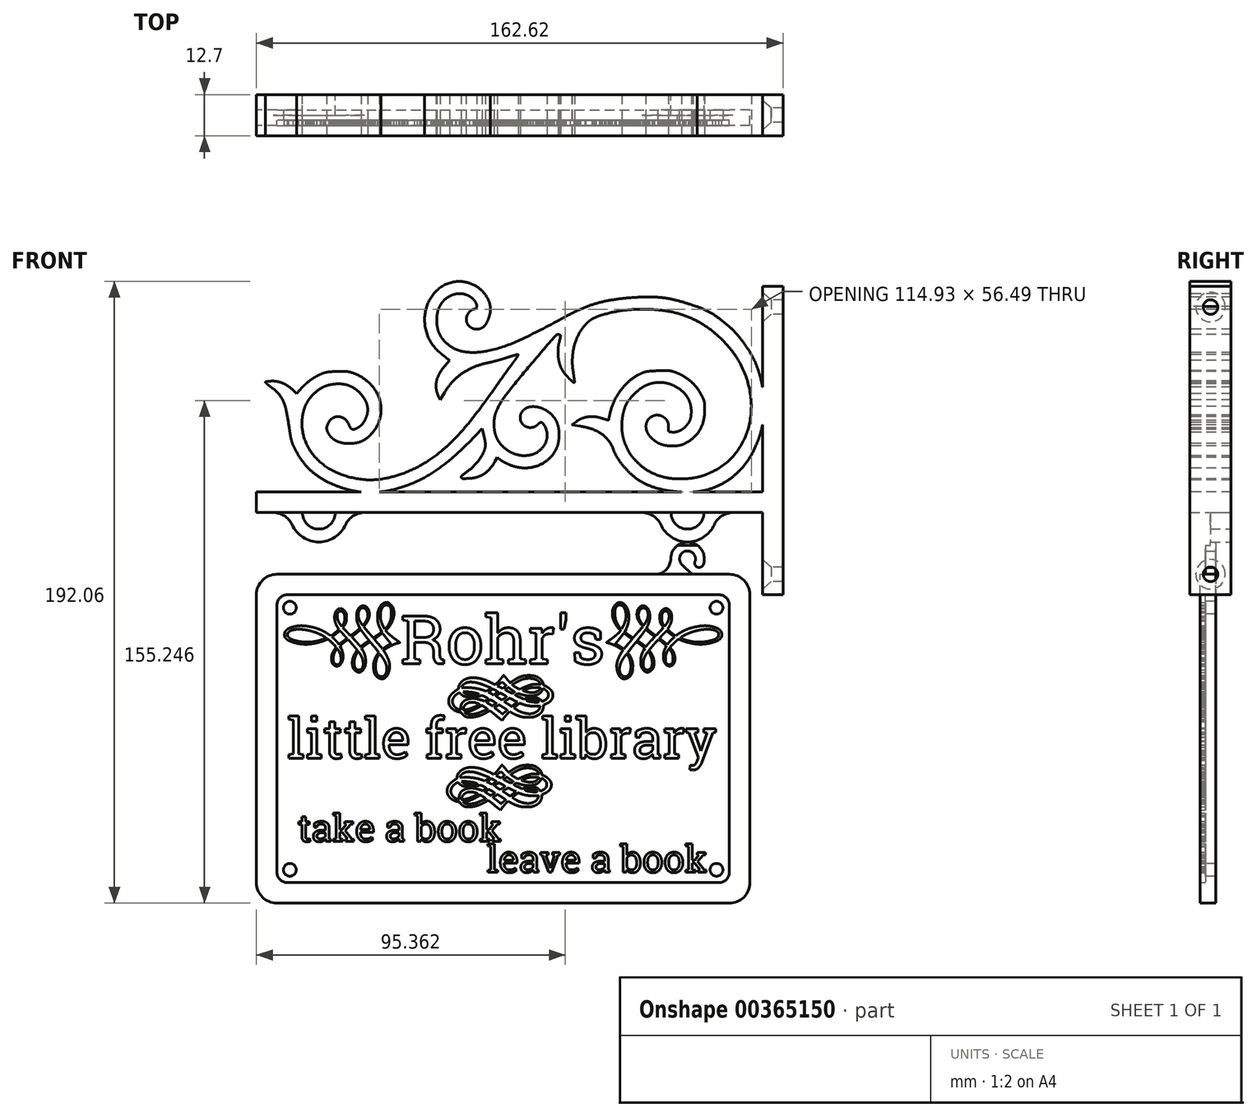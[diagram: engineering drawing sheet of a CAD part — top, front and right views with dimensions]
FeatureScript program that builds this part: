
annotation { "Feature Type Name" : "Feature", "Feature Type Description" : "" }
export const myFeature = defineFeature(function(context is Context, id is Id, definition is map)
    precondition{}
    {
        {
            var Q0;
            Q0=qCreatedBy(makeId("Front.planeOp"),FACE);
            var sketch = newSketch(context, id + "F0", { "sketchPlane" : qUnion([Q0])});
            skLineSegment(sketch, "E0.bottom", {"start": v(-69.85, 50.8) * mm, "end": v(69.85, 50.8) * mm});
            skLineSegment(sketch, "E0.top", {"start": v(-69.85, -50.8) * mm, "end": v(69.85, -50.8) * mm});
            skLineSegment(sketch, "E0.left", {"start": v(-76.2, 44.45) * mm, "end": v(-76.2, -44.45) * mm});
            skLineSegment(sketch, "E0.right", {"start": v(76.2, 44.45) * mm, "end": v(76.2, -44.45) * mm});
            skPoint(sketch, "E0.middle", {"position": v(0, 0) * mm});
            skPoint(sketch, "E1.visualSharp", {"position": v(-76.2, 50.8) * mm});
            skArc(sketch, "E1.filletArc", {"start": v(-69.85, 50.8) * mm, "mid": v(-74.34, 48.94) * mm, "end": v(-76.2, 44.45) * mm});
            skPoint(sketch, "E2.visualSharp", {"position": v(76.2, 50.8) * mm});
            skArc(sketch, "E2.filletArc", {"start": v(76.2, 44.45) * mm, "mid": v(74.34, 48.94) * mm, "end": v(69.85, 50.8) * mm});
            skPoint(sketch, "E3.visualSharp", {"position": v(76.2, -50.8) * mm});
            skArc(sketch, "E3.filletArc", {"start": v(69.85, -50.8) * mm, "mid": v(74.34, -48.94) * mm, "end": v(76.2, -44.45) * mm});
            skPoint(sketch, "E4.visualSharp", {"position": v(-76.2, -50.8) * mm});
            skArc(sketch, "E4.filletArc", {"start": v(-76.2, -44.45) * mm, "mid": v(-74.34, -48.94) * mm, "end": v(-69.85, -50.8) * mm});
            skSolve(sketch);
        }
        {
            var Q0;
            Q0=makeQuery(id+"F0.imprint","IMPRINT",FACE,{"disambiguationData":[TD([[makeQuery(id+"F0.imprint","IMPRINT",EDGE,{"derivedFrom":sQuery(id+"F0.wireOp",EDGE,"E0.bottom")}),-1.0]])]});
            extrude(context, id + "F1", {"entities" : qUnion([Q0]), "endBound" : BoundingType.SYMMETRIC, "depth" : 3.17 * mm, "offsetDistance" : 25.4 * mm});
        }
        {
            var Q0;
            Q0=makeQuery(id+"F1.opExtrude","CAP_FACE",FACE,{"disambiguationData":[OSD([sQuery(id+"F0.wireOp",EDGE,"E0.bottom"),sQuery(id+"F0.wireOp",EDGE,"E0.top"),sQuery(id+"F0.wireOp",EDGE,"E0.left"),sQuery(id+"F0.wireOp",EDGE,"E0.right"),sQuery(id+"F0.wireOp",EDGE,"E1.filletArc"),sQuery(id+"F0.wireOp",EDGE,"E2.filletArc"),sQuery(id+"F0.wireOp",EDGE,"E3.filletArc"),sQuery(id+"F0.wireOp",EDGE,"E4.filletArc")])],"isStart":false});
            var sketch = newSketch(context, id + "F2", { "sketchPlane" : qUnion([Q0])});
            skLineSegment(sketch, "E5.bottom", {"start": v(-66.67, 44.45) * mm, "end": v(66.67, 44.45) * mm});
            skLineSegment(sketch, "E5.top", {"start": v(-66.67, -44.45) * mm, "end": v(66.67, -44.45) * mm});
            skLineSegment(sketch, "E5.left", {"start": v(-69.85, 41.28) * mm, "end": v(-69.85, -41.27) * mm});
            skLineSegment(sketch, "E5.right", {"start": v(69.85, 41.28) * mm, "end": v(69.85, -41.27) * mm});
            skPoint(sketch, "E5.middle", {"position": v(0, 0) * mm});
            skPoint(sketch, "E6.visualSharp", {"position": v(-69.85, 44.45) * mm});
            skArc(sketch, "E6.filletArc", {"start": v(-66.67, 44.45) * mm, "mid": v(-68.92, 43.52) * mm, "end": v(-69.85, 41.28) * mm});
            skPoint(sketch, "E7.visualSharp", {"position": v(69.85, 44.45) * mm});
            skArc(sketch, "E7.filletArc", {"start": v(69.85, 41.28) * mm, "mid": v(68.92, 43.52) * mm, "end": v(66.67, 44.45) * mm});
            skPoint(sketch, "E8.visualSharp", {"position": v(69.85, -44.45) * mm});
            skArc(sketch, "E8.filletArc", {"start": v(66.67, -44.45) * mm, "mid": v(68.92, -43.52) * mm, "end": v(69.85, -41.27) * mm});
            skPoint(sketch, "E9.visualSharp", {"position": v(-69.85, -44.45) * mm});
            skArc(sketch, "E9.filletArc", {"start": v(-69.85, -41.27) * mm, "mid": v(-68.92, -43.52) * mm, "end": v(-66.67, -44.45) * mm});
            skSolve(sketch);
        }
        {
            var Q0;
            Q0=makeQuery(id+"F2.imprint","IMPRINT",FACE,{"disambiguationData":[TD([[makeQuery(id+"F2.imprint","IMPRINT",EDGE,{"derivedFrom":sQuery(id+"F2.wireOp",EDGE,"E5.bottom")}),1.0]])]});
            extrude(context, id + "F3", {"entities" : qUnion([Q0]), "operationType" : NewBodyOperationType.ADD, "depth" : 1.59 * mm, "offsetDistance" : 25.4 * mm});
        }
        {
            var Q0;
            Q0=makeQuery(id+"F1.opExtrude","CAP_FACE",FACE,{"disambiguationData":[OSD([sQuery(id+"F0.wireOp",EDGE,"E0.bottom"),sQuery(id+"F0.wireOp",EDGE,"E0.top"),sQuery(id+"F0.wireOp",EDGE,"E0.left"),sQuery(id+"F0.wireOp",EDGE,"E0.right"),sQuery(id+"F0.wireOp",EDGE,"E1.filletArc"),sQuery(id+"F0.wireOp",EDGE,"E2.filletArc"),sQuery(id+"F0.wireOp",EDGE,"E3.filletArc"),sQuery(id+"F0.wireOp",EDGE,"E4.filletArc")])],"isStart":false});
            var sketch = newSketch(context, id + "F4", { "sketchPlane" : qUnion([Q0])});
            skLineSegment(sketch, "E10", {"start": v(0, 0) * mm, "end": v(0, 25.75) * mm, "construction": true});
            skArc(sketch, "E11", {"start": v(-36.9, 41.88) * mm, "mid": v(-37.36, 41.59) * mm, "end": v(-37.75, 41.2) * mm});
            skArc(sketch, "E12", {"start": v(-37.75, 41.2) * mm, "mid": v(-38.1, 40.67) * mm, "end": v(-38.38, 40.1) * mm});
            skArc(sketch, "E13", {"start": v(-38.38, 40.1) * mm, "mid": v(-38.6, 39.42) * mm, "end": v(-38.75, 38.7) * mm});
            skArc(sketch, "E14", {"start": v(-38.75, 38.7) * mm, "mid": v(-38.82, 37.9) * mm, "end": v(-38.8, 37.1) * mm});
            skArc(sketch, "E15", {"start": v(-38.8, 37.1) * mm, "mid": v(-38.78, 36.68) * mm, "end": v(-38.72, 36.26) * mm});
            skArc(sketch, "E16", {"start": v(-38.72, 36.26) * mm, "mid": v(-38.65, 35.87) * mm, "end": v(-38.56, 35.49) * mm});
            skArc(sketch, "E17", {"start": v(-38.56, 35.49) * mm, "mid": v(-38.44, 35.1) * mm, "end": v(-38.3, 34.7) * mm});
            skArc(sketch, "E18", {"start": v(-38.3, 34.7) * mm, "mid": v(-38.1, 34.27) * mm, "end": v(-37.9, 33.83) * mm});
            skLineSegment(sketch, "E19", {"start": v(-37.9, 33.83) * mm, "end": v(-37.5, 32.99) * mm});
            skLineSegment(sketch, "E20", {"start": v(-37.5, 32.99) * mm, "end": v(-37.74, 32.8) * mm});
            skArc(sketch, "E21", {"start": v(-37.74, 32.8) * mm, "mid": v(-38, 32.6) * mm, "end": v(-38.27, 32.4) * mm});
            skArc(sketch, "E22", {"start": v(-38.27, 32.4) * mm, "mid": v(-38.7, 32.12) * mm, "end": v(-39.12, 31.84) * mm});
            skArc(sketch, "E23", {"start": v(-39.12, 31.84) * mm, "mid": v(-39.59, 31.53) * mm, "end": v(-40.05, 31.23) * mm});
            skArc(sketch, "E24", {"start": v(-40.05, 31.23) * mm, "mid": v(-40.1, 31.21) * mm, "end": v(-40.15, 31.22) * mm});
            skArc(sketch, "E25", {"start": v(-40.15, 31.22) * mm, "mid": v(-40.18, 31.23) * mm, "end": v(-40.2, 31.25) * mm});
            skArc(sketch, "E26", {"start": v(-40.2, 31.25) * mm, "mid": v(-40.41, 31.5) * mm, "end": v(-40.62, 31.74) * mm});
            skArc(sketch, "E27", {"start": v(-40.62, 31.74) * mm, "mid": v(-40.86, 32.01) * mm, "end": v(-41.1, 32.29) * mm});
            skArc(sketch, "E28", {"start": v(-41.1, 32.29) * mm, "mid": v(-41.38, 32.61) * mm, "end": v(-41.66, 32.94) * mm});
            skLineSegment(sketch, "E29", {"start": v(-41.66, 32.94) * mm, "end": v(-43.09, 34.63) * mm});
            skLineSegment(sketch, "E30", {"start": v(-43.09, 34.63) * mm, "end": v(-42.74, 35.06) * mm});
            skArc(sketch, "E31", {"start": v(-42.74, 35.06) * mm, "mid": v(-42.33, 35.6) * mm, "end": v(-41.96, 36.17) * mm});
            skArc(sketch, "E32", {"start": v(-41.96, 36.17) * mm, "mid": v(-41.7, 36.7) * mm, "end": v(-41.49, 37.24) * mm});
            skArc(sketch, "E33", {"start": v(-41.49, 37.24) * mm, "mid": v(-41.36, 37.75) * mm, "end": v(-41.3, 38.28) * mm});
            skArc(sketch, "E34", {"start": v(-41.3, 38.28) * mm, "mid": v(-41.32, 38.78) * mm, "end": v(-41.4, 39.28) * mm});
            skArc(sketch, "E35", {"start": v(-41.4, 39.28) * mm, "mid": v(-41.49, 39.56) * mm, "end": v(-41.6, 39.84) * mm});
            skArc(sketch, "E36", {"start": v(-41.6, 39.84) * mm, "mid": v(-41.7, 40.07) * mm, "end": v(-41.84, 40.29) * mm});
            skArc(sketch, "E37", {"start": v(-41.84, 40.29) * mm, "mid": v(-41.98, 40.47) * mm, "end": v(-42.14, 40.63) * mm});
            skArc(sketch, "E38", {"start": v(-42.14, 40.63) * mm, "mid": v(-42.32, 40.77) * mm, "end": v(-42.51, 40.88) * mm});
            skArc(sketch, "E39", {"start": v(-42.51, 40.88) * mm, "mid": v(-42.7, 40.96) * mm, "end": v(-42.9, 41.03) * mm});
            skArc(sketch, "E40", {"start": v(-42.9, 41.03) * mm, "mid": v(-43.07, 41.06) * mm, "end": v(-43.25, 41.07) * mm});
            skArc(sketch, "E41", {"start": v(-43.25, 41.07) * mm, "mid": v(-43.42, 41.06) * mm, "end": v(-43.6, 41.02) * mm});
            skArc(sketch, "E42", {"start": v(-43.6, 41.02) * mm, "mid": v(-43.8, 40.95) * mm, "end": v(-43.99, 40.86) * mm});
            skArc(sketch, "E43", {"start": v(-43.99, 40.86) * mm, "mid": v(-44.28, 40.67) * mm, "end": v(-44.53, 40.41) * mm});
            skArc(sketch, "E44", {"start": v(-44.53, 40.41) * mm, "mid": v(-44.76, 40.08) * mm, "end": v(-44.95, 39.7) * mm});
            skArc(sketch, "E45", {"start": v(-44.95, 39.7) * mm, "mid": v(-45.1, 39.26) * mm, "end": v(-45.2, 38.79) * mm});
            skArc(sketch, "E46", {"start": v(-45.2, 38.79) * mm, "mid": v(-45.27, 38.25) * mm, "end": v(-45.3, 37.7) * mm});
            skArc(sketch, "E47", {"start": v(-45.3, 37.7) * mm, "mid": v(-45.29, 37.34) * mm, "end": v(-45.26, 36.98) * mm});
            skArc(sketch, "E48", {"start": v(-45.26, 36.98) * mm, "mid": v(-45.2, 36.64) * mm, "end": v(-45.14, 36.3) * mm});
            skArc(sketch, "E49", {"start": v(-45.14, 36.3) * mm, "mid": v(-45.04, 35.97) * mm, "end": v(-44.93, 35.63) * mm});
            skArc(sketch, "E50", {"start": v(-44.93, 35.63) * mm, "mid": v(-44.78, 35.27) * mm, "end": v(-44.6, 34.9) * mm});
            skLineSegment(sketch, "E51", {"start": v(-44.6, 34.9) * mm, "end": v(-44.22, 34.12) * mm});
            skLineSegment(sketch, "E52", {"start": v(-44.22, 34.12) * mm, "end": v(-44.73, 33.68) * mm});
            skArc(sketch, "E53", {"start": v(-44.73, 33.68) * mm, "mid": v(-44.86, 33.57) * mm, "end": v(-45, 33.47) * mm});
            skArc(sketch, "E54", {"start": v(-45, 33.47) * mm, "mid": v(-45.19, 33.32) * mm, "end": v(-45.38, 33.16) * mm});
            skArc(sketch, "E55", {"start": v(-45.38, 33.16) * mm, "mid": v(-45.59, 33) * mm, "end": v(-45.8, 32.83) * mm});
            skArc(sketch, "E56", {"start": v(-45.8, 32.83) * mm, "mid": v(-46, 32.68) * mm, "end": v(-46.2, 32.53) * mm});
            skArc(sketch, "E57", {"start": v(-46.2, 32.53) * mm, "mid": v(-46.45, 32.34) * mm, "end": v(-46.7, 32.16) * mm});
            skArc(sketch, "E58", {"start": v(-46.7, 32.16) * mm, "mid": v(-46.84, 32.07) * mm, "end": v(-46.98, 31.98) * mm});
            skArc(sketch, "E59", {"start": v(-46.98, 31.98) * mm, "mid": v(-47.07, 31.93) * mm, "end": v(-47.17, 31.9) * mm});
            skArc(sketch, "E60", {"start": v(-47.17, 31.9) * mm, "mid": v(-47.22, 31.9) * mm, "end": v(-47.27, 31.93) * mm});
            skArc(sketch, "E61", {"start": v(-47.27, 31.93) * mm, "mid": v(-47.31, 31.97) * mm, "end": v(-47.36, 32.02) * mm});
            skArc(sketch, "E62", {"start": v(-47.36, 32.02) * mm, "mid": v(-47.51, 32.19) * mm, "end": v(-47.67, 32.35) * mm});
            skArc(sketch, "E63", {"start": v(-47.67, 32.35) * mm, "mid": v(-47.85, 32.55) * mm, "end": v(-48.04, 32.75) * mm});
            skArc(sketch, "E64", {"start": v(-48.04, 32.75) * mm, "mid": v(-48.25, 32.97) * mm, "end": v(-48.46, 33.2) * mm});
            skLineSegment(sketch, "E65", {"start": v(-48.46, 33.2) * mm, "end": v(-49.53, 34.33) * mm});
            skLineSegment(sketch, "E66", {"start": v(-49.53, 34.33) * mm, "end": v(-49.19, 34.78) * mm});
            skArc(sketch, "E67", {"start": v(-49.19, 34.78) * mm, "mid": v(-48.98, 35.07) * mm, "end": v(-48.8, 35.37) * mm});
            skArc(sketch, "E68", {"start": v(-48.8, 35.37) * mm, "mid": v(-48.67, 35.66) * mm, "end": v(-48.56, 35.96) * mm});
            skArc(sketch, "E69", {"start": v(-48.56, 35.96) * mm, "mid": v(-48.48, 36.29) * mm, "end": v(-48.42, 36.62) * mm});
            skArc(sketch, "E70", {"start": v(-48.42, 36.62) * mm, "mid": v(-48.39, 37.04) * mm, "end": v(-48.38, 37.45) * mm});
            skArc(sketch, "E71", {"start": v(-48.38, 37.45) * mm, "mid": v(-48.38, 37.75) * mm, "end": v(-48.38, 38.05) * mm});
            skArc(sketch, "E72", {"start": v(-48.38, 38.05) * mm, "mid": v(-48.4, 38.23) * mm, "end": v(-48.42, 38.4) * mm});
            skArc(sketch, "E73", {"start": v(-48.42, 38.4) * mm, "mid": v(-48.44, 38.54) * mm, "end": v(-48.48, 38.68) * mm});
            skArc(sketch, "E74", {"start": v(-48.48, 38.68) * mm, "mid": v(-48.54, 38.82) * mm, "end": v(-48.6, 38.97) * mm});
            skArc(sketch, "E75", {"start": v(-48.6, 38.97) * mm, "mid": v(-48.73, 39.18) * mm, "end": v(-48.85, 39.38) * mm});
            skArc(sketch, "E76", {"start": v(-48.85, 39.38) * mm, "mid": v(-48.97, 39.54) * mm, "end": v(-49.1, 39.68) * mm});
            skArc(sketch, "E77", {"start": v(-49.1, 39.68) * mm, "mid": v(-49.23, 39.8) * mm, "end": v(-49.37, 39.9) * mm});
            skArc(sketch, "E78", {"start": v(-49.37, 39.9) * mm, "mid": v(-49.54, 40.01) * mm, "end": v(-49.72, 40.1) * mm});
            skArc(sketch, "E79", {"start": v(-49.72, 40.1) * mm, "mid": v(-49.92, 40.18) * mm, "end": v(-50.13, 40.23) * mm});
            skArc(sketch, "E80", {"start": v(-50.13, 40.23) * mm, "mid": v(-50.32, 40.24) * mm, "end": v(-50.5, 40.23) * mm});
            skArc(sketch, "E81", {"start": v(-50.5, 40.23) * mm, "mid": v(-50.7, 40.17) * mm, "end": v(-50.87, 40.09) * mm});
            skArc(sketch, "E82", {"start": v(-50.87, 40.09) * mm, "mid": v(-51.07, 39.96) * mm, "end": v(-51.25, 39.81) * mm});
            skArc(sketch, "E83", {"start": v(-51.25, 39.81) * mm, "mid": v(-51.64, 39.34) * mm, "end": v(-51.89, 38.79) * mm});
            skArc(sketch, "E84", {"start": v(-51.89, 38.79) * mm, "mid": v(-52.04, 38.07) * mm, "end": v(-52.07, 37.34) * mm});
            skArc(sketch, "E85", {"start": v(-52.07, 37.34) * mm, "mid": v(-51.98, 36.52) * mm, "end": v(-51.77, 35.73) * mm});
            skArc(sketch, "E86", {"start": v(-51.77, 35.73) * mm, "mid": v(-51.46, 34.97) * mm, "end": v(-51.04, 34.26) * mm});
            skLineSegment(sketch, "E87", {"start": v(-51.04, 34.26) * mm, "end": v(-50.7, 33.78) * mm});
            skLineSegment(sketch, "E88", {"start": v(-50.7, 33.78) * mm, "end": v(-51.26, 33.3) * mm});
            skArc(sketch, "E89", {"start": v(-51.26, 33.3) * mm, "mid": v(-51.39, 33.18) * mm, "end": v(-51.52, 33.07) * mm});
            skArc(sketch, "E90", {"start": v(-51.52, 33.07) * mm, "mid": v(-51.69, 32.94) * mm, "end": v(-51.85, 32.8) * mm});
            skArc(sketch, "E91", {"start": v(-51.85, 32.8) * mm, "mid": v(-52.03, 32.67) * mm, "end": v(-52.2, 32.54) * mm});
            skArc(sketch, "E92", {"start": v(-52.2, 32.54) * mm, "mid": v(-52.37, 32.42) * mm, "end": v(-52.52, 32.3) * mm});
            skLineSegment(sketch, "E93", {"start": v(-52.52, 32.3) * mm, "end": v(-53.25, 31.8) * mm});
            skLineSegment(sketch, "E94", {"start": v(-53.25, 31.8) * mm, "end": v(-54.37, 32.55) * mm});
            skArc(sketch, "E95", {"start": v(-54.37, 32.55) * mm, "mid": v(-55.03, 32.97) * mm, "end": v(-55.72, 33.33) * mm});
            skArc(sketch, "E96", {"start": v(-55.72, 33.33) * mm, "mid": v(-56.45, 33.67) * mm, "end": v(-57.2, 33.95) * mm});
            skArc(sketch, "E97", {"start": v(-57.2, 33.95) * mm, "mid": v(-58.01, 34.22) * mm, "end": v(-58.85, 34.43) * mm});
            skArc(sketch, "E98", {"start": v(-58.85, 34.43) * mm, "mid": v(-59.79, 34.63) * mm, "end": v(-60.73, 34.79) * mm});
            skArc(sketch, "E99", {"start": v(-60.73, 34.79) * mm, "mid": v(-61.26, 34.85) * mm, "end": v(-61.78, 34.9) * mm});
            skArc(sketch, "E100", {"start": v(-61.78, 34.9) * mm, "mid": v(-62.29, 34.9) * mm, "end": v(-62.79, 34.9) * mm});
            skArc(sketch, "E101", {"start": v(-62.79, 34.9) * mm, "mid": v(-63.28, 34.86) * mm, "end": v(-63.77, 34.8) * mm});
            skArc(sketch, "E102", {"start": v(-63.77, 34.8) * mm, "mid": v(-64.28, 34.7) * mm, "end": v(-64.78, 34.6) * mm});
            skArc(sketch, "E103", {"start": v(-64.78, 34.6) * mm, "mid": v(-65.27, 34.45) * mm, "end": v(-65.75, 34.3) * mm});
            skArc(sketch, "E104", {"start": v(-65.75, 34.3) * mm, "mid": v(-66.11, 34.14) * mm, "end": v(-66.46, 33.95) * mm});
            skArc(sketch, "E105", {"start": v(-66.46, 33.95) * mm, "mid": v(-66.73, 33.75) * mm, "end": v(-66.98, 33.52) * mm});
            skArc(sketch, "E106", {"start": v(-66.98, 33.52) * mm, "mid": v(-67.19, 33.26) * mm, "end": v(-67.36, 32.98) * mm});
            skArc(sketch, "E107", {"start": v(-67.36, 32.98) * mm, "mid": v(-67.45, 32.78) * mm, "end": v(-67.5, 32.57) * mm});
            skArc(sketch, "E108", {"start": v(-67.5, 32.57) * mm, "mid": v(-67.53, 32.32) * mm, "end": v(-67.54, 32.06) * mm});
            skArc(sketch, "E109", {"start": v(-67.54, 32.06) * mm, "mid": v(-67.52, 31.82) * mm, "end": v(-67.48, 31.57) * mm});
            skArc(sketch, "E110", {"start": v(-67.48, 31.57) * mm, "mid": v(-67.43, 31.4) * mm, "end": v(-67.33, 31.23) * mm});
            skArc(sketch, "E111", {"start": v(-67.33, 31.23) * mm, "mid": v(-66.8, 30.66) * mm, "end": v(-66.12, 30.26) * mm});
            skArc(sketch, "E112", {"start": v(-66.12, 30.26) * mm, "mid": v(-65.05, 29.85) * mm, "end": v(-63.95, 29.55) * mm});
            skArc(sketch, "E113", {"start": v(-63.95, 29.55) * mm, "mid": v(-62.7, 29.31) * mm, "end": v(-61.44, 29.2) * mm});
            skArc(sketch, "E114", {"start": v(-61.44, 29.2) * mm, "mid": v(-60.25, 29.2) * mm, "end": v(-59.07, 29.33) * mm});
            skArc(sketch, "E115", {"start": v(-59.07, 29.33) * mm, "mid": v(-58.52, 29.42) * mm, "end": v(-57.97, 29.53) * mm});
            skArc(sketch, "E116", {"start": v(-57.97, 29.53) * mm, "mid": v(-57.44, 29.65) * mm, "end": v(-56.92, 29.78) * mm});
            skArc(sketch, "E117", {"start": v(-56.92, 29.78) * mm, "mid": v(-56.44, 29.92) * mm, "end": v(-55.96, 30.07) * mm});
            skArc(sketch, "E118", {"start": v(-55.96, 30.07) * mm, "mid": v(-55.53, 30.23) * mm, "end": v(-55.1, 30.4) * mm});
            skArc(sketch, "E119", {"start": v(-55.1, 30.4) * mm, "mid": v(-54.8, 30.52) * mm, "end": v(-54.5, 30.64) * mm});
            skArc(sketch, "E120", {"start": v(-54.5, 30.64) * mm, "mid": v(-54.37, 30.69) * mm, "end": v(-54.24, 30.72) * mm});
            skArc(sketch, "E121", {"start": v(-54.24, 30.72) * mm, "mid": v(-54.16, 30.72) * mm, "end": v(-54.09, 30.7) * mm});
            skArc(sketch, "E122", {"start": v(-54.09, 30.7) * mm, "mid": v(-54, 30.67) * mm, "end": v(-53.93, 30.62) * mm});
            skArc(sketch, "E123", {"start": v(-53.93, 30.62) * mm, "mid": v(-53.71, 30.43) * mm, "end": v(-53.5, 30.24) * mm});
            skArc(sketch, "E124", {"start": v(-53.5, 30.24) * mm, "mid": v(-53.25, 30) * mm, "end": v(-53, 29.77) * mm});
            skArc(sketch, "E125", {"start": v(-53, 29.77) * mm, "mid": v(-52.74, 29.53) * mm, "end": v(-52.5, 29.28) * mm});
            skArc(sketch, "E126", {"start": v(-52.5, 29.28) * mm, "mid": v(-52.29, 29.07) * mm, "end": v(-52.09, 28.85) * mm});
            skLineSegment(sketch, "E127", {"start": v(-52.09, 28.85) * mm, "end": v(-51.55, 28.28) * mm});
            skLineSegment(sketch, "E128", {"start": v(-51.55, 28.28) * mm, "end": v(-51.96, 27.74) * mm});
            skArc(sketch, "E129", {"start": v(-51.96, 27.74) * mm, "mid": v(-52.24, 27.34) * mm, "end": v(-52.49, 26.92) * mm});
            skArc(sketch, "E130", {"start": v(-52.49, 26.92) * mm, "mid": v(-52.69, 26.5) * mm, "end": v(-52.84, 26.06) * mm});
            skArc(sketch, "E131", {"start": v(-52.84, 26.06) * mm, "mid": v(-52.96, 25.63) * mm, "end": v(-53.02, 25.2) * mm});
            skArc(sketch, "E132", {"start": v(-53.02, 25.2) * mm, "mid": v(-53.04, 24.75) * mm, "end": v(-53.02, 24.31) * mm});
            skArc(sketch, "E133", {"start": v(-53.02, 24.31) * mm, "mid": v(-52.93, 23.82) * mm, "end": v(-52.75, 23.34) * mm});
            skArc(sketch, "E134", {"start": v(-52.75, 23.34) * mm, "mid": v(-52.52, 22.97) * mm, "end": v(-52.2, 22.68) * mm});
            skArc(sketch, "E135", {"start": v(-52.2, 22.68) * mm, "mid": v(-51.85, 22.5) * mm, "end": v(-51.46, 22.43) * mm});
            skArc(sketch, "E136", {"start": v(-51.46, 22.43) * mm, "mid": v(-51.04, 22.48) * mm, "end": v(-50.64, 22.62) * mm});
            skArc(sketch, "E137", {"start": v(-50.64, 22.62) * mm, "mid": v(-50.38, 22.8) * mm, "end": v(-50.17, 23.03) * mm});
            skArc(sketch, "E138", {"start": v(-50.17, 23.03) * mm, "mid": v(-49.95, 23.36) * mm, "end": v(-49.78, 23.7) * mm});
            skArc(sketch, "E139", {"start": v(-49.78, 23.7) * mm, "mid": v(-49.63, 24.13) * mm, "end": v(-49.52, 24.57) * mm});
            skArc(sketch, "E140", {"start": v(-49.52, 24.57) * mm, "mid": v(-49.45, 25.03) * mm, "end": v(-49.43, 25.5) * mm});
            skArc(sketch, "E141", {"start": v(-49.43, 25.5) * mm, "mid": v(-49.45, 25.8) * mm, "end": v(-49.48, 26.1) * mm});
            skArc(sketch, "E142", {"start": v(-49.48, 26.1) * mm, "mid": v(-49.55, 26.46) * mm, "end": v(-49.64, 26.82) * mm});
            skArc(sketch, "E143", {"start": v(-49.64, 26.82) * mm, "mid": v(-49.74, 27.19) * mm, "end": v(-49.86, 27.55) * mm});
            skArc(sketch, "E144", {"start": v(-49.86, 27.55) * mm, "mid": v(-49.99, 27.87) * mm, "end": v(-50.13, 28.18) * mm});
            skLineSegment(sketch, "E145", {"start": v(-50.13, 28.18) * mm, "end": v(-50.42, 28.74) * mm});
            skLineSegment(sketch, "E146", {"start": v(-50.42, 28.74) * mm, "end": v(-50.05, 29.04) * mm});
            skArc(sketch, "E147", {"start": v(-50.05, 29.04) * mm, "mid": v(-49.95, 29.12) * mm, "end": v(-49.85, 29.2) * mm});
            skArc(sketch, "E148", {"start": v(-49.85, 29.2) * mm, "mid": v(-49.7, 29.33) * mm, "end": v(-49.54, 29.46) * mm});
            skArc(sketch, "E149", {"start": v(-49.54, 29.46) * mm, "mid": v(-49.36, 29.6) * mm, "end": v(-49.17, 29.74) * mm});
            skArc(sketch, "E150", {"start": v(-49.17, 29.74) * mm, "mid": v(-49, 29.88) * mm, "end": v(-48.81, 30.02) * mm});
            skLineSegment(sketch, "E151", {"start": v(-48.81, 30.02) * mm, "end": v(-47.94, 30.7) * mm});
            skLineSegment(sketch, "E152", {"start": v(-47.94, 30.7) * mm, "end": v(-47.2, 29.86) * mm});
            skArc(sketch, "E153", {"start": v(-47.2, 29.86) * mm, "mid": v(-46.91, 29.54) * mm, "end": v(-46.63, 29.22) * mm});
            skArc(sketch, "E154", {"start": v(-46.63, 29.22) * mm, "mid": v(-46.32, 28.87) * mm, "end": v(-46.02, 28.52) * mm});
            skArc(sketch, "E155", {"start": v(-46.02, 28.52) * mm, "mid": v(-45.75, 28.2) * mm, "end": v(-45.48, 27.89) * mm});
            skArc(sketch, "E156", {"start": v(-45.48, 27.89) * mm, "mid": v(-45.34, 27.72) * mm, "end": v(-45.2, 27.55) * mm});
            skArc(sketch, "E157", {"start": v(-45.2, 27.55) * mm, "mid": v(-45.18, 27.5) * mm, "end": v(-45.16, 27.43) * mm});
            skArc(sketch, "E158", {"start": v(-45.16, 27.43) * mm, "mid": v(-45.16, 27.36) * mm, "end": v(-45.18, 27.3) * mm});
            skArc(sketch, "E159", {"start": v(-45.18, 27.3) * mm, "mid": v(-45.22, 27.2) * mm, "end": v(-45.27, 27.1) * mm});
            skArc(sketch, "E160", {"start": v(-45.27, 27.1) * mm, "mid": v(-45.38, 26.93) * mm, "end": v(-45.5, 26.76) * mm});
            skArc(sketch, "E161", {"start": v(-45.5, 26.76) * mm, "mid": v(-45.78, 26.3) * mm, "end": v(-46.03, 25.84) * mm});
            skArc(sketch, "E162", {"start": v(-46.03, 25.84) * mm, "mid": v(-46.23, 25.39) * mm, "end": v(-46.39, 24.92) * mm});
            skArc(sketch, "E163", {"start": v(-46.39, 24.92) * mm, "mid": v(-46.5, 24.46) * mm, "end": v(-46.57, 23.99) * mm});
            skArc(sketch, "E164", {"start": v(-46.57, 23.99) * mm, "mid": v(-46.6, 23.5) * mm, "end": v(-46.58, 23.02) * mm});
            skArc(sketch, "E165", {"start": v(-46.58, 23.02) * mm, "mid": v(-46.53, 22.6) * mm, "end": v(-46.43, 22.17) * mm});
            skArc(sketch, "E166", {"start": v(-46.43, 22.17) * mm, "mid": v(-46.28, 21.81) * mm, "end": v(-46.09, 21.48) * mm});
            skArc(sketch, "E167", {"start": v(-46.09, 21.48) * mm, "mid": v(-45.86, 21.2) * mm, "end": v(-45.58, 20.95) * mm});
            skArc(sketch, "E168", {"start": v(-45.58, 20.95) * mm, "mid": v(-45.26, 20.75) * mm, "end": v(-44.91, 20.6) * mm});
            skArc(sketch, "E169", {"start": v(-44.91, 20.6) * mm, "mid": v(-44.64, 20.54) * mm, "end": v(-44.35, 20.54) * mm});
            skArc(sketch, "E170", {"start": v(-44.35, 20.54) * mm, "mid": v(-44.06, 20.61) * mm, "end": v(-43.8, 20.74) * mm});
            skArc(sketch, "E171", {"start": v(-43.8, 20.74) * mm, "mid": v(-43.52, 20.95) * mm, "end": v(-43.29, 21.2) * mm});
            skArc(sketch, "E172", {"start": v(-43.29, 21.2) * mm, "mid": v(-43.05, 21.53) * mm, "end": v(-42.86, 21.9) * mm});
            skArc(sketch, "E173", {"start": v(-42.86, 21.9) * mm, "mid": v(-42.76, 22.1) * mm, "end": v(-42.67, 22.3) * mm});
            skArc(sketch, "E174", {"start": v(-42.67, 22.3) * mm, "mid": v(-42.61, 22.47) * mm, "end": v(-42.57, 22.63) * mm});
            skArc(sketch, "E175", {"start": v(-42.57, 22.63) * mm, "mid": v(-42.54, 22.82) * mm, "end": v(-42.52, 23) * mm});
            skArc(sketch, "E176", {"start": v(-42.52, 23) * mm, "mid": v(-42.5, 23.32) * mm, "end": v(-42.49, 23.64) * mm});
            skArc(sketch, "E177", {"start": v(-42.49, 23.64) * mm, "mid": v(-42.48, 24.17) * mm, "end": v(-42.51, 24.7) * mm});
            skArc(sketch, "E178", {"start": v(-42.51, 24.7) * mm, "mid": v(-42.57, 25.17) * mm, "end": v(-42.66, 25.63) * mm});
            skArc(sketch, "E179", {"start": v(-42.66, 25.63) * mm, "mid": v(-42.8, 26.07) * mm, "end": v(-42.96, 26.5) * mm});
            skArc(sketch, "E180", {"start": v(-42.96, 26.5) * mm, "mid": v(-43.18, 26.96) * mm, "end": v(-43.42, 27.4) * mm});
            skLineSegment(sketch, "E181", {"start": v(-43.42, 27.4) * mm, "end": v(-43.77, 27.97) * mm});
            skLineSegment(sketch, "E182", {"start": v(-43.77, 27.97) * mm, "end": v(-43.33, 28.34) * mm});
            skArc(sketch, "E183", {"start": v(-43.33, 28.34) * mm, "mid": v(-43.22, 28.43) * mm, "end": v(-43.1, 28.52) * mm});
            skArc(sketch, "E184", {"start": v(-43.1, 28.52) * mm, "mid": v(-42.93, 28.65) * mm, "end": v(-42.76, 28.78) * mm});
            skArc(sketch, "E185", {"start": v(-42.76, 28.78) * mm, "mid": v(-42.57, 28.93) * mm, "end": v(-42.37, 29.07) * mm});
            skArc(sketch, "E186", {"start": v(-42.37, 29.07) * mm, "mid": v(-42.19, 29.2) * mm, "end": v(-42, 29.34) * mm});
            skArc(sketch, "E187", {"start": v(-42, 29.34) * mm, "mid": v(-41.78, 29.5) * mm, "end": v(-41.55, 29.66) * mm});
            skArc(sketch, "E188", {"start": v(-41.55, 29.66) * mm, "mid": v(-41.42, 29.74) * mm, "end": v(-41.28, 29.82) * mm});
            skArc(sketch, "E189", {"start": v(-41.28, 29.82) * mm, "mid": v(-41.2, 29.86) * mm, "end": v(-41.1, 29.89) * mm});
            skArc(sketch, "E190", {"start": v(-41.1, 29.89) * mm, "mid": v(-41.05, 29.88) * mm, "end": v(-41, 29.86) * mm});
            skArc(sketch, "E191", {"start": v(-41, 29.86) * mm, "mid": v(-40.97, 29.8) * mm, "end": v(-40.93, 29.76) * mm});
            skArc(sketch, "E192", {"start": v(-40.93, 29.76) * mm, "mid": v(-40.75, 29.54) * mm, "end": v(-40.57, 29.31) * mm});
            skArc(sketch, "E193", {"start": v(-40.57, 29.31) * mm, "mid": v(-40.36, 29.05) * mm, "end": v(-40.15, 28.79) * mm});
            skArc(sketch, "E194", {"start": v(-40.15, 28.79) * mm, "mid": v(-39.9, 28.49) * mm, "end": v(-39.67, 28.2) * mm});
            skLineSegment(sketch, "E195", {"start": v(-39.67, 28.2) * mm, "end": v(-38.42, 26.65) * mm});
            skLineSegment(sketch, "E196", {"start": v(-38.42, 26.65) * mm, "end": v(-38.72, 26.28) * mm});
            skArc(sketch, "E197", {"start": v(-38.72, 26.28) * mm, "mid": v(-38.9, 26.04) * mm, "end": v(-39.05, 25.8) * mm});
            skArc(sketch, "E198", {"start": v(-39.05, 25.8) * mm, "mid": v(-39.21, 25.5) * mm, "end": v(-39.36, 25.2) * mm});
            skArc(sketch, "E199", {"start": v(-39.36, 25.2) * mm, "mid": v(-39.51, 24.87) * mm, "end": v(-39.64, 24.53) * mm});
            skArc(sketch, "E200", {"start": v(-39.64, 24.53) * mm, "mid": v(-39.76, 24.2) * mm, "end": v(-39.86, 23.87) * mm});
            skArc(sketch, "E201", {"start": v(-39.86, 23.87) * mm, "mid": v(-39.92, 23.64) * mm, "end": v(-39.97, 23.41) * mm});
            skArc(sketch, "E202", {"start": v(-39.97, 23.41) * mm, "mid": v(-40, 23.22) * mm, "end": v(-40.02, 23.02) * mm});
            skArc(sketch, "E203", {"start": v(-40.02, 23.02) * mm, "mid": v(-40.04, 22.8) * mm, "end": v(-40.04, 22.59) * mm});
            skArc(sketch, "E204", {"start": v(-40.04, 22.59) * mm, "mid": v(-40.04, 22.28) * mm, "end": v(-40.03, 21.97) * mm});
            skArc(sketch, "E205", {"start": v(-40.03, 21.97) * mm, "mid": v(-39.98, 21.37) * mm, "end": v(-39.9, 20.78) * mm});
            skArc(sketch, "E206", {"start": v(-39.9, 20.78) * mm, "mid": v(-39.78, 20.33) * mm, "end": v(-39.6, 19.9) * mm});
            skArc(sketch, "E207", {"start": v(-39.6, 19.9) * mm, "mid": v(-39.38, 19.54) * mm, "end": v(-39.11, 19.24) * mm});
            skArc(sketch, "E208", {"start": v(-39.11, 19.24) * mm, "mid": v(-38.78, 18.97) * mm, "end": v(-38.41, 18.75) * mm});
            skArc(sketch, "E209", {"start": v(-38.41, 18.75) * mm, "mid": v(-37.94, 18.57) * mm, "end": v(-37.45, 18.49) * mm});
            skArc(sketch, "E210", {"start": v(-37.45, 18.49) * mm, "mid": v(-37.01, 18.53) * mm, "end": v(-36.6, 18.7) * mm});
            skArc(sketch, "E211", {"start": v(-36.6, 18.7) * mm, "mid": v(-36.2, 19) * mm, "end": v(-35.9, 19.39) * mm});
            skArc(sketch, "E212", {"start": v(-35.9, 19.39) * mm, "mid": v(-35.6, 19.96) * mm, "end": v(-35.35, 20.55) * mm});
            skArc(sketch, "E213", {"start": v(-35.35, 20.55) * mm, "mid": v(-35.23, 20.97) * mm, "end": v(-35.15, 21.4) * mm});
            skArc(sketch, "E214", {"start": v(-35.15, 21.4) * mm, "mid": v(-35.1, 21.86) * mm, "end": v(-35.07, 22.33) * mm});
            skArc(sketch, "E215", {"start": v(-35.07, 22.33) * mm, "mid": v(-35.08, 22.79) * mm, "end": v(-35.12, 23.25) * mm});
            skArc(sketch, "E216", {"start": v(-35.12, 23.25) * mm, "mid": v(-35.2, 23.67) * mm, "end": v(-35.3, 24.09) * mm});
            skArc(sketch, "E217", {"start": v(-35.3, 24.09) * mm, "mid": v(-35.42, 24.4) * mm, "end": v(-35.54, 24.72) * mm});
            skArc(sketch, "E218", {"start": v(-35.54, 24.72) * mm, "mid": v(-35.7, 25.09) * mm, "end": v(-35.88, 25.45) * mm});
            skArc(sketch, "E219", {"start": v(-35.88, 25.45) * mm, "mid": v(-36.06, 25.82) * mm, "end": v(-36.25, 26.17) * mm});
            skArc(sketch, "E220", {"start": v(-36.25, 26.17) * mm, "mid": v(-36.43, 26.47) * mm, "end": v(-36.61, 26.76) * mm});
            skArc(sketch, "E221", {"start": v(-36.61, 26.76) * mm, "mid": v(-36.67, 26.85) * mm, "end": v(-36.73, 26.94) * mm});
            skArc(sketch, "E222", {"start": v(-36.73, 26.94) * mm, "mid": v(-36.78, 27.02) * mm, "end": v(-36.83, 27.1) * mm});
            skArc(sketch, "E223", {"start": v(-36.83, 27.1) * mm, "mid": v(-36.87, 27.17) * mm, "end": v(-36.91, 27.24) * mm});
            skArc(sketch, "E224", {"start": v(-36.91, 27.24) * mm, "mid": v(-36.92, 27.26) * mm, "end": v(-36.92, 27.28) * mm});
            skArc(sketch, "E225", {"start": v(-36.92, 27.28) * mm, "mid": v(-36.9, 27.36) * mm, "end": v(-36.85, 27.42) * mm});
            skArc(sketch, "E226", {"start": v(-36.85, 27.42) * mm, "mid": v(-36.44, 27.68) * mm, "end": v(-36.03, 27.94) * mm});
            skArc(sketch, "E227", {"start": v(-36.03, 27.94) * mm, "mid": v(-35.61, 28.2) * mm, "end": v(-35.2, 28.44) * mm});
            skArc(sketch, "E228", {"start": v(-35.2, 28.44) * mm, "mid": v(-34.83, 28.64) * mm, "end": v(-34.46, 28.83) * mm});
            skArc(sketch, "E229", {"start": v(-34.46, 28.83) * mm, "mid": v(-34.25, 28.92) * mm, "end": v(-34.05, 29.02) * mm});
            skArc(sketch, "E230", {"start": v(-34.05, 29.02) * mm, "mid": v(-33.81, 29.11) * mm, "end": v(-33.57, 29.2) * mm});
            skArc(sketch, "E231", {"start": v(-33.57, 29.2) * mm, "mid": v(-33.34, 29.3) * mm, "end": v(-33.11, 29.38) * mm});
            skArc(sketch, "E232", {"start": v(-33.11, 29.38) * mm, "mid": v(-32.92, 29.44) * mm, "end": v(-32.74, 29.5) * mm});
            skArc(sketch, "E233", {"start": v(-32.74, 29.5) * mm, "mid": v(-32.58, 29.53) * mm, "end": v(-32.42, 29.58) * mm});
            skArc(sketch, "E234", {"start": v(-32.42, 29.58) * mm, "mid": v(-32.3, 29.61) * mm, "end": v(-32.16, 29.65) * mm});
            skArc(sketch, "E235", {"start": v(-32.16, 29.65) * mm, "mid": v(-32.04, 29.69) * mm, "end": v(-31.93, 29.72) * mm});
            skArc(sketch, "E236", {"start": v(-31.93, 29.72) * mm, "mid": v(-31.91, 29.73) * mm, "end": v(-31.9, 29.73) * mm});
            skArc(sketch, "E237", {"start": v(-31.9, 29.73) * mm, "mid": v(-31.9, 29.74) * mm, "end": v(-31.9, 29.75) * mm});
            skArc(sketch, "E238", {"start": v(-31.9, 29.75) * mm, "mid": v(-32.08, 29.89) * mm, "end": v(-32.26, 30.02) * mm});
            skArc(sketch, "E239", {"start": v(-32.26, 30.02) * mm, "mid": v(-32.46, 30.16) * mm, "end": v(-32.67, 30.31) * mm});
            skArc(sketch, "E240", {"start": v(-32.67, 30.31) * mm, "mid": v(-32.91, 30.48) * mm, "end": v(-33.16, 30.66) * mm});
            skArc(sketch, "E241", {"start": v(-33.16, 30.66) * mm, "mid": v(-33.63, 31) * mm, "end": v(-34.09, 31.34) * mm});
            skArc(sketch, "E242", {"start": v(-34.09, 31.34) * mm, "mid": v(-34.56, 31.72) * mm, "end": v(-35.03, 32.12) * mm});
            skArc(sketch, "E243", {"start": v(-35.03, 32.12) * mm, "mid": v(-35.43, 32.48) * mm, "end": v(-35.83, 32.85) * mm});
            skArc(sketch, "E244", {"start": v(-35.83, 32.85) * mm, "mid": v(-36, 33.03) * mm, "end": v(-36.13, 33.25) * mm});
            skArc(sketch, "E245", {"start": v(-36.13, 33.25) * mm, "mid": v(-36.16, 33.3) * mm, "end": v(-36.17, 33.36) * mm});
            skArc(sketch, "E246", {"start": v(-36.17, 33.36) * mm, "mid": v(-36.16, 33.42) * mm, "end": v(-36.15, 33.47) * mm});
            skArc(sketch, "E247", {"start": v(-36.15, 33.47) * mm, "mid": v(-36.11, 33.54) * mm, "end": v(-36.07, 33.6) * mm});
            skArc(sketch, "E248", {"start": v(-36.07, 33.6) * mm, "mid": v(-35.98, 33.7) * mm, "end": v(-35.89, 33.8) * mm});
            skArc(sketch, "E249", {"start": v(-35.89, 33.8) * mm, "mid": v(-35.13, 34.7) * mm, "end": v(-34.5, 35.7) * mm});
            skArc(sketch, "E250", {"start": v(-34.5, 35.7) * mm, "mid": v(-34.06, 36.72) * mm, "end": v(-33.78, 37.8) * mm});
            skArc(sketch, "E251", {"start": v(-33.78, 37.8) * mm, "mid": v(-33.7, 38.77) * mm, "end": v(-33.8, 39.75) * mm});
            skArc(sketch, "E252", {"start": v(-33.8, 39.75) * mm, "mid": v(-34.08, 40.57) * mm, "end": v(-34.57, 41.28) * mm});
            skArc(sketch, "E253", {"start": v(-34.57, 41.28) * mm, "mid": v(-34.66, 41.39) * mm, "end": v(-34.77, 41.5) * mm});
            skArc(sketch, "E254", {"start": v(-34.77, 41.5) * mm, "mid": v(-34.87, 41.6) * mm, "end": v(-34.98, 41.7) * mm});
            skArc(sketch, "E255", {"start": v(-34.98, 41.7) * mm, "mid": v(-35.08, 41.77) * mm, "end": v(-35.18, 41.86) * mm});
            skArc(sketch, "E256", {"start": v(-35.18, 41.86) * mm, "mid": v(-35.24, 41.9) * mm, "end": v(-35.32, 41.95) * mm});
            skArc(sketch, "E257", {"start": v(-35.32, 41.95) * mm, "mid": v(-35.48, 42.02) * mm, "end": v(-35.66, 42.06) * mm});
            skArc(sketch, "E258", {"start": v(-35.66, 42.06) * mm, "mid": v(-35.86, 42.08) * mm, "end": v(-36.07, 42.09) * mm});
            skArc(sketch, "E259", {"start": v(-36.07, 42.09) * mm, "mid": v(-36.29, 42.07) * mm, "end": v(-36.5, 42.03) * mm});
            skArc(sketch, "E260", {"start": v(-36.5, 42.03) * mm, "mid": v(-36.7, 41.97) * mm, "end": v(-36.9, 41.88) * mm});
            skArc(sketch, "E261", {"start": v(-35.33, 41.15) * mm, "mid": v(-35.26, 41.1) * mm, "end": v(-35.2, 41.06) * mm});
            skArc(sketch, "E262", {"start": v(-35.2, 41.06) * mm, "mid": v(-35.13, 41) * mm, "end": v(-35.06, 40.92) * mm});
            skArc(sketch, "E263", {"start": v(-35.06, 40.92) * mm, "mid": v(-34.99, 40.83) * mm, "end": v(-34.92, 40.74) * mm});
            skArc(sketch, "E264", {"start": v(-34.92, 40.74) * mm, "mid": v(-34.86, 40.66) * mm, "end": v(-34.8, 40.57) * mm});
            skArc(sketch, "E265", {"start": v(-34.8, 40.57) * mm, "mid": v(-34.73, 40.43) * mm, "end": v(-34.67, 40.29) * mm});
            skArc(sketch, "E266", {"start": v(-34.67, 40.29) * mm, "mid": v(-34.63, 40.15) * mm, "end": v(-34.6, 40.01) * mm});
            skArc(sketch, "E267", {"start": v(-34.6, 40.01) * mm, "mid": v(-34.57, 39.83) * mm, "end": v(-34.55, 39.65) * mm});
            skArc(sketch, "E268", {"start": v(-34.55, 39.65) * mm, "mid": v(-34.53, 39.35) * mm, "end": v(-34.52, 39.05) * mm});
            skArc(sketch, "E269", {"start": v(-34.52, 39.05) * mm, "mid": v(-34.52, 38.37) * mm, "end": v(-34.58, 37.69) * mm});
            skArc(sketch, "E270", {"start": v(-34.58, 37.69) * mm, "mid": v(-34.68, 37.07) * mm, "end": v(-34.85, 36.46) * mm});
            skArc(sketch, "E271", {"start": v(-34.85, 36.46) * mm, "mid": v(-35.07, 35.9) * mm, "end": v(-35.34, 35.35) * mm});
            skArc(sketch, "E272", {"start": v(-35.34, 35.35) * mm, "mid": v(-35.67, 34.85) * mm, "end": v(-36.05, 34.38) * mm});
            skLineSegment(sketch, "E273", {"start": v(-36.05, 34.38) * mm, "end": v(-36.6, 33.77) * mm});
            skLineSegment(sketch, "E274", {"start": v(-36.6, 33.77) * mm, "end": v(-37.1, 34.83) * mm});
            skArc(sketch, "E275", {"start": v(-37.1, 34.83) * mm, "mid": v(-37.3, 35.28) * mm, "end": v(-37.5, 35.73) * mm});
            skArc(sketch, "E276", {"start": v(-37.5, 35.73) * mm, "mid": v(-37.64, 36.12) * mm, "end": v(-37.75, 36.51) * mm});
            skArc(sketch, "E277", {"start": v(-37.75, 36.51) * mm, "mid": v(-37.83, 36.88) * mm, "end": v(-37.89, 37.26) * mm});
            skArc(sketch, "E278", {"start": v(-37.89, 37.26) * mm, "mid": v(-37.92, 37.67) * mm, "end": v(-37.93, 38.08) * mm});
            skArc(sketch, "E279", {"start": v(-37.93, 38.08) * mm, "mid": v(-37.91, 38.57) * mm, "end": v(-37.85, 39.06) * mm});
            skArc(sketch, "E280", {"start": v(-37.85, 39.06) * mm, "mid": v(-37.76, 39.5) * mm, "end": v(-37.62, 39.93) * mm});
            skArc(sketch, "E281", {"start": v(-37.62, 39.93) * mm, "mid": v(-37.45, 40.29) * mm, "end": v(-37.24, 40.63) * mm});
            skArc(sketch, "E282", {"start": v(-37.24, 40.63) * mm, "mid": v(-37.02, 40.89) * mm, "end": v(-36.75, 41.1) * mm});
            skArc(sketch, "E283", {"start": v(-36.75, 41.1) * mm, "mid": v(-36.6, 41.18) * mm, "end": v(-36.45, 41.23) * mm});
            skArc(sketch, "E284", {"start": v(-36.45, 41.23) * mm, "mid": v(-36.25, 41.26) * mm, "end": v(-36.06, 41.28) * mm});
            skArc(sketch, "E285", {"start": v(-36.06, 41.28) * mm, "mid": v(-35.85, 41.28) * mm, "end": v(-35.65, 41.25) * mm});
            skArc(sketch, "E286", {"start": v(-35.65, 41.25) * mm, "mid": v(-35.49, 41.21) * mm, "end": v(-35.33, 41.15) * mm});
            skArc(sketch, "E287", {"start": v(-42.47, 40) * mm, "mid": v(-42.22, 39.7) * mm, "end": v(-42.03, 39.35) * mm});
            skArc(sketch, "E288", {"start": v(-42.03, 39.35) * mm, "mid": v(-41.89, 38.96) * mm, "end": v(-41.81, 38.55) * mm});
            skArc(sketch, "E289", {"start": v(-41.81, 38.55) * mm, "mid": v(-41.8, 38.1) * mm, "end": v(-41.84, 37.67) * mm});
            skArc(sketch, "E290", {"start": v(-41.84, 37.67) * mm, "mid": v(-41.94, 37.22) * mm, "end": v(-42.1, 36.8) * mm});
            skArc(sketch, "E291", {"start": v(-42.1, 36.8) * mm, "mid": v(-42.23, 36.56) * mm, "end": v(-42.36, 36.32) * mm});
            skArc(sketch, "E292", {"start": v(-42.36, 36.32) * mm, "mid": v(-42.56, 36.01) * mm, "end": v(-42.78, 35.7) * mm});
            skArc(sketch, "E293", {"start": v(-42.78, 35.7) * mm, "mid": v(-43, 35.4) * mm, "end": v(-43.22, 35.1) * mm});
            skArc(sketch, "E294", {"start": v(-43.22, 35.1) * mm, "mid": v(-43.28, 35.05) * mm, "end": v(-43.36, 35.03) * mm});
            skArc(sketch, "E295", {"start": v(-43.36, 35.03) * mm, "mid": v(-43.41, 35.05) * mm, "end": v(-43.45, 35.08) * mm});
            skArc(sketch, "E296", {"start": v(-43.45, 35.08) * mm, "mid": v(-43.62, 35.34) * mm, "end": v(-43.79, 35.6) * mm});
            skArc(sketch, "E297", {"start": v(-43.79, 35.6) * mm, "mid": v(-43.96, 35.87) * mm, "end": v(-44.12, 36.14) * mm});
            skArc(sketch, "E298", {"start": v(-44.12, 36.14) * mm, "mid": v(-44.25, 36.36) * mm, "end": v(-44.37, 36.6) * mm});
            skArc(sketch, "E299", {"start": v(-44.37, 36.6) * mm, "mid": v(-44.56, 37.06) * mm, "end": v(-44.69, 37.56) * mm});
            skArc(sketch, "E300", {"start": v(-44.69, 37.56) * mm, "mid": v(-44.75, 38.07) * mm, "end": v(-44.74, 38.58) * mm});
            skArc(sketch, "E301", {"start": v(-44.74, 38.58) * mm, "mid": v(-44.66, 39.05) * mm, "end": v(-44.52, 39.5) * mm});
            skArc(sketch, "E302", {"start": v(-44.52, 39.5) * mm, "mid": v(-44.33, 39.84) * mm, "end": v(-44.07, 40.13) * mm});
            skArc(sketch, "E303", {"start": v(-44.07, 40.13) * mm, "mid": v(-43.99, 40.2) * mm, "end": v(-43.9, 40.25) * mm});
            skArc(sketch, "E304", {"start": v(-43.9, 40.25) * mm, "mid": v(-43.82, 40.29) * mm, "end": v(-43.73, 40.32) * mm});
            skArc(sketch, "E305", {"start": v(-43.73, 40.32) * mm, "mid": v(-43.64, 40.35) * mm, "end": v(-43.54, 40.37) * mm});
            skArc(sketch, "E306", {"start": v(-43.54, 40.37) * mm, "mid": v(-43.43, 40.38) * mm, "end": v(-43.3, 40.38) * mm});
            skArc(sketch, "E307", {"start": v(-43.3, 40.38) * mm, "mid": v(-43.18, 40.37) * mm, "end": v(-43.05, 40.36) * mm});
            skArc(sketch, "E308", {"start": v(-43.05, 40.36) * mm, "mid": v(-42.95, 40.34) * mm, "end": v(-42.86, 40.31) * mm});
            skArc(sketch, "E309", {"start": v(-42.86, 40.31) * mm, "mid": v(-42.78, 40.26) * mm, "end": v(-42.7, 40.2) * mm});
            skArc(sketch, "E310", {"start": v(-42.7, 40.2) * mm, "mid": v(-42.58, 40.1) * mm, "end": v(-42.47, 40) * mm});
            skArc(sketch, "E311", {"start": v(-49.48, 39.14) * mm, "mid": v(-49.34, 38.98) * mm, "end": v(-49.22, 38.8) * mm});
            skArc(sketch, "E312", {"start": v(-49.22, 38.8) * mm, "mid": v(-49.12, 38.6) * mm, "end": v(-49.05, 38.4) * mm});
            skArc(sketch, "E313", {"start": v(-49.05, 38.4) * mm, "mid": v(-49, 38.15) * mm, "end": v(-48.96, 37.9) * mm});
            skArc(sketch, "E314", {"start": v(-48.96, 37.9) * mm, "mid": v(-48.94, 37.55) * mm, "end": v(-48.93, 37.2) * mm});
            skArc(sketch, "E315", {"start": v(-48.93, 37.2) * mm, "mid": v(-48.94, 36.9) * mm, "end": v(-48.96, 36.6) * mm});
            skArc(sketch, "E316", {"start": v(-48.96, 36.6) * mm, "mid": v(-49, 36.37) * mm, "end": v(-49.05, 36.14) * mm});
            skArc(sketch, "E317", {"start": v(-49.05, 36.14) * mm, "mid": v(-49.12, 35.91) * mm, "end": v(-49.2, 35.7) * mm});
            skArc(sketch, "E318", {"start": v(-49.2, 35.7) * mm, "mid": v(-49.34, 35.43) * mm, "end": v(-49.48, 35.17) * mm});
            skLineSegment(sketch, "E319", {"start": v(-49.48, 35.17) * mm, "end": v(-49.77, 34.69) * mm});
            skLineSegment(sketch, "E320", {"start": v(-49.77, 34.69) * mm, "end": v(-50.16, 35.14) * mm});
            skArc(sketch, "E321", {"start": v(-50.16, 35.14) * mm, "mid": v(-50.54, 35.65) * mm, "end": v(-50.86, 36.2) * mm});
            skArc(sketch, "E322", {"start": v(-50.86, 36.2) * mm, "mid": v(-51.08, 36.8) * mm, "end": v(-51.21, 37.4) * mm});
            skArc(sketch, "E323", {"start": v(-51.21, 37.4) * mm, "mid": v(-51.24, 37.94) * mm, "end": v(-51.17, 38.48) * mm});
            skArc(sketch, "E324", {"start": v(-51.17, 38.48) * mm, "mid": v(-51.02, 38.88) * mm, "end": v(-50.73, 39.21) * mm});
            skArc(sketch, "E325", {"start": v(-50.73, 39.21) * mm, "mid": v(-50.58, 39.32) * mm, "end": v(-50.41, 39.41) * mm});
            skArc(sketch, "E326", {"start": v(-50.41, 39.41) * mm, "mid": v(-50.26, 39.46) * mm, "end": v(-50.1, 39.47) * mm});
            skArc(sketch, "E327", {"start": v(-50.1, 39.47) * mm, "mid": v(-49.94, 39.44) * mm, "end": v(-49.8, 39.38) * mm});
            skArc(sketch, "E328", {"start": v(-49.8, 39.38) * mm, "mid": v(-49.63, 39.27) * mm, "end": v(-49.48, 39.14) * mm});
            skArc(sketch, "E329", {"start": v(-61.16, 33.66) * mm, "mid": v(-60.4, 33.53) * mm, "end": v(-59.65, 33.35) * mm});
            skArc(sketch, "E330", {"start": v(-59.65, 33.35) * mm, "mid": v(-58.83, 33.12) * mm, "end": v(-58.03, 32.86) * mm});
            skArc(sketch, "E331", {"start": v(-58.03, 32.86) * mm, "mid": v(-57.26, 32.57) * mm, "end": v(-56.5, 32.24) * mm});
            skArc(sketch, "E332", {"start": v(-56.5, 32.24) * mm, "mid": v(-55.88, 31.94) * mm, "end": v(-55.29, 31.59) * mm});
            skArc(sketch, "E333", {"start": v(-55.29, 31.59) * mm, "mid": v(-55.1, 31.46) * mm, "end": v(-54.9, 31.34) * mm});
            skArc(sketch, "E334", {"start": v(-54.9, 31.34) * mm, "mid": v(-54.83, 31.28) * mm, "end": v(-54.77, 31.22) * mm});
            skArc(sketch, "E335", {"start": v(-54.77, 31.22) * mm, "mid": v(-54.75, 31.18) * mm, "end": v(-54.75, 31.13) * mm});
            skArc(sketch, "E336", {"start": v(-54.75, 31.13) * mm, "mid": v(-54.78, 31.08) * mm, "end": v(-54.82, 31.04) * mm});
            skArc(sketch, "E337", {"start": v(-54.82, 31.04) * mm, "mid": v(-55, 30.93) * mm, "end": v(-55.2, 30.85) * mm});
            skArc(sketch, "E338", {"start": v(-55.2, 30.85) * mm, "mid": v(-55.72, 30.68) * mm, "end": v(-56.24, 30.52) * mm});
            skArc(sketch, "E339", {"start": v(-56.24, 30.52) * mm, "mid": v(-56.79, 30.36) * mm, "end": v(-57.34, 30.21) * mm});
            skArc(sketch, "E340", {"start": v(-57.34, 30.21) * mm, "mid": v(-57.77, 30.1) * mm, "end": v(-58.2, 30.02) * mm});
            skArc(sketch, "E341", {"start": v(-58.2, 30.02) * mm, "mid": v(-59.34, 29.88) * mm, "end": v(-60.47, 29.84) * mm});
            skArc(sketch, "E342", {"start": v(-60.47, 29.84) * mm, "mid": v(-61.66, 29.89) * mm, "end": v(-62.84, 30.03) * mm});
            skArc(sketch, "E343", {"start": v(-62.84, 30.03) * mm, "mid": v(-63.89, 30.24) * mm, "end": v(-64.91, 30.53) * mm});
            skArc(sketch, "E344", {"start": v(-64.91, 30.53) * mm, "mid": v(-65.6, 30.84) * mm, "end": v(-66.19, 31.3) * mm});
            skArc(sketch, "E345", {"start": v(-66.19, 31.3) * mm, "mid": v(-66.3, 31.4) * mm, "end": v(-66.4, 31.52) * mm});
            skArc(sketch, "E346", {"start": v(-66.4, 31.52) * mm, "mid": v(-66.47, 31.6) * mm, "end": v(-66.52, 31.69) * mm});
            skArc(sketch, "E347", {"start": v(-66.52, 31.69) * mm, "mid": v(-66.55, 31.77) * mm, "end": v(-66.57, 31.87) * mm});
            skArc(sketch, "E348", {"start": v(-66.57, 31.87) * mm, "mid": v(-66.58, 32) * mm, "end": v(-66.58, 32.13) * mm});
            skArc(sketch, "E349", {"start": v(-66.58, 32.13) * mm, "mid": v(-66.57, 32.34) * mm, "end": v(-66.52, 32.54) * mm});
            skArc(sketch, "E350", {"start": v(-66.52, 32.54) * mm, "mid": v(-66.44, 32.72) * mm, "end": v(-66.33, 32.89) * mm});
            skArc(sketch, "E351", {"start": v(-66.33, 32.89) * mm, "mid": v(-66.19, 33.04) * mm, "end": v(-66.01, 33.17) * mm});
            skArc(sketch, "E352", {"start": v(-66.01, 33.17) * mm, "mid": v(-65.78, 33.3) * mm, "end": v(-65.54, 33.41) * mm});
            skArc(sketch, "E353", {"start": v(-65.54, 33.41) * mm, "mid": v(-65.1, 33.56) * mm, "end": v(-64.66, 33.67) * mm});
            skArc(sketch, "E354", {"start": v(-64.66, 33.67) * mm, "mid": v(-64.15, 33.75) * mm, "end": v(-63.62, 33.8) * mm});
            skArc(sketch, "E355", {"start": v(-63.62, 33.8) * mm, "mid": v(-63.03, 33.81) * mm, "end": v(-62.44, 33.8) * mm});
            skArc(sketch, "E356", {"start": v(-62.44, 33.8) * mm, "mid": v(-61.8, 33.74) * mm, "end": v(-61.16, 33.66) * mm});
            skArc(sketch, "E357", {"start": v(-43.88, 33.64) * mm, "mid": v(-43.87, 33.58) * mm, "end": v(-43.84, 33.52) * mm});
            skArc(sketch, "E358", {"start": v(-43.84, 33.52) * mm, "mid": v(-43.55, 33.12) * mm, "end": v(-43.26, 32.71) * mm});
            skArc(sketch, "E359", {"start": v(-43.26, 32.71) * mm, "mid": v(-42.95, 32.3) * mm, "end": v(-42.64, 31.88) * mm});
            skArc(sketch, "E360", {"start": v(-42.64, 31.88) * mm, "mid": v(-42.34, 31.5) * mm, "end": v(-42.04, 31.12) * mm});
            skArc(sketch, "E361", {"start": v(-42.04, 31.12) * mm, "mid": v(-41.93, 30.98) * mm, "end": v(-41.82, 30.84) * mm});
            skArc(sketch, "E362", {"start": v(-41.82, 30.84) * mm, "mid": v(-41.73, 30.72) * mm, "end": v(-41.63, 30.6) * mm});
            skArc(sketch, "E363", {"start": v(-41.63, 30.6) * mm, "mid": v(-41.55, 30.5) * mm, "end": v(-41.47, 30.39) * mm});
            skArc(sketch, "E364", {"start": v(-41.47, 30.39) * mm, "mid": v(-41.47, 30.38) * mm, "end": v(-41.46, 30.36) * mm});
            skArc(sketch, "E365", {"start": v(-41.46, 30.36) * mm, "mid": v(-41.47, 30.35) * mm, "end": v(-41.48, 30.34) * mm});
            skArc(sketch, "E366", {"start": v(-41.48, 30.34) * mm, "mid": v(-41.57, 30.27) * mm, "end": v(-41.67, 30.2) * mm});
            skArc(sketch, "E367", {"start": v(-41.67, 30.2) * mm, "mid": v(-41.78, 30.12) * mm, "end": v(-41.89, 30.04) * mm});
            skArc(sketch, "E368", {"start": v(-41.89, 30.04) * mm, "mid": v(-42.02, 29.95) * mm, "end": v(-42.15, 29.86) * mm});
            skArc(sketch, "E369", {"start": v(-42.15, 29.86) * mm, "mid": v(-42.3, 29.76) * mm, "end": v(-42.46, 29.65) * mm});
            skArc(sketch, "E370", {"start": v(-42.46, 29.65) * mm, "mid": v(-42.63, 29.53) * mm, "end": v(-42.8, 29.4) * mm});
            skArc(sketch, "E371", {"start": v(-42.8, 29.4) * mm, "mid": v(-42.98, 29.28) * mm, "end": v(-43.14, 29.15) * mm});
            skArc(sketch, "E372", {"start": v(-43.14, 29.15) * mm, "mid": v(-43.28, 29.04) * mm, "end": v(-43.41, 28.94) * mm});
            skArc(sketch, "E373", {"start": v(-43.41, 28.94) * mm, "mid": v(-43.52, 28.85) * mm, "end": v(-43.64, 28.76) * mm});
            skArc(sketch, "E374", {"start": v(-43.64, 28.76) * mm, "mid": v(-43.74, 28.69) * mm, "end": v(-43.84, 28.61) * mm});
            skArc(sketch, "E375", {"start": v(-43.84, 28.61) * mm, "mid": v(-43.92, 28.55) * mm, "end": v(-44, 28.5) * mm});
            skArc(sketch, "E376", {"start": v(-44, 28.5) * mm, "mid": v(-44.03, 28.48) * mm, "end": v(-44.06, 28.48) * mm});
            skArc(sketch, "E377", {"start": v(-44.06, 28.48) * mm, "mid": v(-44.08, 28.48) * mm, "end": v(-44.1, 28.5) * mm});
            skArc(sketch, "E378", {"start": v(-44.1, 28.5) * mm, "mid": v(-44.16, 28.55) * mm, "end": v(-44.21, 28.6) * mm});
            skArc(sketch, "E379", {"start": v(-44.21, 28.6) * mm, "mid": v(-44.27, 28.68) * mm, "end": v(-44.33, 28.75) * mm});
            skArc(sketch, "E380", {"start": v(-44.33, 28.75) * mm, "mid": v(-44.4, 28.83) * mm, "end": v(-44.47, 28.92) * mm});
            skArc(sketch, "E381", {"start": v(-44.47, 28.92) * mm, "mid": v(-44.56, 29.04) * mm, "end": v(-44.66, 29.15) * mm});
            skArc(sketch, "E382", {"start": v(-44.66, 29.15) * mm, "mid": v(-44.82, 29.35) * mm, "end": v(-45, 29.54) * mm});
            skArc(sketch, "E383", {"start": v(-45, 29.54) * mm, "mid": v(-45.2, 29.76) * mm, "end": v(-45.4, 29.98) * mm});
            skArc(sketch, "E384", {"start": v(-45.4, 29.98) * mm, "mid": v(-45.6, 30.2) * mm, "end": v(-45.8, 30.42) * mm});
            skLineSegment(sketch, "E385", {"start": v(-45.8, 30.42) * mm, "end": v(-46.81, 31.48) * mm});
            skLineSegment(sketch, "E386", {"start": v(-46.81, 31.48) * mm, "end": v(-45.56, 32.45) * mm});
            skArc(sketch, "E387", {"start": v(-45.56, 32.45) * mm, "mid": v(-45.31, 32.64) * mm, "end": v(-45.07, 32.84) * mm});
            skArc(sketch, "E388", {"start": v(-45.07, 32.84) * mm, "mid": v(-44.85, 33) * mm, "end": v(-44.64, 33.18) * mm});
            skArc(sketch, "E389", {"start": v(-44.64, 33.18) * mm, "mid": v(-44.46, 33.33) * mm, "end": v(-44.28, 33.48) * mm});
            skArc(sketch, "E390", {"start": v(-44.28, 33.48) * mm, "mid": v(-44.23, 33.52) * mm, "end": v(-44.18, 33.57) * mm});
            skArc(sketch, "E391", {"start": v(-44.18, 33.57) * mm, "mid": v(-44.14, 33.62) * mm, "end": v(-44.08, 33.67) * mm});
            skArc(sketch, "E392", {"start": v(-44.08, 33.67) * mm, "mid": v(-44.04, 33.7) * mm, "end": v(-43.98, 33.71) * mm});
            skArc(sketch, "E393", {"start": v(-43.98, 33.71) * mm, "mid": v(-43.95, 33.72) * mm, "end": v(-43.91, 33.7) * mm});
            skArc(sketch, "E394", {"start": v(-43.91, 33.7) * mm, "mid": v(-43.9, 33.68) * mm, "end": v(-43.88, 33.64) * mm});
            skArc(sketch, "E395", {"start": v(-49.35, 32.22) * mm, "mid": v(-49.15, 32) * mm, "end": v(-48.95, 31.79) * mm});
            skArc(sketch, "E396", {"start": v(-48.95, 31.79) * mm, "mid": v(-48.79, 31.6) * mm, "end": v(-48.62, 31.41) * mm});
            skArc(sketch, "E397", {"start": v(-48.62, 31.41) * mm, "mid": v(-48.48, 31.25) * mm, "end": v(-48.35, 31.08) * mm});
            skArc(sketch, "E398", {"start": v(-48.35, 31.08) * mm, "mid": v(-48.33, 31.05) * mm, "end": v(-48.32, 31.02) * mm});
            skArc(sketch, "E399", {"start": v(-48.32, 31.02) * mm, "mid": v(-48.33, 31) * mm, "end": v(-48.34, 30.97) * mm});
            skArc(sketch, "E400", {"start": v(-48.34, 30.97) * mm, "mid": v(-48.37, 30.93) * mm, "end": v(-48.4, 30.9) * mm});
            skArc(sketch, "E401", {"start": v(-48.4, 30.9) * mm, "mid": v(-48.45, 30.85) * mm, "end": v(-48.5, 30.81) * mm});
            skArc(sketch, "E402", {"start": v(-48.5, 30.81) * mm, "mid": v(-48.55, 30.77) * mm, "end": v(-48.6, 30.74) * mm});
            skArc(sketch, "E403", {"start": v(-48.6, 30.74) * mm, "mid": v(-48.68, 30.68) * mm, "end": v(-48.76, 30.63) * mm});
            skArc(sketch, "E404", {"start": v(-48.76, 30.63) * mm, "mid": v(-48.9, 30.52) * mm, "end": v(-49.06, 30.4) * mm});
            skArc(sketch, "E405", {"start": v(-49.06, 30.4) * mm, "mid": v(-49.23, 30.27) * mm, "end": v(-49.4, 30.14) * mm});
            skArc(sketch, "E406", {"start": v(-49.4, 30.14) * mm, "mid": v(-49.59, 30) * mm, "end": v(-49.77, 29.85) * mm});
            skLineSegment(sketch, "E407", {"start": v(-49.77, 29.85) * mm, "end": v(-50.66, 29.15) * mm});
            skLineSegment(sketch, "E408", {"start": v(-50.66, 29.15) * mm, "end": v(-51.13, 29.7) * mm});
            skArc(sketch, "E409", {"start": v(-51.13, 29.7) * mm, "mid": v(-51.24, 29.82) * mm, "end": v(-51.35, 29.95) * mm});
            skArc(sketch, "E410", {"start": v(-51.35, 29.95) * mm, "mid": v(-51.5, 30.1) * mm, "end": v(-51.65, 30.26) * mm});
            skArc(sketch, "E411", {"start": v(-51.65, 30.26) * mm, "mid": v(-51.8, 30.42) * mm, "end": v(-51.96, 30.58) * mm});
            skArc(sketch, "E412", {"start": v(-51.96, 30.58) * mm, "mid": v(-52.1, 30.72) * mm, "end": v(-52.25, 30.86) * mm});
            skLineSegment(sketch, "E413", {"start": v(-52.25, 30.86) * mm, "end": v(-52.9, 31.47) * mm});
            skLineSegment(sketch, "E414", {"start": v(-52.9, 31.47) * mm, "end": v(-52.3, 31.88) * mm});
            skArc(sketch, "E415", {"start": v(-52.3, 31.88) * mm, "mid": v(-52.16, 31.98) * mm, "end": v(-52.03, 32.08) * mm});
            skArc(sketch, "E416", {"start": v(-52.03, 32.08) * mm, "mid": v(-51.86, 32.2) * mm, "end": v(-51.7, 32.32) * mm});
            skArc(sketch, "E417", {"start": v(-51.7, 32.32) * mm, "mid": v(-51.54, 32.45) * mm, "end": v(-51.37, 32.58) * mm});
            skArc(sketch, "E418", {"start": v(-51.37, 32.58) * mm, "mid": v(-51.23, 32.69) * mm, "end": v(-51.1, 32.8) * mm});
            skArc(sketch, "E419", {"start": v(-51.1, 32.8) * mm, "mid": v(-50.98, 32.9) * mm, "end": v(-50.86, 33) * mm});
            skArc(sketch, "E420", {"start": v(-50.86, 33) * mm, "mid": v(-50.76, 33.08) * mm, "end": v(-50.65, 33.16) * mm});
            skArc(sketch, "E421", {"start": v(-50.65, 33.16) * mm, "mid": v(-50.56, 33.23) * mm, "end": v(-50.47, 33.3) * mm});
            skArc(sketch, "E422", {"start": v(-50.47, 33.3) * mm, "mid": v(-50.45, 33.3) * mm, "end": v(-50.43, 33.31) * mm});
            skArc(sketch, "E423", {"start": v(-50.43, 33.31) * mm, "mid": v(-50.4, 33.3) * mm, "end": v(-50.39, 33.3) * mm});
            skArc(sketch, "E424", {"start": v(-50.39, 33.3) * mm, "mid": v(-50.24, 33.14) * mm, "end": v(-50.09, 33) * mm});
            skArc(sketch, "E425", {"start": v(-50.09, 33) * mm, "mid": v(-49.91, 32.82) * mm, "end": v(-49.74, 32.64) * mm});
            skArc(sketch, "E426", {"start": v(-49.74, 32.64) * mm, "mid": v(-49.54, 32.43) * mm, "end": v(-49.35, 32.22) * mm});
            skArc(sketch, "E427", {"start": v(-36.54, 31.68) * mm, "mid": v(-36.38, 31.47) * mm, "end": v(-36.23, 31.27) * mm});
            skArc(sketch, "E428", {"start": v(-36.23, 31.27) * mm, "mid": v(-36.05, 31.05) * mm, "end": v(-35.87, 30.83) * mm});
            skArc(sketch, "E429", {"start": v(-35.87, 30.83) * mm, "mid": v(-35.7, 30.62) * mm, "end": v(-35.54, 30.4) * mm});
            skArc(sketch, "E430", {"start": v(-35.54, 30.4) * mm, "mid": v(-35.4, 30.25) * mm, "end": v(-35.27, 30.1) * mm});
            skArc(sketch, "E431", {"start": v(-35.27, 30.1) * mm, "mid": v(-35.17, 29.97) * mm, "end": v(-35.06, 29.84) * mm});
            skArc(sketch, "E432", {"start": v(-35.06, 29.84) * mm, "mid": v(-34.98, 29.73) * mm, "end": v(-34.9, 29.61) * mm});
            skArc(sketch, "E433", {"start": v(-34.9, 29.61) * mm, "mid": v(-34.83, 29.52) * mm, "end": v(-34.76, 29.42) * mm});
            skArc(sketch, "E434", {"start": v(-34.76, 29.42) * mm, "mid": v(-34.75, 29.4) * mm, "end": v(-34.76, 29.37) * mm});
            skArc(sketch, "E435", {"start": v(-34.76, 29.37) * mm, "mid": v(-34.78, 29.35) * mm, "end": v(-34.8, 29.33) * mm});
            skArc(sketch, "E436", {"start": v(-34.8, 29.33) * mm, "mid": v(-34.9, 29.27) * mm, "end": v(-35, 29.2) * mm});
            skArc(sketch, "E437", {"start": v(-35, 29.2) * mm, "mid": v(-35.13, 29.12) * mm, "end": v(-35.25, 29.05) * mm});
            skArc(sketch, "E438", {"start": v(-35.25, 29.05) * mm, "mid": v(-35.4, 28.96) * mm, "end": v(-35.53, 28.88) * mm});
            skArc(sketch, "E439", {"start": v(-35.53, 28.88) * mm, "mid": v(-35.7, 28.78) * mm, "end": v(-35.85, 28.68) * mm});
            skArc(sketch, "E440", {"start": v(-35.85, 28.68) * mm, "mid": v(-36.03, 28.57) * mm, "end": v(-36.2, 28.46) * mm});
            skArc(sketch, "E441", {"start": v(-36.2, 28.46) * mm, "mid": v(-36.37, 28.35) * mm, "end": v(-36.53, 28.25) * mm});
            skArc(sketch, "E442", {"start": v(-36.53, 28.25) * mm, "mid": v(-36.65, 28.16) * mm, "end": v(-36.77, 28.07) * mm});
            skLineSegment(sketch, "E443", {"start": v(-36.77, 28.07) * mm, "end": v(-37.28, 27.7) * mm});
            skLineSegment(sketch, "E444", {"start": v(-37.28, 27.7) * mm, "end": v(-38.54, 29.21) * mm});
            skArc(sketch, "E445", {"start": v(-38.54, 29.21) * mm, "mid": v(-38.78, 29.5) * mm, "end": v(-39.02, 29.8) * mm});
            skArc(sketch, "E446", {"start": v(-39.02, 29.8) * mm, "mid": v(-39.23, 30.05) * mm, "end": v(-39.43, 30.3) * mm});
            skArc(sketch, "E447", {"start": v(-39.43, 30.3) * mm, "mid": v(-39.6, 30.52) * mm, "end": v(-39.79, 30.74) * mm});
            skArc(sketch, "E448", {"start": v(-39.79, 30.74) * mm, "mid": v(-39.8, 30.75) * mm, "end": v(-39.8, 30.77) * mm});
            skArc(sketch, "E449", {"start": v(-39.8, 30.77) * mm, "mid": v(-39.8, 30.78) * mm, "end": v(-39.78, 30.8) * mm});
            skArc(sketch, "E450", {"start": v(-39.78, 30.8) * mm, "mid": v(-39.17, 31.25) * mm, "end": v(-38.55, 31.7) * mm});
            skArc(sketch, "E451", {"start": v(-38.55, 31.7) * mm, "mid": v(-37.94, 32.14) * mm, "end": v(-37.33, 32.58) * mm});
            skArc(sketch, "E452", {"start": v(-37.33, 32.58) * mm, "mid": v(-37.3, 32.6) * mm, "end": v(-37.27, 32.6) * mm});
            skArc(sketch, "E453", {"start": v(-37.27, 32.6) * mm, "mid": v(-37.26, 32.6) * mm, "end": v(-37.26, 32.6) * mm});
            skArc(sketch, "E454", {"start": v(-37.26, 32.6) * mm, "mid": v(-37.15, 32.47) * mm, "end": v(-37.05, 32.34) * mm});
            skArc(sketch, "E455", {"start": v(-37.05, 32.34) * mm, "mid": v(-36.93, 32.19) * mm, "end": v(-36.82, 32.04) * mm});
            skArc(sketch, "E456", {"start": v(-36.82, 32.04) * mm, "mid": v(-36.68, 31.86) * mm, "end": v(-36.54, 31.68) * mm});
            skArc(sketch, "E457", {"start": v(-50.81, 27.22) * mm, "mid": v(-50.64, 26.9) * mm, "end": v(-50.48, 26.59) * mm});
            skArc(sketch, "E458", {"start": v(-50.48, 26.59) * mm, "mid": v(-50.36, 26.3) * mm, "end": v(-50.27, 26.03) * mm});
            skArc(sketch, "E459", {"start": v(-50.27, 26.03) * mm, "mid": v(-50.2, 25.74) * mm, "end": v(-50.15, 25.44) * mm});
            skArc(sketch, "E460", {"start": v(-50.15, 25.44) * mm, "mid": v(-50.12, 25.1) * mm, "end": v(-50.1, 24.74) * mm});
            skArc(sketch, "E461", {"start": v(-50.1, 24.74) * mm, "mid": v(-50.1, 24.52) * mm, "end": v(-50.1, 24.3) * mm});
            skArc(sketch, "E462", {"start": v(-50.1, 24.3) * mm, "mid": v(-50.11, 24.15) * mm, "end": v(-50.13, 24) * mm});
            skArc(sketch, "E463", {"start": v(-50.13, 24) * mm, "mid": v(-50.15, 23.88) * mm, "end": v(-50.18, 23.76) * mm});
            skArc(sketch, "E464", {"start": v(-50.18, 23.76) * mm, "mid": v(-50.22, 23.66) * mm, "end": v(-50.27, 23.56) * mm});
            skArc(sketch, "E465", {"start": v(-50.27, 23.56) * mm, "mid": v(-50.48, 23.27) * mm, "end": v(-50.75, 23.04) * mm});
            skArc(sketch, "E466", {"start": v(-50.75, 23.04) * mm, "mid": v(-51.06, 22.9) * mm, "end": v(-51.39, 22.88) * mm});
            skArc(sketch, "E467", {"start": v(-51.39, 22.88) * mm, "mid": v(-51.7, 22.95) * mm, "end": v(-51.98, 23.13) * mm});
            skArc(sketch, "E468", {"start": v(-51.98, 23.13) * mm, "mid": v(-52.22, 23.4) * mm, "end": v(-52.37, 23.72) * mm});
            skArc(sketch, "E469", {"start": v(-52.37, 23.72) * mm, "mid": v(-52.43, 23.94) * mm, "end": v(-52.46, 24.17) * mm});
            skArc(sketch, "E470", {"start": v(-52.46, 24.17) * mm, "mid": v(-52.48, 24.48) * mm, "end": v(-52.48, 24.8) * mm});
            skArc(sketch, "E471", {"start": v(-52.48, 24.8) * mm, "mid": v(-52.46, 25.13) * mm, "end": v(-52.43, 25.45) * mm});
            skArc(sketch, "E472", {"start": v(-52.43, 25.45) * mm, "mid": v(-52.38, 25.74) * mm, "end": v(-52.31, 26.02) * mm});
            skArc(sketch, "E473", {"start": v(-52.31, 26.02) * mm, "mid": v(-52.23, 26.25) * mm, "end": v(-52.13, 26.48) * mm});
            skArc(sketch, "E474", {"start": v(-52.13, 26.48) * mm, "mid": v(-51.96, 26.81) * mm, "end": v(-51.78, 27.14) * mm});
            skArc(sketch, "E475", {"start": v(-51.78, 27.14) * mm, "mid": v(-51.59, 27.46) * mm, "end": v(-51.4, 27.8) * mm});
            skArc(sketch, "E476", {"start": v(-51.4, 27.8) * mm, "mid": v(-51.33, 27.85) * mm, "end": v(-51.25, 27.87) * mm});
            skArc(sketch, "E477", {"start": v(-51.25, 27.87) * mm, "mid": v(-51.23, 27.86) * mm, "end": v(-51.22, 27.85) * mm});
            skArc(sketch, "E478", {"start": v(-51.22, 27.85) * mm, "mid": v(-51.16, 27.76) * mm, "end": v(-51.1, 27.68) * mm});
            skArc(sketch, "E479", {"start": v(-51.1, 27.68) * mm, "mid": v(-51.03, 27.57) * mm, "end": v(-50.96, 27.46) * mm});
            skArc(sketch, "E480", {"start": v(-50.96, 27.46) * mm, "mid": v(-50.89, 27.34) * mm, "end": v(-50.81, 27.22) * mm});
            skArc(sketch, "E481", {"start": v(-44.19, 26.18) * mm, "mid": v(-43.97, 25.82) * mm, "end": v(-43.77, 25.45) * mm});
            skArc(sketch, "E482", {"start": v(-43.77, 25.45) * mm, "mid": v(-43.6, 25.1) * mm, "end": v(-43.48, 24.72) * mm});
            skArc(sketch, "E483", {"start": v(-43.48, 24.72) * mm, "mid": v(-43.38, 24.36) * mm, "end": v(-43.3, 23.98) * mm});
            skArc(sketch, "E484", {"start": v(-43.3, 23.98) * mm, "mid": v(-43.26, 23.59) * mm, "end": v(-43.24, 23.19) * mm});
            skArc(sketch, "E485", {"start": v(-43.24, 23.19) * mm, "mid": v(-43.24, 22.97) * mm, "end": v(-43.25, 22.76) * mm});
            skArc(sketch, "E486", {"start": v(-43.25, 22.76) * mm, "mid": v(-43.26, 22.6) * mm, "end": v(-43.28, 22.45) * mm});
            skArc(sketch, "E487", {"start": v(-43.28, 22.45) * mm, "mid": v(-43.3, 22.33) * mm, "end": v(-43.35, 22.2) * mm});
            skArc(sketch, "E488", {"start": v(-43.35, 22.2) * mm, "mid": v(-43.4, 22.08) * mm, "end": v(-43.45, 21.96) * mm});
            skArc(sketch, "E489", {"start": v(-43.45, 21.96) * mm, "mid": v(-43.68, 21.64) * mm, "end": v(-43.98, 21.4) * mm});
            skArc(sketch, "E490", {"start": v(-43.98, 21.4) * mm, "mid": v(-44.32, 21.28) * mm, "end": v(-44.68, 21.26) * mm});
            skArc(sketch, "E491", {"start": v(-44.68, 21.26) * mm, "mid": v(-45.05, 21.36) * mm, "end": v(-45.37, 21.57) * mm});
            skArc(sketch, "E492", {"start": v(-45.37, 21.57) * mm, "mid": v(-45.65, 21.88) * mm, "end": v(-45.86, 22.24) * mm});
            skArc(sketch, "E493", {"start": v(-45.86, 22.24) * mm, "mid": v(-45.95, 22.52) * mm, "end": v(-46, 22.8) * mm});
            skArc(sketch, "E494", {"start": v(-46, 22.8) * mm, "mid": v(-46.03, 23.17) * mm, "end": v(-46.03, 23.53) * mm});
            skArc(sketch, "E495", {"start": v(-46.03, 23.53) * mm, "mid": v(-46, 23.93) * mm, "end": v(-45.95, 24.32) * mm});
            skArc(sketch, "E496", {"start": v(-45.95, 24.32) * mm, "mid": v(-45.88, 24.7) * mm, "end": v(-45.77, 25.08) * mm});
            skArc(sketch, "E497", {"start": v(-45.77, 25.08) * mm, "mid": v(-45.67, 25.37) * mm, "end": v(-45.55, 25.66) * mm});
            skArc(sketch, "E498", {"start": v(-45.55, 25.66) * mm, "mid": v(-45.4, 25.99) * mm, "end": v(-45.24, 26.3) * mm});
            skArc(sketch, "E499", {"start": v(-45.24, 26.3) * mm, "mid": v(-45.08, 26.6) * mm, "end": v(-44.92, 26.88) * mm});
            skArc(sketch, "E500", {"start": v(-44.92, 26.88) * mm, "mid": v(-44.86, 26.94) * mm, "end": v(-44.78, 26.96) * mm});
            skArc(sketch, "E501", {"start": v(-44.78, 26.96) * mm, "mid": v(-44.75, 26.96) * mm, "end": v(-44.73, 26.94) * mm});
            skArc(sketch, "E502", {"start": v(-44.73, 26.94) * mm, "mid": v(-44.65, 26.84) * mm, "end": v(-44.57, 26.73) * mm});
            skArc(sketch, "E503", {"start": v(-44.57, 26.73) * mm, "mid": v(-44.48, 26.6) * mm, "end": v(-44.4, 26.48) * mm});
            skArc(sketch, "E504", {"start": v(-44.4, 26.48) * mm, "mid": v(-44.29, 26.33) * mm, "end": v(-44.19, 26.18) * mm});
            skArc(sketch, "E505", {"start": v(-37.66, 25.62) * mm, "mid": v(-37.29, 25.1) * mm, "end": v(-36.94, 24.58) * mm});
            skArc(sketch, "E506", {"start": v(-36.94, 24.58) * mm, "mid": v(-36.66, 24.1) * mm, "end": v(-36.42, 23.6) * mm});
            skArc(sketch, "E507", {"start": v(-36.42, 23.6) * mm, "mid": v(-36.24, 23.16) * mm, "end": v(-36.09, 22.7) * mm});
            skArc(sketch, "E508", {"start": v(-36.09, 22.7) * mm, "mid": v(-36, 22.28) * mm, "end": v(-35.94, 21.84) * mm});
            skArc(sketch, "E509", {"start": v(-35.94, 21.84) * mm, "mid": v(-35.93, 21.5) * mm, "end": v(-35.93, 21.15) * mm});
            skArc(sketch, "E510", {"start": v(-35.93, 21.15) * mm, "mid": v(-35.97, 20.87) * mm, "end": v(-36.03, 20.6) * mm});
            skArc(sketch, "E511", {"start": v(-36.03, 20.6) * mm, "mid": v(-36.13, 20.36) * mm, "end": v(-36.26, 20.14) * mm});
            skArc(sketch, "E512", {"start": v(-36.26, 20.14) * mm, "mid": v(-36.43, 19.9) * mm, "end": v(-36.62, 19.68) * mm});
            skArc(sketch, "E513", {"start": v(-36.62, 19.68) * mm, "mid": v(-36.76, 19.53) * mm, "end": v(-36.91, 19.39) * mm});
            skArc(sketch, "E514", {"start": v(-36.91, 19.39) * mm, "mid": v(-37, 19.32) * mm, "end": v(-37.1, 19.26) * mm});
            skArc(sketch, "E515", {"start": v(-37.1, 19.26) * mm, "mid": v(-37.2, 19.23) * mm, "end": v(-37.3, 19.2) * mm});
            skArc(sketch, "E516", {"start": v(-37.3, 19.2) * mm, "mid": v(-37.45, 19.2) * mm, "end": v(-37.61, 19.2) * mm});
            skArc(sketch, "E517", {"start": v(-37.61, 19.2) * mm, "mid": v(-37.76, 19.2) * mm, "end": v(-37.91, 19.2) * mm});
            skArc(sketch, "E518", {"start": v(-37.91, 19.2) * mm, "mid": v(-38.01, 19.22) * mm, "end": v(-38.11, 19.25) * mm});
            skArc(sketch, "E519", {"start": v(-38.11, 19.25) * mm, "mid": v(-38.2, 19.3) * mm, "end": v(-38.3, 19.35) * mm});
            skArc(sketch, "E520", {"start": v(-38.3, 19.35) * mm, "mid": v(-38.4, 19.45) * mm, "end": v(-38.52, 19.55) * mm});
            skArc(sketch, "E521", {"start": v(-38.52, 19.55) * mm, "mid": v(-38.72, 19.75) * mm, "end": v(-38.9, 19.97) * mm});
            skArc(sketch, "E522", {"start": v(-38.9, 19.97) * mm, "mid": v(-39.04, 20.22) * mm, "end": v(-39.16, 20.49) * mm});
            skArc(sketch, "E523", {"start": v(-39.16, 20.49) * mm, "mid": v(-39.27, 20.8) * mm, "end": v(-39.34, 21.11) * mm});
            skArc(sketch, "E524", {"start": v(-39.34, 21.11) * mm, "mid": v(-39.4, 21.5) * mm, "end": v(-39.42, 21.88) * mm});
            skArc(sketch, "E525", {"start": v(-39.42, 21.88) * mm, "mid": v(-39.43, 22.24) * mm, "end": v(-39.43, 22.61) * mm});
            skArc(sketch, "E526", {"start": v(-39.43, 22.61) * mm, "mid": v(-39.4, 22.98) * mm, "end": v(-39.36, 23.34) * mm});
            skArc(sketch, "E527", {"start": v(-39.36, 23.34) * mm, "mid": v(-39.3, 23.7) * mm, "end": v(-39.24, 24.05) * mm});
            skArc(sketch, "E528", {"start": v(-39.24, 24.05) * mm, "mid": v(-39.15, 24.38) * mm, "end": v(-39.05, 24.7) * mm});
            skArc(sketch, "E529", {"start": v(-39.05, 24.7) * mm, "mid": v(-38.96, 24.93) * mm, "end": v(-38.86, 25.14) * mm});
            skArc(sketch, "E530", {"start": v(-38.86, 25.14) * mm, "mid": v(-38.72, 25.39) * mm, "end": v(-38.58, 25.63) * mm});
            skArc(sketch, "E531", {"start": v(-38.58, 25.63) * mm, "mid": v(-38.43, 25.86) * mm, "end": v(-38.28, 26.08) * mm});
            skArc(sketch, "E532", {"start": v(-38.28, 26.08) * mm, "mid": v(-38.22, 26.13) * mm, "end": v(-38.14, 26.15) * mm});
            skArc(sketch, "E533", {"start": v(-38.14, 26.15) * mm, "mid": v(-38.11, 26.15) * mm, "end": v(-38.1, 26.13) * mm});
            skArc(sketch, "E534", {"start": v(-38.1, 26.13) * mm, "mid": v(-38.03, 26.07) * mm, "end": v(-37.96, 26) * mm});
            skArc(sketch, "E535", {"start": v(-37.96, 26) * mm, "mid": v(-37.89, 25.91) * mm, "end": v(-37.82, 25.83) * mm});
            skArc(sketch, "E536", {"start": v(-37.82, 25.83) * mm, "mid": v(-37.74, 25.73) * mm, "end": v(-37.66, 25.62) * mm});
            skArc(sketch, "E537.MirrorCS", {"start": v(42.04, 31.12) * mm, "mid": v(41.93, 30.98) * mm, "end": v(41.82, 30.84) * mm});
            skArc(sketch, "E538.MirrorCS", {"start": v(44.06, 28.48) * mm, "mid": v(44.08, 28.48) * mm, "end": v(44.1, 28.5) * mm});
            skArc(sketch, "E539.MirrorCS", {"start": v(44.1, 28.5) * mm, "mid": v(44.16, 28.55) * mm, "end": v(44.21, 28.6) * mm});
            skArc(sketch, "E540.MirrorCS", {"start": v(41.82, 30.84) * mm, "mid": v(41.73, 30.72) * mm, "end": v(41.63, 30.6) * mm});
            skArc(sketch, "E541.MirrorCS", {"start": v(44.21, 28.6) * mm, "mid": v(44.27, 28.68) * mm, "end": v(44.33, 28.75) * mm});
            skArc(sketch, "E542.MirrorCS", {"start": v(41.63, 30.6) * mm, "mid": v(41.55, 30.5) * mm, "end": v(41.47, 30.39) * mm});
            skArc(sketch, "E543.MirrorCS", {"start": v(44.33, 28.75) * mm, "mid": v(44.4, 28.83) * mm, "end": v(44.47, 28.92) * mm});
            skArc(sketch, "E544.MirrorCS", {"start": v(41.47, 30.39) * mm, "mid": v(41.47, 30.38) * mm, "end": v(41.46, 30.36) * mm});
            skArc(sketch, "E545.MirrorCS", {"start": v(42, 29.34) * mm, "mid": v(41.78, 29.5) * mm, "end": v(41.55, 29.66) * mm});
            skArc(sketch, "E546.MirrorCS", {"start": v(43.41, 28.94) * mm, "mid": v(43.52, 28.85) * mm, "end": v(43.64, 28.76) * mm});
            skArc(sketch, "E547.MirrorCS", {"start": v(39.43, 30.3) * mm, "mid": v(39.6, 30.52) * mm, "end": v(39.79, 30.74) * mm});
            skArc(sketch, "E548.MirrorCS", {"start": v(41.1, 29.89) * mm, "mid": v(41.05, 29.88) * mm, "end": v(41, 29.86) * mm});
            skArc(sketch, "E549.MirrorCS", {"start": v(41.46, 30.36) * mm, "mid": v(41.47, 30.35) * mm, "end": v(41.48, 30.34) * mm});
            skArc(sketch, "E550.MirrorCS", {"start": v(41.55, 29.66) * mm, "mid": v(41.42, 29.74) * mm, "end": v(41.28, 29.82) * mm});
            skArc(sketch, "E551.MirrorCS", {"start": v(43.64, 28.76) * mm, "mid": v(43.74, 28.69) * mm, "end": v(43.84, 28.61) * mm});
            skArc(sketch, "E552.MirrorCS", {"start": v(42.46, 29.65) * mm, "mid": v(42.63, 29.53) * mm, "end": v(42.8, 29.4) * mm});
            skArc(sketch, "E553.MirrorCS", {"start": v(39.79, 30.74) * mm, "mid": v(39.8, 30.75) * mm, "end": v(39.8, 30.77) * mm});
            skArc(sketch, "E554.MirrorCS", {"start": v(41, 29.86) * mm, "mid": v(40.97, 29.8) * mm, "end": v(40.93, 29.76) * mm});
            skArc(sketch, "E555.MirrorCS", {"start": v(41.48, 30.34) * mm, "mid": v(41.57, 30.27) * mm, "end": v(41.67, 30.2) * mm});
            skArc(sketch, "E556.MirrorCS", {"start": v(41.28, 29.82) * mm, "mid": v(41.2, 29.86) * mm, "end": v(41.1, 29.89) * mm});
            skArc(sketch, "E557.MirrorCS", {"start": v(40.2, 31.25) * mm, "mid": v(40.41, 31.5) * mm, "end": v(40.62, 31.74) * mm});
            skArc(sketch, "E558.MirrorCS", {"start": v(42.76, 28.78) * mm, "mid": v(42.57, 28.93) * mm, "end": v(42.37, 29.07) * mm});
            skArc(sketch, "E559.MirrorCS", {"start": v(40.05, 31.23) * mm, "mid": v(40.1, 31.21) * mm, "end": v(40.15, 31.22) * mm});
            skArc(sketch, "E560.MirrorCS", {"start": v(39.12, 31.84) * mm, "mid": v(39.59, 31.53) * mm, "end": v(40.05, 31.23) * mm});
            skArc(sketch, "E561.MirrorCS", {"start": v(43.33, 28.34) * mm, "mid": v(43.22, 28.43) * mm, "end": v(43.1, 28.52) * mm});
            skArc(sketch, "E562.MirrorCS", {"start": v(43.84, 28.61) * mm, "mid": v(43.92, 28.55) * mm, "end": v(44, 28.5) * mm});
            skArc(sketch, "E563.MirrorCS", {"start": v(42.8, 29.4) * mm, "mid": v(42.98, 29.28) * mm, "end": v(43.14, 29.15) * mm});
            skArc(sketch, "E564.MirrorCS", {"start": v(39.8, 30.77) * mm, "mid": v(39.8, 30.78) * mm, "end": v(39.78, 30.8) * mm});
            skArc(sketch, "E565.MirrorCS", {"start": v(41.89, 30.04) * mm, "mid": v(42.02, 29.95) * mm, "end": v(42.15, 29.86) * mm});
            skArc(sketch, "E566.MirrorCS", {"start": v(40.93, 29.76) * mm, "mid": v(40.75, 29.54) * mm, "end": v(40.57, 29.31) * mm});
            skArc(sketch, "E567.MirrorCS", {"start": v(41.67, 30.2) * mm, "mid": v(41.78, 30.12) * mm, "end": v(41.89, 30.04) * mm});
            skArc(sketch, "E568.MirrorCS", {"start": v(40.62, 31.74) * mm, "mid": v(40.86, 32.01) * mm, "end": v(41.1, 32.29) * mm});
            skArc(sketch, "E569.MirrorCS", {"start": v(43.1, 28.52) * mm, "mid": v(42.93, 28.65) * mm, "end": v(42.76, 28.78) * mm});
            skArc(sketch, "E570.MirrorCS", {"start": v(38.27, 32.4) * mm, "mid": v(38.7, 32.12) * mm, "end": v(39.12, 31.84) * mm});
            skArc(sketch, "E571.MirrorCS", {"start": v(44, 28.5) * mm, "mid": v(44.03, 28.48) * mm, "end": v(44.06, 28.48) * mm});
            skArc(sketch, "E572.MirrorCS", {"start": v(42.64, 31.88) * mm, "mid": v(42.34, 31.5) * mm, "end": v(42.04, 31.12) * mm});
            skArc(sketch, "E573.MirrorCS", {"start": v(40.15, 31.22) * mm, "mid": v(40.18, 31.23) * mm, "end": v(40.2, 31.25) * mm});
            skArc(sketch, "E574.MirrorCS", {"start": v(43.26, 32.71) * mm, "mid": v(42.95, 32.3) * mm, "end": v(42.64, 31.88) * mm});
            skArc(sketch, "E575.MirrorCS", {"start": v(43.84, 33.52) * mm, "mid": v(43.55, 33.12) * mm, "end": v(43.26, 32.71) * mm});
            skLineSegment(sketch, "E576.MirrorCS", {"start": v(43.77, 27.97) * mm, "end": v(43.33, 28.34) * mm});
            skLineSegment(sketch, "E577.MirrorCS", {"start": v(43.42, 27.4) * mm, "end": v(43.77, 27.97) * mm});
            skArc(sketch, "E578.MirrorCS", {"start": v(43.14, 29.15) * mm, "mid": v(43.28, 29.04) * mm, "end": v(43.41, 28.94) * mm});
            skArc(sketch, "E579.MirrorCS", {"start": v(39.78, 30.8) * mm, "mid": v(39.17, 31.25) * mm, "end": v(38.55, 31.7) * mm});
            skArc(sketch, "E580.MirrorCS", {"start": v(40.15, 28.79) * mm, "mid": v(39.9, 28.49) * mm, "end": v(39.67, 28.2) * mm});
            skArc(sketch, "E581.MirrorCS", {"start": v(42.15, 29.86) * mm, "mid": v(42.3, 29.76) * mm, "end": v(42.46, 29.65) * mm});
            skArc(sketch, "E582.MirrorCS", {"start": v(40.57, 29.31) * mm, "mid": v(40.36, 29.05) * mm, "end": v(40.15, 28.79) * mm});
            skArc(sketch, "E583.MirrorCS", {"start": v(39.02, 29.8) * mm, "mid": v(39.23, 30.05) * mm, "end": v(39.43, 30.3) * mm});
            skArc(sketch, "E584.MirrorCS", {"start": v(48.35, 31.08) * mm, "mid": v(48.33, 31.05) * mm, "end": v(48.32, 31.02) * mm});
            skArc(sketch, "E585.MirrorCS", {"start": v(38.54, 29.21) * mm, "mid": v(38.78, 29.5) * mm, "end": v(39.02, 29.8) * mm});
            skArc(sketch, "E586.MirrorCS", {"start": v(41.1, 32.29) * mm, "mid": v(41.38, 32.61) * mm, "end": v(41.66, 32.94) * mm});
            skArc(sketch, "E587.MirrorCS", {"start": v(42.37, 29.07) * mm, "mid": v(42.19, 29.2) * mm, "end": v(42, 29.34) * mm});
            skArc(sketch, "E588.MirrorCS", {"start": v(48.32, 31.02) * mm, "mid": v(48.33, 31) * mm, "end": v(48.34, 30.97) * mm});
            skArc(sketch, "E589.MirrorCS", {"start": v(51.1, 32.8) * mm, "mid": v(50.98, 32.9) * mm, "end": v(50.86, 33) * mm});
            skArc(sketch, "E590.MirrorCS", {"start": v(48.34, 30.97) * mm, "mid": v(48.37, 30.93) * mm, "end": v(48.4, 30.9) * mm});
            skArc(sketch, "E591.MirrorCS", {"start": v(45.48, 27.89) * mm, "mid": v(45.34, 27.72) * mm, "end": v(45.2, 27.55) * mm});
            skArc(sketch, "E592.MirrorCS", {"start": v(43.98, 33.71) * mm, "mid": v(43.95, 33.72) * mm, "end": v(43.91, 33.7) * mm});
            skArc(sketch, "E593.MirrorCS", {"start": v(50.86, 33) * mm, "mid": v(50.76, 33.08) * mm, "end": v(50.65, 33.16) * mm});
            skArc(sketch, "E594.MirrorCS", {"start": v(48.4, 30.9) * mm, "mid": v(48.45, 30.85) * mm, "end": v(48.5, 30.81) * mm});
            skArc(sketch, "E595.MirrorCS", {"start": v(45.2, 27.55) * mm, "mid": v(45.18, 27.5) * mm, "end": v(45.16, 27.43) * mm});
            skArc(sketch, "E596.MirrorCS", {"start": v(46.98, 31.98) * mm, "mid": v(47.07, 31.93) * mm, "end": v(47.17, 31.9) * mm});
            skArc(sketch, "E597.MirrorCS", {"start": v(43.91, 33.7) * mm, "mid": v(43.9, 33.68) * mm, "end": v(43.88, 33.64) * mm});
            skArc(sketch, "E598.MirrorCS", {"start": v(50.65, 33.16) * mm, "mid": v(50.56, 33.23) * mm, "end": v(50.47, 33.3) * mm});
            skArc(sketch, "E599.MirrorCS", {"start": v(43.88, 33.64) * mm, "mid": v(43.87, 33.58) * mm, "end": v(43.84, 33.52) * mm});
            skArc(sketch, "E600.MirrorCS", {"start": v(45.07, 32.84) * mm, "mid": v(44.85, 33) * mm, "end": v(44.64, 33.18) * mm});
            skArc(sketch, "E601.MirrorCS", {"start": v(49.85, 29.2) * mm, "mid": v(49.7, 29.33) * mm, "end": v(49.54, 29.46) * mm});
            skArc(sketch, "E602.MirrorCS", {"start": v(48.5, 30.81) * mm, "mid": v(48.55, 30.77) * mm, "end": v(48.6, 30.74) * mm});
            skArc(sketch, "E603.MirrorCS", {"start": v(45.18, 27.3) * mm, "mid": v(45.22, 27.2) * mm, "end": v(45.27, 27.1) * mm});
            skArc(sketch, "E604.MirrorCS", {"start": v(47.17, 31.9) * mm, "mid": v(47.22, 31.9) * mm, "end": v(47.27, 31.93) * mm});
            skArc(sketch, "E605.MirrorCS", {"start": v(51.26, 33.3) * mm, "mid": v(51.39, 33.18) * mm, "end": v(51.52, 33.07) * mm});
            skArc(sketch, "E606.MirrorCS", {"start": v(50.47, 33.3) * mm, "mid": v(50.45, 33.3) * mm, "end": v(50.43, 33.31) * mm});
            skArc(sketch, "E607.MirrorCS", {"start": v(44.28, 33.48) * mm, "mid": v(44.23, 33.52) * mm, "end": v(44.18, 33.57) * mm});
            skArc(sketch, "E608.MirrorCS", {"start": v(44.64, 33.18) * mm, "mid": v(44.46, 33.33) * mm, "end": v(44.28, 33.48) * mm});
            skArc(sketch, "E609.MirrorCS", {"start": v(49.54, 29.46) * mm, "mid": v(49.36, 29.6) * mm, "end": v(49.17, 29.74) * mm});
            skArc(sketch, "E610.MirrorCS", {"start": v(44.92, 26.88) * mm, "mid": v(44.86, 26.94) * mm, "end": v(44.78, 26.96) * mm});
            skLineSegment(sketch, "E611.MirrorCS", {"start": v(38.42, 26.65) * mm, "end": v(38.72, 26.28) * mm});
            skArc(sketch, "E612.MirrorCS", {"start": v(48.6, 30.74) * mm, "mid": v(48.68, 30.68) * mm, "end": v(48.76, 30.63) * mm});
            skArc(sketch, "E613.MirrorCS", {"start": v(44.66, 29.15) * mm, "mid": v(44.82, 29.35) * mm, "end": v(45, 29.54) * mm});
            skArc(sketch, "E614.MirrorCS", {"start": v(47.27, 31.93) * mm, "mid": v(47.31, 31.97) * mm, "end": v(47.36, 32.02) * mm});
            skArc(sketch, "E615.MirrorCS", {"start": v(51.52, 33.07) * mm, "mid": v(51.69, 32.94) * mm, "end": v(51.85, 32.8) * mm});
            skLineSegment(sketch, "E616.MirrorCS", {"start": v(51.04, 34.26) * mm, "end": v(50.7, 33.78) * mm});
            skArc(sketch, "E617.MirrorCS", {"start": v(44.18, 33.57) * mm, "mid": v(44.14, 33.62) * mm, "end": v(44.08, 33.67) * mm});
            skArc(sketch, "E618.MirrorCS", {"start": v(50.43, 33.31) * mm, "mid": v(50.4, 33.3) * mm, "end": v(50.39, 33.3) * mm});
            skArc(sketch, "E619.MirrorCS", {"start": v(49.4, 30.14) * mm, "mid": v(49.59, 30) * mm, "end": v(49.77, 29.85) * mm});
            skArc(sketch, "E620.MirrorCS", {"start": v(49.17, 29.74) * mm, "mid": v(49, 29.88) * mm, "end": v(48.81, 30.02) * mm});
            skArc(sketch, "E621.MirrorCS", {"start": v(45, 33.47) * mm, "mid": v(45.19, 33.32) * mm, "end": v(45.38, 33.16) * mm});
            skArc(sketch, "E622.MirrorCS", {"start": v(44.78, 26.96) * mm, "mid": v(44.75, 26.96) * mm, "end": v(44.73, 26.94) * mm});
            skArc(sketch, "E623.MirrorCS", {"start": v(38.28, 26.08) * mm, "mid": v(38.22, 26.13) * mm, "end": v(38.14, 26.15) * mm});
            skArc(sketch, "E624.MirrorCS", {"start": v(37.33, 32.58) * mm, "mid": v(37.3, 32.6) * mm, "end": v(37.27, 32.6) * mm});
            skArc(sketch, "E625.MirrorCS", {"start": v(48.76, 30.63) * mm, "mid": v(48.9, 30.52) * mm, "end": v(49.06, 30.4) * mm});
            skLineSegment(sketch, "E626.MirrorCS", {"start": v(44.22, 34.12) * mm, "end": v(44.73, 33.68) * mm});
            skArc(sketch, "E627.MirrorCS", {"start": v(45.24, 26.3) * mm, "mid": v(45.08, 26.6) * mm, "end": v(44.92, 26.88) * mm});
            skLineSegment(sketch, "E628.MirrorCS", {"start": v(39.67, 28.2) * mm, "end": v(38.42, 26.65) * mm});
            skLineSegment(sketch, "E629.MirrorCS", {"start": v(50.13, 28.18) * mm, "end": v(50.42, 28.74) * mm});
            skArc(sketch, "E630.MirrorCS", {"start": v(48.04, 32.75) * mm, "mid": v(48.25, 32.97) * mm, "end": v(48.46, 33.2) * mm});
            skArc(sketch, "E631.MirrorCS", {"start": v(52.03, 32.08) * mm, "mid": v(51.86, 32.2) * mm, "end": v(51.7, 32.32) * mm});
            skArc(sketch, "E632.MirrorCS", {"start": v(45, 29.54) * mm, "mid": v(45.2, 29.76) * mm, "end": v(45.4, 29.98) * mm});
            skArc(sketch, "E633.MirrorCS", {"start": v(47.36, 32.02) * mm, "mid": v(47.51, 32.19) * mm, "end": v(47.67, 32.35) * mm});
            skArc(sketch, "E634.MirrorCS", {"start": v(51.78, 27.14) * mm, "mid": v(51.59, 27.46) * mm, "end": v(51.4, 27.8) * mm});
            skArc(sketch, "E635.MirrorCS", {"start": v(49.35, 32.22) * mm, "mid": v(49.15, 32) * mm, "end": v(48.95, 31.79) * mm});
            skArc(sketch, "E636.MirrorCS", {"start": v(51.65, 30.26) * mm, "mid": v(51.8, 30.42) * mm, "end": v(51.96, 30.58) * mm});
            skArc(sketch, "E637.MirrorCS", {"start": v(51.85, 32.8) * mm, "mid": v(52.03, 32.67) * mm, "end": v(52.2, 32.54) * mm});
            skArc(sketch, "E638.MirrorCS", {"start": v(47.2, 29.86) * mm, "mid": v(46.91, 29.54) * mm, "end": v(46.63, 29.22) * mm});
            skArc(sketch, "E639.MirrorCS", {"start": v(46.2, 32.53) * mm, "mid": v(46.45, 32.34) * mm, "end": v(46.7, 32.16) * mm});
            skArc(sketch, "E640.MirrorCS", {"start": v(51.13, 29.7) * mm, "mid": v(51.24, 29.82) * mm, "end": v(51.35, 29.95) * mm});
            skArc(sketch, "E641.MirrorCS", {"start": v(50.09, 33) * mm, "mid": v(49.91, 32.82) * mm, "end": v(49.74, 32.64) * mm});
            skLineSegment(sketch, "E642.MirrorCS", {"start": v(47.94, 30.7) * mm, "end": v(47.2, 29.86) * mm});
            skArc(sketch, "E643.MirrorCS", {"start": v(45.8, 32.83) * mm, "mid": v(46, 32.68) * mm, "end": v(46.2, 32.53) * mm});
            skLineSegment(sketch, "E644.MirrorCS", {"start": v(50.7, 33.78) * mm, "end": v(51.26, 33.3) * mm});
            skArc(sketch, "E645.MirrorCS", {"start": v(44.4, 26.48) * mm, "mid": v(44.29, 26.33) * mm, "end": v(44.19, 26.18) * mm});
            skArc(sketch, "E646.MirrorCS", {"start": v(44.08, 33.67) * mm, "mid": v(44.04, 33.7) * mm, "end": v(43.98, 33.71) * mm});
            skLineSegment(sketch, "E647.MirrorCS", {"start": v(50.66, 29.15) * mm, "end": v(51.13, 29.7) * mm});
            skArc(sketch, "E648.MirrorCS", {"start": v(50.39, 33.3) * mm, "mid": v(50.24, 33.14) * mm, "end": v(50.09, 33) * mm});
            skLineSegment(sketch, "E649.MirrorCS", {"start": v(48.81, 30.02) * mm, "end": v(47.94, 30.7) * mm});
            skArc(sketch, "E650.MirrorCS", {"start": v(45.38, 33.16) * mm, "mid": v(45.59, 33) * mm, "end": v(45.8, 32.83) * mm});
            skArc(sketch, "E651.MirrorCS", {"start": v(44.57, 26.73) * mm, "mid": v(44.48, 26.6) * mm, "end": v(44.4, 26.48) * mm});
            skLineSegment(sketch, "E652.MirrorCS", {"start": v(49.77, 29.85) * mm, "end": v(50.66, 29.15) * mm});
            skArc(sketch, "E653.MirrorCS", {"start": v(44.73, 26.94) * mm, "mid": v(44.65, 26.84) * mm, "end": v(44.57, 26.73) * mm});
            skArc(sketch, "E654.MirrorCS", {"start": v(38.14, 26.15) * mm, "mid": v(38.11, 26.15) * mm, "end": v(38.1, 26.13) * mm});
            skArc(sketch, "E655.MirrorCS", {"start": v(37.27, 32.6) * mm, "mid": v(37.26, 32.6) * mm, "end": v(37.26, 32.6) * mm});
            skArc(sketch, "E656.MirrorCS", {"start": v(49.06, 30.4) * mm, "mid": v(49.23, 30.27) * mm, "end": v(49.4, 30.14) * mm});
            skArc(sketch, "E657.MirrorCS", {"start": v(42.78, 35.7) * mm, "mid": v(43, 35.4) * mm, "end": v(43.22, 35.1) * mm});
            skArc(sketch, "E658.MirrorCS", {"start": v(38.72, 26.28) * mm, "mid": v(38.9, 26.04) * mm, "end": v(39.05, 25.8) * mm});
            skArc(sketch, "E659.MirrorCS", {"start": v(44.73, 33.68) * mm, "mid": v(44.86, 33.57) * mm, "end": v(45, 33.47) * mm});
            skArc(sketch, "E660.MirrorCS", {"start": v(42.96, 26.5) * mm, "mid": v(43.18, 26.96) * mm, "end": v(43.42, 27.4) * mm});
            skArc(sketch, "E661.MirrorCS", {"start": v(38.55, 31.7) * mm, "mid": v(37.94, 32.14) * mm, "end": v(37.33, 32.58) * mm});
            skArc(sketch, "E662.MirrorCS", {"start": v(45.56, 32.45) * mm, "mid": v(45.31, 32.64) * mm, "end": v(45.07, 32.84) * mm});
            skArc(sketch, "E663.MirrorCS", {"start": v(50.05, 29.04) * mm, "mid": v(49.95, 29.12) * mm, "end": v(49.85, 29.2) * mm});
            skArc(sketch, "E664.MirrorCS", {"start": v(51.37, 32.58) * mm, "mid": v(51.23, 32.69) * mm, "end": v(51.1, 32.8) * mm});
            skLineSegment(sketch, "E665.MirrorCS", {"start": v(46.81, 31.48) * mm, "end": v(45.56, 32.45) * mm});
            skLineSegment(sketch, "E666.MirrorCS", {"start": v(50.42, 28.74) * mm, "end": v(50.05, 29.04) * mm});
            skArc(sketch, "E667.MirrorCS", {"start": v(51.7, 32.32) * mm, "mid": v(51.54, 32.45) * mm, "end": v(51.37, 32.58) * mm});
            skLineSegment(sketch, "E668.MirrorCS", {"start": v(45.8, 30.42) * mm, "end": v(46.81, 31.48) * mm});
            skLineSegment(sketch, "E669.MirrorCS", {"start": v(48.46, 33.2) * mm, "end": v(49.53, 34.33) * mm});
            skArc(sketch, "E670.MirrorCS", {"start": v(45.4, 29.98) * mm, "mid": v(45.6, 30.2) * mm, "end": v(45.8, 30.42) * mm});
            skArc(sketch, "E671.MirrorCS", {"start": v(36.83, 27.1) * mm, "mid": v(36.87, 27.17) * mm, "end": v(36.91, 27.24) * mm});
            skLineSegment(sketch, "E672.MirrorCS", {"start": v(52.09, 28.85) * mm, "end": v(51.55, 28.28) * mm});
            skArc(sketch, "E673.MirrorCS", {"start": v(47.67, 32.35) * mm, "mid": v(47.85, 32.55) * mm, "end": v(48.04, 32.75) * mm});
            skArc(sketch, "E674.MirrorCS", {"start": v(35.27, 30.1) * mm, "mid": v(35.17, 29.97) * mm, "end": v(35.06, 29.84) * mm});
            skArc(sketch, "E675.MirrorCS", {"start": v(44.47, 28.92) * mm, "mid": v(44.56, 29.04) * mm, "end": v(44.66, 29.15) * mm});
            skArc(sketch, "E676.MirrorCS", {"start": v(48.62, 31.41) * mm, "mid": v(48.48, 31.25) * mm, "end": v(48.35, 31.08) * mm});
            skArc(sketch, "E677.MirrorCS", {"start": v(51.4, 27.8) * mm, "mid": v(51.33, 27.85) * mm, "end": v(51.25, 27.87) * mm});
            skArc(sketch, "E678.MirrorCS", {"start": v(48.95, 31.79) * mm, "mid": v(48.79, 31.6) * mm, "end": v(48.62, 31.41) * mm});
            skArc(sketch, "E679.MirrorCS", {"start": v(51.96, 30.58) * mm, "mid": v(52.1, 30.72) * mm, "end": v(52.25, 30.86) * mm});
            skArc(sketch, "E680.MirrorCS", {"start": v(46.02, 28.52) * mm, "mid": v(45.75, 28.2) * mm, "end": v(45.48, 27.89) * mm});
            skArc(sketch, "E681.MirrorCS", {"start": v(49.74, 32.64) * mm, "mid": v(49.54, 32.43) * mm, "end": v(49.35, 32.22) * mm});
            skArc(sketch, "E682.MirrorCS", {"start": v(51.35, 29.95) * mm, "mid": v(51.5, 30.1) * mm, "end": v(51.65, 30.26) * mm});
            skArc(sketch, "E683.MirrorCS", {"start": v(46.63, 29.22) * mm, "mid": v(46.32, 28.87) * mm, "end": v(46.02, 28.52) * mm});
            skArc(sketch, "E684.MirrorCS", {"start": v(46.7, 32.16) * mm, "mid": v(46.84, 32.07) * mm, "end": v(46.98, 31.98) * mm});
            skLineSegment(sketch, "E685.MirrorCS", {"start": v(37.5, 32.99) * mm, "end": v(37.74, 32.8) * mm});
            skArc(sketch, "E686.MirrorCS", {"start": v(38.1, 26.13) * mm, "mid": v(38.03, 26.07) * mm, "end": v(37.96, 26) * mm});
            skArc(sketch, "E687.MirrorCS", {"start": v(37.26, 32.6) * mm, "mid": v(37.15, 32.47) * mm, "end": v(37.05, 32.34) * mm});
            skArc(sketch, "E688.MirrorCS", {"start": v(43.22, 35.1) * mm, "mid": v(43.28, 35.05) * mm, "end": v(43.36, 35.03) * mm});
            skArc(sketch, "E689.MirrorCS", {"start": v(35.83, 32.85) * mm, "mid": v(36, 33.03) * mm, "end": v(36.13, 33.25) * mm});
            skArc(sketch, "E690.MirrorCS", {"start": v(44.93, 35.63) * mm, "mid": v(44.78, 35.27) * mm, "end": v(44.6, 34.9) * mm});
            skLineSegment(sketch, "E691.MirrorCS", {"start": v(49.53, 34.33) * mm, "end": v(49.19, 34.78) * mm});
            skArc(sketch, "E692.MirrorCS", {"start": v(45.5, 26.76) * mm, "mid": v(45.78, 26.3) * mm, "end": v(46.03, 25.84) * mm});
            skArc(sketch, "E693.MirrorCS", {"start": v(44.19, 26.18) * mm, "mid": v(43.97, 25.82) * mm, "end": v(43.77, 25.45) * mm});
            skArc(sketch, "E694.MirrorCS", {"start": v(45.77, 25.08) * mm, "mid": v(45.67, 25.37) * mm, "end": v(45.55, 25.66) * mm});
            skArc(sketch, "E695.MirrorCS", {"start": v(36.91, 27.24) * mm, "mid": v(36.92, 27.26) * mm, "end": v(36.92, 27.28) * mm});
            skArc(sketch, "E696.MirrorCS", {"start": v(35.06, 29.84) * mm, "mid": v(34.98, 29.73) * mm, "end": v(34.9, 29.61) * mm});
            skArc(sketch, "E697.MirrorCS", {"start": v(42.57, 22.63) * mm, "mid": v(42.54, 22.82) * mm, "end": v(42.52, 23) * mm});
            skLineSegment(sketch, "E698.MirrorCS", {"start": v(49.48, 35.17) * mm, "end": v(49.77, 34.69) * mm});
            skArc(sketch, "E699.MirrorCS", {"start": v(45.16, 27.43) * mm, "mid": v(45.16, 27.36) * mm, "end": v(45.18, 27.3) * mm});
            skLineSegment(sketch, "E700.MirrorCS", {"start": v(43.09, 34.63) * mm, "end": v(42.74, 35.06) * mm});
            skArc(sketch, "E701.MirrorCS", {"start": v(49.2, 35.7) * mm, "mid": v(49.34, 35.43) * mm, "end": v(49.48, 35.17) * mm});
            skLineSegment(sketch, "E702.MirrorCS", {"start": v(41.66, 32.94) * mm, "end": v(43.09, 34.63) * mm});
            skArc(sketch, "E703.MirrorCS", {"start": v(51.25, 27.87) * mm, "mid": v(51.23, 27.86) * mm, "end": v(51.22, 27.85) * mm});
            skLineSegment(sketch, "E704.MirrorCS", {"start": v(37.28, 27.7) * mm, "end": v(38.54, 29.21) * mm});
            skArc(sketch, "E705.MirrorCS", {"start": v(43.79, 35.6) * mm, "mid": v(43.96, 35.87) * mm, "end": v(44.12, 36.14) * mm});
            skArc(sketch, "E706.MirrorCS", {"start": v(43.45, 35.08) * mm, "mid": v(43.62, 35.34) * mm, "end": v(43.79, 35.6) * mm});
            skArc(sketch, "E707.MirrorCS", {"start": v(37.74, 32.8) * mm, "mid": v(38, 32.6) * mm, "end": v(38.27, 32.4) * mm});
            skLineSegment(sketch, "E708.MirrorCS", {"start": v(37.9, 33.83) * mm, "end": v(37.5, 32.99) * mm});
            skArc(sketch, "E709.MirrorCS", {"start": v(37.96, 26) * mm, "mid": v(37.89, 25.91) * mm, "end": v(37.82, 25.83) * mm});
            skArc(sketch, "E710.MirrorCS", {"start": v(37.05, 32.34) * mm, "mid": v(36.93, 32.19) * mm, "end": v(36.82, 32.04) * mm});
            skArc(sketch, "E711.MirrorCS", {"start": v(43.36, 35.03) * mm, "mid": v(43.41, 35.05) * mm, "end": v(43.45, 35.08) * mm});
            skArc(sketch, "E712.MirrorCS", {"start": v(43.25, 22.76) * mm, "mid": v(43.26, 22.6) * mm, "end": v(43.28, 22.45) * mm});
            skArc(sketch, "E713.MirrorCS", {"start": v(36.13, 33.25) * mm, "mid": v(36.16, 33.3) * mm, "end": v(36.17, 33.36) * mm});
            skArc(sketch, "E714.MirrorCS", {"start": v(48.8, 35.37) * mm, "mid": v(48.67, 35.66) * mm, "end": v(48.56, 35.96) * mm});
            skArc(sketch, "E715.MirrorCS", {"start": v(42.66, 25.63) * mm, "mid": v(42.8, 26.07) * mm, "end": v(42.96, 26.5) * mm});
            skLineSegment(sketch, "E716.MirrorCS", {"start": v(44.6, 34.9) * mm, "end": v(44.22, 34.12) * mm});
            skArc(sketch, "E717.MirrorCS", {"start": v(49.19, 34.78) * mm, "mid": v(48.98, 35.07) * mm, "end": v(48.8, 35.37) * mm});
            skArc(sketch, "E718.MirrorCS", {"start": v(43.77, 25.45) * mm, "mid": v(43.6, 25.1) * mm, "end": v(43.48, 24.72) * mm});
            skArc(sketch, "E719.MirrorCS", {"start": v(45.55, 25.66) * mm, "mid": v(45.4, 25.99) * mm, "end": v(45.24, 26.3) * mm});
            skArc(sketch, "E720.MirrorCS", {"start": v(46.03, 25.84) * mm, "mid": v(46.23, 25.39) * mm, "end": v(46.39, 24.92) * mm});
            skArc(sketch, "E721.MirrorCS", {"start": v(42.51, 24.7) * mm, "mid": v(42.57, 25.17) * mm, "end": v(42.66, 25.63) * mm});
            skArc(sketch, "E722.MirrorCS", {"start": v(34.9, 29.61) * mm, "mid": v(34.83, 29.52) * mm, "end": v(34.76, 29.42) * mm});
            skArc(sketch, "E723.MirrorCS", {"start": v(36.92, 27.28) * mm, "mid": v(36.9, 27.36) * mm, "end": v(36.85, 27.42) * mm});
            skArc(sketch, "E724.MirrorCS", {"start": v(41.49, 37.24) * mm, "mid": v(41.36, 37.75) * mm, "end": v(41.3, 38.28) * mm});
            skArc(sketch, "E725.MirrorCS", {"start": v(39.05, 24.7) * mm, "mid": v(38.96, 24.93) * mm, "end": v(38.86, 25.14) * mm});
            skLineSegment(sketch, "E726.MirrorCS", {"start": v(49.77, 34.69) * mm, "end": v(50.16, 35.14) * mm});
            skArc(sketch, "E727.MirrorCS", {"start": v(45.27, 27.1) * mm, "mid": v(45.38, 26.93) * mm, "end": v(45.5, 26.76) * mm});
            skArc(sketch, "E728.MirrorCS", {"start": v(42.52, 23) * mm, "mid": v(42.5, 23.32) * mm, "end": v(42.49, 23.64) * mm});
            skArc(sketch, "E729.MirrorCS", {"start": v(41.96, 36.17) * mm, "mid": v(41.7, 36.7) * mm, "end": v(41.49, 37.24) * mm});
            skArc(sketch, "E730.MirrorCS", {"start": v(45.95, 24.32) * mm, "mid": v(45.88, 24.7) * mm, "end": v(45.77, 25.08) * mm});
            skArc(sketch, "E731.MirrorCS", {"start": v(51.1, 27.68) * mm, "mid": v(51.03, 27.57) * mm, "end": v(50.96, 27.46) * mm});
            skArc(sketch, "E732.MirrorCS", {"start": v(42.67, 22.3) * mm, "mid": v(42.61, 22.47) * mm, "end": v(42.57, 22.63) * mm});
            skArc(sketch, "E733.MirrorCS", {"start": v(51.22, 27.85) * mm, "mid": v(51.16, 27.76) * mm, "end": v(51.1, 27.68) * mm});
            skArc(sketch, "E734.MirrorCS", {"start": v(44.69, 37.56) * mm, "mid": v(44.75, 38.07) * mm, "end": v(44.74, 38.58) * mm});
            skLineSegment(sketch, "E735.MirrorCS", {"start": v(36.77, 28.07) * mm, "end": v(37.28, 27.7) * mm});
            skArc(sketch, "E736.MirrorCS", {"start": v(44.12, 36.14) * mm, "mid": v(44.25, 36.36) * mm, "end": v(44.37, 36.6) * mm});
            skArc(sketch, "E737.MirrorCS", {"start": v(39.97, 23.41) * mm, "mid": v(40, 23.22) * mm, "end": v(40.02, 23.02) * mm});
            skArc(sketch, "E738.MirrorCS", {"start": v(43.28, 22.45) * mm, "mid": v(43.3, 22.33) * mm, "end": v(43.35, 22.2) * mm});
            skArc(sketch, "E739.MirrorCS", {"start": v(36.17, 33.36) * mm, "mid": v(36.16, 33.42) * mm, "end": v(36.15, 33.47) * mm});
            skArc(sketch, "E740.MirrorCS", {"start": v(39.05, 25.8) * mm, "mid": v(39.21, 25.5) * mm, "end": v(39.36, 25.2) * mm});
            skArc(sketch, "E741.MirrorCS", {"start": v(51.77, 35.73) * mm, "mid": v(51.46, 34.97) * mm, "end": v(51.04, 34.26) * mm});
            skArc(sketch, "E742.MirrorCS", {"start": v(43.24, 23.19) * mm, "mid": v(43.24, 22.97) * mm, "end": v(43.25, 22.76) * mm});
            skArc(sketch, "E743.MirrorCS", {"start": v(48.56, 35.96) * mm, "mid": v(48.48, 36.29) * mm, "end": v(48.42, 36.62) * mm});
            skArc(sketch, "E744.MirrorCS", {"start": v(43.3, 23.98) * mm, "mid": v(43.26, 23.59) * mm, "end": v(43.24, 23.19) * mm});
            skArc(sketch, "E745.MirrorCS", {"start": v(42.36, 36.32) * mm, "mid": v(42.56, 36.01) * mm, "end": v(42.78, 35.7) * mm});
            skArc(sketch, "E746.MirrorCS", {"start": v(46.57, 23.99) * mm, "mid": v(46.6, 23.5) * mm, "end": v(46.58, 23.02) * mm});
            skArc(sketch, "E747.MirrorCS", {"start": v(43.48, 24.72) * mm, "mid": v(43.38, 24.36) * mm, "end": v(43.3, 23.98) * mm});
            skArc(sketch, "E748.MirrorCS", {"start": v(43.3, 40.38) * mm, "mid": v(43.18, 40.37) * mm, "end": v(43.05, 40.36) * mm});
            skArc(sketch, "E749.MirrorCS", {"start": v(42.1, 36.8) * mm, "mid": v(42.23, 36.56) * mm, "end": v(42.36, 36.32) * mm});
            skArc(sketch, "E750.MirrorCS", {"start": v(46.39, 24.92) * mm, "mid": v(46.5, 24.46) * mm, "end": v(46.57, 23.99) * mm});
            skArc(sketch, "E751.MirrorCS", {"start": v(34.76, 29.42) * mm, "mid": v(34.75, 29.4) * mm, "end": v(34.76, 29.37) * mm});
            skArc(sketch, "E752.MirrorCS", {"start": v(41.84, 37.67) * mm, "mid": v(41.94, 37.22) * mm, "end": v(42.1, 36.8) * mm});
            skArc(sketch, "E753.MirrorCS", {"start": v(38.86, 25.14) * mm, "mid": v(38.72, 25.39) * mm, "end": v(38.58, 25.63) * mm});
            skArc(sketch, "E754.MirrorCS", {"start": v(41.81, 38.55) * mm, "mid": v(41.8, 38.1) * mm, "end": v(41.84, 37.67) * mm});
            skArc(sketch, "E755.MirrorCS", {"start": v(50.16, 35.14) * mm, "mid": v(50.54, 35.65) * mm, "end": v(50.86, 36.2) * mm});
            skLineSegment(sketch, "E756.MirrorCS", {"start": v(36.05, 34.38) * mm, "end": v(36.6, 33.77) * mm});
            skArc(sketch, "E757.MirrorCS", {"start": v(42.49, 23.64) * mm, "mid": v(42.48, 24.17) * mm, "end": v(42.51, 24.7) * mm});
            skArc(sketch, "E758.MirrorCS", {"start": v(45.14, 36.3) * mm, "mid": v(45.04, 35.97) * mm, "end": v(44.93, 35.63) * mm});
            skLineSegment(sketch, "E759.MirrorCS", {"start": v(51.55, 28.28) * mm, "end": v(51.96, 27.74) * mm});
            skArc(sketch, "E760.MirrorCS", {"start": v(49.86, 27.55) * mm, "mid": v(49.99, 27.87) * mm, "end": v(50.13, 28.18) * mm});
            skArc(sketch, "E761.MirrorCS", {"start": v(45.26, 36.98) * mm, "mid": v(45.2, 36.64) * mm, "end": v(45.14, 36.3) * mm});
            skArc(sketch, "E762.MirrorCS", {"start": v(50.96, 27.46) * mm, "mid": v(50.89, 27.34) * mm, "end": v(50.81, 27.22) * mm});
            skArc(sketch, "E763.MirrorCS", {"start": v(42.74, 35.06) * mm, "mid": v(42.33, 35.6) * mm, "end": v(41.96, 36.17) * mm});
            skArc(sketch, "E764.MirrorCS", {"start": v(45.3, 37.7) * mm, "mid": v(45.29, 37.34) * mm, "end": v(45.26, 36.98) * mm});
            skArc(sketch, "E765.MirrorCS", {"start": v(46.03, 23.53) * mm, "mid": v(46, 23.93) * mm, "end": v(45.95, 24.32) * mm});
            skArc(sketch, "E766.MirrorCS", {"start": v(50.13, 24) * mm, "mid": v(50.15, 23.88) * mm, "end": v(50.18, 23.76) * mm});
            skArc(sketch, "E767.MirrorCS", {"start": v(45.2, 38.79) * mm, "mid": v(45.27, 38.25) * mm, "end": v(45.3, 37.7) * mm});
            skArc(sketch, "E768.MirrorCS", {"start": v(46, 22.8) * mm, "mid": v(46.03, 23.17) * mm, "end": v(46.03, 23.53) * mm});
            skArc(sketch, "E769.MirrorCS", {"start": v(50.1, 24.3) * mm, "mid": v(50.11, 24.15) * mm, "end": v(50.13, 24) * mm});
            skArc(sketch, "E770.MirrorCS", {"start": v(45.86, 22.24) * mm, "mid": v(45.95, 22.52) * mm, "end": v(46, 22.8) * mm});
            skArc(sketch, "E771.MirrorCS", {"start": v(48.96, 36.6) * mm, "mid": v(49, 36.37) * mm, "end": v(49.05, 36.14) * mm});
            skArc(sketch, "E772.MirrorCS", {"start": v(36.54, 31.68) * mm, "mid": v(36.38, 31.47) * mm, "end": v(36.23, 31.27) * mm});
            skArc(sketch, "E773.MirrorCS", {"start": v(48.93, 37.2) * mm, "mid": v(48.94, 36.9) * mm, "end": v(48.96, 36.6) * mm});
            skArc(sketch, "E774.MirrorCS", {"start": v(44.37, 36.6) * mm, "mid": v(44.56, 37.06) * mm, "end": v(44.69, 37.56) * mm});
            skArc(sketch, "E775.MirrorCS", {"start": v(40.02, 23.02) * mm, "mid": v(40.04, 22.8) * mm, "end": v(40.04, 22.59) * mm});
            skArc(sketch, "E776.MirrorCS", {"start": v(34.8, 40.57) * mm, "mid": v(34.73, 40.43) * mm, "end": v(34.67, 40.29) * mm});
            skArc(sketch, "E777.MirrorCS", {"start": v(39.86, 23.87) * mm, "mid": v(39.92, 23.64) * mm, "end": v(39.97, 23.41) * mm});
            skArc(sketch, "E778.MirrorCS", {"start": v(48.42, 38.4) * mm, "mid": v(48.44, 38.54) * mm, "end": v(48.48, 38.68) * mm});
            skArc(sketch, "E779.MirrorCS", {"start": v(43.25, 41.07) * mm, "mid": v(43.42, 41.06) * mm, "end": v(43.6, 41.02) * mm});
            skArc(sketch, "E780.MirrorCS", {"start": v(43.45, 21.96) * mm, "mid": v(43.68, 21.64) * mm, "end": v(43.98, 21.4) * mm});
            skArc(sketch, "E781.MirrorCS", {"start": v(36.2, 28.46) * mm, "mid": v(36.37, 28.35) * mm, "end": v(36.53, 28.25) * mm});
            skArc(sketch, "E782.MirrorCS", {"start": v(50.81, 27.22) * mm, "mid": v(50.64, 26.9) * mm, "end": v(50.48, 26.59) * mm});
            skArc(sketch, "E783.MirrorCS", {"start": v(36.07, 33.6) * mm, "mid": v(35.98, 33.7) * mm, "end": v(35.89, 33.8) * mm});
            skArc(sketch, "E784.MirrorCS", {"start": v(39.64, 24.53) * mm, "mid": v(39.76, 24.2) * mm, "end": v(39.86, 23.87) * mm});
            skArc(sketch, "E785.MirrorCS", {"start": v(37.82, 25.83) * mm, "mid": v(37.74, 25.73) * mm, "end": v(37.66, 25.62) * mm});
            skArc(sketch, "E786.MirrorCS", {"start": v(43.35, 22.2) * mm, "mid": v(43.4, 22.08) * mm, "end": v(43.45, 21.96) * mm});
            skArc(sketch, "E787.MirrorCS", {"start": v(35.85, 28.68) * mm, "mid": v(36.03, 28.57) * mm, "end": v(36.2, 28.46) * mm});
            skArc(sketch, "E788.MirrorCS", {"start": v(36.82, 32.04) * mm, "mid": v(36.68, 31.86) * mm, "end": v(36.54, 31.68) * mm});
            skArc(sketch, "E789.MirrorCS", {"start": v(38.56, 35.49) * mm, "mid": v(38.44, 35.1) * mm, "end": v(38.3, 34.7) * mm});
            skArc(sketch, "E790.MirrorCS", {"start": v(39.36, 25.2) * mm, "mid": v(39.51, 24.87) * mm, "end": v(39.64, 24.53) * mm});
            skArc(sketch, "E791.MirrorCS", {"start": v(36.15, 33.47) * mm, "mid": v(36.11, 33.54) * mm, "end": v(36.07, 33.6) * mm});
            skArc(sketch, "E792.MirrorCS", {"start": v(48.42, 36.62) * mm, "mid": v(48.39, 37.04) * mm, "end": v(48.38, 37.45) * mm});
            skArc(sketch, "E793.MirrorCS", {"start": v(46.58, 23.02) * mm, "mid": v(46.53, 22.6) * mm, "end": v(46.43, 22.17) * mm});
            skArc(sketch, "E794.MirrorCS", {"start": v(43.05, 40.36) * mm, "mid": v(42.95, 40.34) * mm, "end": v(42.86, 40.31) * mm});
            skArc(sketch, "E795.MirrorCS", {"start": v(38.58, 25.63) * mm, "mid": v(38.43, 25.86) * mm, "end": v(38.28, 26.08) * mm});
            skArc(sketch, "E796.MirrorCS", {"start": v(34.76, 29.37) * mm, "mid": v(34.78, 29.35) * mm, "end": v(34.8, 29.33) * mm});
            skArc(sketch, "E797.MirrorCS", {"start": v(52.84, 26.06) * mm, "mid": v(52.96, 25.63) * mm, "end": v(53.02, 25.2) * mm});
            skArc(sketch, "E798.MirrorCS", {"start": v(50.86, 36.2) * mm, "mid": v(51.08, 36.8) * mm, "end": v(51.21, 37.4) * mm});
            skArc(sketch, "E799.MirrorCS", {"start": v(51.96, 27.74) * mm, "mid": v(52.24, 27.34) * mm, "end": v(52.49, 26.92) * mm});
            skArc(sketch, "E800.MirrorCS", {"start": v(50.5, 40.23) * mm, "mid": v(50.7, 40.17) * mm, "end": v(50.87, 40.09) * mm});
            skArc(sketch, "E801.MirrorCS", {"start": v(43.9, 40.25) * mm, "mid": v(43.82, 40.29) * mm, "end": v(43.73, 40.32) * mm});
            skArc(sketch, "E802.MirrorCS", {"start": v(50.18, 23.76) * mm, "mid": v(50.22, 23.66) * mm, "end": v(50.27, 23.56) * mm});
            skArc(sketch, "E803.MirrorCS", {"start": v(42.47, 40) * mm, "mid": v(42.22, 39.7) * mm, "end": v(42.03, 39.35) * mm});
            skArc(sketch, "E804.MirrorCS", {"start": v(39.36, 23.34) * mm, "mid": v(39.3, 23.7) * mm, "end": v(39.24, 24.05) * mm});
            skArc(sketch, "E805.MirrorCS", {"start": v(49.48, 26.1) * mm, "mid": v(49.55, 26.46) * mm, "end": v(49.64, 26.82) * mm});
            skArc(sketch, "E806.MirrorCS", {"start": v(53, 29.77) * mm, "mid": v(52.74, 29.53) * mm, "end": v(52.5, 29.28) * mm});
            skArc(sketch, "E807.MirrorCS", {"start": v(42.86, 21.9) * mm, "mid": v(42.76, 22.1) * mm, "end": v(42.67, 22.3) * mm});
            skArc(sketch, "E808.MirrorCS", {"start": v(49.1, 39.68) * mm, "mid": v(49.23, 39.8) * mm, "end": v(49.37, 39.9) * mm});
            skLineSegment(sketch, "E809.MirrorCS", {"start": v(52.52, 32.3) * mm, "end": v(53.25, 31.8) * mm});
            skArc(sketch, "E810.MirrorCS", {"start": v(49.05, 36.14) * mm, "mid": v(49.12, 35.91) * mm, "end": v(49.2, 35.7) * mm});
            skArc(sketch, "E811.MirrorCS", {"start": v(34.57, 41.28) * mm, "mid": v(34.66, 41.39) * mm, "end": v(34.77, 41.5) * mm});
            skArc(sketch, "E812.MirrorCS", {"start": v(44.74, 38.58) * mm, "mid": v(44.66, 39.05) * mm, "end": v(44.52, 39.5) * mm});
            skArc(sketch, "E813.MirrorCS", {"start": v(45.37, 21.57) * mm, "mid": v(45.65, 21.88) * mm, "end": v(45.86, 22.24) * mm});
            skArc(sketch, "E814.MirrorCS", {"start": v(36.23, 31.27) * mm, "mid": v(36.05, 31.05) * mm, "end": v(35.87, 30.83) * mm});
            skArc(sketch, "E815.MirrorCS", {"start": v(50.15, 25.44) * mm, "mid": v(50.12, 25.1) * mm, "end": v(50.1, 24.74) * mm});
            skArc(sketch, "E816.MirrorCS", {"start": v(49.78, 23.7) * mm, "mid": v(49.63, 24.13) * mm, "end": v(49.52, 24.57) * mm});
            skArc(sketch, "E817.MirrorCS", {"start": v(36.53, 28.25) * mm, "mid": v(36.65, 28.16) * mm, "end": v(36.77, 28.07) * mm});
            skArc(sketch, "E818.MirrorCS", {"start": v(50.48, 26.59) * mm, "mid": v(50.36, 26.3) * mm, "end": v(50.27, 26.03) * mm});
            skArc(sketch, "E819.MirrorCS", {"start": v(48.96, 37.9) * mm, "mid": v(48.94, 37.55) * mm, "end": v(48.93, 37.2) * mm});
            skArc(sketch, "E820.MirrorCS", {"start": v(48.48, 38.68) * mm, "mid": v(48.54, 38.82) * mm, "end": v(48.6, 38.97) * mm});
            skArc(sketch, "E821.MirrorCS", {"start": v(32.74, 29.5) * mm, "mid": v(32.58, 29.53) * mm, "end": v(32.42, 29.58) * mm});
            skArc(sketch, "E822.MirrorCS", {"start": v(50.64, 22.62) * mm, "mid": v(50.38, 22.8) * mm, "end": v(50.17, 23.03) * mm});
            skArc(sketch, "E823.MirrorCS", {"start": v(44.91, 20.6) * mm, "mid": v(44.64, 20.54) * mm, "end": v(44.35, 20.54) * mm});
            skArc(sketch, "E824.MirrorCS", {"start": v(52.31, 26.02) * mm, "mid": v(52.23, 26.25) * mm, "end": v(52.13, 26.48) * mm});
            skArc(sketch, "E825.MirrorCS", {"start": v(52.43, 25.45) * mm, "mid": v(52.38, 25.74) * mm, "end": v(52.31, 26.02) * mm});
            skArc(sketch, "E826.MirrorCS", {"start": v(38.3, 34.7) * mm, "mid": v(38.1, 34.27) * mm, "end": v(37.9, 33.83) * mm});
            skArc(sketch, "E827.MirrorCS", {"start": v(48.38, 37.45) * mm, "mid": v(48.38, 37.75) * mm, "end": v(48.38, 38.05) * mm});
            skArc(sketch, "E828.MirrorCS", {"start": v(42.51, 40.88) * mm, "mid": v(42.7, 40.96) * mm, "end": v(42.9, 41.03) * mm});
            skArc(sketch, "E829.MirrorCS", {"start": v(52.48, 24.8) * mm, "mid": v(52.46, 25.13) * mm, "end": v(52.43, 25.45) * mm});
            skArc(sketch, "E830.MirrorCS", {"start": v(52.46, 24.17) * mm, "mid": v(52.48, 24.48) * mm, "end": v(52.48, 24.8) * mm});
            skArc(sketch, "E831.MirrorCS", {"start": v(52.37, 23.72) * mm, "mid": v(52.43, 23.94) * mm, "end": v(52.46, 24.17) * mm});
            skArc(sketch, "E832.MirrorCS", {"start": v(42.86, 40.31) * mm, "mid": v(42.78, 40.26) * mm, "end": v(42.7, 40.2) * mm});
            skArc(sketch, "E833.MirrorCS", {"start": v(50.73, 39.21) * mm, "mid": v(50.58, 39.32) * mm, "end": v(50.41, 39.41) * mm});
            skArc(sketch, "E834.MirrorCS", {"start": v(35.33, 41.15) * mm, "mid": v(35.26, 41.1) * mm, "end": v(35.2, 41.06) * mm});
            skArc(sketch, "E835.MirrorCS", {"start": v(41.84, 40.29) * mm, "mid": v(41.98, 40.47) * mm, "end": v(42.14, 40.63) * mm});
            skArc(sketch, "E836.MirrorCS", {"start": v(51.98, 23.13) * mm, "mid": v(52.22, 23.4) * mm, "end": v(52.37, 23.72) * mm});
            skArc(sketch, "E837.MirrorCS", {"start": v(34.8, 29.33) * mm, "mid": v(34.9, 29.27) * mm, "end": v(35, 29.2) * mm});
            skArc(sketch, "E838.MirrorCS", {"start": v(35.2, 28.44) * mm, "mid": v(34.83, 28.64) * mm, "end": v(34.46, 28.83) * mm});
            skArc(sketch, "E839.MirrorCS", {"start": v(51.21, 37.4) * mm, "mid": v(51.24, 37.94) * mm, "end": v(51.17, 38.48) * mm});
            skArc(sketch, "E840.MirrorCS", {"start": v(37.1, 34.83) * mm, "mid": v(37.3, 35.28) * mm, "end": v(37.5, 35.73) * mm});
            skArc(sketch, "E841.MirrorCS", {"start": v(50.75, 23.04) * mm, "mid": v(51.06, 22.9) * mm, "end": v(51.39, 22.88) * mm});
            skLineSegment(sketch, "E842.MirrorCS", {"start": v(36.6, 33.77) * mm, "end": v(37.1, 34.83) * mm});
            skArc(sketch, "E843.MirrorCS", {"start": v(52.49, 26.92) * mm, "mid": v(52.69, 26.5) * mm, "end": v(52.84, 26.06) * mm});
            skArc(sketch, "E844.MirrorCS", {"start": v(43.73, 40.32) * mm, "mid": v(43.64, 40.35) * mm, "end": v(43.54, 40.37) * mm});
            skArc(sketch, "E845.MirrorCS", {"start": v(50.27, 23.56) * mm, "mid": v(50.48, 23.27) * mm, "end": v(50.75, 23.04) * mm});
            skArc(sketch, "E846.MirrorCS", {"start": v(42.03, 39.35) * mm, "mid": v(41.89, 38.96) * mm, "end": v(41.81, 38.55) * mm});
            skArc(sketch, "E847.MirrorCS", {"start": v(49.64, 26.82) * mm, "mid": v(49.74, 27.19) * mm, "end": v(49.86, 27.55) * mm});
            skArc(sketch, "E848.MirrorCS", {"start": v(36.73, 26.94) * mm, "mid": v(36.78, 27.02) * mm, "end": v(36.83, 27.1) * mm});
            skArc(sketch, "E849.MirrorCS", {"start": v(52.5, 29.28) * mm, "mid": v(52.29, 29.07) * mm, "end": v(52.09, 28.85) * mm});
            skArc(sketch, "E850.MirrorCS", {"start": v(49.37, 39.9) * mm, "mid": v(49.54, 40.01) * mm, "end": v(49.72, 40.1) * mm});
            skLineSegment(sketch, "E851.MirrorCS", {"start": v(52.9, 31.47) * mm, "end": v(52.3, 31.88) * mm});
            skArc(sketch, "E852.MirrorCS", {"start": v(34.77, 41.5) * mm, "mid": v(34.87, 41.6) * mm, "end": v(34.98, 41.7) * mm});
            skArc(sketch, "E853.MirrorCS", {"start": v(49.43, 25.5) * mm, "mid": v(49.45, 25.8) * mm, "end": v(49.48, 26.1) * mm});
            skArc(sketch, "E854.MirrorCS", {"start": v(44.95, 39.7) * mm, "mid": v(45.1, 39.26) * mm, "end": v(45.2, 38.79) * mm});
            skArc(sketch, "E855.MirrorCS", {"start": v(35.87, 30.83) * mm, "mid": v(35.7, 30.62) * mm, "end": v(35.54, 30.4) * mm});
            skArc(sketch, "E856.MirrorCS", {"start": v(50.1, 24.74) * mm, "mid": v(50.1, 24.52) * mm, "end": v(50.1, 24.3) * mm});
            skArc(sketch, "E857.MirrorCS", {"start": v(36.25, 26.17) * mm, "mid": v(36.43, 26.47) * mm, "end": v(36.61, 26.76) * mm});
            skArc(sketch, "E858.MirrorCS", {"start": v(49.52, 24.57) * mm, "mid": v(49.45, 25.03) * mm, "end": v(49.43, 25.5) * mm});
            skArc(sketch, "E859.MirrorCS", {"start": v(44.68, 21.26) * mm, "mid": v(45.05, 21.36) * mm, "end": v(45.37, 21.57) * mm});
            skArc(sketch, "E860.MirrorCS", {"start": v(43.99, 40.86) * mm, "mid": v(44.28, 40.67) * mm, "end": v(44.53, 40.41) * mm});
            skArc(sketch, "E861.MirrorCS", {"start": v(50.27, 26.03) * mm, "mid": v(50.2, 25.74) * mm, "end": v(50.15, 25.44) * mm});
            skArc(sketch, "E862.MirrorCS", {"start": v(32.16, 29.65) * mm, "mid": v(32.04, 29.69) * mm, "end": v(31.93, 29.72) * mm});
            skArc(sketch, "E863.MirrorCS", {"start": v(52.13, 26.48) * mm, "mid": v(51.96, 26.81) * mm, "end": v(51.78, 27.14) * mm});
            skArc(sketch, "E864.MirrorCS", {"start": v(43.98, 21.4) * mm, "mid": v(44.32, 21.28) * mm, "end": v(44.68, 21.26) * mm});
            skArc(sketch, "E865.MirrorCS", {"start": v(32.42, 29.58) * mm, "mid": v(32.3, 29.61) * mm, "end": v(32.16, 29.65) * mm});
            skArc(sketch, "E866.MirrorCS", {"start": v(49.05, 38.4) * mm, "mid": v(49, 38.15) * mm, "end": v(48.96, 37.9) * mm});
            skArc(sketch, "E867.MirrorCS", {"start": v(54.24, 30.72) * mm, "mid": v(54.16, 30.72) * mm, "end": v(54.09, 30.7) * mm});
            skArc(sketch, "E868.MirrorCS", {"start": v(37.66, 25.62) * mm, "mid": v(37.29, 25.1) * mm, "end": v(36.94, 24.58) * mm});
            skArc(sketch, "E869.MirrorCS", {"start": v(51.46, 22.43) * mm, "mid": v(51.04, 22.48) * mm, "end": v(50.64, 22.62) * mm});
            skArc(sketch, "E870.MirrorCS", {"start": v(45.58, 20.95) * mm, "mid": v(45.26, 20.75) * mm, "end": v(44.91, 20.6) * mm});
            skArc(sketch, "E871.MirrorCS", {"start": v(48.38, 38.05) * mm, "mid": v(48.4, 38.23) * mm, "end": v(48.42, 38.4) * mm});
            skArc(sketch, "E872.MirrorCS", {"start": v(42.9, 41.03) * mm, "mid": v(43.07, 41.06) * mm, "end": v(43.25, 41.07) * mm});
            skArc(sketch, "E873.MirrorCS", {"start": v(49.22, 38.8) * mm, "mid": v(49.12, 38.6) * mm, "end": v(49.05, 38.4) * mm});
            skArc(sketch, "E874.MirrorCS", {"start": v(46.09, 21.48) * mm, "mid": v(45.86, 21.2) * mm, "end": v(45.58, 20.95) * mm});
            skArc(sketch, "E875.MirrorCS", {"start": v(49.48, 39.14) * mm, "mid": v(49.34, 38.98) * mm, "end": v(49.22, 38.8) * mm});
            skArc(sketch, "E876.MirrorCS", {"start": v(35.25, 29.05) * mm, "mid": v(35.4, 28.96) * mm, "end": v(35.53, 28.88) * mm});
            skArc(sketch, "E877.MirrorCS", {"start": v(42.7, 40.2) * mm, "mid": v(42.58, 40.1) * mm, "end": v(42.47, 40) * mm});
            skArc(sketch, "E878.MirrorCS", {"start": v(50.41, 39.41) * mm, "mid": v(50.26, 39.46) * mm, "end": v(50.1, 39.47) * mm});
            skArc(sketch, "E879.MirrorCS", {"start": v(35.2, 41.06) * mm, "mid": v(35.13, 41) * mm, "end": v(35.06, 40.92) * mm});
            skArc(sketch, "E880.MirrorCS", {"start": v(46.43, 22.17) * mm, "mid": v(46.28, 21.81) * mm, "end": v(46.09, 21.48) * mm});
            skArc(sketch, "E881.MirrorCS", {"start": v(42.14, 40.63) * mm, "mid": v(42.32, 40.77) * mm, "end": v(42.51, 40.88) * mm});
            skArc(sketch, "E882.MirrorCS", {"start": v(35, 29.2) * mm, "mid": v(35.13, 29.12) * mm, "end": v(35.25, 29.05) * mm});
            skArc(sketch, "E883.MirrorCS", {"start": v(34.46, 28.83) * mm, "mid": v(34.25, 28.92) * mm, "end": v(34.05, 29.02) * mm});
            skArc(sketch, "E884.MirrorCS", {"start": v(51.17, 38.48) * mm, "mid": v(51.02, 38.88) * mm, "end": v(50.73, 39.21) * mm});
            skArc(sketch, "E885.MirrorCS", {"start": v(37.5, 35.73) * mm, "mid": v(37.64, 36.12) * mm, "end": v(37.75, 36.51) * mm});
            skArc(sketch, "E886.MirrorCS", {"start": v(41.6, 39.84) * mm, "mid": v(41.7, 40.07) * mm, "end": v(41.84, 40.29) * mm});
            skArc(sketch, "E887.MirrorCS", {"start": v(51.39, 22.88) * mm, "mid": v(51.7, 22.95) * mm, "end": v(51.98, 23.13) * mm});
            skArc(sketch, "E888.MirrorCS", {"start": v(35.03, 32.12) * mm, "mid": v(35.43, 32.48) * mm, "end": v(35.83, 32.85) * mm});
            skArc(sketch, "E889.MirrorCS", {"start": v(41.4, 39.28) * mm, "mid": v(41.49, 39.56) * mm, "end": v(41.6, 39.84) * mm});
            skArc(sketch, "E890.MirrorCS", {"start": v(43.54, 40.37) * mm, "mid": v(43.43, 40.38) * mm, "end": v(43.3, 40.38) * mm});
            skArc(sketch, "E891.MirrorCS", {"start": v(36.85, 27.42) * mm, "mid": v(36.44, 27.68) * mm, "end": v(36.03, 27.94) * mm});
            skArc(sketch, "E892.MirrorCS", {"start": v(35.66, 42.06) * mm, "mid": v(35.86, 42.08) * mm, "end": v(36.07, 42.09) * mm});
            skArc(sketch, "E893.MirrorCS", {"start": v(41.3, 38.28) * mm, "mid": v(41.32, 38.78) * mm, "end": v(41.4, 39.28) * mm});
            skArc(sketch, "E894.MirrorCS", {"start": v(35.34, 35.35) * mm, "mid": v(35.67, 34.85) * mm, "end": v(36.05, 34.38) * mm});
            skArc(sketch, "E895.MirrorCS", {"start": v(39.24, 24.05) * mm, "mid": v(39.15, 24.38) * mm, "end": v(39.05, 24.7) * mm});
            skArc(sketch, "E896.MirrorCS", {"start": v(34.98, 41.7) * mm, "mid": v(35.08, 41.77) * mm, "end": v(35.18, 41.86) * mm});
            skArc(sketch, "E897.MirrorCS", {"start": v(44.07, 40.13) * mm, "mid": v(43.99, 40.2) * mm, "end": v(43.9, 40.25) * mm});
            skArc(sketch, "E898.MirrorCS", {"start": v(32.26, 30.02) * mm, "mid": v(32.46, 30.16) * mm, "end": v(32.67, 30.31) * mm});
            skArc(sketch, "E899.MirrorCS", {"start": v(52.3, 31.88) * mm, "mid": v(52.16, 31.98) * mm, "end": v(52.03, 32.08) * mm});
            skArc(sketch, "E900.MirrorCS", {"start": v(39.43, 22.61) * mm, "mid": v(39.4, 22.98) * mm, "end": v(39.36, 23.34) * mm});
            skArc(sketch, "E901.MirrorCS", {"start": v(35.54, 30.4) * mm, "mid": v(35.4, 30.25) * mm, "end": v(35.27, 30.1) * mm});
            skArc(sketch, "E902.MirrorCS", {"start": v(44.52, 39.5) * mm, "mid": v(44.33, 39.84) * mm, "end": v(44.07, 40.13) * mm});
            skLineSegment(sketch, "E903.MirrorCS", {"start": v(52.25, 30.86) * mm, "end": v(52.9, 31.47) * mm});
            skArc(sketch, "E904.MirrorCS", {"start": v(36.61, 26.76) * mm, "mid": v(36.67, 26.85) * mm, "end": v(36.73, 26.94) * mm});
            skArc(sketch, "E905.MirrorCS", {"start": v(44.53, 40.41) * mm, "mid": v(44.76, 40.08) * mm, "end": v(44.95, 39.7) * mm});
            skArc(sketch, "E906.MirrorCS", {"start": v(36.45, 41.23) * mm, "mid": v(36.25, 41.26) * mm, "end": v(36.06, 41.28) * mm});
            skArc(sketch, "E907.MirrorCS", {"start": v(31.93, 29.72) * mm, "mid": v(31.91, 29.73) * mm, "end": v(31.9, 29.73) * mm});
            skArc(sketch, "E908.MirrorCS", {"start": v(43.29, 21.2) * mm, "mid": v(43.05, 21.53) * mm, "end": v(42.86, 21.9) * mm});
            skArc(sketch, "E909.MirrorCS", {"start": v(36.42, 23.6) * mm, "mid": v(36.24, 23.16) * mm, "end": v(36.09, 22.7) * mm});
            skArc(sketch, "E910.MirrorCS", {"start": v(35.88, 25.45) * mm, "mid": v(36.06, 25.82) * mm, "end": v(36.25, 26.17) * mm});
            skArc(sketch, "E911.MirrorCS", {"start": v(43.8, 20.74) * mm, "mid": v(43.52, 20.95) * mm, "end": v(43.29, 21.2) * mm});
            skArc(sketch, "E912.MirrorCS", {"start": v(48.6, 38.97) * mm, "mid": v(48.73, 39.18) * mm, "end": v(48.85, 39.38) * mm});
            skArc(sketch, "E913.MirrorCS", {"start": v(36.94, 24.58) * mm, "mid": v(36.66, 24.1) * mm, "end": v(36.42, 23.6) * mm});
            skArc(sketch, "E914.MirrorCS", {"start": v(37.24, 40.63) * mm, "mid": v(37.02, 40.89) * mm, "end": v(36.75, 41.1) * mm});
            skArc(sketch, "E915.MirrorCS", {"start": v(54.09, 30.7) * mm, "mid": v(54, 30.67) * mm, "end": v(53.93, 30.62) * mm});
            skArc(sketch, "E916.MirrorCS", {"start": v(50.17, 23.03) * mm, "mid": v(49.95, 23.36) * mm, "end": v(49.78, 23.7) * mm});
            skArc(sketch, "E917.MirrorCS", {"start": v(49.8, 39.38) * mm, "mid": v(49.63, 39.27) * mm, "end": v(49.48, 39.14) * mm});
            skArc(sketch, "E918.MirrorCS", {"start": v(38.72, 36.26) * mm, "mid": v(38.65, 35.87) * mm, "end": v(38.56, 35.49) * mm});
            skArc(sketch, "E919.MirrorCS", {"start": v(38.75, 38.7) * mm, "mid": v(38.82, 37.9) * mm, "end": v(38.8, 37.1) * mm});
            skArc(sketch, "E920.MirrorCS", {"start": v(33.57, 29.2) * mm, "mid": v(33.34, 29.3) * mm, "end": v(33.11, 29.38) * mm});
            skArc(sketch, "E921.MirrorCS", {"start": v(52.2, 22.68) * mm, "mid": v(51.85, 22.5) * mm, "end": v(51.46, 22.43) * mm});
            skArc(sketch, "E922.MirrorCS", {"start": v(35.53, 28.88) * mm, "mid": v(35.7, 28.78) * mm, "end": v(35.85, 28.68) * mm});
            skArc(sketch, "E923.MirrorCS", {"start": v(50.1, 39.47) * mm, "mid": v(49.94, 39.44) * mm, "end": v(49.8, 39.38) * mm});
            skArc(sketch, "E924.MirrorCS", {"start": v(35.06, 40.92) * mm, "mid": v(34.99, 40.83) * mm, "end": v(34.92, 40.74) * mm});
            skArc(sketch, "E925.MirrorCS", {"start": v(34.05, 29.02) * mm, "mid": v(33.81, 29.11) * mm, "end": v(33.57, 29.2) * mm});
            skArc(sketch, "E926.MirrorCS", {"start": v(52.75, 23.34) * mm, "mid": v(52.52, 22.97) * mm, "end": v(52.2, 22.68) * mm});
            skArc(sketch, "E927.MirrorCS", {"start": v(37.75, 36.51) * mm, "mid": v(37.83, 36.88) * mm, "end": v(37.89, 37.26) * mm});
            skArc(sketch, "E928.MirrorCS", {"start": v(36.03, 27.94) * mm, "mid": v(35.61, 28.2) * mm, "end": v(35.2, 28.44) * mm});
            skArc(sketch, "E929.MirrorCS", {"start": v(36.07, 42.09) * mm, "mid": v(36.29, 42.07) * mm, "end": v(36.5, 42.03) * mm});
            skArc(sketch, "E930.MirrorCS", {"start": v(51.25, 39.81) * mm, "mid": v(51.64, 39.34) * mm, "end": v(51.89, 38.79) * mm});
            skArc(sketch, "E931.MirrorCS", {"start": v(50.87, 40.09) * mm, "mid": v(51.07, 39.96) * mm, "end": v(51.25, 39.81) * mm});
            skArc(sketch, "E932.MirrorCS", {"start": v(35.18, 41.86) * mm, "mid": v(35.24, 41.9) * mm, "end": v(35.32, 41.95) * mm});
            skArc(sketch, "E933.MirrorCS", {"start": v(32.67, 30.31) * mm, "mid": v(32.91, 30.48) * mm, "end": v(33.16, 30.66) * mm});
            skArc(sketch, "E934.MirrorCS", {"start": v(50.13, 40.23) * mm, "mid": v(50.32, 40.24) * mm, "end": v(50.5, 40.23) * mm});
            skArc(sketch, "E935.MirrorCS", {"start": v(34.85, 36.46) * mm, "mid": v(35.07, 35.9) * mm, "end": v(35.34, 35.35) * mm});
            skArc(sketch, "E936.MirrorCS", {"start": v(49.72, 40.1) * mm, "mid": v(49.92, 40.18) * mm, "end": v(50.13, 40.23) * mm});
            skArc(sketch, "E937.MirrorCS", {"start": v(36.06, 41.28) * mm, "mid": v(35.85, 41.28) * mm, "end": v(35.65, 41.25) * mm});
            skArc(sketch, "E938.MirrorCS", {"start": v(31.9, 29.73) * mm, "mid": v(31.9, 29.74) * mm, "end": v(31.9, 29.75) * mm});
            skArc(sketch, "E939.MirrorCS", {"start": v(48.85, 39.38) * mm, "mid": v(48.97, 39.54) * mm, "end": v(49.1, 39.68) * mm});
            skArc(sketch, "E940.MirrorCS", {"start": v(40.04, 22.59) * mm, "mid": v(40.04, 22.28) * mm, "end": v(40.03, 21.97) * mm});
            skArc(sketch, "E941.MirrorCS", {"start": v(39.16, 20.49) * mm, "mid": v(39.27, 20.8) * mm, "end": v(39.34, 21.11) * mm});
            skArc(sketch, "E942.MirrorCS", {"start": v(36.75, 41.1) * mm, "mid": v(36.6, 41.18) * mm, "end": v(36.45, 41.23) * mm});
            skArc(sketch, "E943.MirrorCS", {"start": v(53.93, 30.62) * mm, "mid": v(53.71, 30.43) * mm, "end": v(53.5, 30.24) * mm});
            skArc(sketch, "E944.MirrorCS", {"start": v(34.67, 40.29) * mm, "mid": v(34.63, 40.15) * mm, "end": v(34.6, 40.01) * mm});
            skArc(sketch, "E945.MirrorCS", {"start": v(35.54, 24.72) * mm, "mid": v(35.7, 25.09) * mm, "end": v(35.88, 25.45) * mm});
            skArc(sketch, "E946.MirrorCS", {"start": v(43.6, 41.02) * mm, "mid": v(43.8, 40.95) * mm, "end": v(43.99, 40.86) * mm});
            skArc(sketch, "E947.MirrorCS", {"start": v(37.62, 39.93) * mm, "mid": v(37.45, 40.29) * mm, "end": v(37.24, 40.63) * mm});
            skArc(sketch, "E948.MirrorCS", {"start": v(35.3, 24.09) * mm, "mid": v(35.42, 24.4) * mm, "end": v(35.54, 24.72) * mm});
            skArc(sketch, "E949.MirrorCS", {"start": v(34.92, 40.74) * mm, "mid": v(34.86, 40.66) * mm, "end": v(34.8, 40.57) * mm});
            skArc(sketch, "E950.MirrorCS", {"start": v(37.85, 39.06) * mm, "mid": v(37.76, 39.5) * mm, "end": v(37.62, 39.93) * mm});
            skArc(sketch, "E951.MirrorCS", {"start": v(35.12, 23.25) * mm, "mid": v(35.2, 23.67) * mm, "end": v(35.3, 24.09) * mm});
            skArc(sketch, "E952.MirrorCS", {"start": v(33.11, 29.38) * mm, "mid": v(32.92, 29.44) * mm, "end": v(32.74, 29.5) * mm});
            skArc(sketch, "E953.MirrorCS", {"start": v(54.5, 30.64) * mm, "mid": v(54.37, 30.69) * mm, "end": v(54.24, 30.72) * mm});
            skArc(sketch, "E954.MirrorCS", {"start": v(38.8, 37.1) * mm, "mid": v(38.78, 36.68) * mm, "end": v(38.72, 36.26) * mm});
            skArc(sketch, "E955.MirrorCS", {"start": v(38.38, 40.1) * mm, "mid": v(38.6, 39.42) * mm, "end": v(38.75, 38.7) * mm});
            skArc(sketch, "E956.MirrorCS", {"start": v(37.75, 41.2) * mm, "mid": v(38.1, 40.67) * mm, "end": v(38.38, 40.1) * mm});
            skArc(sketch, "E957.MirrorCS", {"start": v(36.9, 41.88) * mm, "mid": v(37.36, 41.59) * mm, "end": v(37.75, 41.2) * mm});
            skArc(sketch, "E958.MirrorCS", {"start": v(37.93, 38.08) * mm, "mid": v(37.91, 38.57) * mm, "end": v(37.85, 39.06) * mm});
            skArc(sketch, "E959.MirrorCS", {"start": v(37.89, 37.26) * mm, "mid": v(37.92, 37.67) * mm, "end": v(37.93, 38.08) * mm});
            skArc(sketch, "E960.MirrorCS", {"start": v(36.5, 42.03) * mm, "mid": v(36.7, 41.97) * mm, "end": v(36.9, 41.88) * mm});
            skArc(sketch, "E961.MirrorCS", {"start": v(53.02, 25.2) * mm, "mid": v(53.04, 24.75) * mm, "end": v(53.02, 24.31) * mm});
            skArc(sketch, "E962.MirrorCS", {"start": v(34.09, 31.34) * mm, "mid": v(34.56, 31.72) * mm, "end": v(35.03, 32.12) * mm});
            skArc(sketch, "E963.MirrorCS", {"start": v(33.16, 30.66) * mm, "mid": v(33.63, 31) * mm, "end": v(34.09, 31.34) * mm});
            skArc(sketch, "E964.MirrorCS", {"start": v(35.32, 41.95) * mm, "mid": v(35.48, 42.02) * mm, "end": v(35.66, 42.06) * mm});
            skArc(sketch, "E965.MirrorCS", {"start": v(31.9, 29.75) * mm, "mid": v(32.08, 29.89) * mm, "end": v(32.26, 30.02) * mm});
            skLineSegment(sketch, "E966.MirrorCS", {"start": v(53.25, 31.8) * mm, "end": v(54.37, 32.55) * mm});
            skArc(sketch, "E967.MirrorCS", {"start": v(35.65, 41.25) * mm, "mid": v(35.49, 41.21) * mm, "end": v(35.33, 41.15) * mm});
            skArc(sketch, "E968.MirrorCS", {"start": v(39.42, 21.88) * mm, "mid": v(39.43, 22.24) * mm, "end": v(39.43, 22.61) * mm});
            skArc(sketch, "E969.MirrorCS", {"start": v(40.03, 21.97) * mm, "mid": v(39.98, 21.37) * mm, "end": v(39.9, 20.78) * mm});
            skArc(sketch, "E970.MirrorCS", {"start": v(52.2, 32.54) * mm, "mid": v(52.37, 32.42) * mm, "end": v(52.52, 32.3) * mm});
            skArc(sketch, "E971.MirrorCS", {"start": v(39.34, 21.11) * mm, "mid": v(39.4, 21.5) * mm, "end": v(39.42, 21.88) * mm});
            skArc(sketch, "E972.MirrorCS", {"start": v(53.5, 30.24) * mm, "mid": v(53.25, 30) * mm, "end": v(53, 29.77) * mm});
            skArc(sketch, "E973.MirrorCS", {"start": v(34.6, 40.01) * mm, "mid": v(34.57, 39.83) * mm, "end": v(34.55, 39.65) * mm});
            skArc(sketch, "E974.MirrorCS", {"start": v(38.52, 19.55) * mm, "mid": v(38.72, 19.75) * mm, "end": v(38.9, 19.97) * mm});
            skArc(sketch, "E975.MirrorCS", {"start": v(37.91, 19.2) * mm, "mid": v(38.01, 19.22) * mm, "end": v(38.11, 19.25) * mm});
            skArc(sketch, "E976.MirrorCS", {"start": v(54.77, 31.22) * mm, "mid": v(54.75, 31.18) * mm, "end": v(54.75, 31.13) * mm});
            skArc(sketch, "E977.MirrorCS", {"start": v(34.55, 39.65) * mm, "mid": v(34.53, 39.35) * mm, "end": v(34.52, 39.05) * mm});
            skArc(sketch, "E978.MirrorCS", {"start": v(38.9, 19.97) * mm, "mid": v(39.04, 20.22) * mm, "end": v(39.16, 20.49) * mm});
            skArc(sketch, "E979.MirrorCS", {"start": v(44.35, 20.54) * mm, "mid": v(44.06, 20.61) * mm, "end": v(43.8, 20.74) * mm});
            skArc(sketch, "E980.MirrorCS", {"start": v(38.11, 19.25) * mm, "mid": v(38.2, 19.3) * mm, "end": v(38.3, 19.35) * mm});
            skArc(sketch, "E981.MirrorCS", {"start": v(53.02, 24.31) * mm, "mid": v(52.93, 23.82) * mm, "end": v(52.75, 23.34) * mm});
            skArc(sketch, "E982.MirrorCS", {"start": v(36.91, 19.39) * mm, "mid": v(37, 19.32) * mm, "end": v(37.1, 19.26) * mm});
            skArc(sketch, "E983.MirrorCS", {"start": v(54.75, 31.13) * mm, "mid": v(54.78, 31.08) * mm, "end": v(54.82, 31.04) * mm});
            skArc(sketch, "E984.MirrorCS", {"start": v(39.9, 20.78) * mm, "mid": v(39.78, 20.33) * mm, "end": v(39.6, 19.9) * mm});
            skArc(sketch, "E985.MirrorCS", {"start": v(34.52, 39.05) * mm, "mid": v(34.52, 38.37) * mm, "end": v(34.58, 37.69) * mm});
            skArc(sketch, "E986.MirrorCS", {"start": v(33.8, 39.75) * mm, "mid": v(34.08, 40.57) * mm, "end": v(34.57, 41.28) * mm});
            skArc(sketch, "E987.MirrorCS", {"start": v(38.3, 19.35) * mm, "mid": v(38.4, 19.45) * mm, "end": v(38.52, 19.55) * mm});
            skArc(sketch, "E988.MirrorCS", {"start": v(35.15, 21.4) * mm, "mid": v(35.1, 21.86) * mm, "end": v(35.07, 22.33) * mm});
            skArc(sketch, "E989.MirrorCS", {"start": v(52.07, 37.34) * mm, "mid": v(51.98, 36.52) * mm, "end": v(51.77, 35.73) * mm});
            skArc(sketch, "E990.MirrorCS", {"start": v(51.89, 38.79) * mm, "mid": v(52.04, 38.07) * mm, "end": v(52.07, 37.34) * mm});
            skArc(sketch, "E991.MirrorCS", {"start": v(37.1, 19.26) * mm, "mid": v(37.2, 19.23) * mm, "end": v(37.3, 19.2) * mm});
            skArc(sketch, "E992.MirrorCS", {"start": v(54.82, 31.04) * mm, "mid": v(55, 30.93) * mm, "end": v(55.2, 30.85) * mm});
            skArc(sketch, "E993.MirrorCS", {"start": v(39.6, 19.9) * mm, "mid": v(39.38, 19.54) * mm, "end": v(39.11, 19.24) * mm});
            skArc(sketch, "E994.MirrorCS", {"start": v(34.58, 37.69) * mm, "mid": v(34.68, 37.07) * mm, "end": v(34.85, 36.46) * mm});
            skArc(sketch, "E995.MirrorCS", {"start": v(55.29, 31.59) * mm, "mid": v(55.1, 31.46) * mm, "end": v(54.9, 31.34) * mm});
            skArc(sketch, "E996.MirrorCS", {"start": v(36.09, 22.7) * mm, "mid": v(36, 22.28) * mm, "end": v(35.94, 21.84) * mm});
            skArc(sketch, "E997.MirrorCS", {"start": v(35.89, 33.8) * mm, "mid": v(35.13, 34.7) * mm, "end": v(34.5, 35.7) * mm});
            skArc(sketch, "E998.MirrorCS", {"start": v(35.07, 22.33) * mm, "mid": v(35.08, 22.79) * mm, "end": v(35.12, 23.25) * mm});
            skArc(sketch, "E999.MirrorCS", {"start": v(55.1, 30.4) * mm, "mid": v(54.8, 30.52) * mm, "end": v(54.5, 30.64) * mm});
            skArc(sketch, "E1000.MirrorCS", {"start": v(37.61, 19.2) * mm, "mid": v(37.76, 19.2) * mm, "end": v(37.91, 19.2) * mm});
            skArc(sketch, "E1001.MirrorCS", {"start": v(36.26, 20.14) * mm, "mid": v(36.43, 19.9) * mm, "end": v(36.62, 19.68) * mm});
            skArc(sketch, "E1002.MirrorCS", {"start": v(35.93, 21.15) * mm, "mid": v(35.97, 20.87) * mm, "end": v(36.03, 20.6) * mm});
            skArc(sketch, "E1003.MirrorCS", {"start": v(54.9, 31.34) * mm, "mid": v(54.83, 31.28) * mm, "end": v(54.77, 31.22) * mm});
            skArc(sketch, "E1004.MirrorCS", {"start": v(35.94, 21.84) * mm, "mid": v(35.93, 21.5) * mm, "end": v(35.93, 21.15) * mm});
            skArc(sketch, "E1005.MirrorCS", {"start": v(33.78, 37.8) * mm, "mid": v(33.7, 38.77) * mm, "end": v(33.8, 39.75) * mm});
            skArc(sketch, "E1006.MirrorCS", {"start": v(35.35, 20.55) * mm, "mid": v(35.23, 20.97) * mm, "end": v(35.15, 21.4) * mm});
            skArc(sketch, "E1007.MirrorCS", {"start": v(37.3, 19.2) * mm, "mid": v(37.45, 19.2) * mm, "end": v(37.61, 19.2) * mm});
            skArc(sketch, "E1008.MirrorCS", {"start": v(55.2, 30.85) * mm, "mid": v(55.72, 30.68) * mm, "end": v(56.24, 30.52) * mm});
            skArc(sketch, "E1009.MirrorCS", {"start": v(36.62, 19.68) * mm, "mid": v(36.76, 19.53) * mm, "end": v(36.91, 19.39) * mm});
            skArc(sketch, "E1010.MirrorCS", {"start": v(36.03, 20.6) * mm, "mid": v(36.13, 20.36) * mm, "end": v(36.26, 20.14) * mm});
            skArc(sketch, "E1011.MirrorCS", {"start": v(66.4, 31.52) * mm, "mid": v(66.47, 31.6) * mm, "end": v(66.52, 31.69) * mm});
            skArc(sketch, "E1012.MirrorCS", {"start": v(55.96, 30.07) * mm, "mid": v(55.53, 30.23) * mm, "end": v(55.1, 30.4) * mm});
            skArc(sketch, "E1013.MirrorCS", {"start": v(56.92, 29.78) * mm, "mid": v(56.44, 29.92) * mm, "end": v(55.96, 30.07) * mm});
            skArc(sketch, "E1014.MirrorCS", {"start": v(57.97, 29.53) * mm, "mid": v(57.44, 29.65) * mm, "end": v(56.92, 29.78) * mm});
            skArc(sketch, "E1015.MirrorCS", {"start": v(56.24, 30.52) * mm, "mid": v(56.79, 30.36) * mm, "end": v(57.34, 30.21) * mm});
            skArc(sketch, "E1016.MirrorCS", {"start": v(36.6, 18.7) * mm, "mid": v(36.2, 19) * mm, "end": v(35.9, 19.39) * mm});
            skArc(sketch, "E1017.MirrorCS", {"start": v(37.45, 18.49) * mm, "mid": v(37.01, 18.53) * mm, "end": v(36.6, 18.7) * mm});
            skArc(sketch, "E1018.MirrorCS", {"start": v(38.41, 18.75) * mm, "mid": v(37.94, 18.57) * mm, "end": v(37.45, 18.49) * mm});
            skArc(sketch, "E1019.MirrorCS", {"start": v(39.11, 19.24) * mm, "mid": v(38.78, 18.97) * mm, "end": v(38.41, 18.75) * mm});
            skArc(sketch, "E1020.MirrorCS", {"start": v(54.37, 32.55) * mm, "mid": v(55.03, 32.97) * mm, "end": v(55.72, 33.33) * mm});
            skArc(sketch, "E1021.MirrorCS", {"start": v(66.52, 32.54) * mm, "mid": v(66.44, 32.72) * mm, "end": v(66.33, 32.89) * mm});
            skArc(sketch, "E1022.MirrorCS", {"start": v(56.5, 32.24) * mm, "mid": v(55.88, 31.94) * mm, "end": v(55.29, 31.59) * mm});
            skArc(sketch, "E1023.MirrorCS", {"start": v(66.52, 31.69) * mm, "mid": v(66.55, 31.77) * mm, "end": v(66.57, 31.87) * mm});
            skArc(sketch, "E1024.MirrorCS", {"start": v(57.34, 30.21) * mm, "mid": v(57.77, 30.1) * mm, "end": v(58.2, 30.02) * mm});
            skArc(sketch, "E1025.MirrorCS", {"start": v(35.9, 19.39) * mm, "mid": v(35.6, 19.96) * mm, "end": v(35.35, 20.55) * mm});
            skArc(sketch, "E1026.MirrorCS", {"start": v(59.07, 29.33) * mm, "mid": v(58.52, 29.42) * mm, "end": v(57.97, 29.53) * mm});
            skArc(sketch, "E1027.MirrorCS", {"start": v(66.33, 32.89) * mm, "mid": v(66.19, 33.04) * mm, "end": v(66.01, 33.17) * mm});
            skArc(sketch, "E1028.MirrorCS", {"start": v(66.57, 31.87) * mm, "mid": v(66.58, 32) * mm, "end": v(66.58, 32.13) * mm});
            skArc(sketch, "E1029.MirrorCS", {"start": v(58.03, 32.86) * mm, "mid": v(57.26, 32.57) * mm, "end": v(56.5, 32.24) * mm});
            skArc(sketch, "E1030.MirrorCS", {"start": v(34.5, 35.7) * mm, "mid": v(34.06, 36.72) * mm, "end": v(33.78, 37.8) * mm});
            skArc(sketch, "E1031.MirrorCS", {"start": v(66.98, 33.52) * mm, "mid": v(67.19, 33.26) * mm, "end": v(67.36, 32.98) * mm});
            skArc(sketch, "E1032.MirrorCS", {"start": v(66.19, 31.3) * mm, "mid": v(66.3, 31.4) * mm, "end": v(66.4, 31.52) * mm});
            skArc(sketch, "E1033.MirrorCS", {"start": v(64.91, 30.53) * mm, "mid": v(65.6, 30.84) * mm, "end": v(66.19, 31.3) * mm});
            skArc(sketch, "E1034.MirrorCS", {"start": v(58.2, 30.02) * mm, "mid": v(59.34, 29.88) * mm, "end": v(60.47, 29.84) * mm});
            skArc(sketch, "E1035.MirrorCS", {"start": v(64.66, 33.67) * mm, "mid": v(64.15, 33.75) * mm, "end": v(63.62, 33.8) * mm});
            skArc(sketch, "E1036.MirrorCS", {"start": v(65.54, 33.41) * mm, "mid": v(65.1, 33.56) * mm, "end": v(64.66, 33.67) * mm});
            skArc(sketch, "E1037.MirrorCS", {"start": v(66.01, 33.17) * mm, "mid": v(65.78, 33.3) * mm, "end": v(65.54, 33.41) * mm});
            skArc(sketch, "E1038.MirrorCS", {"start": v(55.72, 33.33) * mm, "mid": v(56.45, 33.67) * mm, "end": v(57.2, 33.95) * mm});
            skArc(sketch, "E1039.MirrorCS", {"start": v(66.12, 30.26) * mm, "mid": v(65.05, 29.85) * mm, "end": v(63.95, 29.55) * mm});
            skArc(sketch, "E1040.MirrorCS", {"start": v(67.33, 31.23) * mm, "mid": v(66.8, 30.66) * mm, "end": v(66.12, 30.26) * mm});
            skArc(sketch, "E1041.MirrorCS", {"start": v(67.48, 31.57) * mm, "mid": v(67.43, 31.4) * mm, "end": v(67.33, 31.23) * mm});
            skArc(sketch, "E1042.MirrorCS", {"start": v(67.54, 32.06) * mm, "mid": v(67.52, 31.82) * mm, "end": v(67.48, 31.57) * mm});
            skArc(sketch, "E1043.MirrorCS", {"start": v(66.58, 32.13) * mm, "mid": v(66.57, 32.34) * mm, "end": v(66.52, 32.54) * mm});
            skArc(sketch, "E1044.MirrorCS", {"start": v(67.5, 32.57) * mm, "mid": v(67.53, 32.32) * mm, "end": v(67.54, 32.06) * mm});
            skArc(sketch, "E1045.MirrorCS", {"start": v(67.36, 32.98) * mm, "mid": v(67.45, 32.78) * mm, "end": v(67.5, 32.57) * mm});
            skArc(sketch, "E1046.MirrorCS", {"start": v(59.65, 33.35) * mm, "mid": v(58.83, 33.12) * mm, "end": v(58.03, 32.86) * mm});
            skArc(sketch, "E1047.MirrorCS", {"start": v(66.46, 33.95) * mm, "mid": v(66.73, 33.75) * mm, "end": v(66.98, 33.52) * mm});
            skArc(sketch, "E1048.MirrorCS", {"start": v(65.75, 34.3) * mm, "mid": v(66.11, 34.14) * mm, "end": v(66.46, 33.95) * mm});
            skArc(sketch, "E1049.MirrorCS", {"start": v(64.78, 34.6) * mm, "mid": v(65.27, 34.45) * mm, "end": v(65.75, 34.3) * mm});
            skArc(sketch, "E1050.MirrorCS", {"start": v(62.84, 30.03) * mm, "mid": v(63.89, 30.24) * mm, "end": v(64.91, 30.53) * mm});
            skArc(sketch, "E1051.MirrorCS", {"start": v(60.47, 29.84) * mm, "mid": v(61.66, 29.89) * mm, "end": v(62.84, 30.03) * mm});
            skArc(sketch, "E1052.MirrorCS", {"start": v(63.77, 34.8) * mm, "mid": v(64.28, 34.7) * mm, "end": v(64.78, 34.6) * mm});
            skArc(sketch, "E1053.MirrorCS", {"start": v(62.79, 34.9) * mm, "mid": v(63.28, 34.86) * mm, "end": v(63.77, 34.8) * mm});
            skArc(sketch, "E1054.MirrorCS", {"start": v(61.78, 34.9) * mm, "mid": v(62.29, 34.9) * mm, "end": v(62.79, 34.9) * mm});
            skArc(sketch, "E1055.MirrorCS", {"start": v(63.62, 33.8) * mm, "mid": v(63.03, 33.81) * mm, "end": v(62.44, 33.8) * mm});
            skArc(sketch, "E1056.MirrorCS", {"start": v(61.44, 29.2) * mm, "mid": v(60.25, 29.2) * mm, "end": v(59.07, 29.33) * mm});
            skArc(sketch, "E1057.MirrorCS", {"start": v(61.16, 33.66) * mm, "mid": v(60.4, 33.53) * mm, "end": v(59.65, 33.35) * mm});
            skArc(sketch, "E1058.MirrorCS", {"start": v(62.44, 33.8) * mm, "mid": v(61.8, 33.74) * mm, "end": v(61.16, 33.66) * mm});
            skArc(sketch, "E1059.MirrorCS", {"start": v(60.73, 34.79) * mm, "mid": v(61.26, 34.85) * mm, "end": v(61.78, 34.9) * mm});
            skArc(sketch, "E1060.MirrorCS", {"start": v(58.85, 34.43) * mm, "mid": v(59.79, 34.63) * mm, "end": v(60.73, 34.79) * mm});
            skArc(sketch, "E1061.MirrorCS", {"start": v(57.2, 33.95) * mm, "mid": v(58.01, 34.22) * mm, "end": v(58.85, 34.43) * mm});
            skArc(sketch, "E1062.MirrorCS", {"start": v(63.95, 29.55) * mm, "mid": v(62.7, 29.31) * mm, "end": v(61.44, 29.2) * mm});
            skSolve(sketch);
        }
        {
            var Q0;
            Q0 = qSketchRegion(id + "F4", true);
            extrude(context, id + "F5", {"entities" : qUnion([Q0]), "operationType" : NewBodyOperationType.ADD, "depth" : 1.59 * mm, "offsetDistance" : 25.4 * mm});
        }
        {
            var Q0;
            Q0=makeQuery(id+"F5.boolean.opBoolean","SPLIT",FACE,{"disambiguationData":[TD([makeQuery(id+"F3.opExtrude","SWEPT_FACE",FACE,{"disambiguationData":[OSD([sQuery(id+"F2.wireOp",EDGE,"E5.bottom")])]})])],"derivedFrom":makeQuery(id+"F1.opExtrude","CAP_FACE",FACE,{"disambiguationData":[OSD([sQuery(id+"F0.wireOp",EDGE,"E0.bottom"),sQuery(id+"F0.wireOp",EDGE,"E0.top"),sQuery(id+"F0.wireOp",EDGE,"E0.left"),sQuery(id+"F0.wireOp",EDGE,"E0.right"),sQuery(id+"F0.wireOp",EDGE,"E1.filletArc"),sQuery(id+"F0.wireOp",EDGE,"E2.filletArc"),sQuery(id+"F0.wireOp",EDGE,"E3.filletArc"),sQuery(id+"F0.wireOp",EDGE,"E4.filletArc")])],"isStart":false})});
            var sketch = newSketch(context, id + "F6", { "sketchPlane" : qUnion([Q0])});
            skText(sketch, "E1063", { "text": "Rohr\'s", "fontName": "RobotoSlab-Regular.ttf"});
            const initialGuessF6  = {"E1063": [-0.03171, 0.02311, 1, 0, 0.01499]};
            skSetInitialGuess(sketch, initialGuessF6);
            skSolve(sketch);
        }
        {
            var Q0;
            Q0 = qSketchRegion(id + "F6", true);
            extrude(context, id + "F7", {"entities" : qUnion([Q0]), "operationType" : NewBodyOperationType.ADD, "depth" : 1.59 * mm, "offsetDistance" : 25.4 * mm});
        }
        {
            var Q0;
            {var subQ295=makeQuery(id+"F3.opExtrude","SWEPT_FACE",FACE,{"disambiguationData":[OSD([sQuery(id+"F2.wireOp",EDGE,"E5.bottom")])]});Q0=makeQuery(id+"F7.boolean.opBoolean","SPLIT",FACE,{"disambiguationData":[TD([subQ295])],"derivedFrom":makeQuery(id+"F5.boolean.opBoolean","SPLIT",FACE,{"disambiguationData":[TD([subQ295])],"derivedFrom":makeQuery(id+"F1.opExtrude","CAP_FACE",FACE,{"disambiguationData":[OSD([sQuery(id+"F0.wireOp",EDGE,"E0.bottom"),sQuery(id+"F0.wireOp",EDGE,"E0.top"),sQuery(id+"F0.wireOp",EDGE,"E0.left"),sQuery(id+"F0.wireOp",EDGE,"E0.right"),sQuery(id+"F0.wireOp",EDGE,"E1.filletArc"),sQuery(id+"F0.wireOp",EDGE,"E2.filletArc"),sQuery(id+"F0.wireOp",EDGE,"E3.filletArc"),sQuery(id+"F0.wireOp",EDGE,"E4.filletArc")])],"isStart":false})})});}
            var sketch = newSketch(context, id + "F8", { "sketchPlane" : qUnion([Q0])});
            skArc(sketch, "E1064", {"start": v(-0.5, 18.82) * mm, "mid": v(-0.63, 18.64) * mm, "end": v(-0.77, 18.47) * mm});
            skArc(sketch, "E1065", {"start": v(-0.77, 18.47) * mm, "mid": v(-0.94, 18.26) * mm, "end": v(-1.11, 18.06) * mm});
            skArc(sketch, "E1066", {"start": v(-1.11, 18.06) * mm, "mid": v(-1.28, 17.86) * mm, "end": v(-1.45, 17.66) * mm});
            skArc(sketch, "E1067", {"start": v(-1.45, 17.66) * mm, "mid": v(-1.6, 17.5) * mm, "end": v(-1.75, 17.35) * mm});
            skLineSegment(sketch, "E1068", {"start": v(-1.75, 17.35) * mm, "end": v(-2.4, 16.67) * mm});
            skLineSegment(sketch, "E1069", {"start": v(-2.4, 16.67) * mm, "end": v(-3.66, 17.3) * mm});
            skArc(sketch, "E1070", {"start": v(-3.66, 17.3) * mm, "mid": v(-4.41, 17.66) * mm, "end": v(-5.17, 18) * mm});
            skArc(sketch, "E1071", {"start": v(-5.17, 18) * mm, "mid": v(-5.79, 18.23) * mm, "end": v(-6.41, 18.44) * mm});
            skArc(sketch, "E1072", {"start": v(-6.41, 18.44) * mm, "mid": v(-7, 18.59) * mm, "end": v(-7.58, 18.7) * mm});
            skArc(sketch, "E1073", {"start": v(-7.58, 18.7) * mm, "mid": v(-8.22, 18.78) * mm, "end": v(-8.85, 18.83) * mm});
            skArc(sketch, "E1074", {"start": v(-8.85, 18.83) * mm, "mid": v(-9.28, 18.84) * mm, "end": v(-9.72, 18.83) * mm});
            skArc(sketch, "E1075", {"start": v(-9.72, 18.83) * mm, "mid": v(-10.1, 18.8) * mm, "end": v(-10.48, 18.75) * mm});
            skArc(sketch, "E1076", {"start": v(-10.48, 18.75) * mm, "mid": v(-10.82, 18.68) * mm, "end": v(-11.16, 18.58) * mm});
            skArc(sketch, "E1077", {"start": v(-11.16, 18.58) * mm, "mid": v(-11.5, 18.46) * mm, "end": v(-11.81, 18.32) * mm});
            skArc(sketch, "E1078", {"start": v(-11.81, 18.32) * mm, "mid": v(-12.2, 18.1) * mm, "end": v(-12.58, 17.83) * mm});
            skArc(sketch, "E1079", {"start": v(-12.58, 17.83) * mm, "mid": v(-12.9, 17.54) * mm, "end": v(-13.2, 17.2) * mm});
            skArc(sketch, "E1080", {"start": v(-13.2, 17.2) * mm, "mid": v(-13.43, 16.87) * mm, "end": v(-13.61, 16.51) * mm});
            skArc(sketch, "E1081", {"start": v(-13.61, 16.51) * mm, "mid": v(-13.73, 16.17) * mm, "end": v(-13.77, 15.82) * mm});
            skArc(sketch, "E1082", {"start": v(-13.77, 15.82) * mm, "mid": v(-13.78, 15.7) * mm, "end": v(-13.8, 15.59) * mm});
            skArc(sketch, "E1083", {"start": v(-13.8, 15.59) * mm, "mid": v(-13.8, 15.52) * mm, "end": v(-13.84, 15.45) * mm});
            skArc(sketch, "E1084", {"start": v(-13.84, 15.45) * mm, "mid": v(-13.87, 15.4) * mm, "end": v(-13.92, 15.35) * mm});
            skArc(sketch, "E1085", {"start": v(-13.92, 15.35) * mm, "mid": v(-14, 15.3) * mm, "end": v(-14.07, 15.25) * mm});
            skArc(sketch, "E1086", {"start": v(-14.07, 15.25) * mm, "mid": v(-14.28, 15.12) * mm, "end": v(-14.48, 14.99) * mm});
            skArc(sketch, "E1087", {"start": v(-14.48, 14.99) * mm, "mid": v(-14.79, 14.76) * mm, "end": v(-15.09, 14.52) * mm});
            skArc(sketch, "E1088", {"start": v(-15.09, 14.52) * mm, "mid": v(-15.38, 14.27) * mm, "end": v(-15.67, 14.02) * mm});
            skArc(sketch, "E1089", {"start": v(-15.67, 14.02) * mm, "mid": v(-15.86, 13.85) * mm, "end": v(-16.03, 13.66) * mm});
            skArc(sketch, "E1090", {"start": v(-16.03, 13.66) * mm, "mid": v(-16.38, 13.2) * mm, "end": v(-16.64, 12.69) * mm});
            skArc(sketch, "E1091", {"start": v(-16.64, 12.69) * mm, "mid": v(-16.8, 12.16) * mm, "end": v(-16.86, 11.62) * mm});
            skArc(sketch, "E1092", {"start": v(-16.86, 11.62) * mm, "mid": v(-16.82, 11.08) * mm, "end": v(-16.67, 10.56) * mm});
            skArc(sketch, "E1093", {"start": v(-16.67, 10.56) * mm, "mid": v(-16.42, 10.07) * mm, "end": v(-16.08, 9.62) * mm});
            skArc(sketch, "E1094", {"start": v(-16.08, 9.62) * mm, "mid": v(-15.81, 9.35) * mm, "end": v(-15.52, 9.1) * mm});
            skArc(sketch, "E1095", {"start": v(-15.52, 9.1) * mm, "mid": v(-15.2, 8.88) * mm, "end": v(-14.87, 8.7) * mm});
            skArc(sketch, "E1096", {"start": v(-14.87, 8.7) * mm, "mid": v(-14.52, 8.53) * mm, "end": v(-14.15, 8.4) * mm});
            skArc(sketch, "E1097", {"start": v(-14.15, 8.4) * mm, "mid": v(-13.77, 8.3) * mm, "end": v(-13.37, 8.23) * mm});
            skArc(sketch, "E1098", {"start": v(-13.37, 8.23) * mm, "mid": v(-13.25, 8.2) * mm, "end": v(-13.13, 8.18) * mm});
            skArc(sketch, "E1099", {"start": v(-13.13, 8.18) * mm, "mid": v(-13.05, 8.16) * mm, "end": v(-12.98, 8.13) * mm});
            skArc(sketch, "E1100", {"start": v(-12.98, 8.13) * mm, "mid": v(-12.93, 8.1) * mm, "end": v(-12.88, 8.04) * mm});
            skArc(sketch, "E1101", {"start": v(-12.88, 8.04) * mm, "mid": v(-12.84, 7.98) * mm, "end": v(-12.8, 7.9) * mm});
            skArc(sketch, "E1102", {"start": v(-12.8, 7.9) * mm, "mid": v(-12.73, 7.75) * mm, "end": v(-12.63, 7.62) * mm});
            skArc(sketch, "E1103", {"start": v(-12.63, 7.62) * mm, "mid": v(-12.5, 7.46) * mm, "end": v(-12.36, 7.32) * mm});
            skArc(sketch, "E1104", {"start": v(-12.36, 7.32) * mm, "mid": v(-12.18, 7.18) * mm, "end": v(-12, 7.05) * mm});
            skArc(sketch, "E1105", {"start": v(-12, 7.05) * mm, "mid": v(-11.81, 6.94) * mm, "end": v(-11.61, 6.84) * mm});
            skArc(sketch, "E1106", {"start": v(-11.61, 6.84) * mm, "mid": v(-11.47, 6.78) * mm, "end": v(-11.32, 6.73) * mm});
            skArc(sketch, "E1107", {"start": v(-11.32, 6.73) * mm, "mid": v(-11.18, 6.7) * mm, "end": v(-11.04, 6.66) * mm});
            skArc(sketch, "E1108", {"start": v(-11.04, 6.66) * mm, "mid": v(-10.87, 6.64) * mm, "end": v(-10.7, 6.64) * mm});
            skArc(sketch, "E1109", {"start": v(-10.7, 6.64) * mm, "mid": v(-10.42, 6.63) * mm, "end": v(-10.14, 6.63) * mm});
            skArc(sketch, "E1110", {"start": v(-10.14, 6.63) * mm, "mid": v(-9.52, 6.66) * mm, "end": v(-8.9, 6.73) * mm});
            skArc(sketch, "E1111", {"start": v(-8.9, 6.73) * mm, "mid": v(-8.3, 6.84) * mm, "end": v(-7.69, 7) * mm});
            skArc(sketch, "E1112", {"start": v(-7.69, 7) * mm, "mid": v(-7.05, 7.22) * mm, "end": v(-6.42, 7.47) * mm});
            skArc(sketch, "E1113", {"start": v(-6.42, 7.47) * mm, "mid": v(-5.74, 7.8) * mm, "end": v(-5.07, 8.15) * mm});
            skLineSegment(sketch, "E1114", {"start": v(-5.07, 8.15) * mm, "end": v(-4.14, 8.68) * mm});
            skLineSegment(sketch, "E1115", {"start": v(-4.14, 8.68) * mm, "end": v(-3.83, 8.46) * mm});
            skArc(sketch, "E1116", {"start": v(-3.83, 8.46) * mm, "mid": v(-3.73, 8.39) * mm, "end": v(-3.63, 8.31) * mm});
            skArc(sketch, "E1117", {"start": v(-3.63, 8.31) * mm, "mid": v(-3.39, 8.12) * mm, "end": v(-3.14, 7.92) * mm});
            skArc(sketch, "E1118", {"start": v(-3.14, 7.92) * mm, "mid": v(-2.85, 7.68) * mm, "end": v(-2.56, 7.45) * mm});
            skArc(sketch, "E1119", {"start": v(-2.56, 7.45) * mm, "mid": v(-2.24, 7.2) * mm, "end": v(-1.93, 6.93) * mm});
            skLineSegment(sketch, "E1120", {"start": v(-1.93, 6.93) * mm, "end": v(-0.33, 5.63) * mm});
            skLineSegment(sketch, "E1121", {"start": v(-0.33, 5.63) * mm, "end": v(0.23, 6.4) * mm});
            skArc(sketch, "E1122", {"start": v(0.23, 6.4) * mm, "mid": v(0.36, 6.58) * mm, "end": v(0.49, 6.75) * mm});
            skArc(sketch, "E1123", {"start": v(0.49, 6.75) * mm, "mid": v(0.64, 6.95) * mm, "end": v(0.8, 7.14) * mm});
            skArc(sketch, "E1124", {"start": v(0.8, 7.14) * mm, "mid": v(0.95, 7.33) * mm, "end": v(1.1, 7.52) * mm});
            skArc(sketch, "E1125", {"start": v(1.1, 7.52) * mm, "mid": v(1.24, 7.66) * mm, "end": v(1.37, 7.8) * mm});
            skLineSegment(sketch, "E1126", {"start": v(1.37, 7.8) * mm, "end": v(1.94, 8.43) * mm});
            skLineSegment(sketch, "E1127", {"start": v(1.94, 8.43) * mm, "end": v(2.4, 8.16) * mm});
            skArc(sketch, "E1128", {"start": v(2.4, 8.16) * mm, "mid": v(2.79, 7.94) * mm, "end": v(3.18, 7.74) * mm});
            skArc(sketch, "E1129", {"start": v(3.18, 7.74) * mm, "mid": v(3.59, 7.54) * mm, "end": v(4, 7.35) * mm});
            skArc(sketch, "E1130", {"start": v(4, 7.35) * mm, "mid": v(4.39, 7.2) * mm, "end": v(4.78, 7.04) * mm});
            skArc(sketch, "E1131", {"start": v(4.78, 7.04) * mm, "mid": v(5.1, 6.93) * mm, "end": v(5.44, 6.84) * mm});
            skArc(sketch, "E1132", {"start": v(5.44, 6.84) * mm, "mid": v(5.7, 6.78) * mm, "end": v(5.94, 6.73) * mm});
            skArc(sketch, "E1133", {"start": v(5.94, 6.73) * mm, "mid": v(6.17, 6.7) * mm, "end": v(6.4, 6.67) * mm});
            skArc(sketch, "E1134", {"start": v(6.4, 6.67) * mm, "mid": v(6.68, 6.65) * mm, "end": v(6.95, 6.63) * mm});
            skArc(sketch, "E1135", {"start": v(6.95, 6.63) * mm, "mid": v(7.33, 6.63) * mm, "end": v(7.72, 6.62) * mm});
            skArc(sketch, "E1136", {"start": v(7.72, 6.62) * mm, "mid": v(8.15, 6.63) * mm, "end": v(8.58, 6.63) * mm});
            skArc(sketch, "E1137", {"start": v(8.58, 6.63) * mm, "mid": v(8.81, 6.64) * mm, "end": v(9.04, 6.66) * mm});
            skArc(sketch, "E1138", {"start": v(9.04, 6.66) * mm, "mid": v(9.24, 6.7) * mm, "end": v(9.43, 6.74) * mm});
            skArc(sketch, "E1139", {"start": v(9.43, 6.74) * mm, "mid": v(9.66, 6.8) * mm, "end": v(9.9, 6.89) * mm});
            skArc(sketch, "E1140", {"start": v(9.9, 6.89) * mm, "mid": v(10.43, 7.1) * mm, "end": v(10.94, 7.38) * mm});
            skArc(sketch, "E1141", {"start": v(10.94, 7.38) * mm, "mid": v(11.35, 7.67) * mm, "end": v(11.7, 8.02) * mm});
            skArc(sketch, "E1142", {"start": v(11.7, 8.02) * mm, "mid": v(11.98, 8.41) * mm, "end": v(12.2, 8.84) * mm});
            skArc(sketch, "E1143", {"start": v(12.2, 8.84) * mm, "mid": v(12.34, 9.33) * mm, "end": v(12.42, 9.84) * mm});
            skLineSegment(sketch, "E1144", {"start": v(12.42, 9.84) * mm, "end": v(12.48, 10.5) * mm});
            skLineSegment(sketch, "E1145", {"start": v(12.48, 10.5) * mm, "end": v(13, 10.7) * mm});
            skArc(sketch, "E1146", {"start": v(13, 10.7) * mm, "mid": v(13.53, 10.92) * mm, "end": v(14.03, 11.2) * mm});
            skArc(sketch, "E1147", {"start": v(14.03, 11.2) * mm, "mid": v(14.43, 11.49) * mm, "end": v(14.78, 11.84) * mm});
            skArc(sketch, "E1148", {"start": v(14.78, 11.84) * mm, "mid": v(15.04, 12.2) * mm, "end": v(15.23, 12.6) * mm});
            skArc(sketch, "E1149", {"start": v(15.23, 12.6) * mm, "mid": v(15.35, 13.03) * mm, "end": v(15.39, 13.48) * mm});
            skArc(sketch, "E1150", {"start": v(15.39, 13.48) * mm, "mid": v(15.37, 13.74) * mm, "end": v(15.32, 14) * mm});
            skArc(sketch, "E1151", {"start": v(15.32, 14) * mm, "mid": v(15.24, 14.25) * mm, "end": v(15.13, 14.5) * mm});
            skArc(sketch, "E1152", {"start": v(15.13, 14.5) * mm, "mid": v(14.98, 14.74) * mm, "end": v(14.8, 14.98) * mm});
            skArc(sketch, "E1153", {"start": v(14.8, 14.98) * mm, "mid": v(14.58, 15.23) * mm, "end": v(14.34, 15.46) * mm});
            skArc(sketch, "E1154", {"start": v(14.34, 15.46) * mm, "mid": v(14.14, 15.63) * mm, "end": v(13.93, 15.78) * mm});
            skArc(sketch, "E1155", {"start": v(13.93, 15.78) * mm, "mid": v(13.65, 15.95) * mm, "end": v(13.37, 16.12) * mm});
            skArc(sketch, "E1156", {"start": v(13.37, 16.12) * mm, "mid": v(13.1, 16.27) * mm, "end": v(12.82, 16.41) * mm});
            skArc(sketch, "E1157", {"start": v(12.82, 16.41) * mm, "mid": v(12.68, 16.46) * mm, "end": v(12.54, 16.48) * mm});
            skArc(sketch, "E1158", {"start": v(12.54, 16.48) * mm, "mid": v(12.52, 16.48) * mm, "end": v(12.5, 16.5) * mm});
            skArc(sketch, "E1159", {"start": v(12.5, 16.5) * mm, "mid": v(12.48, 16.52) * mm, "end": v(12.47, 16.55) * mm});
            skArc(sketch, "E1160", {"start": v(12.47, 16.55) * mm, "mid": v(12.45, 16.6) * mm, "end": v(12.44, 16.64) * mm});
            skArc(sketch, "E1161", {"start": v(12.44, 16.64) * mm, "mid": v(12.44, 16.69) * mm, "end": v(12.44, 16.74) * mm});
            skArc(sketch, "E1162", {"start": v(12.44, 16.74) * mm, "mid": v(12.42, 16.92) * mm, "end": v(12.37, 17.1) * mm});
            skArc(sketch, "E1163", {"start": v(12.37, 17.1) * mm, "mid": v(12.28, 17.32) * mm, "end": v(12.17, 17.54) * mm});
            skArc(sketch, "E1164", {"start": v(12.17, 17.54) * mm, "mid": v(12.04, 17.77) * mm, "end": v(11.89, 17.99) * mm});
            skArc(sketch, "E1165", {"start": v(11.89, 17.99) * mm, "mid": v(11.73, 18.17) * mm, "end": v(11.56, 18.34) * mm});
            skArc(sketch, "E1166", {"start": v(11.56, 18.34) * mm, "mid": v(11.2, 18.65) * mm, "end": v(10.8, 18.92) * mm});
            skArc(sketch, "E1167", {"start": v(10.8, 18.92) * mm, "mid": v(10.42, 19.13) * mm, "end": v(10.01, 19.3) * mm});
            skArc(sketch, "E1168", {"start": v(10.01, 19.3) * mm, "mid": v(9.56, 19.42) * mm, "end": v(9.09, 19.5) * mm});
            skArc(sketch, "E1169", {"start": v(9.09, 19.5) * mm, "mid": v(8.5, 19.54) * mm, "end": v(7.91, 19.55) * mm});
            skArc(sketch, "E1170", {"start": v(7.91, 19.55) * mm, "mid": v(7.27, 19.53) * mm, "end": v(6.63, 19.46) * mm});
            skArc(sketch, "E1171", {"start": v(6.63, 19.46) * mm, "mid": v(6.07, 19.36) * mm, "end": v(5.53, 19.2) * mm});
            skArc(sketch, "E1172", {"start": v(5.53, 19.2) * mm, "mid": v(4.97, 18.98) * mm, "end": v(4.43, 18.72) * mm});
            skArc(sketch, "E1173", {"start": v(4.43, 18.72) * mm, "mid": v(3.76, 18.34) * mm, "end": v(3.11, 17.93) * mm});
            skArc(sketch, "E1174", {"start": v(3.11, 17.93) * mm, "mid": v(2.94, 17.82) * mm, "end": v(2.76, 17.7) * mm});
            skArc(sketch, "E1175", {"start": v(2.76, 17.7) * mm, "mid": v(2.6, 17.6) * mm, "end": v(2.45, 17.5) * mm});
            skArc(sketch, "E1176", {"start": v(2.45, 17.5) * mm, "mid": v(2.32, 17.43) * mm, "end": v(2.18, 17.35) * mm});
            skArc(sketch, "E1177", {"start": v(2.18, 17.35) * mm, "mid": v(2.16, 17.34) * mm, "end": v(2.13, 17.33) * mm});
            skArc(sketch, "E1178", {"start": v(2.13, 17.33) * mm, "mid": v(2.1, 17.34) * mm, "end": v(2.08, 17.35) * mm});
            skArc(sketch, "E1179", {"start": v(2.08, 17.35) * mm, "mid": v(1.95, 17.51) * mm, "end": v(1.8, 17.67) * mm});
            skArc(sketch, "E1180", {"start": v(1.8, 17.67) * mm, "mid": v(1.65, 17.85) * mm, "end": v(1.5, 18.04) * mm});
            skArc(sketch, "E1181", {"start": v(1.5, 18.04) * mm, "mid": v(1.3, 18.26) * mm, "end": v(1.13, 18.48) * mm});
            skArc(sketch, "E1182", {"start": v(1.13, 18.48) * mm, "mid": v(0.95, 18.7) * mm, "end": v(0.77, 18.91) * mm});
            skArc(sketch, "E1183", {"start": v(0.77, 18.91) * mm, "mid": v(0.61, 19.1) * mm, "end": v(0.46, 19.28) * mm});
            skArc(sketch, "E1184", {"start": v(0.46, 19.28) * mm, "mid": v(0.32, 19.44) * mm, "end": v(0.18, 19.6) * mm});
            skArc(sketch, "E1185", {"start": v(0.18, 19.6) * mm, "mid": v(0.17, 19.62) * mm, "end": v(0.15, 19.62) * mm});
            skArc(sketch, "E1186", {"start": v(0.15, 19.62) * mm, "mid": v(0.13, 19.62) * mm, "end": v(0.11, 19.6) * mm});
            skArc(sketch, "E1187", {"start": v(0.11, 19.6) * mm, "mid": v(0.02, 19.5) * mm, "end": v(-0.06, 19.38) * mm});
            skArc(sketch, "E1188", {"start": v(-0.06, 19.38) * mm, "mid": v(-0.17, 19.26) * mm, "end": v(-0.27, 19.13) * mm});
            skArc(sketch, "E1189", {"start": v(-0.27, 19.13) * mm, "mid": v(-0.38, 18.97) * mm, "end": v(-0.5, 18.82) * mm});
            skArc(sketch, "E1190", {"start": v(9.27, 18.52) * mm, "mid": v(9.5, 18.46) * mm, "end": v(9.73, 18.4) * mm});
            skArc(sketch, "E1191", {"start": v(9.73, 18.4) * mm, "mid": v(9.96, 18.3) * mm, "end": v(10.18, 18.22) * mm});
            skArc(sketch, "E1192", {"start": v(10.18, 18.22) * mm, "mid": v(10.38, 18.12) * mm, "end": v(10.58, 18.01) * mm});
            skArc(sketch, "E1193", {"start": v(10.58, 18.01) * mm, "mid": v(10.75, 17.9) * mm, "end": v(10.91, 17.79) * mm});
            skArc(sketch, "E1194", {"start": v(10.91, 17.79) * mm, "mid": v(11, 17.7) * mm, "end": v(11.1, 17.61) * mm});
            skArc(sketch, "E1195", {"start": v(11.1, 17.61) * mm, "mid": v(11.21, 17.46) * mm, "end": v(11.33, 17.3) * mm});
            skArc(sketch, "E1196", {"start": v(11.33, 17.3) * mm, "mid": v(11.43, 17.15) * mm, "end": v(11.54, 17) * mm});
            skArc(sketch, "E1197", {"start": v(11.54, 17) * mm, "mid": v(11.57, 16.92) * mm, "end": v(11.58, 16.85) * mm});
            skArc(sketch, "E1198", {"start": v(11.58, 16.85) * mm, "mid": v(11.57, 16.83) * mm, "end": v(11.56, 16.83) * mm});
            skArc(sketch, "E1199", {"start": v(11.56, 16.83) * mm, "mid": v(11.42, 16.82) * mm, "end": v(11.29, 16.82) * mm});
            skArc(sketch, "E1200", {"start": v(11.29, 16.82) * mm, "mid": v(11.13, 16.82) * mm, "end": v(10.97, 16.82) * mm});
            skArc(sketch, "E1201", {"start": v(10.97, 16.82) * mm, "mid": v(10.78, 16.83) * mm, "end": v(10.59, 16.84) * mm});
            skArc(sketch, "E1202", {"start": v(10.59, 16.84) * mm, "mid": v(10.34, 16.85) * mm, "end": v(10.08, 16.85) * mm});
            skArc(sketch, "E1203", {"start": v(10.08, 16.85) * mm, "mid": v(9.87, 16.85) * mm, "end": v(9.66, 16.83) * mm});
            skArc(sketch, "E1204", {"start": v(9.66, 16.83) * mm, "mid": v(9.46, 16.82) * mm, "end": v(9.26, 16.8) * mm});
            skArc(sketch, "E1205", {"start": v(9.26, 16.8) * mm, "mid": v(9.06, 16.76) * mm, "end": v(8.86, 16.72) * mm});
            skArc(sketch, "E1206", {"start": v(8.86, 16.72) * mm, "mid": v(8.52, 16.63) * mm, "end": v(8.2, 16.53) * mm});
            skArc(sketch, "E1207", {"start": v(8.2, 16.53) * mm, "mid": v(7.74, 16.38) * mm, "end": v(7.29, 16.21) * mm});
            skArc(sketch, "E1208", {"start": v(7.29, 16.21) * mm, "mid": v(6.82, 16.03) * mm, "end": v(6.36, 15.84) * mm});
            skArc(sketch, "E1209", {"start": v(6.36, 15.84) * mm, "mid": v(5.98, 15.67) * mm, "end": v(5.61, 15.5) * mm});
            skLineSegment(sketch, "E1210", {"start": v(5.61, 15.5) * mm, "end": v(5.13, 15.25) * mm});
            skLineSegment(sketch, "E1211", {"start": v(5.13, 15.25) * mm, "end": v(4.57, 15.53) * mm});
            skArc(sketch, "E1212", {"start": v(4.57, 15.53) * mm, "mid": v(4.32, 15.67) * mm, "end": v(4.07, 15.8) * mm});
            skArc(sketch, "E1213", {"start": v(4.07, 15.8) * mm, "mid": v(3.77, 16) * mm, "end": v(3.47, 16.18) * mm});
            skArc(sketch, "E1214", {"start": v(3.47, 16.18) * mm, "mid": v(3.16, 16.38) * mm, "end": v(2.86, 16.58) * mm});
            skArc(sketch, "E1215", {"start": v(2.86, 16.58) * mm, "mid": v(2.83, 16.62) * mm, "end": v(2.82, 16.67) * mm});
            skArc(sketch, "E1216", {"start": v(2.82, 16.67) * mm, "mid": v(2.83, 16.72) * mm, "end": v(2.87, 16.75) * mm});
            skArc(sketch, "E1217", {"start": v(2.87, 16.75) * mm, "mid": v(3.3, 17) * mm, "end": v(3.73, 17.25) * mm});
            skArc(sketch, "E1218", {"start": v(3.73, 17.25) * mm, "mid": v(4.14, 17.49) * mm, "end": v(4.55, 17.72) * mm});
            skArc(sketch, "E1219", {"start": v(4.55, 17.72) * mm, "mid": v(4.88, 17.89) * mm, "end": v(5.2, 18.05) * mm});
            skArc(sketch, "E1220", {"start": v(5.2, 18.05) * mm, "mid": v(5.69, 18.25) * mm, "end": v(6.19, 18.41) * mm});
            skArc(sketch, "E1221", {"start": v(6.19, 18.41) * mm, "mid": v(6.7, 18.54) * mm, "end": v(7.24, 18.62) * mm});
            skArc(sketch, "E1222", {"start": v(7.24, 18.62) * mm, "mid": v(7.76, 18.66) * mm, "end": v(8.29, 18.66) * mm});
            skArc(sketch, "E1223", {"start": v(8.29, 18.66) * mm, "mid": v(8.78, 18.61) * mm, "end": v(9.27, 18.52) * mm});
            skArc(sketch, "E1224", {"start": v(0.91, 16.42) * mm, "mid": v(0.9, 16.41) * mm, "end": v(0.9, 16.4) * mm});
            skArc(sketch, "E1225", {"start": v(0.9, 16.4) * mm, "mid": v(0.82, 16.34) * mm, "end": v(0.74, 16.27) * mm});
            skArc(sketch, "E1226", {"start": v(0.74, 16.27) * mm, "mid": v(0.65, 16.2) * mm, "end": v(0.56, 16.13) * mm});
            skArc(sketch, "E1227", {"start": v(0.56, 16.13) * mm, "mid": v(0.45, 16.04) * mm, "end": v(0.34, 15.96) * mm});
            skLineSegment(sketch, "E1228", {"start": v(0.34, 15.96) * mm, "end": v(-0.22, 15.52) * mm});
            skLineSegment(sketch, "E1229", {"start": v(-0.22, 15.52) * mm, "end": v(-0.99, 15.93) * mm});
            skLineSegment(sketch, "E1230", {"start": v(-0.99, 15.93) * mm, "end": v(-1.75, 16.33) * mm});
            skLineSegment(sketch, "E1231", {"start": v(-1.75, 16.33) * mm, "end": v(-1.06, 16.96) * mm});
            skLineSegment(sketch, "E1232", {"start": v(-1.06, 16.96) * mm, "end": v(-0.37, 17.6) * mm});
            skLineSegment(sketch, "E1233", {"start": v(-0.37, 17.6) * mm, "end": v(0.27, 17.03) * mm});
            skArc(sketch, "E1234", {"start": v(0.27, 17.03) * mm, "mid": v(0.4, 16.92) * mm, "end": v(0.51, 16.8) * mm});
            skArc(sketch, "E1235", {"start": v(0.51, 16.8) * mm, "mid": v(0.62, 16.71) * mm, "end": v(0.72, 16.61) * mm});
            skArc(sketch, "E1236", {"start": v(0.72, 16.61) * mm, "mid": v(0.81, 16.53) * mm, "end": v(0.9, 16.45) * mm});
            skArc(sketch, "E1237", {"start": v(0.9, 16.45) * mm, "mid": v(0.9, 16.44) * mm, "end": v(0.91, 16.42) * mm});
            skArc(sketch, "E1238", {"start": v(-8.58, 17.38) * mm, "mid": v(-8.42, 17.35) * mm, "end": v(-8.26, 17.3) * mm});
            skArc(sketch, "E1239", {"start": v(-8.26, 17.3) * mm, "mid": v(-8.05, 17.25) * mm, "end": v(-7.84, 17.2) * mm});
            skArc(sketch, "E1240", {"start": v(-7.84, 17.2) * mm, "mid": v(-7.61, 17.13) * mm, "end": v(-7.4, 17.07) * mm});
            skArc(sketch, "E1241", {"start": v(-7.4, 17.07) * mm, "mid": v(-7.2, 17.01) * mm, "end": v(-7, 16.95) * mm});
            skArc(sketch, "E1242", {"start": v(-7, 16.95) * mm, "mid": v(-6.55, 16.8) * mm, "end": v(-6.1, 16.63) * mm});
            skArc(sketch, "E1243", {"start": v(-6.1, 16.63) * mm, "mid": v(-5.54, 16.42) * mm, "end": v(-4.98, 16.2) * mm});
            skArc(sketch, "E1244", {"start": v(-4.98, 16.2) * mm, "mid": v(-4.4, 15.96) * mm, "end": v(-3.81, 15.72) * mm});
            skArc(sketch, "E1245", {"start": v(-3.81, 15.72) * mm, "mid": v(-3.77, 15.68) * mm, "end": v(-3.76, 15.63) * mm});
            skArc(sketch, "E1246", {"start": v(-3.76, 15.63) * mm, "mid": v(-3.76, 15.61) * mm, "end": v(-3.78, 15.6) * mm});
            skArc(sketch, "E1247", {"start": v(-3.78, 15.6) * mm, "mid": v(-3.87, 15.53) * mm, "end": v(-3.97, 15.46) * mm});
            skArc(sketch, "E1248", {"start": v(-3.98, 15.46) * mm, "mid": v(-4.1, 15.38) * mm, "end": v(-4.22, 15.3) * mm});
            skArc(sketch, "E1249", {"start": v(-4.22, 15.3) * mm, "mid": v(-4.36, 15.2) * mm, "end": v(-4.5, 15.12) * mm});
            skLineSegment(sketch, "E1250", {"start": v(-4.5, 15.12) * mm, "end": v(-5.24, 14.68) * mm});
            skLineSegment(sketch, "E1251", {"start": v(-5.24, 14.68) * mm, "end": v(-5.9, 14.92) * mm});
            skArc(sketch, "E1252", {"start": v(-5.9, 14.92) * mm, "mid": v(-6.58, 15.14) * mm, "end": v(-7.26, 15.33) * mm});
            skArc(sketch, "E1253", {"start": v(-7.26, 15.33) * mm, "mid": v(-8, 15.49) * mm, "end": v(-8.74, 15.62) * mm});
            skArc(sketch, "E1254", {"start": v(-8.74, 15.62) * mm, "mid": v(-9.5, 15.71) * mm, "end": v(-10.25, 15.77) * mm});
            skArc(sketch, "E1255", {"start": v(-10.25, 15.77) * mm, "mid": v(-10.98, 15.8) * mm, "end": v(-11.72, 15.79) * mm});
            skLineSegment(sketch, "E1256", {"start": v(-11.72, 15.79) * mm, "end": v(-12.9, 15.73) * mm});
            skLineSegment(sketch, "E1257", {"start": v(-12.9, 15.73) * mm, "end": v(-12.75, 16.08) * mm});
            skArc(sketch, "E1258", {"start": v(-12.75, 16.08) * mm, "mid": v(-12.72, 16.15) * mm, "end": v(-12.68, 16.22) * mm});
            skArc(sketch, "E1259", {"start": v(-12.68, 16.22) * mm, "mid": v(-12.64, 16.3) * mm, "end": v(-12.6, 16.37) * mm});
            skArc(sketch, "E1260", {"start": v(-12.6, 16.37) * mm, "mid": v(-12.56, 16.44) * mm, "end": v(-12.52, 16.5) * mm});
            skArc(sketch, "E1261", {"start": v(-12.52, 16.5) * mm, "mid": v(-12.48, 16.56) * mm, "end": v(-12.44, 16.6) * mm});
            skArc(sketch, "E1262", {"start": v(-12.44, 16.6) * mm, "mid": v(-12.34, 16.7) * mm, "end": v(-12.23, 16.79) * mm});
            skArc(sketch, "E1263", {"start": v(-12.23, 16.79) * mm, "mid": v(-12.05, 16.9) * mm, "end": v(-11.87, 17.02) * mm});
            skArc(sketch, "E1264", {"start": v(-11.87, 17.02) * mm, "mid": v(-11.67, 17.13) * mm, "end": v(-11.47, 17.24) * mm});
            skArc(sketch, "E1265", {"start": v(-11.47, 17.24) * mm, "mid": v(-11.29, 17.32) * mm, "end": v(-11.1, 17.4) * mm});
            skArc(sketch, "E1266", {"start": v(-11.1, 17.4) * mm, "mid": v(-10.88, 17.45) * mm, "end": v(-10.66, 17.49) * mm});
            skArc(sketch, "E1267", {"start": v(-10.66, 17.49) * mm, "mid": v(-10.32, 17.5) * mm, "end": v(-9.98, 17.51) * mm});
            skArc(sketch, "E1268", {"start": v(-9.98, 17.51) * mm, "mid": v(-9.62, 17.5) * mm, "end": v(-9.25, 17.48) * mm});
            skArc(sketch, "E1269", {"start": v(-9.25, 17.48) * mm, "mid": v(-8.92, 17.44) * mm, "end": v(-8.58, 17.38) * mm});
            skArc(sketch, "E1270", {"start": v(2.3, 15.32) * mm, "mid": v(2.44, 15.22) * mm, "end": v(2.58, 15.12) * mm});
            skArc(sketch, "E1271", {"start": v(2.58, 15.12) * mm, "mid": v(2.71, 15.03) * mm, "end": v(2.85, 14.93) * mm});
            skArc(sketch, "E1272", {"start": v(2.85, 14.93) * mm, "mid": v(2.98, 14.85) * mm, "end": v(3.1, 14.77) * mm});
            skArc(sketch, "E1273", {"start": v(3.1, 14.77) * mm, "mid": v(3.18, 14.73) * mm, "end": v(3.26, 14.69) * mm});
            skArc(sketch, "E1274", {"start": v(3.26, 14.69) * mm, "mid": v(3.32, 14.66) * mm, "end": v(3.38, 14.62) * mm});
            skArc(sketch, "E1275", {"start": v(3.38, 14.62) * mm, "mid": v(3.44, 14.6) * mm, "end": v(3.49, 14.56) * mm});
            skArc(sketch, "E1276", {"start": v(3.49, 14.56) * mm, "mid": v(3.52, 14.53) * mm, "end": v(3.56, 14.5) * mm});
            skArc(sketch, "E1277", {"start": v(3.56, 14.5) * mm, "mid": v(3.57, 14.48) * mm, "end": v(3.58, 14.46) * mm});
            skArc(sketch, "E1278", {"start": v(3.58, 14.46) * mm, "mid": v(3.57, 14.43) * mm, "end": v(3.56, 14.42) * mm});
            skArc(sketch, "E1279", {"start": v(3.56, 14.42) * mm, "mid": v(3.5, 14.38) * mm, "end": v(3.46, 14.34) * mm});
            skArc(sketch, "E1280", {"start": v(3.46, 14.34) * mm, "mid": v(3.39, 14.3) * mm, "end": v(3.32, 14.26) * mm});
            skArc(sketch, "E1281", {"start": v(3.32, 14.26) * mm, "mid": v(3.24, 14.22) * mm, "end": v(3.16, 14.18) * mm});
            skLineSegment(sketch, "E1282", {"start": v(3.16, 14.18) * mm, "end": v(2.74, 13.97) * mm});
            skLineSegment(sketch, "E1283", {"start": v(2.74, 13.97) * mm, "end": v(1.68, 14.53) * mm});
            skArc(sketch, "E1284", {"start": v(1.68, 14.53) * mm, "mid": v(1.48, 14.64) * mm, "end": v(1.28, 14.75) * mm});
            skArc(sketch, "E1285", {"start": v(1.28, 14.75) * mm, "mid": v(1.1, 14.85) * mm, "end": v(0.94, 14.94) * mm});
            skArc(sketch, "E1286", {"start": v(0.94, 14.94) * mm, "mid": v(0.79, 15.03) * mm, "end": v(0.64, 15.11) * mm});
            skArc(sketch, "E1287", {"start": v(0.64, 15.11) * mm, "mid": v(0.63, 15.13) * mm, "end": v(0.63, 15.14) * mm});
            skArc(sketch, "E1288", {"start": v(0.63, 15.14) * mm, "mid": v(0.64, 15.18) * mm, "end": v(0.66, 15.21) * mm});
            skArc(sketch, "E1289", {"start": v(0.66, 15.21) * mm, "mid": v(0.87, 15.36) * mm, "end": v(1.08, 15.5) * mm});
            skArc(sketch, "E1290", {"start": v(1.08, 15.5) * mm, "mid": v(1.28, 15.64) * mm, "end": v(1.48, 15.78) * mm});
            skArc(sketch, "E1291", {"start": v(1.48, 15.78) * mm, "mid": v(1.54, 15.8) * mm, "end": v(1.6, 15.8) * mm});
            skArc(sketch, "E1292", {"start": v(1.6, 15.8) * mm, "mid": v(1.62, 15.8) * mm, "end": v(1.64, 15.8) * mm});
            skArc(sketch, "E1293", {"start": v(1.64, 15.8) * mm, "mid": v(1.74, 15.73) * mm, "end": v(1.83, 15.67) * mm});
            skArc(sketch, "E1294", {"start": v(1.83, 15.67) * mm, "mid": v(1.94, 15.59) * mm, "end": v(2.05, 15.5) * mm});
            skArc(sketch, "E1295", {"start": v(2.05, 15.5) * mm, "mid": v(2.18, 15.42) * mm, "end": v(2.3, 15.32) * mm});
            skArc(sketch, "E1296", {"start": v(11.44, 15.7) * mm, "mid": v(11.46, 15.65) * mm, "end": v(11.46, 15.6) * mm});
            skArc(sketch, "E1297", {"start": v(11.46, 15.6) * mm, "mid": v(11.41, 15.5) * mm, "end": v(11.36, 15.4) * mm});
            skArc(sketch, "E1298", {"start": v(11.36, 15.4) * mm, "mid": v(11.28, 15.28) * mm, "end": v(11.2, 15.17) * mm});
            skArc(sketch, "E1299", {"start": v(11.2, 15.17) * mm, "mid": v(11.1, 15.06) * mm, "end": v(10.98, 14.95) * mm});
            skArc(sketch, "E1300", {"start": v(10.98, 14.95) * mm, "mid": v(10.74, 14.75) * mm, "end": v(10.47, 14.6) * mm});
            skArc(sketch, "E1301", {"start": v(10.47, 14.6) * mm, "mid": v(10.15, 14.46) * mm, "end": v(9.81, 14.36) * mm});
            skArc(sketch, "E1302", {"start": v(9.81, 14.36) * mm, "mid": v(9.44, 14.29) * mm, "end": v(9.06, 14.25) * mm});
            skArc(sketch, "E1303", {"start": v(9.06, 14.25) * mm, "mid": v(8.67, 14.26) * mm, "end": v(8.28, 14.3) * mm});
            skArc(sketch, "E1304", {"start": v(8.28, 14.3) * mm, "mid": v(7.97, 14.34) * mm, "end": v(7.67, 14.4) * mm});
            skArc(sketch, "E1305", {"start": v(7.67, 14.4) * mm, "mid": v(7.32, 14.48) * mm, "end": v(6.98, 14.58) * mm});
            skArc(sketch, "E1306", {"start": v(6.98, 14.58) * mm, "mid": v(6.64, 14.67) * mm, "end": v(6.31, 14.77) * mm});
            skArc(sketch, "E1307", {"start": v(6.31, 14.77) * mm, "mid": v(6.26, 14.8) * mm, "end": v(6.24, 14.86) * mm});
            skArc(sketch, "E1308", {"start": v(6.24, 14.86) * mm, "mid": v(6.26, 14.92) * mm, "end": v(6.3, 14.96) * mm});
            skArc(sketch, "E1309", {"start": v(6.3, 14.96) * mm, "mid": v(6.65, 15.1) * mm, "end": v(6.99, 15.24) * mm});
            skArc(sketch, "E1310", {"start": v(6.99, 15.24) * mm, "mid": v(7.32, 15.37) * mm, "end": v(7.67, 15.5) * mm});
            skArc(sketch, "E1311", {"start": v(7.67, 15.5) * mm, "mid": v(7.94, 15.59) * mm, "end": v(8.22, 15.66) * mm});
            skArc(sketch, "E1312", {"start": v(8.22, 15.66) * mm, "mid": v(8.52, 15.72) * mm, "end": v(8.83, 15.75) * mm});
            skArc(sketch, "E1313", {"start": v(8.83, 15.75) * mm, "mid": v(9.4, 15.77) * mm, "end": v(10, 15.78) * mm});
            skArc(sketch, "E1314", {"start": v(10, 15.78) * mm, "mid": v(10.6, 15.79) * mm, "end": v(11.22, 15.78) * mm});
            skArc(sketch, "E1315", {"start": v(11.22, 15.78) * mm, "mid": v(11.34, 15.76) * mm, "end": v(11.44, 15.7) * mm});
            skArc(sketch, "E1316", {"start": v(13, 15.14) * mm, "mid": v(13.2, 14.97) * mm, "end": v(13.41, 14.79) * mm});
            skArc(sketch, "E1317", {"start": v(13.41, 14.79) * mm, "mid": v(13.57, 14.6) * mm, "end": v(13.71, 14.4) * mm});
            skArc(sketch, "E1318", {"start": v(13.71, 14.4) * mm, "mid": v(13.82, 14.21) * mm, "end": v(13.9, 14) * mm});
            skArc(sketch, "E1319", {"start": v(13.9, 14) * mm, "mid": v(13.94, 13.8) * mm, "end": v(13.96, 13.6) * mm});
            skArc(sketch, "E1320", {"start": v(13.96, 13.6) * mm, "mid": v(13.94, 13.3) * mm, "end": v(13.87, 13) * mm});
            skArc(sketch, "E1321", {"start": v(13.87, 13) * mm, "mid": v(13.76, 12.74) * mm, "end": v(13.6, 12.5) * mm});
            skArc(sketch, "E1322", {"start": v(13.6, 12.5) * mm, "mid": v(13.4, 12.27) * mm, "end": v(13.15, 12.07) * mm});
            skArc(sketch, "E1323", {"start": v(13.15, 12.07) * mm, "mid": v(12.83, 11.87) * mm, "end": v(12.5, 11.7) * mm});
            skLineSegment(sketch, "E1324", {"start": v(12.5, 11.7) * mm, "end": v(12.03, 11.5) * mm});
            skLineSegment(sketch, "E1325", {"start": v(12.03, 11.5) * mm, "end": v(11.6, 11.94) * mm});
            skArc(sketch, "E1326", {"start": v(11.6, 11.94) * mm, "mid": v(11.38, 12.13) * mm, "end": v(11.14, 12.3) * mm});
            skArc(sketch, "E1327", {"start": v(11.14, 12.3) * mm, "mid": v(10.9, 12.46) * mm, "end": v(10.66, 12.58) * mm});
            skArc(sketch, "E1328", {"start": v(10.66, 12.58) * mm, "mid": v(10.4, 12.68) * mm, "end": v(10.13, 12.75) * mm});
            skArc(sketch, "E1329", {"start": v(10.13, 12.75) * mm, "mid": v(9.83, 12.8) * mm, "end": v(9.52, 12.84) * mm});
            skArc(sketch, "E1330", {"start": v(9.52, 12.84) * mm, "mid": v(9.22, 12.84) * mm, "end": v(8.91, 12.83) * mm});
            skArc(sketch, "E1331", {"start": v(8.91, 12.83) * mm, "mid": v(8.55, 12.8) * mm, "end": v(8.18, 12.74) * mm});
            skArc(sketch, "E1332", {"start": v(8.18, 12.74) * mm, "mid": v(7.81, 12.67) * mm, "end": v(7.44, 12.59) * mm});
            skArc(sketch, "E1333", {"start": v(7.44, 12.59) * mm, "mid": v(7.12, 12.5) * mm, "end": v(6.8, 12.38) * mm});
            skLineSegment(sketch, "E1334", {"start": v(6.8, 12.38) * mm, "end": v(6.33, 12.2) * mm});
            skLineSegment(sketch, "E1335", {"start": v(6.33, 12.2) * mm, "end": v(5.05, 12.82) * mm});
            skArc(sketch, "E1336", {"start": v(5.05, 12.82) * mm, "mid": v(4.8, 12.94) * mm, "end": v(4.56, 13.06) * mm});
            skArc(sketch, "E1337", {"start": v(4.56, 13.06) * mm, "mid": v(4.35, 13.16) * mm, "end": v(4.15, 13.27) * mm});
            skArc(sketch, "E1338", {"start": v(4.15, 13.27) * mm, "mid": v(3.97, 13.37) * mm, "end": v(3.8, 13.46) * mm});
            skArc(sketch, "E1339", {"start": v(3.8, 13.46) * mm, "mid": v(3.77, 13.48) * mm, "end": v(3.77, 13.5) * mm});
            skArc(sketch, "E1340", {"start": v(3.77, 13.5) * mm, "mid": v(3.77, 13.52) * mm, "end": v(3.79, 13.54) * mm});
            skArc(sketch, "E1341", {"start": v(3.79, 13.54) * mm, "mid": v(3.84, 13.58) * mm, "end": v(3.89, 13.62) * mm});
            skArc(sketch, "E1342", {"start": v(3.89, 13.62) * mm, "mid": v(3.95, 13.67) * mm, "end": v(4.02, 13.7) * mm});
            skArc(sketch, "E1343", {"start": v(4.02, 13.7) * mm, "mid": v(4.1, 13.75) * mm, "end": v(4.18, 13.8) * mm});
            skLineSegment(sketch, "E1344", {"start": v(4.18, 13.8) * mm, "end": v(4.59, 14.02) * mm});
            skLineSegment(sketch, "E1345", {"start": v(4.59, 14.02) * mm, "end": v(5.3, 13.78) * mm});
            skArc(sketch, "E1346", {"start": v(5.3, 13.78) * mm, "mid": v(6.07, 13.55) * mm, "end": v(6.86, 13.38) * mm});
            skArc(sketch, "E1347", {"start": v(6.86, 13.38) * mm, "mid": v(7.64, 13.27) * mm, "end": v(8.42, 13.24) * mm});
            skArc(sketch, "E1348", {"start": v(8.42, 13.24) * mm, "mid": v(9.12, 13.27) * mm, "end": v(9.82, 13.37) * mm});
            skArc(sketch, "E1349", {"start": v(9.82, 13.37) * mm, "mid": v(10.37, 13.52) * mm, "end": v(10.89, 13.77) * mm});
            skArc(sketch, "E1350", {"start": v(10.89, 13.77) * mm, "mid": v(11.08, 13.9) * mm, "end": v(11.27, 14.03) * mm});
            skArc(sketch, "E1351", {"start": v(11.27, 14.03) * mm, "mid": v(11.45, 14.18) * mm, "end": v(11.61, 14.35) * mm});
            skArc(sketch, "E1352", {"start": v(11.61, 14.35) * mm, "mid": v(11.76, 14.52) * mm, "end": v(11.9, 14.7) * mm});
            skArc(sketch, "E1353", {"start": v(11.9, 14.7) * mm, "mid": v(12.01, 14.87) * mm, "end": v(12.1, 15.05) * mm});
            skArc(sketch, "E1354", {"start": v(12.1, 15.05) * mm, "mid": v(12.17, 15.19) * mm, "end": v(12.26, 15.32) * mm});
            skArc(sketch, "E1355", {"start": v(12.26, 15.32) * mm, "mid": v(12.33, 15.38) * mm, "end": v(12.43, 15.41) * mm});
            skArc(sketch, "E1356", {"start": v(12.43, 15.41) * mm, "mid": v(12.54, 15.4) * mm, "end": v(12.64, 15.37) * mm});
            skArc(sketch, "E1357", {"start": v(12.64, 15.37) * mm, "mid": v(12.82, 15.26) * mm, "end": v(13, 15.14) * mm});
            skArc(sketch, "E1358", {"start": v(-2.35, 14.95) * mm, "mid": v(-2.22, 14.87) * mm, "end": v(-2.09, 14.8) * mm});
            skArc(sketch, "E1359", {"start": v(-2.09, 14.8) * mm, "mid": v(-1.97, 14.73) * mm, "end": v(-1.86, 14.67) * mm});
            skArc(sketch, "E1360", {"start": v(-1.86, 14.67) * mm, "mid": v(-1.77, 14.6) * mm, "end": v(-1.67, 14.55) * mm});
            skArc(sketch, "E1361", {"start": v(-1.67, 14.55) * mm, "mid": v(-1.66, 14.54) * mm, "end": v(-1.66, 14.53) * mm});
            skArc(sketch, "E1362", {"start": v(-1.66, 14.53) * mm, "mid": v(-1.66, 14.52) * mm, "end": v(-1.67, 14.5) * mm});
            skArc(sketch, "E1363", {"start": v(-1.67, 14.5) * mm, "mid": v(-1.76, 14.43) * mm, "end": v(-1.85, 14.36) * mm});
            skArc(sketch, "E1364", {"start": v(-1.85, 14.36) * mm, "mid": v(-1.96, 14.28) * mm, "end": v(-2.06, 14.2) * mm});
            skArc(sketch, "E1365", {"start": v(-2.06, 14.2) * mm, "mid": v(-2.19, 14.1) * mm, "end": v(-2.3, 14.01) * mm});
            skLineSegment(sketch, "E1366", {"start": v(-2.3, 14.01) * mm, "end": v(-2.96, 13.53) * mm});
            skLineSegment(sketch, "E1367", {"start": v(-2.96, 13.53) * mm, "end": v(-3.79, 13.96) * mm});
            skLineSegment(sketch, "E1368", {"start": v(-3.79, 13.96) * mm, "end": v(-4.62, 14.4) * mm});
            skLineSegment(sketch, "E1369", {"start": v(-4.62, 14.4) * mm, "end": v(-3.93, 14.86) * mm});
            skArc(sketch, "E1370", {"start": v(-3.93, 14.86) * mm, "mid": v(-3.79, 14.95) * mm, "end": v(-3.65, 15.03) * mm});
            skArc(sketch, "E1371", {"start": v(-3.65, 15.03) * mm, "mid": v(-3.53, 15.1) * mm, "end": v(-3.4, 15.18) * mm});
            skArc(sketch, "E1372", {"start": v(-3.4, 15.18) * mm, "mid": v(-3.3, 15.25) * mm, "end": v(-3.2, 15.3) * mm});
            skArc(sketch, "E1373", {"start": v(-3.2, 15.3) * mm, "mid": v(-3.17, 15.32) * mm, "end": v(-3.14, 15.32) * mm});
            skArc(sketch, "E1374", {"start": v(-3.14, 15.32) * mm, "mid": v(-3.1, 15.32) * mm, "end": v(-3.07, 15.31) * mm});
            skArc(sketch, "E1375", {"start": v(-3.07, 15.31) * mm, "mid": v(-2.97, 15.27) * mm, "end": v(-2.87, 15.22) * mm});
            skArc(sketch, "E1376", {"start": v(-2.87, 15.22) * mm, "mid": v(-2.74, 15.16) * mm, "end": v(-2.62, 15.1) * mm});
            skArc(sketch, "E1377", {"start": v(-2.62, 15.1) * mm, "mid": v(-2.49, 15.02) * mm, "end": v(-2.35, 14.95) * mm});
            skArc(sketch, "E1378", {"start": v(-9.52, 14.34) * mm, "mid": v(-9.18, 14.28) * mm, "end": v(-8.84, 14.2) * mm});
            skArc(sketch, "E1379", {"start": v(-8.84, 14.2) * mm, "mid": v(-8.51, 14.13) * mm, "end": v(-8.2, 14.05) * mm});
            skArc(sketch, "E1380", {"start": v(-8.2, 14.05) * mm, "mid": v(-7.9, 13.97) * mm, "end": v(-7.62, 13.88) * mm});
            skArc(sketch, "E1381", {"start": v(-7.62, 13.88) * mm, "mid": v(-7.58, 13.85) * mm, "end": v(-7.57, 13.8) * mm});
            skArc(sketch, "E1382", {"start": v(-7.57, 13.8) * mm, "mid": v(-7.6, 13.74) * mm, "end": v(-7.66, 13.7) * mm});
            skArc(sketch, "E1383", {"start": v(-7.66, 13.7) * mm, "mid": v(-8.03, 13.65) * mm, "end": v(-8.4, 13.6) * mm});
            skArc(sketch, "E1384", {"start": v(-8.4, 13.6) * mm, "mid": v(-8.79, 13.57) * mm, "end": v(-9.18, 13.54) * mm});
            skArc(sketch, "E1385", {"start": v(-9.18, 13.54) * mm, "mid": v(-9.52, 13.54) * mm, "end": v(-9.87, 13.54) * mm});
            skArc(sketch, "E1386", {"start": v(-9.87, 13.54) * mm, "mid": v(-10.22, 13.57) * mm, "end": v(-10.56, 13.62) * mm});
            skArc(sketch, "E1387", {"start": v(-10.56, 13.62) * mm, "mid": v(-10.88, 13.68) * mm, "end": v(-11.2, 13.77) * mm});
            skArc(sketch, "E1388", {"start": v(-11.2, 13.77) * mm, "mid": v(-11.46, 13.86) * mm, "end": v(-11.72, 13.98) * mm});
            skArc(sketch, "E1389", {"start": v(-11.72, 13.98) * mm, "mid": v(-11.93, 14.1) * mm, "end": v(-12.12, 14.24) * mm});
            skLineSegment(sketch, "E1390", {"start": v(-12.12, 14.24) * mm, "end": v(-12.38, 14.47) * mm});
            skLineSegment(sketch, "E1391", {"start": v(-12.38, 14.47) * mm, "end": v(-11.33, 14.47) * mm});
            skArc(sketch, "E1392", {"start": v(-11.33, 14.47) * mm, "mid": v(-11.1, 14.47) * mm, "end": v(-10.87, 14.46) * mm});
            skArc(sketch, "E1393", {"start": v(-10.87, 14.46) * mm, "mid": v(-10.62, 14.45) * mm, "end": v(-10.36, 14.44) * mm});
            skArc(sketch, "E1394", {"start": v(-10.36, 14.44) * mm, "mid": v(-10.12, 14.42) * mm, "end": v(-9.89, 14.4) * mm});
            skArc(sketch, "E1395", {"start": v(-9.89, 14.4) * mm, "mid": v(-9.7, 14.37) * mm, "end": v(-9.52, 14.34) * mm});
            skArc(sketch, "E1396", {"start": v(-13.02, 13.77) * mm, "mid": v(-12.78, 13.55) * mm, "end": v(-12.53, 13.36) * mm});
            skArc(sketch, "E1397", {"start": v(-12.53, 13.36) * mm, "mid": v(-12.26, 13.21) * mm, "end": v(-11.98, 13.1) * mm});
            skArc(sketch, "E1398", {"start": v(-11.98, 13.1) * mm, "mid": v(-11.63, 13) * mm, "end": v(-11.27, 12.95) * mm});
            skArc(sketch, "E1399", {"start": v(-11.27, 12.95) * mm, "mid": v(-10.76, 12.9) * mm, "end": v(-10.25, 12.88) * mm});
            skArc(sketch, "E1400", {"start": v(-10.25, 12.88) * mm, "mid": v(-9.77, 12.87) * mm, "end": v(-9.29, 12.87) * mm});
            skArc(sketch, "E1401", {"start": v(-9.29, 12.87) * mm, "mid": v(-8.87, 12.9) * mm, "end": v(-8.45, 12.93) * mm});
            skArc(sketch, "E1402", {"start": v(-8.45, 12.93) * mm, "mid": v(-8.08, 12.98) * mm, "end": v(-7.71, 13.05) * mm});
            skArc(sketch, "E1403", {"start": v(-7.71, 13.05) * mm, "mid": v(-7.37, 13.14) * mm, "end": v(-7.03, 13.24) * mm});
            skLineSegment(sketch, "E1404", {"start": v(-7.03, 13.24) * mm, "end": v(-6.5, 13.42) * mm});
            skLineSegment(sketch, "E1405", {"start": v(-6.5, 13.42) * mm, "end": v(-5.68, 13) * mm});
            skArc(sketch, "E1406", {"start": v(-5.68, 13) * mm, "mid": v(-5.26, 12.79) * mm, "end": v(-4.85, 12.57) * mm});
            skArc(sketch, "E1407", {"start": v(-4.85, 12.57) * mm, "mid": v(-4.78, 12.52) * mm, "end": v(-4.73, 12.44) * mm});
            skArc(sketch, "E1408", {"start": v(-4.73, 12.44) * mm, "mid": v(-4.72, 12.37) * mm, "end": v(-4.76, 12.3) * mm});
            skArc(sketch, "E1409", {"start": v(-4.76, 12.3) * mm, "mid": v(-4.97, 12.15) * mm, "end": v(-5.2, 12) * mm});
            skLineSegment(sketch, "E1410", {"start": v(-5.2, 12) * mm, "end": v(-5.79, 11.59) * mm});
            skLineSegment(sketch, "E1411", {"start": v(-5.79, 11.59) * mm, "end": v(-6.8, 11.93) * mm});
            skArc(sketch, "E1412", {"start": v(-6.8, 11.93) * mm, "mid": v(-7.42, 12.13) * mm, "end": v(-8.05, 12.3) * mm});
            skArc(sketch, "E1413", {"start": v(-8.05, 12.3) * mm, "mid": v(-8.56, 12.4) * mm, "end": v(-9.08, 12.45) * mm});
            skArc(sketch, "E1414", {"start": v(-9.08, 12.45) * mm, "mid": v(-9.55, 12.45) * mm, "end": v(-10.03, 12.41) * mm});
            skArc(sketch, "E1415", {"start": v(-10.03, 12.41) * mm, "mid": v(-10.53, 12.32) * mm, "end": v(-11.01, 12.2) * mm});
            skArc(sketch, "E1416", {"start": v(-11.01, 12.2) * mm, "mid": v(-11.46, 12.02) * mm, "end": v(-11.9, 11.8) * mm});
            skArc(sketch, "E1417", {"start": v(-11.9, 11.8) * mm, "mid": v(-12.24, 11.53) * mm, "end": v(-12.55, 11.2) * mm});
            skArc(sketch, "E1418", {"start": v(-12.55, 11.2) * mm, "mid": v(-12.79, 10.85) * mm, "end": v(-12.96, 10.46) * mm});
            skArc(sketch, "E1419", {"start": v(-12.96, 10.46) * mm, "mid": v(-13.07, 10.02) * mm, "end": v(-13.12, 9.57) * mm});
            skArc(sketch, "E1420", {"start": v(-13.12, 9.57) * mm, "mid": v(-13.13, 9.34) * mm, "end": v(-13.16, 9.11) * mm});
            skArc(sketch, "E1421", {"start": v(-13.16, 9.11) * mm, "mid": v(-13.2, 9.02) * mm, "end": v(-13.28, 8.96) * mm});
            skArc(sketch, "E1422", {"start": v(-13.28, 8.96) * mm, "mid": v(-13.4, 8.94) * mm, "end": v(-13.51, 8.97) * mm});
            skArc(sketch, "E1423", {"start": v(-13.51, 8.97) * mm, "mid": v(-13.8, 9.1) * mm, "end": v(-14.1, 9.23) * mm});
            skArc(sketch, "E1424", {"start": v(-14.1, 9.23) * mm, "mid": v(-14.32, 9.34) * mm, "end": v(-14.53, 9.47) * mm});
            skArc(sketch, "E1425", {"start": v(-14.53, 9.47) * mm, "mid": v(-14.7, 9.6) * mm, "end": v(-14.87, 9.74) * mm});
            skArc(sketch, "E1426", {"start": v(-14.87, 9.74) * mm, "mid": v(-15.02, 9.9) * mm, "end": v(-15.15, 10.07) * mm});
            skArc(sketch, "E1427", {"start": v(-15.15, 10.07) * mm, "mid": v(-15.29, 10.29) * mm, "end": v(-15.42, 10.51) * mm});
            skArc(sketch, "E1428", {"start": v(-15.42, 10.51) * mm, "mid": v(-15.56, 10.85) * mm, "end": v(-15.65, 11.2) * mm});
            skArc(sketch, "E1429", {"start": v(-15.65, 11.2) * mm, "mid": v(-15.67, 11.55) * mm, "end": v(-15.63, 11.9) * mm});
            skArc(sketch, "E1430", {"start": v(-15.63, 11.9) * mm, "mid": v(-15.53, 12.27) * mm, "end": v(-15.38, 12.61) * mm});
            skArc(sketch, "E1431", {"start": v(-15.38, 12.61) * mm, "mid": v(-15.15, 12.97) * mm, "end": v(-14.88, 13.3) * mm});
            skArc(sketch, "E1432", {"start": v(-14.88, 13.3) * mm, "mid": v(-14.74, 13.44) * mm, "end": v(-14.58, 13.57) * mm});
            skArc(sketch, "E1433", {"start": v(-14.58, 13.57) * mm, "mid": v(-14.36, 13.73) * mm, "end": v(-14.14, 13.88) * mm});
            skArc(sketch, "E1434", {"start": v(-14.14, 13.88) * mm, "mid": v(-13.93, 14) * mm, "end": v(-13.7, 14.13) * mm});
            skArc(sketch, "E1435", {"start": v(-13.7, 14.13) * mm, "mid": v(-13.6, 14.17) * mm, "end": v(-13.47, 14.19) * mm});
            skArc(sketch, "E1436", {"start": v(-13.47, 14.19) * mm, "mid": v(-13.46, 14.18) * mm, "end": v(-13.44, 14.18) * mm});
            skArc(sketch, "E1437", {"start": v(-13.44, 14.18) * mm, "mid": v(-13.38, 14.12) * mm, "end": v(-13.32, 14.06) * mm});
            skArc(sketch, "E1438", {"start": v(-13.32, 14.06) * mm, "mid": v(-13.25, 14) * mm, "end": v(-13.18, 13.93) * mm});
            skArc(sketch, "E1439", {"start": v(-13.18, 13.93) * mm, "mid": v(-13.1, 13.85) * mm, "end": v(-13.02, 13.77) * mm});
            skArc(sketch, "E1440", {"start": v(0.15, 13.6) * mm, "mid": v(0.32, 13.5) * mm, "end": v(0.5, 13.4) * mm});
            skArc(sketch, "E1441", {"start": v(0.5, 13.4) * mm, "mid": v(0.64, 13.3) * mm, "end": v(0.78, 13.21) * mm});
            skArc(sketch, "E1442", {"start": v(0.78, 13.21) * mm, "mid": v(0.9, 13.13) * mm, "end": v(1.02, 13.05) * mm});
            skArc(sketch, "E1443", {"start": v(1.02, 13.05) * mm, "mid": v(1.04, 13.03) * mm, "end": v(1.04, 13) * mm});
            skArc(sketch, "E1444", {"start": v(1.04, 13) * mm, "mid": v(1.03, 12.97) * mm, "end": v(1.01, 12.95) * mm});
            skArc(sketch, "E1445", {"start": v(1.01, 12.95) * mm, "mid": v(0.92, 12.88) * mm, "end": v(0.82, 12.8) * mm});
            skArc(sketch, "E1446", {"start": v(0.82, 12.8) * mm, "mid": v(0.7, 12.72) * mm, "end": v(0.58, 12.63) * mm});
            skArc(sketch, "E1447", {"start": v(0.58, 12.63) * mm, "mid": v(0.44, 12.54) * mm, "end": v(0.3, 12.45) * mm});
            skLineSegment(sketch, "E1448", {"start": v(0.3, 12.45) * mm, "end": v(-0.43, 12) * mm});
            skLineSegment(sketch, "E1449", {"start": v(-0.43, 12) * mm, "end": v(-1.33, 12.54) * mm});
            skArc(sketch, "E1450", {"start": v(-1.33, 12.54) * mm, "mid": v(-1.5, 12.65) * mm, "end": v(-1.67, 12.76) * mm});
            skArc(sketch, "E1451", {"start": v(-1.67, 12.76) * mm, "mid": v(-1.82, 12.86) * mm, "end": v(-1.96, 12.95) * mm});
            skArc(sketch, "E1452", {"start": v(-1.96, 12.95) * mm, "mid": v(-2.08, 13.04) * mm, "end": v(-2.2, 13.12) * mm});
            skArc(sketch, "E1453", {"start": v(-2.2, 13.12) * mm, "mid": v(-2.2, 13.14) * mm, "end": v(-2.2, 13.16) * mm});
            skArc(sketch, "E1454", {"start": v(-2.2, 13.16) * mm, "mid": v(-2.18, 13.22) * mm, "end": v(-2.13, 13.27) * mm});
            skArc(sketch, "E1455", {"start": v(-2.13, 13.27) * mm, "mid": v(-1.84, 13.47) * mm, "end": v(-1.56, 13.66) * mm});
            skArc(sketch, "E1456", {"start": v(-1.56, 13.66) * mm, "mid": v(-1.27, 13.86) * mm, "end": v(-0.99, 14.05) * mm});
            skArc(sketch, "E1457", {"start": v(-0.99, 14.05) * mm, "mid": v(-0.92, 14.08) * mm, "end": v(-0.85, 14.1) * mm});
            skArc(sketch, "E1458", {"start": v(-0.85, 14.1) * mm, "mid": v(-0.82, 14.09) * mm, "end": v(-0.79, 14.08) * mm});
            skArc(sketch, "E1459", {"start": v(-0.79, 14.08) * mm, "mid": v(-0.65, 14.01) * mm, "end": v(-0.52, 13.95) * mm});
            skArc(sketch, "E1460", {"start": v(-0.52, 13.95) * mm, "mid": v(-0.36, 13.87) * mm, "end": v(-0.2, 13.78) * mm});
            skArc(sketch, "E1461", {"start": v(-0.2, 13.78) * mm, "mid": v(-0.03, 13.69) * mm, "end": v(0.15, 13.6) * mm});
            skLineSegment(sketch, "E1462", {"start": v(3.3, 11.9) * mm, "end": v(4.45, 11.32) * mm});
            skLineSegment(sketch, "E1463", {"start": v(4.45, 11.32) * mm, "end": v(3.75, 10.84) * mm});
            skArc(sketch, "E1464", {"start": v(3.75, 10.84) * mm, "mid": v(3.61, 10.74) * mm, "end": v(3.47, 10.65) * mm});
            skArc(sketch, "E1465", {"start": v(3.47, 10.65) * mm, "mid": v(3.34, 10.55) * mm, "end": v(3.2, 10.45) * mm});
            skArc(sketch, "E1466", {"start": v(3.2, 10.45) * mm, "mid": v(3.09, 10.37) * mm, "end": v(2.97, 10.28) * mm});
            skArc(sketch, "E1467", {"start": v(2.97, 10.28) * mm, "mid": v(2.91, 10.23) * mm, "end": v(2.86, 10.18) * mm});
            skArc(sketch, "E1468", {"start": v(2.86, 10.18) * mm, "mid": v(2.82, 10.15) * mm, "end": v(2.78, 10.11) * mm});
            skArc(sketch, "E1469", {"start": v(2.78, 10.11) * mm, "mid": v(2.74, 10.08) * mm, "end": v(2.7, 10.05) * mm});
            skArc(sketch, "E1470", {"start": v(2.7, 10.05) * mm, "mid": v(2.66, 10.03) * mm, "end": v(2.63, 10) * mm});
            skArc(sketch, "E1471", {"start": v(2.63, 10) * mm, "mid": v(2.61, 10) * mm, "end": v(2.6, 10) * mm});
            skArc(sketch, "E1472", {"start": v(2.6, 10) * mm, "mid": v(2.57, 10) * mm, "end": v(2.55, 10.01) * mm});
            skArc(sketch, "E1473", {"start": v(2.55, 10.01) * mm, "mid": v(2.38, 10.12) * mm, "end": v(2.22, 10.22) * mm});
            skArc(sketch, "E1474", {"start": v(2.22, 10.22) * mm, "mid": v(2.04, 10.34) * mm, "end": v(1.85, 10.46) * mm});
            skArc(sketch, "E1475", {"start": v(1.85, 10.46) * mm, "mid": v(1.64, 10.6) * mm, "end": v(1.43, 10.75) * mm});
            skLineSegment(sketch, "E1476", {"start": v(1.43, 10.75) * mm, "end": v(0.33, 11.5) * mm});
            skLineSegment(sketch, "E1477", {"start": v(0.33, 11.5) * mm, "end": v(1.12, 11.99) * mm});
            skArc(sketch, "E1478", {"start": v(1.12, 11.99) * mm, "mid": v(1.28, 12.08) * mm, "end": v(1.43, 12.17) * mm});
            skArc(sketch, "E1479", {"start": v(1.43, 12.17) * mm, "mid": v(1.57, 12.25) * mm, "end": v(1.71, 12.33) * mm});
            skArc(sketch, "E1480", {"start": v(1.71, 12.33) * mm, "mid": v(1.83, 12.4) * mm, "end": v(1.95, 12.45) * mm});
            skArc(sketch, "E1481", {"start": v(1.95, 12.45) * mm, "mid": v(2, 12.47) * mm, "end": v(2.03, 12.47) * mm});
            skArc(sketch, "E1482", {"start": v(2.03, 12.47) * mm, "mid": v(2.07, 12.47) * mm, "end": v(2.11, 12.46) * mm});
            skArc(sketch, "E1483", {"start": v(2.11, 12.46) * mm, "mid": v(2.28, 12.38) * mm, "end": v(2.45, 12.3) * mm});
            skArc(sketch, "E1484", {"start": v(2.45, 12.3) * mm, "mid": v(2.65, 12.21) * mm, "end": v(2.85, 12.12) * mm});
            skArc(sketch, "E1485", {"start": v(2.85, 12.12) * mm, "mid": v(3.08, 12) * mm, "end": v(3.3, 11.9) * mm});
            skArc(sketch, "E1486", {"start": v(10.3, 11.93) * mm, "mid": v(10.38, 11.88) * mm, "end": v(10.45, 11.84) * mm});
            skArc(sketch, "E1487", {"start": v(10.45, 11.84) * mm, "mid": v(10.54, 11.79) * mm, "end": v(10.62, 11.73) * mm});
            skArc(sketch, "E1488", {"start": v(10.62, 11.73) * mm, "mid": v(10.69, 11.68) * mm, "end": v(10.76, 11.63) * mm});
            skArc(sketch, "E1489", {"start": v(10.76, 11.63) * mm, "mid": v(10.8, 11.59) * mm, "end": v(10.85, 11.54) * mm});
            skArc(sketch, "E1490", {"start": v(10.85, 11.54) * mm, "mid": v(10.9, 11.48) * mm, "end": v(10.96, 11.41) * mm});
            skArc(sketch, "E1491", {"start": v(10.96, 11.41) * mm, "mid": v(10.96, 11.39) * mm, "end": v(10.96, 11.36) * mm});
            skArc(sketch, "E1492", {"start": v(10.96, 11.36) * mm, "mid": v(10.93, 11.34) * mm, "end": v(10.9, 11.33) * mm});
            skArc(sketch, "E1493", {"start": v(10.9, 11.33) * mm, "mid": v(10.78, 11.3) * mm, "end": v(10.67, 11.28) * mm});
            skArc(sketch, "E1494", {"start": v(10.67, 11.28) * mm, "mid": v(10.31, 11.24) * mm, "end": v(9.96, 11.25) * mm});
            skArc(sketch, "E1495", {"start": v(9.96, 11.25) * mm, "mid": v(9.34, 11.32) * mm, "end": v(8.72, 11.41) * mm});
            skArc(sketch, "E1496", {"start": v(8.72, 11.41) * mm, "mid": v(8.08, 11.52) * mm, "end": v(7.45, 11.64) * mm});
            skArc(sketch, "E1497", {"start": v(7.45, 11.64) * mm, "mid": v(7.34, 11.7) * mm, "end": v(7.3, 11.83) * mm});
            skArc(sketch, "E1498", {"start": v(7.3, 11.83) * mm, "mid": v(7.3, 11.85) * mm, "end": v(7.31, 11.86) * mm});
            skArc(sketch, "E1499", {"start": v(7.31, 11.86) * mm, "mid": v(7.35, 11.88) * mm, "end": v(7.4, 11.9) * mm});
            skArc(sketch, "E1500", {"start": v(7.4, 11.9) * mm, "mid": v(7.45, 11.93) * mm, "end": v(7.51, 11.95) * mm});
            skArc(sketch, "E1501", {"start": v(7.51, 11.95) * mm, "mid": v(7.58, 11.97) * mm, "end": v(7.65, 11.99) * mm});
            skArc(sketch, "E1502", {"start": v(7.65, 11.99) * mm, "mid": v(7.73, 12) * mm, "end": v(7.8, 12.03) * mm});
            skArc(sketch, "E1503", {"start": v(7.8, 12.03) * mm, "mid": v(7.88, 12.05) * mm, "end": v(7.96, 12.07) * mm});
            skArc(sketch, "E1504", {"start": v(7.96, 12.07) * mm, "mid": v(8.03, 12.09) * mm, "end": v(8.1, 12.1) * mm});
            skArc(sketch, "E1505", {"start": v(8.1, 12.1) * mm, "mid": v(8.15, 12.12) * mm, "end": v(8.2, 12.13) * mm});
            skArc(sketch, "E1506", {"start": v(8.2, 12.13) * mm, "mid": v(8.4, 12.17) * mm, "end": v(8.62, 12.18) * mm});
            skArc(sketch, "E1507", {"start": v(8.62, 12.18) * mm, "mid": v(8.94, 12.17) * mm, "end": v(9.27, 12.14) * mm});
            skArc(sketch, "E1508", {"start": v(9.27, 12.14) * mm, "mid": v(9.6, 12.1) * mm, "end": v(9.91, 12.05) * mm});
            skArc(sketch, "E1509", {"start": v(9.91, 12.05) * mm, "mid": v(10.11, 12) * mm, "end": v(10.3, 11.93) * mm});
            skArc(sketch, "E1510", {"start": v(-2.97, 11.52) * mm, "mid": v(-2.81, 11.42) * mm, "end": v(-2.65, 11.33) * mm});
            skArc(sketch, "E1511", {"start": v(-2.65, 11.33) * mm, "mid": v(-2.52, 11.24) * mm, "end": v(-2.38, 11.15) * mm});
            skArc(sketch, "E1512", {"start": v(-2.38, 11.16) * mm, "mid": v(-2.27, 11.08) * mm, "end": v(-2.16, 11) * mm});
            skArc(sketch, "E1513", {"start": v(-2.16, 11) * mm, "mid": v(-2.14, 10.99) * mm, "end": v(-2.14, 10.97) * mm});
            skArc(sketch, "E1514", {"start": v(-2.14, 10.97) * mm, "mid": v(-2.14, 10.95) * mm, "end": v(-2.16, 10.93) * mm});
            skArc(sketch, "E1515", {"start": v(-2.16, 10.93) * mm, "mid": v(-2.24, 10.87) * mm, "end": v(-2.32, 10.81) * mm});
            skArc(sketch, "E1516", {"start": v(-2.32, 10.81) * mm, "mid": v(-2.42, 10.74) * mm, "end": v(-2.53, 10.68) * mm});
            skArc(sketch, "E1517", {"start": v(-2.53, 10.68) * mm, "mid": v(-2.65, 10.6) * mm, "end": v(-2.77, 10.53) * mm});
            skArc(sketch, "E1518", {"start": v(-2.77, 10.53) * mm, "mid": v(-2.97, 10.41) * mm, "end": v(-3.17, 10.3) * mm});
            skArc(sketch, "E1519", {"start": v(-3.17, 10.3) * mm, "mid": v(-3.26, 10.26) * mm, "end": v(-3.34, 10.23) * mm});
            skArc(sketch, "E1520", {"start": v(-3.34, 10.23) * mm, "mid": v(-3.41, 10.22) * mm, "end": v(-3.48, 10.24) * mm});
            skArc(sketch, "E1521", {"start": v(-3.48, 10.24) * mm, "mid": v(-3.56, 10.27) * mm, "end": v(-3.65, 10.32) * mm});
            skArc(sketch, "E1522", {"start": v(-3.65, 10.32) * mm, "mid": v(-3.71, 10.36) * mm, "end": v(-3.78, 10.4) * mm});
            skArc(sketch, "E1523", {"start": v(-3.78, 10.4) * mm, "mid": v(-3.9, 10.47) * mm, "end": v(-4, 10.54) * mm});
            skArc(sketch, "E1524", {"start": v(-4, 10.54) * mm, "mid": v(-4.12, 10.61) * mm, "end": v(-4.25, 10.69) * mm});
            skArc(sketch, "E1525", {"start": v(-4.25, 10.69) * mm, "mid": v(-4.37, 10.76) * mm, "end": v(-4.5, 10.83) * mm});
            skArc(sketch, "E1526", {"start": v(-4.5, 10.83) * mm, "mid": v(-4.6, 10.9) * mm, "end": v(-4.72, 10.97) * mm});
            skArc(sketch, "E1527", {"start": v(-4.72, 10.97) * mm, "mid": v(-4.82, 11.04) * mm, "end": v(-4.91, 11.1) * mm});
            skArc(sketch, "E1528", {"start": v(-4.91, 11.1) * mm, "mid": v(-5, 11.15) * mm, "end": v(-5.07, 11.2) * mm});
            skArc(sketch, "E1529", {"start": v(-5.07, 11.2) * mm, "mid": v(-5.08, 11.22) * mm, "end": v(-5.09, 11.24) * mm});
            skArc(sketch, "E1530", {"start": v(-5.09, 11.24) * mm, "mid": v(-5.08, 11.28) * mm, "end": v(-5.05, 11.31) * mm});
            skArc(sketch, "E1531", {"start": v(-5.05, 11.31) * mm, "mid": v(-4.8, 11.48) * mm, "end": v(-4.54, 11.64) * mm});
            skArc(sketch, "E1532", {"start": v(-4.54, 11.64) * mm, "mid": v(-4.29, 11.8) * mm, "end": v(-4.03, 11.96) * mm});
            skArc(sketch, "E1533", {"start": v(-4.03, 11.96) * mm, "mid": v(-3.97, 11.99) * mm, "end": v(-3.9, 12) * mm});
            skArc(sketch, "E1534", {"start": v(-3.9, 12) * mm, "mid": v(-3.87, 12) * mm, "end": v(-3.83, 11.98) * mm});
            skArc(sketch, "E1535", {"start": v(-3.83, 11.98) * mm, "mid": v(-3.71, 11.92) * mm, "end": v(-3.59, 11.86) * mm});
            skArc(sketch, "E1536", {"start": v(-3.59, 11.86) * mm, "mid": v(-3.44, 11.78) * mm, "end": v(-3.3, 11.7) * mm});
            skArc(sketch, "E1537", {"start": v(-3.3, 11.7) * mm, "mid": v(-3.13, 11.6) * mm, "end": v(-2.97, 11.52) * mm});
            skArc(sketch, "E1538", {"start": v(-8.01, 10.97) * mm, "mid": v(-7.87, 10.93) * mm, "end": v(-7.73, 10.88) * mm});
            skArc(sketch, "E1539", {"start": v(-7.73, 10.88) * mm, "mid": v(-7.62, 10.83) * mm, "end": v(-7.51, 10.78) * mm});
            skArc(sketch, "E1540", {"start": v(-7.51, 10.78) * mm, "mid": v(-7.43, 10.74) * mm, "end": v(-7.35, 10.7) * mm});
            skArc(sketch, "E1541", {"start": v(-7.35, 10.7) * mm, "mid": v(-7.34, 10.68) * mm, "end": v(-7.35, 10.66) * mm});
            skArc(sketch, "E1542", {"start": v(-7.35, 10.66) * mm, "mid": v(-7.45, 10.57) * mm, "end": v(-7.56, 10.5) * mm});
            skArc(sketch, "E1543", {"start": v(-7.56, 10.5) * mm, "mid": v(-7.85, 10.34) * mm, "end": v(-8.13, 10.19) * mm});
            skArc(sketch, "E1544", {"start": v(-8.13, 10.19) * mm, "mid": v(-8.45, 10.03) * mm, "end": v(-8.78, 9.87) * mm});
            skArc(sketch, "E1545", {"start": v(-8.78, 9.87) * mm, "mid": v(-9.08, 9.73) * mm, "end": v(-9.38, 9.6) * mm});
            skArc(sketch, "E1546", {"start": v(-9.38, 9.6) * mm, "mid": v(-9.71, 9.46) * mm, "end": v(-10.05, 9.33) * mm});
            skArc(sketch, "E1547", {"start": v(-10.05, 9.33) * mm, "mid": v(-10.45, 9.2) * mm, "end": v(-10.85, 9.1) * mm});
            skArc(sketch, "E1548", {"start": v(-10.85, 9.1) * mm, "mid": v(-11.23, 9) * mm, "end": v(-11.6, 8.9) * mm});
            skArc(sketch, "E1549", {"start": v(-11.6, 8.9) * mm, "mid": v(-11.83, 8.87) * mm, "end": v(-12.07, 8.86) * mm});
            skArc(sketch, "E1550", {"start": v(-12.07, 8.86) * mm, "mid": v(-12.14, 8.86) * mm, "end": v(-12.21, 8.87) * mm});
            skArc(sketch, "E1551", {"start": v(-12.21, 8.87) * mm, "mid": v(-12.25, 8.88) * mm, "end": v(-12.28, 8.9) * mm});
            skArc(sketch, "E1552", {"start": v(-12.28, 8.9) * mm, "mid": v(-12.3, 8.94) * mm, "end": v(-12.32, 8.98) * mm});
            skArc(sketch, "E1553", {"start": v(-12.32, 8.98) * mm, "mid": v(-12.33, 9.06) * mm, "end": v(-12.33, 9.14) * mm});
            skArc(sketch, "E1554", {"start": v(-12.33, 9.14) * mm, "mid": v(-12.32, 9.3) * mm, "end": v(-12.29, 9.47) * mm});
            skArc(sketch, "E1555", {"start": v(-12.29, 9.47) * mm, "mid": v(-12.23, 9.64) * mm, "end": v(-12.16, 9.82) * mm});
            skArc(sketch, "E1556", {"start": v(-12.16, 9.82) * mm, "mid": v(-12.07, 10) * mm, "end": v(-11.97, 10.16) * mm});
            skArc(sketch, "E1557", {"start": v(-11.97, 10.16) * mm, "mid": v(-11.86, 10.31) * mm, "end": v(-11.73, 10.46) * mm});
            skArc(sketch, "E1558", {"start": v(-11.73, 10.46) * mm, "mid": v(-11.4, 10.75) * mm, "end": v(-11.02, 10.98) * mm});
            skArc(sketch, "E1559", {"start": v(-11.02, 10.98) * mm, "mid": v(-10.6, 11.14) * mm, "end": v(-10.17, 11.24) * mm});
            skArc(sketch, "E1560", {"start": v(-10.17, 11.24) * mm, "mid": v(-9.66, 11.28) * mm, "end": v(-9.16, 11.24) * mm});
            skArc(sketch, "E1561", {"start": v(-9.16, 11.24) * mm, "mid": v(-8.58, 11.13) * mm, "end": v(-8.01, 10.97) * mm});
            skArc(sketch, "E1562", {"start": v(6.01, 10.67) * mm, "mid": v(6.5, 10.5) * mm, "end": v(7, 10.36) * mm});
            skArc(sketch, "E1563", {"start": v(7, 10.36) * mm, "mid": v(7.42, 10.26) * mm, "end": v(7.84, 10.19) * mm});
            skArc(sketch, "E1564", {"start": v(7.84, 10.19) * mm, "mid": v(8.29, 10.14) * mm, "end": v(8.74, 10.11) * mm});
            skArc(sketch, "E1565", {"start": v(8.74, 10.11) * mm, "mid": v(9.31, 10.1) * mm, "end": v(9.89, 10.12) * mm});
            skArc(sketch, "E1566", {"start": v(9.89, 10.12) * mm, "mid": v(10.25, 10.13) * mm, "end": v(10.62, 10.13) * mm});
            skArc(sketch, "E1567", {"start": v(10.62, 10.13) * mm, "mid": v(10.84, 10.14) * mm, "end": v(11.06, 10.13) * mm});
            skArc(sketch, "E1568", {"start": v(11.06, 10.13) * mm, "mid": v(11.2, 10.12) * mm, "end": v(11.34, 10.1) * mm});
            skArc(sketch, "E1569", {"start": v(11.34, 10.1) * mm, "mid": v(11.37, 10.09) * mm, "end": v(11.39, 10.05) * mm});
            skArc(sketch, "E1570", {"start": v(11.39, 10.05) * mm, "mid": v(11.39, 10.02) * mm, "end": v(11.38, 9.98) * mm});
            skArc(sketch, "E1571", {"start": v(11.38, 9.98) * mm, "mid": v(11.36, 9.9) * mm, "end": v(11.35, 9.83) * mm});
            skArc(sketch, "E1572", {"start": v(11.35, 9.83) * mm, "mid": v(11.33, 9.74) * mm, "end": v(11.3, 9.66) * mm});
            skArc(sketch, "E1573", {"start": v(11.3, 9.66) * mm, "mid": v(11.28, 9.56) * mm, "end": v(11.25, 9.47) * mm});
            skArc(sketch, "E1574", {"start": v(11.25, 9.47) * mm, "mid": v(11.14, 9.2) * mm, "end": v(10.99, 8.94) * mm});
            skArc(sketch, "E1575", {"start": v(10.99, 8.94) * mm, "mid": v(10.78, 8.7) * mm, "end": v(10.54, 8.49) * mm});
            skArc(sketch, "E1576", {"start": v(10.54, 8.49) * mm, "mid": v(10.24, 8.28) * mm, "end": v(9.92, 8.12) * mm});
            skArc(sketch, "E1577", {"start": v(9.92, 8.12) * mm, "mid": v(9.54, 7.96) * mm, "end": v(9.15, 7.84) * mm});
            skArc(sketch, "E1578", {"start": v(9.15, 7.84) * mm, "mid": v(8.56, 7.73) * mm, "end": v(7.96, 7.72) * mm});
            skArc(sketch, "E1579", {"start": v(7.96, 7.72) * mm, "mid": v(7.24, 7.8) * mm, "end": v(6.54, 7.95) * mm});
            skArc(sketch, "E1580", {"start": v(6.54, 7.95) * mm, "mid": v(5.8, 8.18) * mm, "end": v(5.07, 8.47) * mm});
            skArc(sketch, "E1581", {"start": v(5.07, 8.47) * mm, "mid": v(4.36, 8.84) * mm, "end": v(3.69, 9.26) * mm});
            skLineSegment(sketch, "E1582", {"start": v(3.69, 9.26) * mm, "end": v(3.27, 9.55) * mm});
            skLineSegment(sketch, "E1583", {"start": v(3.27, 9.55) * mm, "end": v(3.5, 9.77) * mm});
            skArc(sketch, "E1584", {"start": v(3.5, 9.77) * mm, "mid": v(3.61, 9.87) * mm, "end": v(3.73, 9.97) * mm});
            skArc(sketch, "E1585", {"start": v(3.73, 9.97) * mm, "mid": v(4.05, 10.2) * mm, "end": v(4.37, 10.42) * mm});
            skArc(sketch, "E1586", {"start": v(4.37, 10.42) * mm, "mid": v(4.71, 10.66) * mm, "end": v(5.06, 10.9) * mm});
            skArc(sketch, "E1587", {"start": v(5.06, 10.9) * mm, "mid": v(5.12, 10.93) * mm, "end": v(5.18, 10.95) * mm});
            skArc(sketch, "E1588", {"start": v(5.18, 10.95) * mm, "mid": v(5.2, 10.95) * mm, "end": v(5.2, 10.94) * mm});
            skArc(sketch, "E1589", {"start": v(5.2, 10.94) * mm, "mid": v(5.32, 10.9) * mm, "end": v(5.44, 10.87) * mm});
            skArc(sketch, "E1590", {"start": v(5.44, 10.87) * mm, "mid": v(5.57, 10.82) * mm, "end": v(5.7, 10.78) * mm});
            skArc(sketch, "E1591", {"start": v(5.7, 10.78) * mm, "mid": v(5.86, 10.72) * mm, "end": v(6.01, 10.67) * mm});
            skArc(sketch, "E1592", {"start": v(0.05, 9.66) * mm, "mid": v(0.27, 9.52) * mm, "end": v(0.5, 9.38) * mm});
            skArc(sketch, "E1593", {"start": v(0.5, 9.38) * mm, "mid": v(0.68, 9.25) * mm, "end": v(0.86, 9.13) * mm});
            skArc(sketch, "E1594", {"start": v(0.86, 9.13) * mm, "mid": v(1.02, 9.02) * mm, "end": v(1.17, 8.9) * mm});
            skArc(sketch, "E1595", {"start": v(1.17, 8.9) * mm, "mid": v(1.2, 8.89) * mm, "end": v(1.2, 8.86) * mm});
            skArc(sketch, "E1596", {"start": v(1.2, 8.86) * mm, "mid": v(1.19, 8.82) * mm, "end": v(1.16, 8.78) * mm});
            skArc(sketch, "E1597", {"start": v(1.16, 8.78) * mm, "mid": v(0.86, 8.51) * mm, "end": v(0.55, 8.25) * mm});
            skArc(sketch, "E1598", {"start": v(0.55, 8.25) * mm, "mid": v(0.26, 8) * mm, "end": v(-0.04, 7.75) * mm});
            skArc(sketch, "E1599", {"start": v(-0.04, 7.75) * mm, "mid": v(-0.1, 7.7) * mm, "end": v(-0.17, 7.68) * mm});
            skArc(sketch, "E1600", {"start": v(-0.17, 7.68) * mm, "mid": v(-0.23, 7.68) * mm, "end": v(-0.27, 7.7) * mm});
            skArc(sketch, "E1601", {"start": v(-0.27, 7.7) * mm, "mid": v(-0.85, 8.15) * mm, "end": v(-1.42, 8.6) * mm});
            skArc(sketch, "E1602", {"start": v(-1.42, 8.6) * mm, "mid": v(-2, 9.06) * mm, "end": v(-2.57, 9.51) * mm});
            skArc(sketch, "E1603", {"start": v(-2.57, 9.51) * mm, "mid": v(-2.6, 9.55) * mm, "end": v(-2.61, 9.6) * mm});
            skArc(sketch, "E1604", {"start": v(-2.61, 9.6) * mm, "mid": v(-2.6, 9.67) * mm, "end": v(-2.55, 9.72) * mm});
            skArc(sketch, "E1605", {"start": v(-2.55, 9.72) * mm, "mid": v(-2.25, 9.9) * mm, "end": v(-1.96, 10.08) * mm});
            skArc(sketch, "E1606", {"start": v(-1.96, 10.08) * mm, "mid": v(-1.66, 10.25) * mm, "end": v(-1.36, 10.42) * mm});
            skArc(sketch, "E1607", {"start": v(-1.36, 10.42) * mm, "mid": v(-1.29, 10.44) * mm, "end": v(-1.2, 10.43) * mm});
            skArc(sketch, "E1608", {"start": v(-1.2, 10.43) * mm, "mid": v(-1.17, 10.41) * mm, "end": v(-1.13, 10.4) * mm});
            skArc(sketch, "E1609", {"start": v(-1.13, 10.4) * mm, "mid": v(-0.96, 10.29) * mm, "end": v(-0.79, 10.19) * mm});
            skArc(sketch, "E1610", {"start": v(-0.79, 10.19) * mm, "mid": v(-0.6, 10.06) * mm, "end": v(-0.4, 9.94) * mm});
            skArc(sketch, "E1611", {"start": v(-0.4, 9.94) * mm, "mid": v(-0.17, 9.8) * mm, "end": v(0.05, 9.66) * mm});
            skArc(sketch, "E1612", {"start": v(-5.7, 9.78) * mm, "mid": v(-5.54, 9.69) * mm, "end": v(-5.4, 9.59) * mm});
            skArc(sketch, "E1613", {"start": v(-5.4, 9.59) * mm, "mid": v(-5.26, 9.5) * mm, "end": v(-5.13, 9.42) * mm});
            skArc(sketch, "E1614", {"start": v(-5.13, 9.42) * mm, "mid": v(-5.03, 9.34) * mm, "end": v(-4.92, 9.26) * mm});
            skArc(sketch, "E1615", {"start": v(-4.92, 9.26) * mm, "mid": v(-4.9, 9.25) * mm, "end": v(-4.9, 9.23) * mm});
            skArc(sketch, "E1616", {"start": v(-4.9, 9.23) * mm, "mid": v(-4.92, 9.15) * mm, "end": v(-4.98, 9.1) * mm});
            skArc(sketch, "E1617", {"start": v(-4.98, 9.1) * mm, "mid": v(-5.6, 8.82) * mm, "end": v(-6.24, 8.54) * mm});
            skArc(sketch, "E1618", {"start": v(-6.24, 8.54) * mm, "mid": v(-6.82, 8.28) * mm, "end": v(-7.4, 8.04) * mm});
            skArc(sketch, "E1619", {"start": v(-7.4, 8.04) * mm, "mid": v(-7.74, 7.9) * mm, "end": v(-8.1, 7.8) * mm});
            skArc(sketch, "E1620", {"start": v(-8.1, 7.8) * mm, "mid": v(-8.63, 7.68) * mm, "end": v(-9.17, 7.6) * mm});
            skArc(sketch, "E1621", {"start": v(-9.17, 7.6) * mm, "mid": v(-9.67, 7.55) * mm, "end": v(-10.16, 7.55) * mm});
            skArc(sketch, "E1622", {"start": v(-10.16, 7.55) * mm, "mid": v(-10.6, 7.58) * mm, "end": v(-11.01, 7.66) * mm});
            skArc(sketch, "E1623", {"start": v(-11.01, 7.66) * mm, "mid": v(-11.35, 7.76) * mm, "end": v(-11.66, 7.92) * mm});
            skLineSegment(sketch, "E1624", {"start": v(-11.66, 7.92) * mm, "end": v(-12, 8.13) * mm});
            skLineSegment(sketch, "E1625", {"start": v(-12, 8.13) * mm, "end": v(-11.19, 8.3) * mm});
            skArc(sketch, "E1626", {"start": v(-11.19, 8.3) * mm, "mid": v(-11.01, 8.33) * mm, "end": v(-10.84, 8.37) * mm});
            skArc(sketch, "E1627", {"start": v(-10.84, 8.37) * mm, "mid": v(-10.66, 8.41) * mm, "end": v(-10.47, 8.46) * mm});
            skArc(sketch, "E1628", {"start": v(-10.47, 8.46) * mm, "mid": v(-10.3, 8.5) * mm, "end": v(-10.14, 8.55) * mm});
            skArc(sketch, "E1629", {"start": v(-10.14, 8.55) * mm, "mid": v(-10.02, 8.58) * mm, "end": v(-9.9, 8.62) * mm});
            skArc(sketch, "E1630", {"start": v(-9.9, 8.62) * mm, "mid": v(-9.63, 8.72) * mm, "end": v(-9.36, 8.83) * mm});
            skArc(sketch, "E1631", {"start": v(-9.36, 8.83) * mm, "mid": v(-8.95, 9.03) * mm, "end": v(-8.55, 9.22) * mm});
            skArc(sketch, "E1632", {"start": v(-8.55, 9.22) * mm, "mid": v(-8.13, 9.43) * mm, "end": v(-7.72, 9.64) * mm});
            skArc(sketch, "E1633", {"start": v(-7.72, 9.64) * mm, "mid": v(-7.43, 9.8) * mm, "end": v(-7.13, 9.99) * mm});
            skArc(sketch, "E1634", {"start": v(-7.13, 9.99) * mm, "mid": v(-7.04, 10.04) * mm, "end": v(-6.95, 10.1) * mm});
            skArc(sketch, "E1635", {"start": v(-6.95, 10.1) * mm, "mid": v(-6.86, 10.15) * mm, "end": v(-6.78, 10.2) * mm});
            skArc(sketch, "E1636", {"start": v(-6.78, 10.2) * mm, "mid": v(-6.7, 10.23) * mm, "end": v(-6.63, 10.27) * mm});
            skArc(sketch, "E1637", {"start": v(-6.63, 10.27) * mm, "mid": v(-6.6, 10.28) * mm, "end": v(-6.58, 10.28) * mm});
            skArc(sketch, "E1638", {"start": v(-6.58, 10.28) * mm, "mid": v(-6.55, 10.28) * mm, "end": v(-6.52, 10.27) * mm});
            skArc(sketch, "E1639", {"start": v(-6.52, 10.27) * mm, "mid": v(-6.4, 10.2) * mm, "end": v(-6.28, 10.14) * mm});
            skArc(sketch, "E1640", {"start": v(-6.28, 10.14) * mm, "mid": v(-6.15, 10.06) * mm, "end": v(-6, 9.98) * mm});
            skArc(sketch, "E1641", {"start": v(-6, 9.98) * mm, "mid": v(-5.85, 9.88) * mm, "end": v(-5.7, 9.78) * mm});
            skLineSegment(sketch, "E1642", {"start": v(0, 44.45) * mm, "end": v(0, -44.45) * mm, "construction": true});
            skSolve(sketch);
        }
        {
            var Q0;
            Q0 = qSketchRegion(id + "F8", true);
            extrude(context, id + "F9", {"entities" : qUnion([Q0]), "operationType" : NewBodyOperationType.ADD, "depth" : 1.59 * mm, "offsetDistance" : 25.4 * mm});
        }
        {
            var Q0;
            {var subQ350=makeQuery(id+"F3.opExtrude","SWEPT_FACE",FACE,{"disambiguationData":[OSD([sQuery(id+"F2.wireOp",EDGE,"E5.bottom")])]});Q0=makeQuery(id+"F9.boolean.opBoolean","SPLIT",FACE,{"disambiguationData":[TD([subQ350])],"derivedFrom":makeQuery(id+"F7.boolean.opBoolean","SPLIT",FACE,{"disambiguationData":[TD([subQ350])],"derivedFrom":makeQuery(id+"F5.boolean.opBoolean","SPLIT",FACE,{"disambiguationData":[TD([subQ350])],"derivedFrom":makeQuery(id+"F1.opExtrude","CAP_FACE",FACE,{"disambiguationData":[OSD([sQuery(id+"F0.wireOp",EDGE,"E0.bottom"),sQuery(id+"F0.wireOp",EDGE,"E0.top"),sQuery(id+"F0.wireOp",EDGE,"E0.left"),sQuery(id+"F0.wireOp",EDGE,"E0.right"),sQuery(id+"F0.wireOp",EDGE,"E1.filletArc"),sQuery(id+"F0.wireOp",EDGE,"E2.filletArc"),sQuery(id+"F0.wireOp",EDGE,"E3.filletArc"),sQuery(id+"F0.wireOp",EDGE,"E4.filletArc")])],"isStart":false})})})});}
            var sketch = newSketch(context, id + "F10", { "sketchPlane" : qUnion([Q0])});
            skText(sketch, "E1643", { "text": "little free library", "fontName": "RobotoSlab-Regular.ttf"});
            const initialGuessF10  = {"E1643": [-0.06668, -0.006, 1, 0, 0.01234]};
            skSetInitialGuess(sketch, initialGuessF10);
            skSolve(sketch);
        }
        {
            var Q0;
            Q0 = qSketchRegion(id + "F10", true);
            extrude(context, id + "F11", {"entities" : qUnion([Q0]), "operationType" : NewBodyOperationType.ADD, "depth" : 1.59 * mm, "offsetDistance" : 25.4 * mm});
        }
        {
            var Q0;
            {var subQ400=makeQuery(id+"F3.opExtrude","SWEPT_FACE",FACE,{"disambiguationData":[OSD([sQuery(id+"F2.wireOp",EDGE,"E5.bottom")])]});Q0=makeQuery(id+"F11.boolean.opBoolean","SPLIT",FACE,{"disambiguationData":[TD([subQ400])],"derivedFrom":makeQuery(id+"F9.boolean.opBoolean","SPLIT",FACE,{"disambiguationData":[TD([subQ400])],"derivedFrom":makeQuery(id+"F7.boolean.opBoolean","SPLIT",FACE,{"disambiguationData":[TD([subQ400])],"derivedFrom":makeQuery(id+"F5.boolean.opBoolean","SPLIT",FACE,{"disambiguationData":[TD([subQ400])],"derivedFrom":makeQuery(id+"F1.opExtrude","CAP_FACE",FACE,{"disambiguationData":[OSD([sQuery(id+"F0.wireOp",EDGE,"E0.bottom"),sQuery(id+"F0.wireOp",EDGE,"E0.top"),sQuery(id+"F0.wireOp",EDGE,"E0.left"),sQuery(id+"F0.wireOp",EDGE,"E0.right"),sQuery(id+"F0.wireOp",EDGE,"E1.filletArc"),sQuery(id+"F0.wireOp",EDGE,"E2.filletArc"),sQuery(id+"F0.wireOp",EDGE,"E3.filletArc"),sQuery(id+"F0.wireOp",EDGE,"E4.filletArc")])],"isStart":false})})})})});}
            var sketch = newSketch(context, id + "F12", { "sketchPlane" : qUnion([Q0])});
            skArc(sketch, "E1644", {"start": v(-0.98, -8.87) * mm, "mid": v(-1.11, -9.05) * mm, "end": v(-1.25, -9.22) * mm});
            skArc(sketch, "E1645", {"start": v(-1.25, -9.22) * mm, "mid": v(-1.42, -9.43) * mm, "end": v(-1.6, -9.63) * mm});
            skArc(sketch, "E1646", {"start": v(-1.6, -9.63) * mm, "mid": v(-1.76, -9.83) * mm, "end": v(-1.93, -10.03) * mm});
            skArc(sketch, "E1647", {"start": v(-1.93, -10.03) * mm, "mid": v(-2.08, -10.19) * mm, "end": v(-2.23, -10.34) * mm});
            skLineSegment(sketch, "E1648", {"start": v(-2.23, -10.34) * mm, "end": v(-2.89, -11.02) * mm});
            skLineSegment(sketch, "E1649", {"start": v(-2.89, -11.02) * mm, "end": v(-4.14, -10.4) * mm});
            skArc(sketch, "E1650", {"start": v(-4.14, -10.4) * mm, "mid": v(-4.9, -10.03) * mm, "end": v(-5.65, -9.7) * mm});
            skArc(sketch, "E1651", {"start": v(-5.65, -9.7) * mm, "mid": v(-6.27, -9.46) * mm, "end": v(-6.9, -9.25) * mm});
            skArc(sketch, "E1652", {"start": v(-6.9, -9.25) * mm, "mid": v(-7.48, -9.1) * mm, "end": v(-8.06, -8.99) * mm});
            skArc(sketch, "E1653", {"start": v(-8.06, -8.99) * mm, "mid": v(-8.7, -8.9) * mm, "end": v(-9.33, -8.86) * mm});
            skArc(sketch, "E1654", {"start": v(-9.33, -8.86) * mm, "mid": v(-9.77, -8.85) * mm, "end": v(-10.2, -8.86) * mm});
            skArc(sketch, "E1655", {"start": v(-10.2, -8.86) * mm, "mid": v(-10.58, -8.89) * mm, "end": v(-10.96, -8.94) * mm});
            skArc(sketch, "E1656", {"start": v(-10.96, -8.94) * mm, "mid": v(-11.3, -9.01) * mm, "end": v(-11.64, -9.11) * mm});
            skArc(sketch, "E1657", {"start": v(-11.64, -9.11) * mm, "mid": v(-11.97, -9.23) * mm, "end": v(-12.3, -9.37) * mm});
            skArc(sketch, "E1658", {"start": v(-12.3, -9.37) * mm, "mid": v(-12.69, -9.6) * mm, "end": v(-13.06, -9.86) * mm});
            skArc(sketch, "E1659", {"start": v(-13.06, -9.86) * mm, "mid": v(-13.39, -10.15) * mm, "end": v(-13.68, -10.48) * mm});
            skArc(sketch, "E1660", {"start": v(-13.68, -10.48) * mm, "mid": v(-13.9, -10.81) * mm, "end": v(-14.1, -11.18) * mm});
            skArc(sketch, "E1661", {"start": v(-14.1, -11.18) * mm, "mid": v(-14.2, -11.52) * mm, "end": v(-14.25, -11.87) * mm});
            skArc(sketch, "E1662", {"start": v(-14.25, -11.87) * mm, "mid": v(-14.26, -11.99) * mm, "end": v(-14.27, -12.1) * mm});
            skArc(sketch, "E1663", {"start": v(-14.27, -12.1) * mm, "mid": v(-14.29, -12.17) * mm, "end": v(-14.32, -12.24) * mm});
            skArc(sketch, "E1664", {"start": v(-14.32, -12.24) * mm, "mid": v(-14.35, -12.3) * mm, "end": v(-14.4, -12.34) * mm});
            skArc(sketch, "E1665", {"start": v(-14.4, -12.34) * mm, "mid": v(-14.48, -12.4) * mm, "end": v(-14.55, -12.44) * mm});
            skArc(sketch, "E1666", {"start": v(-14.55, -12.44) * mm, "mid": v(-14.76, -12.57) * mm, "end": v(-14.96, -12.7) * mm});
            skArc(sketch, "E1667", {"start": v(-14.96, -12.7) * mm, "mid": v(-15.27, -12.93) * mm, "end": v(-15.57, -13.17) * mm});
            skArc(sketch, "E1668", {"start": v(-15.57, -13.17) * mm, "mid": v(-15.86, -13.42) * mm, "end": v(-16.16, -13.67) * mm});
            skArc(sketch, "E1669", {"start": v(-16.16, -13.67) * mm, "mid": v(-16.34, -13.84) * mm, "end": v(-16.51, -14.03) * mm});
            skArc(sketch, "E1670", {"start": v(-16.51, -14.03) * mm, "mid": v(-16.86, -14.5) * mm, "end": v(-17.12, -15) * mm});
            skArc(sketch, "E1671", {"start": v(-17.12, -15) * mm, "mid": v(-17.28, -15.53) * mm, "end": v(-17.34, -16.07) * mm});
            skArc(sketch, "E1672", {"start": v(-17.34, -16.07) * mm, "mid": v(-17.3, -16.61) * mm, "end": v(-17.15, -17.13) * mm});
            skArc(sketch, "E1673", {"start": v(-17.15, -17.13) * mm, "mid": v(-16.9, -17.62) * mm, "end": v(-16.56, -18.07) * mm});
            skArc(sketch, "E1674", {"start": v(-16.56, -18.07) * mm, "mid": v(-16.3, -18.34) * mm, "end": v(-16, -18.59) * mm});
            skArc(sketch, "E1675", {"start": v(-16, -18.59) * mm, "mid": v(-15.69, -18.8) * mm, "end": v(-15.35, -19) * mm});
            skArc(sketch, "E1676", {"start": v(-15.35, -19) * mm, "mid": v(-15, -19.16) * mm, "end": v(-14.63, -19.3) * mm});
            skArc(sketch, "E1677", {"start": v(-14.63, -19.3) * mm, "mid": v(-14.25, -19.4) * mm, "end": v(-13.85, -19.46) * mm});
            skArc(sketch, "E1678", {"start": v(-13.85, -19.46) * mm, "mid": v(-13.73, -19.48) * mm, "end": v(-13.6, -19.5) * mm});
            skArc(sketch, "E1679", {"start": v(-13.6, -19.5) * mm, "mid": v(-13.53, -19.53) * mm, "end": v(-13.46, -19.56) * mm});
            skArc(sketch, "E1680", {"start": v(-13.46, -19.56) * mm, "mid": v(-13.4, -19.6) * mm, "end": v(-13.36, -19.65) * mm});
            skArc(sketch, "E1681", {"start": v(-13.36, -19.65) * mm, "mid": v(-13.32, -19.71) * mm, "end": v(-13.29, -19.78) * mm});
            skArc(sketch, "E1682", {"start": v(-13.29, -19.78) * mm, "mid": v(-13.21, -19.94) * mm, "end": v(-13.11, -20.07) * mm});
            skArc(sketch, "E1683", {"start": v(-13.11, -20.07) * mm, "mid": v(-12.98, -20.23) * mm, "end": v(-12.84, -20.37) * mm});
            skArc(sketch, "E1684", {"start": v(-12.84, -20.37) * mm, "mid": v(-12.67, -20.5) * mm, "end": v(-12.48, -20.64) * mm});
            skArc(sketch, "E1685", {"start": v(-12.48, -20.64) * mm, "mid": v(-12.3, -20.75) * mm, "end": v(-12.1, -20.85) * mm});
            skArc(sketch, "E1686", {"start": v(-12.1, -20.85) * mm, "mid": v(-11.95, -20.91) * mm, "end": v(-11.8, -20.96) * mm});
            skArc(sketch, "E1687", {"start": v(-11.8, -20.96) * mm, "mid": v(-11.66, -21) * mm, "end": v(-11.52, -21.03) * mm});
            skArc(sketch, "E1688", {"start": v(-11.52, -21.03) * mm, "mid": v(-11.35, -21.04) * mm, "end": v(-11.17, -21.05) * mm});
            skArc(sketch, "E1689", {"start": v(-11.17, -21.05) * mm, "mid": v(-10.9, -21.06) * mm, "end": v(-10.62, -21.06) * mm});
            skArc(sketch, "E1690", {"start": v(-10.62, -21.06) * mm, "mid": v(-10, -21.03) * mm, "end": v(-9.39, -20.96) * mm});
            skArc(sketch, "E1691", {"start": v(-9.39, -20.96) * mm, "mid": v(-8.77, -20.85) * mm, "end": v(-8.17, -20.69) * mm});
            skArc(sketch, "E1692", {"start": v(-8.17, -20.69) * mm, "mid": v(-7.53, -20.47) * mm, "end": v(-6.9, -20.22) * mm});
            skArc(sketch, "E1693", {"start": v(-6.9, -20.22) * mm, "mid": v(-6.22, -19.9) * mm, "end": v(-5.55, -19.54) * mm});
            skLineSegment(sketch, "E1694", {"start": v(-5.55, -19.54) * mm, "end": v(-4.62, -19.01) * mm});
            skLineSegment(sketch, "E1695", {"start": v(-4.62, -19.01) * mm, "end": v(-4.3, -19.23) * mm});
            skArc(sketch, "E1696", {"start": v(-4.3, -19.23) * mm, "mid": v(-4.2, -19.3) * mm, "end": v(-4.11, -19.38) * mm});
            skArc(sketch, "E1697", {"start": v(-4.11, -19.38) * mm, "mid": v(-3.87, -19.57) * mm, "end": v(-3.62, -19.77) * mm});
            skArc(sketch, "E1698", {"start": v(-3.62, -19.77) * mm, "mid": v(-3.33, -20) * mm, "end": v(-3.04, -20.24) * mm});
            skArc(sketch, "E1699", {"start": v(-3.04, -20.24) * mm, "mid": v(-2.72, -20.5) * mm, "end": v(-2.4, -20.76) * mm});
            skLineSegment(sketch, "E1700", {"start": v(-2.4, -20.76) * mm, "end": v(-0.81, -22.06) * mm});
            skLineSegment(sketch, "E1701", {"start": v(-0.81, -22.06) * mm, "end": v(-0.25, -21.28) * mm});
            skArc(sketch, "E1702", {"start": v(-0.25, -21.28) * mm, "mid": v(-0.12, -21.1) * mm, "end": v(0, -20.94) * mm});
            skArc(sketch, "E1703", {"start": v(0, -20.94) * mm, "mid": v(0.16, -20.74) * mm, "end": v(0.32, -20.55) * mm});
            skArc(sketch, "E1704", {"start": v(0.32, -20.55) * mm, "mid": v(0.47, -20.36) * mm, "end": v(0.63, -20.17) * mm});
            skArc(sketch, "E1705", {"start": v(0.63, -20.17) * mm, "mid": v(0.76, -20.03) * mm, "end": v(0.89, -19.88) * mm});
            skLineSegment(sketch, "E1706", {"start": v(0.89, -19.88) * mm, "end": v(1.46, -19.26) * mm});
            skLineSegment(sketch, "E1707", {"start": v(1.46, -19.26) * mm, "end": v(1.92, -19.53) * mm});
            skArc(sketch, "E1708", {"start": v(1.92, -19.53) * mm, "mid": v(2.3, -19.75) * mm, "end": v(2.7, -19.95) * mm});
            skArc(sketch, "E1709", {"start": v(2.7, -19.95) * mm, "mid": v(3.1, -20.15) * mm, "end": v(3.52, -20.34) * mm});
            skArc(sketch, "E1710", {"start": v(3.52, -20.34) * mm, "mid": v(3.9, -20.5) * mm, "end": v(4.3, -20.65) * mm});
            skArc(sketch, "E1711", {"start": v(4.3, -20.65) * mm, "mid": v(4.63, -20.76) * mm, "end": v(4.96, -20.85) * mm});
            skArc(sketch, "E1712", {"start": v(4.96, -20.85) * mm, "mid": v(5.21, -20.9) * mm, "end": v(5.46, -20.96) * mm});
            skArc(sketch, "E1713", {"start": v(5.46, -20.96) * mm, "mid": v(5.7, -21) * mm, "end": v(5.92, -21.02) * mm});
            skArc(sketch, "E1714", {"start": v(5.92, -21.02) * mm, "mid": v(6.2, -21.04) * mm, "end": v(6.47, -21.06) * mm});
            skArc(sketch, "E1715", {"start": v(6.47, -21.06) * mm, "mid": v(6.85, -21.06) * mm, "end": v(7.24, -21.07) * mm});
            skArc(sketch, "E1716", {"start": v(7.24, -21.07) * mm, "mid": v(7.67, -21.06) * mm, "end": v(8.1, -21.06) * mm});
            skArc(sketch, "E1717", {"start": v(8.1, -21.06) * mm, "mid": v(8.33, -21.05) * mm, "end": v(8.56, -21.03) * mm});
            skArc(sketch, "E1718", {"start": v(8.56, -21.03) * mm, "mid": v(8.76, -21) * mm, "end": v(8.94, -20.95) * mm});
            skArc(sketch, "E1719", {"start": v(8.94, -20.95) * mm, "mid": v(9.18, -20.88) * mm, "end": v(9.42, -20.8) * mm});
            skArc(sketch, "E1720", {"start": v(9.42, -20.8) * mm, "mid": v(9.95, -20.59) * mm, "end": v(10.46, -20.31) * mm});
            skArc(sketch, "E1721", {"start": v(10.46, -20.31) * mm, "mid": v(10.87, -20.02) * mm, "end": v(11.22, -19.66) * mm});
            skArc(sketch, "E1722", {"start": v(11.22, -19.66) * mm, "mid": v(11.5, -19.28) * mm, "end": v(11.71, -18.85) * mm});
            skArc(sketch, "E1723", {"start": v(11.71, -18.85) * mm, "mid": v(11.86, -18.36) * mm, "end": v(11.94, -17.85) * mm});
            skLineSegment(sketch, "E1724", {"start": v(11.94, -17.85) * mm, "end": v(12, -17.2) * mm});
            skLineSegment(sketch, "E1725", {"start": v(12, -17.2) * mm, "end": v(12.53, -17) * mm});
            skArc(sketch, "E1726", {"start": v(12.53, -17) * mm, "mid": v(13.05, -16.77) * mm, "end": v(13.55, -16.5) * mm});
            skArc(sketch, "E1727", {"start": v(13.55, -16.5) * mm, "mid": v(13.95, -16.2) * mm, "end": v(14.3, -15.85) * mm});
            skArc(sketch, "E1728", {"start": v(14.3, -15.85) * mm, "mid": v(14.56, -15.49) * mm, "end": v(14.75, -15.09) * mm});
            skArc(sketch, "E1729", {"start": v(14.75, -15.09) * mm, "mid": v(14.87, -14.66) * mm, "end": v(14.9, -14.21) * mm});
            skArc(sketch, "E1730", {"start": v(14.9, -14.21) * mm, "mid": v(14.9, -13.95) * mm, "end": v(14.84, -13.7) * mm});
            skArc(sketch, "E1731", {"start": v(14.84, -13.7) * mm, "mid": v(14.76, -13.44) * mm, "end": v(14.65, -13.2) * mm});
            skArc(sketch, "E1732", {"start": v(14.65, -13.2) * mm, "mid": v(14.5, -12.95) * mm, "end": v(14.33, -12.71) * mm});
            skArc(sketch, "E1733", {"start": v(14.33, -12.71) * mm, "mid": v(14.1, -12.46) * mm, "end": v(13.86, -12.23) * mm});
            skArc(sketch, "E1734", {"start": v(13.86, -12.23) * mm, "mid": v(13.66, -12.06) * mm, "end": v(13.45, -11.91) * mm});
            skArc(sketch, "E1735", {"start": v(13.45, -11.91) * mm, "mid": v(13.17, -11.74) * mm, "end": v(12.9, -11.57) * mm});
            skArc(sketch, "E1736", {"start": v(12.9, -11.57) * mm, "mid": v(12.62, -11.42) * mm, "end": v(12.34, -11.28) * mm});
            skArc(sketch, "E1737", {"start": v(12.34, -11.28) * mm, "mid": v(12.2, -11.23) * mm, "end": v(12.06, -11.21) * mm});
            skArc(sketch, "E1738", {"start": v(12.06, -11.21) * mm, "mid": v(12.04, -11.2) * mm, "end": v(12.02, -11.2) * mm});
            skArc(sketch, "E1739", {"start": v(12.02, -11.2) * mm, "mid": v(12, -11.17) * mm, "end": v(11.99, -11.14) * mm});
            skArc(sketch, "E1740", {"start": v(11.99, -11.14) * mm, "mid": v(11.97, -11.1) * mm, "end": v(11.96, -11.05) * mm});
            skArc(sketch, "E1741", {"start": v(11.96, -11.05) * mm, "mid": v(11.96, -11) * mm, "end": v(11.95, -10.95) * mm});
            skArc(sketch, "E1742", {"start": v(11.95, -10.95) * mm, "mid": v(11.94, -10.77) * mm, "end": v(11.9, -10.6) * mm});
            skArc(sketch, "E1743", {"start": v(11.9, -10.6) * mm, "mid": v(11.8, -10.37) * mm, "end": v(11.69, -10.15) * mm});
            skArc(sketch, "E1744", {"start": v(11.69, -10.15) * mm, "mid": v(11.56, -9.92) * mm, "end": v(11.4, -9.7) * mm});
            skArc(sketch, "E1745", {"start": v(11.4, -9.7) * mm, "mid": v(11.25, -9.52) * mm, "end": v(11.08, -9.35) * mm});
            skArc(sketch, "E1746", {"start": v(11.08, -9.35) * mm, "mid": v(10.72, -9.04) * mm, "end": v(10.32, -8.77) * mm});
            skArc(sketch, "E1747", {"start": v(10.32, -8.76) * mm, "mid": v(9.94, -8.56) * mm, "end": v(9.53, -8.4) * mm});
            skArc(sketch, "E1748", {"start": v(9.53, -8.4) * mm, "mid": v(9.08, -8.27) * mm, "end": v(8.6, -8.2) * mm});
            skArc(sketch, "E1749", {"start": v(8.6, -8.2) * mm, "mid": v(8.02, -8.15) * mm, "end": v(7.43, -8.14) * mm});
            skArc(sketch, "E1750", {"start": v(7.43, -8.14) * mm, "mid": v(6.79, -8.16) * mm, "end": v(6.15, -8.23) * mm});
            skArc(sketch, "E1751", {"start": v(6.15, -8.23) * mm, "mid": v(5.6, -8.33) * mm, "end": v(5.05, -8.49) * mm});
            skArc(sketch, "E1752", {"start": v(5.05, -8.49) * mm, "mid": v(4.49, -8.7) * mm, "end": v(3.95, -8.97) * mm});
            skArc(sketch, "E1753", {"start": v(3.95, -8.97) * mm, "mid": v(3.28, -9.35) * mm, "end": v(2.63, -9.76) * mm});
            skArc(sketch, "E1754", {"start": v(2.63, -9.76) * mm, "mid": v(2.46, -9.87) * mm, "end": v(2.28, -9.99) * mm});
            skArc(sketch, "E1755", {"start": v(2.28, -9.99) * mm, "mid": v(2.13, -10.09) * mm, "end": v(1.97, -10.18) * mm});
            skArc(sketch, "E1756", {"start": v(1.97, -10.18) * mm, "mid": v(1.84, -10.26) * mm, "end": v(1.7, -10.34) * mm});
            skArc(sketch, "E1757", {"start": v(1.7, -10.34) * mm, "mid": v(1.68, -10.35) * mm, "end": v(1.65, -10.36) * mm});
            skArc(sketch, "E1758", {"start": v(1.65, -10.36) * mm, "mid": v(1.63, -10.35) * mm, "end": v(1.6, -10.34) * mm});
            skArc(sketch, "E1759", {"start": v(1.6, -10.34) * mm, "mid": v(1.46, -10.18) * mm, "end": v(1.33, -10.02) * mm});
            skArc(sketch, "E1760", {"start": v(1.33, -10.02) * mm, "mid": v(1.17, -9.84) * mm, "end": v(1.01, -9.65) * mm});
            skArc(sketch, "E1761", {"start": v(1.01, -9.65) * mm, "mid": v(0.83, -9.43) * mm, "end": v(0.65, -9.21) * mm});
            skArc(sketch, "E1762", {"start": v(0.65, -9.21) * mm, "mid": v(0.47, -9) * mm, "end": v(0.29, -8.78) * mm});
            skArc(sketch, "E1763", {"start": v(0.29, -8.78) * mm, "mid": v(0.13, -8.6) * mm, "end": v(-0.02, -8.4) * mm});
            skArc(sketch, "E1764", {"start": v(-0.02, -8.4) * mm, "mid": v(-0.16, -8.25) * mm, "end": v(-0.3, -8.09) * mm});
            skArc(sketch, "E1765", {"start": v(-0.3, -8.09) * mm, "mid": v(-0.31, -8.07) * mm, "end": v(-0.33, -8.07) * mm});
            skArc(sketch, "E1766", {"start": v(-0.33, -8.07) * mm, "mid": v(-0.35, -8.07) * mm, "end": v(-0.37, -8.09) * mm});
            skArc(sketch, "E1767", {"start": v(-0.37, -8.09) * mm, "mid": v(-0.46, -8.2) * mm, "end": v(-0.55, -8.3) * mm});
            skArc(sketch, "E1768", {"start": v(-0.55, -8.3) * mm, "mid": v(-0.65, -8.43) * mm, "end": v(-0.75, -8.56) * mm});
            skArc(sketch, "E1769", {"start": v(-0.75, -8.56) * mm, "mid": v(-0.86, -8.72) * mm, "end": v(-0.98, -8.87) * mm});
            skArc(sketch, "E1770", {"start": v(8.8, -9.17) * mm, "mid": v(9.02, -9.23) * mm, "end": v(9.25, -9.3) * mm});
            skArc(sketch, "E1771", {"start": v(9.25, -9.3) * mm, "mid": v(9.48, -9.38) * mm, "end": v(9.7, -9.47) * mm});
            skArc(sketch, "E1772", {"start": v(9.7, -9.47) * mm, "mid": v(9.9, -9.57) * mm, "end": v(10.1, -9.68) * mm});
            skArc(sketch, "E1773", {"start": v(10.1, -9.68) * mm, "mid": v(10.27, -9.78) * mm, "end": v(10.43, -9.9) * mm});
            skArc(sketch, "E1774", {"start": v(10.43, -9.9) * mm, "mid": v(10.53, -9.98) * mm, "end": v(10.61, -10.08) * mm});
            skArc(sketch, "E1775", {"start": v(10.61, -10.08) * mm, "mid": v(10.73, -10.23) * mm, "end": v(10.85, -10.38) * mm});
            skArc(sketch, "E1776", {"start": v(10.85, -10.38) * mm, "mid": v(10.95, -10.54) * mm, "end": v(11.06, -10.7) * mm});
            skArc(sketch, "E1777", {"start": v(11.06, -10.7) * mm, "mid": v(11.09, -10.76) * mm, "end": v(11.1, -10.84) * mm});
            skArc(sketch, "E1778", {"start": v(11.1, -10.84) * mm, "mid": v(11.1, -10.86) * mm, "end": v(11.08, -10.86) * mm});
            skArc(sketch, "E1779", {"start": v(11.08, -10.86) * mm, "mid": v(10.94, -10.87) * mm, "end": v(10.8, -10.87) * mm});
            skArc(sketch, "E1780", {"start": v(10.8, -10.87) * mm, "mid": v(10.65, -10.87) * mm, "end": v(10.49, -10.87) * mm});
            skArc(sketch, "E1781", {"start": v(10.49, -10.87) * mm, "mid": v(10.3, -10.86) * mm, "end": v(10.1, -10.85) * mm});
            skArc(sketch, "E1782", {"start": v(10.1, -10.85) * mm, "mid": v(9.86, -10.84) * mm, "end": v(9.6, -10.84) * mm});
            skArc(sketch, "E1783", {"start": v(9.6, -10.84) * mm, "mid": v(9.39, -10.84) * mm, "end": v(9.18, -10.86) * mm});
            skArc(sketch, "E1784", {"start": v(9.18, -10.86) * mm, "mid": v(8.98, -10.87) * mm, "end": v(8.78, -10.9) * mm});
            skArc(sketch, "E1785", {"start": v(8.78, -10.9) * mm, "mid": v(8.58, -10.93) * mm, "end": v(8.38, -10.97) * mm});
            skArc(sketch, "E1786", {"start": v(8.38, -10.97) * mm, "mid": v(8.04, -11.06) * mm, "end": v(7.71, -11.16) * mm});
            skArc(sketch, "E1787", {"start": v(7.71, -11.16) * mm, "mid": v(7.26, -11.31) * mm, "end": v(6.8, -11.48) * mm});
            skArc(sketch, "E1788", {"start": v(6.8, -11.48) * mm, "mid": v(6.34, -11.66) * mm, "end": v(5.88, -11.85) * mm});
            skArc(sketch, "E1789", {"start": v(5.88, -11.85) * mm, "mid": v(5.5, -12.02) * mm, "end": v(5.13, -12.2) * mm});
            skLineSegment(sketch, "E1790", {"start": v(5.13, -12.2) * mm, "end": v(4.65, -12.44) * mm});
            skLineSegment(sketch, "E1791", {"start": v(4.65, -12.44) * mm, "end": v(4.09, -12.16) * mm});
            skArc(sketch, "E1792", {"start": v(4.09, -12.16) * mm, "mid": v(3.83, -12.02) * mm, "end": v(3.59, -11.88) * mm});
            skArc(sketch, "E1793", {"start": v(3.59, -11.88) * mm, "mid": v(3.29, -11.7) * mm, "end": v(2.99, -11.5) * mm});
            skArc(sketch, "E1794", {"start": v(2.99, -11.5) * mm, "mid": v(2.68, -11.3) * mm, "end": v(2.38, -11.1) * mm});
            skArc(sketch, "E1795", {"start": v(2.38, -11.1) * mm, "mid": v(2.35, -11.07) * mm, "end": v(2.34, -11.02) * mm});
            skArc(sketch, "E1796", {"start": v(2.34, -11.02) * mm, "mid": v(2.35, -10.97) * mm, "end": v(2.39, -10.94) * mm});
            skArc(sketch, "E1797", {"start": v(2.39, -10.94) * mm, "mid": v(2.82, -10.69) * mm, "end": v(3.25, -10.44) * mm});
            skArc(sketch, "E1798", {"start": v(3.25, -10.44) * mm, "mid": v(3.66, -10.2) * mm, "end": v(4.07, -9.97) * mm});
            skArc(sketch, "E1799", {"start": v(4.07, -9.97) * mm, "mid": v(4.4, -9.8) * mm, "end": v(4.72, -9.64) * mm});
            skArc(sketch, "E1800", {"start": v(4.72, -9.64) * mm, "mid": v(5.2, -9.44) * mm, "end": v(5.7, -9.28) * mm});
            skArc(sketch, "E1801", {"start": v(5.7, -9.28) * mm, "mid": v(6.23, -9.15) * mm, "end": v(6.76, -9.07) * mm});
            skArc(sketch, "E1802", {"start": v(6.76, -9.07) * mm, "mid": v(7.28, -9.03) * mm, "end": v(7.8, -9.03) * mm});
            skArc(sketch, "E1803", {"start": v(7.8, -9.03) * mm, "mid": v(8.3, -9.08) * mm, "end": v(8.8, -9.17) * mm});
            skArc(sketch, "E1804", {"start": v(0.43, -11.27) * mm, "mid": v(0.43, -11.28) * mm, "end": v(0.42, -11.29) * mm});
            skArc(sketch, "E1805", {"start": v(0.42, -11.29) * mm, "mid": v(0.34, -11.35) * mm, "end": v(0.26, -11.42) * mm});
            skArc(sketch, "E1806", {"start": v(0.26, -11.42) * mm, "mid": v(0.17, -11.5) * mm, "end": v(0.08, -11.56) * mm});
            skArc(sketch, "E1807", {"start": v(0.08, -11.56) * mm, "mid": v(-0.03, -11.65) * mm, "end": v(-0.14, -11.73) * mm});
            skLineSegment(sketch, "E1808", {"start": v(-0.14, -11.73) * mm, "end": v(-0.7, -12.17) * mm});
            skLineSegment(sketch, "E1809", {"start": v(-0.7, -12.17) * mm, "end": v(-1.47, -11.76) * mm});
            skLineSegment(sketch, "E1810", {"start": v(-1.47, -11.76) * mm, "end": v(-2.23, -11.36) * mm});
            skLineSegment(sketch, "E1811", {"start": v(-2.23, -11.36) * mm, "end": v(-1.54, -10.73) * mm});
            skLineSegment(sketch, "E1812", {"start": v(-1.54, -10.73) * mm, "end": v(-0.86, -10.1) * mm});
            skLineSegment(sketch, "E1813", {"start": v(-0.86, -10.1) * mm, "end": v(-0.21, -10.66) * mm});
            skArc(sketch, "E1814", {"start": v(-0.21, -10.66) * mm, "mid": v(-0.09, -10.77) * mm, "end": v(0.03, -10.88) * mm});
            skArc(sketch, "E1815", {"start": v(0.03, -10.88) * mm, "mid": v(0.14, -10.98) * mm, "end": v(0.24, -11.08) * mm});
            skArc(sketch, "E1816", {"start": v(0.24, -11.08) * mm, "mid": v(0.33, -11.16) * mm, "end": v(0.42, -11.24) * mm});
            skArc(sketch, "E1817", {"start": v(0.42, -11.24) * mm, "mid": v(0.43, -11.25) * mm, "end": v(0.43, -11.27) * mm});
            skArc(sketch, "E1818", {"start": v(-9.06, -10.3) * mm, "mid": v(-8.9, -10.34) * mm, "end": v(-8.74, -10.38) * mm});
            skArc(sketch, "E1819", {"start": v(-8.74, -10.38) * mm, "mid": v(-8.53, -10.44) * mm, "end": v(-8.32, -10.5) * mm});
            skArc(sketch, "E1820", {"start": v(-8.32, -10.5) * mm, "mid": v(-8.1, -10.56) * mm, "end": v(-7.87, -10.62) * mm});
            skArc(sketch, "E1821", {"start": v(-7.87, -10.62) * mm, "mid": v(-7.68, -10.68) * mm, "end": v(-7.48, -10.74) * mm});
            skArc(sketch, "E1822", {"start": v(-7.48, -10.74) * mm, "mid": v(-7.03, -10.9) * mm, "end": v(-6.58, -11.06) * mm});
            skArc(sketch, "E1823", {"start": v(-6.58, -11.06) * mm, "mid": v(-6.02, -11.27) * mm, "end": v(-5.46, -11.5) * mm});
            skArc(sketch, "E1824", {"start": v(-5.46, -11.5) * mm, "mid": v(-4.88, -11.73) * mm, "end": v(-4.3, -11.97) * mm});
            skArc(sketch, "E1825", {"start": v(-4.3, -11.97) * mm, "mid": v(-4.25, -12) * mm, "end": v(-4.24, -12.06) * mm});
            skArc(sketch, "E1826", {"start": v(-4.24, -12.06) * mm, "mid": v(-4.24, -12.08) * mm, "end": v(-4.26, -12.1) * mm});
            skArc(sketch, "E1827", {"start": v(-4.26, -12.1) * mm, "mid": v(-4.36, -12.16) * mm, "end": v(-4.46, -12.23) * mm});
            skArc(sketch, "E1828", {"start": v(-4.46, -12.23) * mm, "mid": v(-4.57, -12.31) * mm, "end": v(-4.7, -12.4) * mm});
            skArc(sketch, "E1829", {"start": v(-4.7, -12.4) * mm, "mid": v(-4.84, -12.48) * mm, "end": v(-4.98, -12.57) * mm});
            skLineSegment(sketch, "E1830", {"start": v(-4.98, -12.57) * mm, "end": v(-5.73, -13.01) * mm});
            skLineSegment(sketch, "E1831", {"start": v(-5.73, -13.01) * mm, "end": v(-6.39, -12.77) * mm});
            skArc(sketch, "E1832", {"start": v(-6.39, -12.77) * mm, "mid": v(-7.06, -12.55) * mm, "end": v(-7.74, -12.36) * mm});
            skArc(sketch, "E1833", {"start": v(-7.74, -12.36) * mm, "mid": v(-8.48, -12.2) * mm, "end": v(-9.22, -12.07) * mm});
            skArc(sketch, "E1834", {"start": v(-9.22, -12.07) * mm, "mid": v(-9.98, -11.98) * mm, "end": v(-10.73, -11.92) * mm});
            skArc(sketch, "E1835", {"start": v(-10.73, -11.92) * mm, "mid": v(-11.46, -11.9) * mm, "end": v(-12.2, -11.9) * mm});
            skLineSegment(sketch, "E1836", {"start": v(-12.2, -11.9) * mm, "end": v(-13.37, -11.96) * mm});
            skLineSegment(sketch, "E1837", {"start": v(-13.37, -11.96) * mm, "end": v(-13.23, -11.61) * mm});
            skArc(sketch, "E1838", {"start": v(-13.23, -11.61) * mm, "mid": v(-13.2, -11.54) * mm, "end": v(-13.16, -11.47) * mm});
            skArc(sketch, "E1839", {"start": v(-13.16, -11.47) * mm, "mid": v(-13.12, -11.4) * mm, "end": v(-13.08, -11.32) * mm});
            skArc(sketch, "E1840", {"start": v(-13.08, -11.32) * mm, "mid": v(-13.04, -11.25) * mm, "end": v(-13, -11.18) * mm});
            skArc(sketch, "E1841", {"start": v(-13, -11.18) * mm, "mid": v(-12.96, -11.13) * mm, "end": v(-12.92, -11.09) * mm});
            skArc(sketch, "E1842", {"start": v(-12.92, -11.09) * mm, "mid": v(-12.82, -10.99) * mm, "end": v(-12.71, -10.9) * mm});
            skArc(sketch, "E1843", {"start": v(-12.71, -10.9) * mm, "mid": v(-12.53, -10.78) * mm, "end": v(-12.35, -10.67) * mm});
            skArc(sketch, "E1844", {"start": v(-12.35, -10.67) * mm, "mid": v(-12.15, -10.56) * mm, "end": v(-11.95, -10.45) * mm});
            skArc(sketch, "E1845", {"start": v(-11.95, -10.45) * mm, "mid": v(-11.77, -10.37) * mm, "end": v(-11.59, -10.3) * mm});
            skArc(sketch, "E1846", {"start": v(-11.59, -10.3) * mm, "mid": v(-11.36, -10.24) * mm, "end": v(-11.14, -10.2) * mm});
            skArc(sketch, "E1847", {"start": v(-11.14, -10.2) * mm, "mid": v(-10.8, -10.18) * mm, "end": v(-10.46, -10.18) * mm});
            skArc(sketch, "E1848", {"start": v(-10.46, -10.18) * mm, "mid": v(-10.1, -10.18) * mm, "end": v(-9.73, -10.2) * mm});
            skArc(sketch, "E1849", {"start": v(-9.73, -10.2) * mm, "mid": v(-9.4, -10.25) * mm, "end": v(-9.06, -10.3) * mm});
            skArc(sketch, "E1850", {"start": v(1.83, -12.37) * mm, "mid": v(1.96, -12.47) * mm, "end": v(2.1, -12.56) * mm});
            skArc(sketch, "E1851", {"start": v(2.1, -12.56) * mm, "mid": v(2.23, -12.66) * mm, "end": v(2.37, -12.76) * mm});
            skArc(sketch, "E1852", {"start": v(2.37, -12.76) * mm, "mid": v(2.5, -12.84) * mm, "end": v(2.62, -12.92) * mm});
            skArc(sketch, "E1853", {"start": v(2.62, -12.92) * mm, "mid": v(2.7, -12.96) * mm, "end": v(2.78, -13) * mm});
            skArc(sketch, "E1854", {"start": v(2.78, -13) * mm, "mid": v(2.84, -13.03) * mm, "end": v(2.9, -13.07) * mm});
            skArc(sketch, "E1855", {"start": v(2.9, -13.07) * mm, "mid": v(2.96, -13.1) * mm, "end": v(3, -13.13) * mm});
            skArc(sketch, "E1856", {"start": v(3, -13.13) * mm, "mid": v(3.04, -13.16) * mm, "end": v(3.08, -13.2) * mm});
            skArc(sketch, "E1857", {"start": v(3.08, -13.2) * mm, "mid": v(3.1, -13.21) * mm, "end": v(3.1, -13.23) * mm});
            skArc(sketch, "E1858", {"start": v(3.1, -13.23) * mm, "mid": v(3.1, -13.26) * mm, "end": v(3.08, -13.27) * mm});
            skArc(sketch, "E1859", {"start": v(3.08, -13.27) * mm, "mid": v(3.03, -13.31) * mm, "end": v(2.98, -13.35) * mm});
            skArc(sketch, "E1860", {"start": v(2.98, -13.35) * mm, "mid": v(2.9, -13.4) * mm, "end": v(2.84, -13.43) * mm});
            skArc(sketch, "E1861", {"start": v(2.84, -13.43) * mm, "mid": v(2.76, -13.47) * mm, "end": v(2.68, -13.51) * mm});
            skLineSegment(sketch, "E1862", {"start": v(2.68, -13.51) * mm, "end": v(2.26, -13.72) * mm});
            skLineSegment(sketch, "E1863", {"start": v(2.26, -13.72) * mm, "end": v(1.2, -13.16) * mm});
            skArc(sketch, "E1864", {"start": v(1.2, -13.16) * mm, "mid": v(1, -13.05) * mm, "end": v(0.8, -12.94) * mm});
            skArc(sketch, "E1865", {"start": v(0.8, -12.94) * mm, "mid": v(0.63, -12.84) * mm, "end": v(0.46, -12.75) * mm});
            skArc(sketch, "E1866", {"start": v(0.46, -12.75) * mm, "mid": v(0.3, -12.66) * mm, "end": v(0.16, -12.57) * mm});
            skArc(sketch, "E1867", {"start": v(0.16, -12.57) * mm, "mid": v(0.15, -12.56) * mm, "end": v(0.15, -12.55) * mm});
            skArc(sketch, "E1868", {"start": v(0.15, -12.55) * mm, "mid": v(0.16, -12.5) * mm, "end": v(0.18, -12.48) * mm});
            skArc(sketch, "E1869", {"start": v(0.18, -12.48) * mm, "mid": v(0.39, -12.33) * mm, "end": v(0.6, -12.2) * mm});
            skArc(sketch, "E1870", {"start": v(0.6, -12.2) * mm, "mid": v(0.8, -12.05) * mm, "end": v(1, -11.91) * mm});
            skArc(sketch, "E1871", {"start": v(1, -11.91) * mm, "mid": v(1.06, -11.89) * mm, "end": v(1.11, -11.88) * mm});
            skArc(sketch, "E1872", {"start": v(1.11, -11.88) * mm, "mid": v(1.14, -11.88) * mm, "end": v(1.16, -11.9) * mm});
            skArc(sketch, "E1873", {"start": v(1.16, -11.9) * mm, "mid": v(1.26, -11.96) * mm, "end": v(1.35, -12.02) * mm});
            skArc(sketch, "E1874", {"start": v(1.35, -12.02) * mm, "mid": v(1.46, -12.1) * mm, "end": v(1.57, -12.18) * mm});
            skArc(sketch, "E1875", {"start": v(1.57, -12.18) * mm, "mid": v(1.7, -12.27) * mm, "end": v(1.83, -12.37) * mm});
            skArc(sketch, "E1876", {"start": v(10.96, -12) * mm, "mid": v(10.98, -12.04) * mm, "end": v(10.98, -12.1) * mm});
            skArc(sketch, "E1877", {"start": v(10.98, -12.1) * mm, "mid": v(10.93, -12.2) * mm, "end": v(10.88, -12.3) * mm});
            skArc(sketch, "E1878", {"start": v(10.88, -12.3) * mm, "mid": v(10.8, -12.4) * mm, "end": v(10.71, -12.52) * mm});
            skArc(sketch, "E1879", {"start": v(10.71, -12.52) * mm, "mid": v(10.61, -12.63) * mm, "end": v(10.5, -12.74) * mm});
            skArc(sketch, "E1880", {"start": v(10.5, -12.74) * mm, "mid": v(10.26, -12.94) * mm, "end": v(10, -13.1) * mm});
            skArc(sketch, "E1881", {"start": v(10, -13.1) * mm, "mid": v(9.67, -13.23) * mm, "end": v(9.33, -13.33) * mm});
            skArc(sketch, "E1882", {"start": v(9.33, -13.33) * mm, "mid": v(8.96, -13.4) * mm, "end": v(8.58, -13.44) * mm});
            skArc(sketch, "E1883", {"start": v(8.58, -13.44) * mm, "mid": v(8.19, -13.43) * mm, "end": v(7.8, -13.4) * mm});
            skArc(sketch, "E1884", {"start": v(7.8, -13.4) * mm, "mid": v(7.5, -13.35) * mm, "end": v(7.19, -13.29) * mm});
            skArc(sketch, "E1885", {"start": v(7.19, -13.29) * mm, "mid": v(6.84, -13.2) * mm, "end": v(6.5, -13.11) * mm});
            skArc(sketch, "E1886", {"start": v(6.5, -13.11) * mm, "mid": v(6.16, -13.02) * mm, "end": v(5.83, -12.92) * mm});
            skArc(sketch, "E1887", {"start": v(5.83, -12.92) * mm, "mid": v(5.78, -12.88) * mm, "end": v(5.76, -12.83) * mm});
            skArc(sketch, "E1888", {"start": v(5.76, -12.83) * mm, "mid": v(5.78, -12.77) * mm, "end": v(5.83, -12.73) * mm});
            skArc(sketch, "E1889", {"start": v(5.83, -12.73) * mm, "mid": v(6.17, -12.59) * mm, "end": v(6.5, -12.45) * mm});
            skArc(sketch, "E1890", {"start": v(6.5, -12.45) * mm, "mid": v(6.84, -12.32) * mm, "end": v(7.19, -12.2) * mm});
            skArc(sketch, "E1891", {"start": v(7.19, -12.2) * mm, "mid": v(7.46, -12.1) * mm, "end": v(7.74, -12.03) * mm});
            skArc(sketch, "E1892", {"start": v(7.74, -12.03) * mm, "mid": v(8.04, -11.97) * mm, "end": v(8.35, -11.94) * mm});
            skArc(sketch, "E1893", {"start": v(8.35, -11.94) * mm, "mid": v(8.93, -11.92) * mm, "end": v(9.51, -11.9) * mm});
            skArc(sketch, "E1894", {"start": v(9.51, -11.9) * mm, "mid": v(10.13, -11.9) * mm, "end": v(10.74, -11.9) * mm});
            skArc(sketch, "E1895", {"start": v(10.74, -11.9) * mm, "mid": v(10.86, -11.93) * mm, "end": v(10.96, -12) * mm});
            skArc(sketch, "E1896", {"start": v(12.51, -12.55) * mm, "mid": v(12.73, -12.72) * mm, "end": v(12.93, -12.9) * mm});
            skArc(sketch, "E1897", {"start": v(12.93, -12.9) * mm, "mid": v(13.1, -13.09) * mm, "end": v(13.23, -13.28) * mm});
            skArc(sketch, "E1898", {"start": v(13.23, -13.28) * mm, "mid": v(13.34, -13.48) * mm, "end": v(13.42, -13.68) * mm});
            skArc(sketch, "E1899", {"start": v(13.42, -13.68) * mm, "mid": v(13.46, -13.88) * mm, "end": v(13.48, -14.09) * mm});
            skArc(sketch, "E1900", {"start": v(13.48, -14.09) * mm, "mid": v(13.46, -14.39) * mm, "end": v(13.39, -14.68) * mm});
            skArc(sketch, "E1901", {"start": v(13.39, -14.68) * mm, "mid": v(13.28, -14.95) * mm, "end": v(13.12, -15.19) * mm});
            skArc(sketch, "E1902", {"start": v(13.12, -15.19) * mm, "mid": v(12.91, -15.42) * mm, "end": v(12.67, -15.62) * mm});
            skArc(sketch, "E1903", {"start": v(12.67, -15.62) * mm, "mid": v(12.35, -15.82) * mm, "end": v(12.01, -15.98) * mm});
            skLineSegment(sketch, "E1904", {"start": v(12.01, -15.98) * mm, "end": v(11.55, -16.19) * mm});
            skLineSegment(sketch, "E1905", {"start": v(11.55, -16.19) * mm, "end": v(11.11, -15.75) * mm});
            skArc(sketch, "E1906", {"start": v(11.11, -15.75) * mm, "mid": v(10.9, -15.56) * mm, "end": v(10.66, -15.38) * mm});
            skArc(sketch, "E1907", {"start": v(10.66, -15.38) * mm, "mid": v(10.43, -15.23) * mm, "end": v(10.18, -15.11) * mm});
            skArc(sketch, "E1908", {"start": v(10.18, -15.11) * mm, "mid": v(9.92, -15.01) * mm, "end": v(9.65, -14.94) * mm});
            skArc(sketch, "E1909", {"start": v(9.65, -14.94) * mm, "mid": v(9.35, -14.88) * mm, "end": v(9.04, -14.85) * mm});
            skArc(sketch, "E1910", {"start": v(9.04, -14.85) * mm, "mid": v(8.74, -14.85) * mm, "end": v(8.43, -14.86) * mm});
            skArc(sketch, "E1911", {"start": v(8.43, -14.86) * mm, "mid": v(8.07, -14.9) * mm, "end": v(7.7, -14.95) * mm});
            skArc(sketch, "E1912", {"start": v(7.7, -14.95) * mm, "mid": v(7.33, -15.02) * mm, "end": v(6.96, -15.1) * mm});
            skArc(sketch, "E1913", {"start": v(6.96, -15.1) * mm, "mid": v(6.64, -15.2) * mm, "end": v(6.32, -15.3) * mm});
            skLineSegment(sketch, "E1914", {"start": v(6.32, -15.3) * mm, "end": v(5.85, -15.48) * mm});
            skLineSegment(sketch, "E1915", {"start": v(5.85, -15.48) * mm, "end": v(4.57, -14.87) * mm});
            skArc(sketch, "E1916", {"start": v(4.57, -14.87) * mm, "mid": v(4.32, -14.75) * mm, "end": v(4.08, -14.63) * mm});
            skArc(sketch, "E1917", {"start": v(4.08, -14.63) * mm, "mid": v(3.87, -14.53) * mm, "end": v(3.67, -14.42) * mm});
            skArc(sketch, "E1918", {"start": v(3.67, -14.42) * mm, "mid": v(3.49, -14.32) * mm, "end": v(3.31, -14.23) * mm});
            skArc(sketch, "E1919", {"start": v(3.31, -14.23) * mm, "mid": v(3.3, -14.21) * mm, "end": v(3.29, -14.19) * mm});
            skArc(sketch, "E1920", {"start": v(3.29, -14.19) * mm, "mid": v(3.3, -14.17) * mm, "end": v(3.3, -14.15) * mm});
            skArc(sketch, "E1921", {"start": v(3.3, -14.15) * mm, "mid": v(3.36, -14.1) * mm, "end": v(3.4, -14.07) * mm});
            skArc(sketch, "E1922", {"start": v(3.4, -14.07) * mm, "mid": v(3.47, -14.02) * mm, "end": v(3.54, -13.98) * mm});
            skArc(sketch, "E1923", {"start": v(3.54, -13.98) * mm, "mid": v(3.62, -13.94) * mm, "end": v(3.7, -13.9) * mm});
            skLineSegment(sketch, "E1924", {"start": v(3.7, -13.9) * mm, "end": v(4.1, -13.67) * mm});
            skLineSegment(sketch, "E1925", {"start": v(4.1, -13.67) * mm, "end": v(4.82, -13.9) * mm});
            skArc(sketch, "E1926", {"start": v(4.82, -13.9) * mm, "mid": v(5.6, -14.14) * mm, "end": v(6.38, -14.31) * mm});
            skArc(sketch, "E1927", {"start": v(6.38, -14.31) * mm, "mid": v(7.16, -14.42) * mm, "end": v(7.94, -14.45) * mm});
            skArc(sketch, "E1928", {"start": v(7.94, -14.45) * mm, "mid": v(8.64, -14.42) * mm, "end": v(9.34, -14.32) * mm});
            skArc(sketch, "E1929", {"start": v(9.34, -14.32) * mm, "mid": v(9.89, -14.17) * mm, "end": v(10.4, -13.92) * mm});
            skArc(sketch, "E1930", {"start": v(10.4, -13.92) * mm, "mid": v(10.6, -13.8) * mm, "end": v(10.79, -13.66) * mm});
            skArc(sketch, "E1931", {"start": v(10.79, -13.66) * mm, "mid": v(10.97, -13.5) * mm, "end": v(11.13, -13.34) * mm});
            skArc(sketch, "E1932", {"start": v(11.13, -13.34) * mm, "mid": v(11.28, -13.17) * mm, "end": v(11.42, -13) * mm});
            skArc(sketch, "E1933", {"start": v(11.42, -13) * mm, "mid": v(11.53, -12.82) * mm, "end": v(11.62, -12.64) * mm});
            skArc(sketch, "E1934", {"start": v(11.62, -12.64) * mm, "mid": v(11.7, -12.5) * mm, "end": v(11.78, -12.37) * mm});
            skArc(sketch, "E1935", {"start": v(11.78, -12.37) * mm, "mid": v(11.85, -12.3) * mm, "end": v(11.95, -12.28) * mm});
            skArc(sketch, "E1936", {"start": v(11.95, -12.28) * mm, "mid": v(12.06, -12.28) * mm, "end": v(12.16, -12.32) * mm});
            skArc(sketch, "E1937", {"start": v(12.16, -12.32) * mm, "mid": v(12.34, -12.43) * mm, "end": v(12.51, -12.55) * mm});
            skArc(sketch, "E1938", {"start": v(-2.83, -12.74) * mm, "mid": v(-2.7, -12.82) * mm, "end": v(-2.57, -12.9) * mm});
            skArc(sketch, "E1939", {"start": v(-2.57, -12.9) * mm, "mid": v(-2.46, -12.96) * mm, "end": v(-2.34, -13.02) * mm});
            skArc(sketch, "E1940", {"start": v(-2.34, -13.02) * mm, "mid": v(-2.25, -13.08) * mm, "end": v(-2.15, -13.14) * mm});
            skArc(sketch, "E1941", {"start": v(-2.15, -13.14) * mm, "mid": v(-2.14, -13.15) * mm, "end": v(-2.14, -13.16) * mm});
            skArc(sketch, "E1942", {"start": v(-2.14, -13.16) * mm, "mid": v(-2.14, -13.17) * mm, "end": v(-2.15, -13.18) * mm});
            skArc(sketch, "E1943", {"start": v(-2.15, -13.18) * mm, "mid": v(-2.24, -13.25) * mm, "end": v(-2.33, -13.33) * mm});
            skArc(sketch, "E1944", {"start": v(-2.33, -13.33) * mm, "mid": v(-2.44, -13.4) * mm, "end": v(-2.54, -13.49) * mm});
            skArc(sketch, "E1945", {"start": v(-2.54, -13.49) * mm, "mid": v(-2.67, -13.58) * mm, "end": v(-2.8, -13.68) * mm});
            skLineSegment(sketch, "E1946", {"start": v(-2.79, -13.68) * mm, "end": v(-3.44, -14.16) * mm});
            skLineSegment(sketch, "E1947", {"start": v(-3.44, -14.16) * mm, "end": v(-4.27, -13.73) * mm});
            skLineSegment(sketch, "E1948", {"start": v(-4.27, -13.73) * mm, "end": v(-5.1, -13.3) * mm});
            skLineSegment(sketch, "E1949", {"start": v(-5.1, -13.3) * mm, "end": v(-4.4, -12.83) * mm});
            skArc(sketch, "E1950", {"start": v(-4.4, -12.83) * mm, "mid": v(-4.27, -12.74) * mm, "end": v(-4.13, -12.66) * mm});
            skArc(sketch, "E1951", {"start": v(-4.13, -12.66) * mm, "mid": v(-4.01, -12.58) * mm, "end": v(-3.89, -12.5) * mm});
            skArc(sketch, "E1952", {"start": v(-3.89, -12.5) * mm, "mid": v(-3.78, -12.44) * mm, "end": v(-3.68, -12.38) * mm});
            skArc(sketch, "E1953", {"start": v(-3.68, -12.38) * mm, "mid": v(-3.65, -12.37) * mm, "end": v(-3.62, -12.37) * mm});
            skArc(sketch, "E1954", {"start": v(-3.62, -12.37) * mm, "mid": v(-3.59, -12.37) * mm, "end": v(-3.55, -12.38) * mm});
            skArc(sketch, "E1955", {"start": v(-3.55, -12.38) * mm, "mid": v(-3.45, -12.42) * mm, "end": v(-3.35, -12.47) * mm});
            skArc(sketch, "E1956", {"start": v(-3.35, -12.47) * mm, "mid": v(-3.22, -12.53) * mm, "end": v(-3.1, -12.6) * mm});
            skArc(sketch, "E1957", {"start": v(-3.1, -12.6) * mm, "mid": v(-2.97, -12.67) * mm, "end": v(-2.83, -12.74) * mm});
            skArc(sketch, "E1958", {"start": v(-10, -13.35) * mm, "mid": v(-9.66, -13.41) * mm, "end": v(-9.32, -13.48) * mm});
            skArc(sketch, "E1959", {"start": v(-9.32, -13.48) * mm, "mid": v(-9, -13.56) * mm, "end": v(-8.67, -13.64) * mm});
            skArc(sketch, "E1960", {"start": v(-8.67, -13.64) * mm, "mid": v(-8.39, -13.72) * mm, "end": v(-8.1, -13.8) * mm});
            skArc(sketch, "E1961", {"start": v(-8.1, -13.8) * mm, "mid": v(-8.06, -13.83) * mm, "end": v(-8.05, -13.88) * mm});
            skArc(sketch, "E1962", {"start": v(-8.05, -13.88) * mm, "mid": v(-8.07, -13.95) * mm, "end": v(-8.14, -13.99) * mm});
            skArc(sketch, "E1963", {"start": v(-8.14, -13.99) * mm, "mid": v(-8.5, -14.04) * mm, "end": v(-8.88, -14.08) * mm});
            skArc(sketch, "E1964", {"start": v(-8.88, -14.08) * mm, "mid": v(-9.27, -14.12) * mm, "end": v(-9.66, -14.15) * mm});
            skArc(sketch, "E1965", {"start": v(-9.66, -14.15) * mm, "mid": v(-10, -14.15) * mm, "end": v(-10.35, -14.14) * mm});
            skArc(sketch, "E1966", {"start": v(-10.35, -14.14) * mm, "mid": v(-10.7, -14.12) * mm, "end": v(-11.04, -14.07) * mm});
            skArc(sketch, "E1967", {"start": v(-11.04, -14.07) * mm, "mid": v(-11.36, -14) * mm, "end": v(-11.67, -13.92) * mm});
            skArc(sketch, "E1968", {"start": v(-11.67, -13.92) * mm, "mid": v(-11.94, -13.83) * mm, "end": v(-12.2, -13.71) * mm});
            skArc(sketch, "E1969", {"start": v(-12.2, -13.71) * mm, "mid": v(-12.4, -13.6) * mm, "end": v(-12.6, -13.45) * mm});
            skLineSegment(sketch, "E1970", {"start": v(-12.6, -13.45) * mm, "end": v(-12.86, -13.22) * mm});
            skLineSegment(sketch, "E1971", {"start": v(-12.86, -13.22) * mm, "end": v(-11.8, -13.22) * mm});
            skArc(sketch, "E1972", {"start": v(-11.8, -13.22) * mm, "mid": v(-11.58, -13.22) * mm, "end": v(-11.35, -13.23) * mm});
            skArc(sketch, "E1973", {"start": v(-11.35, -13.23) * mm, "mid": v(-11.1, -13.24) * mm, "end": v(-10.85, -13.25) * mm});
            skArc(sketch, "E1974", {"start": v(-10.85, -13.25) * mm, "mid": v(-10.6, -13.27) * mm, "end": v(-10.37, -13.3) * mm});
            skArc(sketch, "E1975", {"start": v(-10.37, -13.3) * mm, "mid": v(-10.18, -13.32) * mm, "end": v(-10, -13.35) * mm});
            skArc(sketch, "E1976", {"start": v(-13.5, -13.92) * mm, "mid": v(-13.26, -14.14) * mm, "end": v(-13, -14.33) * mm});
            skArc(sketch, "E1977", {"start": v(-13, -14.33) * mm, "mid": v(-12.74, -14.48) * mm, "end": v(-12.46, -14.59) * mm});
            skArc(sketch, "E1978", {"start": v(-12.46, -14.59) * mm, "mid": v(-12.11, -14.68) * mm, "end": v(-11.75, -14.74) * mm});
            skArc(sketch, "E1979", {"start": v(-11.75, -14.74) * mm, "mid": v(-11.24, -14.78) * mm, "end": v(-10.73, -14.81) * mm});
            skArc(sketch, "E1980", {"start": v(-10.73, -14.81) * mm, "mid": v(-10.25, -14.82) * mm, "end": v(-9.77, -14.82) * mm});
            skArc(sketch, "E1981", {"start": v(-9.77, -14.82) * mm, "mid": v(-9.35, -14.8) * mm, "end": v(-8.93, -14.76) * mm});
            skArc(sketch, "E1982", {"start": v(-8.93, -14.76) * mm, "mid": v(-8.56, -14.7) * mm, "end": v(-8.2, -14.64) * mm});
            skArc(sketch, "E1983", {"start": v(-8.2, -14.64) * mm, "mid": v(-7.85, -14.55) * mm, "end": v(-7.5, -14.45) * mm});
            skLineSegment(sketch, "E1984", {"start": v(-7.5, -14.45) * mm, "end": v(-6.98, -14.27) * mm});
            skLineSegment(sketch, "E1985", {"start": v(-6.98, -14.27) * mm, "end": v(-6.16, -14.69) * mm});
            skArc(sketch, "E1986", {"start": v(-6.16, -14.69) * mm, "mid": v(-5.75, -14.9) * mm, "end": v(-5.33, -15.12) * mm});
            skArc(sketch, "E1987", {"start": v(-5.33, -15.12) * mm, "mid": v(-5.26, -15.17) * mm, "end": v(-5.2, -15.25) * mm});
            skArc(sketch, "E1988", {"start": v(-5.2, -15.25) * mm, "mid": v(-5.2, -15.32) * mm, "end": v(-5.24, -15.38) * mm});
            skArc(sketch, "E1989", {"start": v(-5.24, -15.38) * mm, "mid": v(-5.45, -15.54) * mm, "end": v(-5.67, -15.7) * mm});
            skLineSegment(sketch, "E1990", {"start": v(-5.67, -15.7) * mm, "end": v(-6.27, -16.1) * mm});
            skLineSegment(sketch, "E1991", {"start": v(-6.27, -16.1) * mm, "end": v(-7.28, -15.76) * mm});
            skArc(sketch, "E1992", {"start": v(-7.28, -15.76) * mm, "mid": v(-7.9, -15.56) * mm, "end": v(-8.53, -15.4) * mm});
            skArc(sketch, "E1993", {"start": v(-8.53, -15.4) * mm, "mid": v(-9.04, -15.3) * mm, "end": v(-9.56, -15.24) * mm});
            skArc(sketch, "E1994", {"start": v(-9.56, -15.24) * mm, "mid": v(-10.03, -15.24) * mm, "end": v(-10.5, -15.28) * mm});
            skArc(sketch, "E1995", {"start": v(-10.5, -15.28) * mm, "mid": v(-11, -15.37) * mm, "end": v(-11.5, -15.5) * mm});
            skArc(sketch, "E1996", {"start": v(-11.5, -15.5) * mm, "mid": v(-11.95, -15.67) * mm, "end": v(-12.37, -15.9) * mm});
            skArc(sketch, "E1997", {"start": v(-12.37, -15.9) * mm, "mid": v(-12.72, -16.16) * mm, "end": v(-13.03, -16.48) * mm});
            skArc(sketch, "E1998", {"start": v(-13.03, -16.48) * mm, "mid": v(-13.27, -16.84) * mm, "end": v(-13.44, -17.23) * mm});
            skArc(sketch, "E1999", {"start": v(-13.44, -17.23) * mm, "mid": v(-13.55, -17.67) * mm, "end": v(-13.6, -18.12) * mm});
            skArc(sketch, "E2000", {"start": v(-13.6, -18.12) * mm, "mid": v(-13.61, -18.35) * mm, "end": v(-13.64, -18.58) * mm});
            skArc(sketch, "E2001", {"start": v(-13.64, -18.58) * mm, "mid": v(-13.68, -18.67) * mm, "end": v(-13.76, -18.73) * mm});
            skArc(sketch, "E2002", {"start": v(-13.76, -18.73) * mm, "mid": v(-13.88, -18.75) * mm, "end": v(-14, -18.72) * mm});
            skArc(sketch, "E2003", {"start": v(-14, -18.72) * mm, "mid": v(-14.28, -18.6) * mm, "end": v(-14.57, -18.46) * mm});
            skArc(sketch, "E2004", {"start": v(-14.57, -18.46) * mm, "mid": v(-14.8, -18.35) * mm, "end": v(-15.01, -18.22) * mm});
            skArc(sketch, "E2005", {"start": v(-15.01, -18.22) * mm, "mid": v(-15.19, -18.1) * mm, "end": v(-15.35, -17.95) * mm});
            skArc(sketch, "E2006", {"start": v(-15.35, -17.95) * mm, "mid": v(-15.5, -17.8) * mm, "end": v(-15.63, -17.62) * mm});
            skArc(sketch, "E2007", {"start": v(-15.63, -17.62) * mm, "mid": v(-15.77, -17.4) * mm, "end": v(-15.9, -17.18) * mm});
            skArc(sketch, "E2008", {"start": v(-15.9, -17.18) * mm, "mid": v(-16.04, -16.84) * mm, "end": v(-16.13, -16.5) * mm});
            skArc(sketch, "E2009", {"start": v(-16.13, -16.5) * mm, "mid": v(-16.15, -16.14) * mm, "end": v(-16.11, -15.78) * mm});
            skArc(sketch, "E2010", {"start": v(-16.11, -15.78) * mm, "mid": v(-16.01, -15.42) * mm, "end": v(-15.86, -15.08) * mm});
            skArc(sketch, "E2011", {"start": v(-15.86, -15.08) * mm, "mid": v(-15.63, -14.72) * mm, "end": v(-15.36, -14.4) * mm});
            skArc(sketch, "E2012", {"start": v(-15.36, -14.4) * mm, "mid": v(-15.22, -14.25) * mm, "end": v(-15.06, -14.12) * mm});
            skArc(sketch, "E2013", {"start": v(-15.06, -14.12) * mm, "mid": v(-14.84, -13.96) * mm, "end": v(-14.62, -13.81) * mm});
            skArc(sketch, "E2014", {"start": v(-14.62, -13.81) * mm, "mid": v(-14.4, -13.68) * mm, "end": v(-14.19, -13.56) * mm});
            skArc(sketch, "E2015", {"start": v(-14.19, -13.56) * mm, "mid": v(-14.07, -13.52) * mm, "end": v(-13.95, -13.5) * mm});
            skArc(sketch, "E2016", {"start": v(-13.95, -13.5) * mm, "mid": v(-13.94, -13.5) * mm, "end": v(-13.92, -13.51) * mm});
            skArc(sketch, "E2017", {"start": v(-13.92, -13.51) * mm, "mid": v(-13.86, -13.57) * mm, "end": v(-13.8, -13.63) * mm});
            skArc(sketch, "E2018", {"start": v(-13.8, -13.63) * mm, "mid": v(-13.73, -13.7) * mm, "end": v(-13.66, -13.76) * mm});
            skArc(sketch, "E2019", {"start": v(-13.66, -13.76) * mm, "mid": v(-13.58, -13.84) * mm, "end": v(-13.5, -13.92) * mm});
            skArc(sketch, "E2020", {"start": v(-0.33, -14.1) * mm, "mid": v(-0.16, -14.2) * mm, "end": v(0.01, -14.3) * mm});
            skArc(sketch, "E2021", {"start": v(0.01, -14.3) * mm, "mid": v(0.16, -14.38) * mm, "end": v(0.3, -14.48) * mm});
            skArc(sketch, "E2022", {"start": v(0.3, -14.48) * mm, "mid": v(0.42, -14.56) * mm, "end": v(0.54, -14.64) * mm});
            skArc(sketch, "E2023", {"start": v(0.54, -14.64) * mm, "mid": v(0.56, -14.66) * mm, "end": v(0.56, -14.69) * mm});
            skArc(sketch, "E2024", {"start": v(0.56, -14.69) * mm, "mid": v(0.55, -14.72) * mm, "end": v(0.53, -14.74) * mm});
            skArc(sketch, "E2025", {"start": v(0.53, -14.74) * mm, "mid": v(0.44, -14.81) * mm, "end": v(0.34, -14.89) * mm});
            skArc(sketch, "E2026", {"start": v(0.34, -14.89) * mm, "mid": v(0.22, -14.97) * mm, "end": v(0.1, -15.06) * mm});
            skArc(sketch, "E2027", {"start": v(0.1, -15.06) * mm, "mid": v(-0.04, -15.15) * mm, "end": v(-0.18, -15.24) * mm});
            skLineSegment(sketch, "E2028", {"start": v(-0.18, -15.24) * mm, "end": v(-0.9, -15.7) * mm});
            skLineSegment(sketch, "E2029", {"start": v(-0.9, -15.7) * mm, "end": v(-1.8, -15.15) * mm});
            skArc(sketch, "E2030", {"start": v(-1.8, -15.15) * mm, "mid": v(-1.98, -15.04) * mm, "end": v(-2.15, -14.93) * mm});
            skArc(sketch, "E2031", {"start": v(-2.15, -14.93) * mm, "mid": v(-2.3, -14.83) * mm, "end": v(-2.44, -14.74) * mm});
            skArc(sketch, "E2032", {"start": v(-2.44, -14.74) * mm, "mid": v(-2.56, -14.65) * mm, "end": v(-2.68, -14.57) * mm});
            skArc(sketch, "E2033", {"start": v(-2.68, -14.57) * mm, "mid": v(-2.69, -14.55) * mm, "end": v(-2.69, -14.53) * mm});
            skArc(sketch, "E2034", {"start": v(-2.69, -14.53) * mm, "mid": v(-2.66, -14.47) * mm, "end": v(-2.6, -14.42) * mm});
            skArc(sketch, "E2035", {"start": v(-2.6, -14.42) * mm, "mid": v(-2.32, -14.22) * mm, "end": v(-2.04, -14.02) * mm});
            skArc(sketch, "E2036", {"start": v(-2.04, -14.03) * mm, "mid": v(-1.75, -13.83) * mm, "end": v(-1.47, -13.64) * mm});
            skArc(sketch, "E2037", {"start": v(-1.47, -13.64) * mm, "mid": v(-1.4, -13.6) * mm, "end": v(-1.33, -13.6) * mm});
            skArc(sketch, "E2038", {"start": v(-1.33, -13.6) * mm, "mid": v(-1.3, -13.6) * mm, "end": v(-1.27, -13.61) * mm});
            skArc(sketch, "E2039", {"start": v(-1.27, -13.61) * mm, "mid": v(-1.13, -13.68) * mm, "end": v(-1, -13.74) * mm});
            skArc(sketch, "E2040", {"start": v(-1, -13.74) * mm, "mid": v(-0.84, -13.82) * mm, "end": v(-0.69, -13.9) * mm});
            skArc(sketch, "E2041", {"start": v(-0.69, -13.9) * mm, "mid": v(-0.5, -14) * mm, "end": v(-0.33, -14.1) * mm});
            skLineSegment(sketch, "E2042", {"start": v(2.82, -15.8) * mm, "end": v(3.97, -16.37) * mm});
            skLineSegment(sketch, "E2043", {"start": v(3.97, -16.37) * mm, "end": v(3.27, -16.85) * mm});
            skArc(sketch, "E2044", {"start": v(3.27, -16.85) * mm, "mid": v(3.13, -16.95) * mm, "end": v(3, -17.04) * mm});
            skArc(sketch, "E2045", {"start": v(3, -17.04) * mm, "mid": v(2.86, -17.14) * mm, "end": v(2.72, -17.24) * mm});
            skArc(sketch, "E2046", {"start": v(2.72, -17.24) * mm, "mid": v(2.6, -17.32) * mm, "end": v(2.5, -17.41) * mm});
            skArc(sketch, "E2047", {"start": v(2.5, -17.41) * mm, "mid": v(2.43, -17.46) * mm, "end": v(2.38, -17.5) * mm});
            skArc(sketch, "E2048", {"start": v(2.38, -17.5) * mm, "mid": v(2.34, -17.54) * mm, "end": v(2.3, -17.58) * mm});
            skArc(sketch, "E2049", {"start": v(2.3, -17.58) * mm, "mid": v(2.26, -17.6) * mm, "end": v(2.22, -17.64) * mm});
            skArc(sketch, "E2050", {"start": v(2.22, -17.64) * mm, "mid": v(2.18, -17.66) * mm, "end": v(2.15, -17.68) * mm});
            skArc(sketch, "E2051", {"start": v(2.15, -17.68) * mm, "mid": v(2.13, -17.69) * mm, "end": v(2.11, -17.7) * mm});
            skArc(sketch, "E2052", {"start": v(2.11, -17.7) * mm, "mid": v(2.09, -17.69) * mm, "end": v(2.07, -17.68) * mm});
            skArc(sketch, "E2053", {"start": v(2.07, -17.68) * mm, "mid": v(1.9, -17.57) * mm, "end": v(1.74, -17.47) * mm});
            skArc(sketch, "E2054", {"start": v(1.74, -17.47) * mm, "mid": v(1.56, -17.35) * mm, "end": v(1.37, -17.23) * mm});
            skArc(sketch, "E2055", {"start": v(1.37, -17.23) * mm, "mid": v(1.16, -17.08) * mm, "end": v(0.95, -16.94) * mm});
            skLineSegment(sketch, "E2056", {"start": v(0.95, -16.94) * mm, "end": v(-0.15, -16.18) * mm});
            skLineSegment(sketch, "E2057", {"start": v(-0.15, -16.18) * mm, "end": v(0.64, -15.7) * mm});
            skArc(sketch, "E2058", {"start": v(0.64, -15.7) * mm, "mid": v(0.8, -15.6) * mm, "end": v(0.95, -15.52) * mm});
            skArc(sketch, "E2059", {"start": v(0.95, -15.52) * mm, "mid": v(1.1, -15.44) * mm, "end": v(1.23, -15.36) * mm});
            skArc(sketch, "E2060", {"start": v(1.23, -15.36) * mm, "mid": v(1.35, -15.3) * mm, "end": v(1.47, -15.24) * mm});
            skArc(sketch, "E2061", {"start": v(1.47, -15.24) * mm, "mid": v(1.51, -15.22) * mm, "end": v(1.55, -15.22) * mm});
            skArc(sketch, "E2062", {"start": v(1.55, -15.22) * mm, "mid": v(1.6, -15.22) * mm, "end": v(1.63, -15.23) * mm});
            skArc(sketch, "E2063", {"start": v(1.63, -15.23) * mm, "mid": v(1.8, -15.3) * mm, "end": v(1.97, -15.38) * mm});
            skArc(sketch, "E2064", {"start": v(1.97, -15.38) * mm, "mid": v(2.17, -15.48) * mm, "end": v(2.37, -15.57) * mm});
            skArc(sketch, "E2065", {"start": v(2.37, -15.57) * mm, "mid": v(2.6, -15.68) * mm, "end": v(2.82, -15.8) * mm});
            skArc(sketch, "E2066", {"start": v(9.82, -15.76) * mm, "mid": v(9.9, -15.8) * mm, "end": v(9.97, -15.85) * mm});
            skArc(sketch, "E2067", {"start": v(9.97, -15.85) * mm, "mid": v(10.06, -15.9) * mm, "end": v(10.13, -15.96) * mm});
            skArc(sketch, "E2068", {"start": v(10.13, -15.96) * mm, "mid": v(10.2, -16) * mm, "end": v(10.28, -16.06) * mm});
            skArc(sketch, "E2069", {"start": v(10.28, -16.06) * mm, "mid": v(10.32, -16.1) * mm, "end": v(10.37, -16.15) * mm});
            skArc(sketch, "E2070", {"start": v(10.37, -16.15) * mm, "mid": v(10.42, -16.21) * mm, "end": v(10.48, -16.28) * mm});
            skArc(sketch, "E2071", {"start": v(10.48, -16.28) * mm, "mid": v(10.48, -16.3) * mm, "end": v(10.48, -16.33) * mm});
            skArc(sketch, "E2072", {"start": v(10.48, -16.33) * mm, "mid": v(10.45, -16.35) * mm, "end": v(10.42, -16.36) * mm});
            skArc(sketch, "E2073", {"start": v(10.42, -16.36) * mm, "mid": v(10.3, -16.39) * mm, "end": v(10.19, -16.41) * mm});
            skArc(sketch, "E2074", {"start": v(10.19, -16.41) * mm, "mid": v(9.83, -16.45) * mm, "end": v(9.48, -16.44) * mm});
            skArc(sketch, "E2075", {"start": v(9.48, -16.44) * mm, "mid": v(8.86, -16.37) * mm, "end": v(8.24, -16.28) * mm});
            skArc(sketch, "E2076", {"start": v(8.24, -16.28) * mm, "mid": v(7.6, -16.17) * mm, "end": v(6.97, -16.05) * mm});
            skArc(sketch, "E2077", {"start": v(6.97, -16.05) * mm, "mid": v(6.86, -15.98) * mm, "end": v(6.81, -15.86) * mm});
            skArc(sketch, "E2078", {"start": v(6.81, -15.86) * mm, "mid": v(6.82, -15.84) * mm, "end": v(6.83, -15.83) * mm});
            skArc(sketch, "E2079", {"start": v(6.83, -15.83) * mm, "mid": v(6.87, -15.8) * mm, "end": v(6.92, -15.79) * mm});
            skArc(sketch, "E2080", {"start": v(6.92, -15.79) * mm, "mid": v(6.97, -15.76) * mm, "end": v(7.03, -15.74) * mm});
            skArc(sketch, "E2081", {"start": v(7.03, -15.74) * mm, "mid": v(7.1, -15.72) * mm, "end": v(7.17, -15.7) * mm});
            skArc(sketch, "E2082", {"start": v(7.17, -15.7) * mm, "mid": v(7.24, -15.68) * mm, "end": v(7.32, -15.66) * mm});
            skArc(sketch, "E2083", {"start": v(7.32, -15.66) * mm, "mid": v(7.4, -15.64) * mm, "end": v(7.48, -15.62) * mm});
            skArc(sketch, "E2084", {"start": v(7.48, -15.62) * mm, "mid": v(7.55, -15.6) * mm, "end": v(7.62, -15.59) * mm});
            skArc(sketch, "E2085", {"start": v(7.62, -15.59) * mm, "mid": v(7.67, -15.57) * mm, "end": v(7.72, -15.56) * mm});
            skArc(sketch, "E2086", {"start": v(7.72, -15.56) * mm, "mid": v(7.92, -15.52) * mm, "end": v(8.14, -15.5) * mm});
            skArc(sketch, "E2087", {"start": v(8.14, -15.5) * mm, "mid": v(8.46, -15.52) * mm, "end": v(8.79, -15.55) * mm});
            skArc(sketch, "E2088", {"start": v(8.79, -15.55) * mm, "mid": v(9.11, -15.59) * mm, "end": v(9.43, -15.64) * mm});
            skArc(sketch, "E2089", {"start": v(9.43, -15.64) * mm, "mid": v(9.63, -15.69) * mm, "end": v(9.82, -15.76) * mm});
            skArc(sketch, "E2090", {"start": v(-3.45, -16.17) * mm, "mid": v(-3.3, -16.27) * mm, "end": v(-3.13, -16.36) * mm});
            skArc(sketch, "E2091", {"start": v(-3.13, -16.36) * mm, "mid": v(-3, -16.45) * mm, "end": v(-2.86, -16.53) * mm});
            skArc(sketch, "E2092", {"start": v(-2.86, -16.53) * mm, "mid": v(-2.75, -16.6) * mm, "end": v(-2.64, -16.68) * mm});
            skArc(sketch, "E2093", {"start": v(-2.64, -16.68) * mm, "mid": v(-2.62, -16.7) * mm, "end": v(-2.62, -16.72) * mm});
            skArc(sketch, "E2094", {"start": v(-2.62, -16.72) * mm, "mid": v(-2.62, -16.74) * mm, "end": v(-2.64, -16.76) * mm});
            skArc(sketch, "E2095", {"start": v(-2.64, -16.76) * mm, "mid": v(-2.72, -16.82) * mm, "end": v(-2.8, -16.88) * mm});
            skArc(sketch, "E2096", {"start": v(-2.8, -16.88) * mm, "mid": v(-2.9, -16.95) * mm, "end": v(-3, -17.01) * mm});
            skArc(sketch, "E2097", {"start": v(-3, -17.01) * mm, "mid": v(-3.13, -17.09) * mm, "end": v(-3.25, -17.16) * mm});
            skArc(sketch, "E2098", {"start": v(-3.25, -17.16) * mm, "mid": v(-3.45, -17.28) * mm, "end": v(-3.65, -17.4) * mm});
            skArc(sketch, "E2099", {"start": v(-3.65, -17.4) * mm, "mid": v(-3.74, -17.43) * mm, "end": v(-3.83, -17.46) * mm});
            skArc(sketch, "E2100", {"start": v(-3.83, -17.46) * mm, "mid": v(-3.9, -17.47) * mm, "end": v(-3.96, -17.45) * mm});
            skArc(sketch, "E2101", {"start": v(-3.96, -17.45) * mm, "mid": v(-4.05, -17.42) * mm, "end": v(-4.13, -17.37) * mm});
            skArc(sketch, "E2102", {"start": v(-4.13, -17.37) * mm, "mid": v(-4.2, -17.33) * mm, "end": v(-4.26, -17.29) * mm});
            skArc(sketch, "E2103", {"start": v(-4.26, -17.29) * mm, "mid": v(-4.37, -17.22) * mm, "end": v(-4.48, -17.15) * mm});
            skArc(sketch, "E2104", {"start": v(-4.48, -17.15) * mm, "mid": v(-4.6, -17.08) * mm, "end": v(-4.73, -17) * mm});
            skArc(sketch, "E2105", {"start": v(-4.73, -17) * mm, "mid": v(-4.85, -16.93) * mm, "end": v(-4.97, -16.86) * mm});
            skArc(sketch, "E2106", {"start": v(-4.97, -16.85) * mm, "mid": v(-5.09, -16.79) * mm, "end": v(-5.2, -16.72) * mm});
            skArc(sketch, "E2107", {"start": v(-5.2, -16.72) * mm, "mid": v(-5.3, -16.65) * mm, "end": v(-5.4, -16.6) * mm});
            skArc(sketch, "E2108", {"start": v(-5.4, -16.6) * mm, "mid": v(-5.47, -16.54) * mm, "end": v(-5.55, -16.48) * mm});
            skArc(sketch, "E2109", {"start": v(-5.55, -16.48) * mm, "mid": v(-5.56, -16.47) * mm, "end": v(-5.57, -16.45) * mm});
            skArc(sketch, "E2110", {"start": v(-5.57, -16.45) * mm, "mid": v(-5.56, -16.41) * mm, "end": v(-5.53, -16.38) * mm});
            skArc(sketch, "E2111", {"start": v(-5.53, -16.38) * mm, "mid": v(-5.27, -16.21) * mm, "end": v(-5.02, -16.05) * mm});
            skArc(sketch, "E2112", {"start": v(-5.02, -16.05) * mm, "mid": v(-4.77, -15.89) * mm, "end": v(-4.51, -15.73) * mm});
            skArc(sketch, "E2113", {"start": v(-4.51, -15.73) * mm, "mid": v(-4.45, -15.7) * mm, "end": v(-4.38, -15.7) * mm});
            skArc(sketch, "E2114", {"start": v(-4.38, -15.7) * mm, "mid": v(-4.35, -15.7) * mm, "end": v(-4.32, -15.7) * mm});
            skArc(sketch, "E2115", {"start": v(-4.32, -15.7) * mm, "mid": v(-4.2, -15.77) * mm, "end": v(-4.07, -15.83) * mm});
            skArc(sketch, "E2116", {"start": v(-4.07, -15.83) * mm, "mid": v(-3.92, -15.9) * mm, "end": v(-3.78, -15.99) * mm});
            skArc(sketch, "E2117", {"start": v(-3.78, -15.99) * mm, "mid": v(-3.61, -16.08) * mm, "end": v(-3.45, -16.17) * mm});
            skArc(sketch, "E2118", {"start": v(-8.5, -16.72) * mm, "mid": v(-8.35, -16.76) * mm, "end": v(-8.21, -16.81) * mm});
            skArc(sketch, "E2119", {"start": v(-8.21, -16.81) * mm, "mid": v(-8.1, -16.86) * mm, "end": v(-8, -16.9) * mm});
            skArc(sketch, "E2120", {"start": v(-8, -16.9) * mm, "mid": v(-7.91, -16.95) * mm, "end": v(-7.83, -17) * mm});
            skArc(sketch, "E2121", {"start": v(-7.83, -17) * mm, "mid": v(-7.82, -17) * mm, "end": v(-7.83, -17.03) * mm});
            skArc(sketch, "E2122", {"start": v(-7.83, -17.03) * mm, "mid": v(-7.93, -17.12) * mm, "end": v(-8.04, -17.19) * mm});
            skArc(sketch, "E2123", {"start": v(-8.04, -17.19) * mm, "mid": v(-8.33, -17.35) * mm, "end": v(-8.62, -17.5) * mm});
            skArc(sketch, "E2124", {"start": v(-8.62, -17.5) * mm, "mid": v(-8.94, -17.66) * mm, "end": v(-9.26, -17.82) * mm});
            skArc(sketch, "E2125", {"start": v(-9.26, -17.82) * mm, "mid": v(-9.56, -17.96) * mm, "end": v(-9.86, -18.1) * mm});
            skArc(sketch, "E2126", {"start": v(-9.86, -18.1) * mm, "mid": v(-10.2, -18.23) * mm, "end": v(-10.54, -18.35) * mm});
            skArc(sketch, "E2127", {"start": v(-10.54, -18.35) * mm, "mid": v(-10.93, -18.48) * mm, "end": v(-11.33, -18.6) * mm});
            skArc(sketch, "E2128", {"start": v(-11.33, -18.6) * mm, "mid": v(-11.7, -18.7) * mm, "end": v(-12.08, -18.78) * mm});
            skArc(sketch, "E2129", {"start": v(-12.08, -18.78) * mm, "mid": v(-12.31, -18.82) * mm, "end": v(-12.55, -18.83) * mm});
            skArc(sketch, "E2130", {"start": v(-12.55, -18.83) * mm, "mid": v(-12.62, -18.83) * mm, "end": v(-12.7, -18.82) * mm});
            skArc(sketch, "E2131", {"start": v(-12.7, -18.82) * mm, "mid": v(-12.73, -18.8) * mm, "end": v(-12.76, -18.78) * mm});
            skArc(sketch, "E2132", {"start": v(-12.76, -18.78) * mm, "mid": v(-12.79, -18.75) * mm, "end": v(-12.8, -18.7) * mm});
            skArc(sketch, "E2133", {"start": v(-12.8, -18.7) * mm, "mid": v(-12.8, -18.62) * mm, "end": v(-12.8, -18.54) * mm});
            skArc(sketch, "E2134", {"start": v(-12.8, -18.54) * mm, "mid": v(-12.8, -18.38) * mm, "end": v(-12.77, -18.22) * mm});
            skArc(sketch, "E2135", {"start": v(-12.77, -18.22) * mm, "mid": v(-12.71, -18.05) * mm, "end": v(-12.64, -17.87) * mm});
            skArc(sketch, "E2136", {"start": v(-12.64, -17.87) * mm, "mid": v(-12.55, -17.7) * mm, "end": v(-12.45, -17.53) * mm});
            skArc(sketch, "E2137", {"start": v(-12.45, -17.53) * mm, "mid": v(-12.34, -17.37) * mm, "end": v(-12.2, -17.23) * mm});
            skArc(sketch, "E2138", {"start": v(-12.2, -17.23) * mm, "mid": v(-11.88, -16.94) * mm, "end": v(-11.5, -16.71) * mm});
            skArc(sketch, "E2139", {"start": v(-11.5, -16.71) * mm, "mid": v(-11.09, -16.55) * mm, "end": v(-10.65, -16.45) * mm});
            skArc(sketch, "E2140", {"start": v(-10.65, -16.45) * mm, "mid": v(-10.14, -16.41) * mm, "end": v(-9.64, -16.45) * mm});
            skArc(sketch, "E2141", {"start": v(-9.64, -16.45) * mm, "mid": v(-9.06, -16.56) * mm, "end": v(-8.5, -16.72) * mm});
            skArc(sketch, "E2142", {"start": v(5.53, -17.02) * mm, "mid": v(6.02, -17.18) * mm, "end": v(6.52, -17.33) * mm});
            skArc(sketch, "E2143", {"start": v(6.52, -17.33) * mm, "mid": v(6.94, -17.43) * mm, "end": v(7.36, -17.5) * mm});
            skArc(sketch, "E2144", {"start": v(7.36, -17.5) * mm, "mid": v(7.8, -17.55) * mm, "end": v(8.26, -17.58) * mm});
            skArc(sketch, "E2145", {"start": v(8.26, -17.58) * mm, "mid": v(8.83, -17.58) * mm, "end": v(9.4, -17.57) * mm});
            skArc(sketch, "E2146", {"start": v(9.4, -17.57) * mm, "mid": v(9.77, -17.56) * mm, "end": v(10.14, -17.55) * mm});
            skArc(sketch, "E2147", {"start": v(10.14, -17.55) * mm, "mid": v(10.36, -17.55) * mm, "end": v(10.58, -17.56) * mm});
            skArc(sketch, "E2148", {"start": v(10.58, -17.56) * mm, "mid": v(10.72, -17.57) * mm, "end": v(10.86, -17.58) * mm});
            skArc(sketch, "E2149", {"start": v(10.86, -17.58) * mm, "mid": v(10.9, -17.6) * mm, "end": v(10.9, -17.64) * mm});
            skArc(sketch, "E2150", {"start": v(10.9, -17.64) * mm, "mid": v(10.9, -17.67) * mm, "end": v(10.9, -17.7) * mm});
            skArc(sketch, "E2151", {"start": v(10.9, -17.7) * mm, "mid": v(10.88, -17.78) * mm, "end": v(10.87, -17.86) * mm});
            skArc(sketch, "E2152", {"start": v(10.87, -17.86) * mm, "mid": v(10.84, -17.95) * mm, "end": v(10.82, -18.03) * mm});
            skArc(sketch, "E2153", {"start": v(10.82, -18.03) * mm, "mid": v(10.8, -18.13) * mm, "end": v(10.77, -18.22) * mm});
            skArc(sketch, "E2154", {"start": v(10.77, -18.22) * mm, "mid": v(10.66, -18.5) * mm, "end": v(10.5, -18.75) * mm});
            skArc(sketch, "E2155", {"start": v(10.5, -18.75) * mm, "mid": v(10.3, -19) * mm, "end": v(10.06, -19.2) * mm});
            skArc(sketch, "E2156", {"start": v(10.06, -19.2) * mm, "mid": v(9.76, -19.4) * mm, "end": v(9.44, -19.57) * mm});
            skArc(sketch, "E2157", {"start": v(9.44, -19.57) * mm, "mid": v(9.06, -19.73) * mm, "end": v(8.67, -19.85) * mm});
            skArc(sketch, "E2158", {"start": v(8.67, -19.85) * mm, "mid": v(8.08, -19.96) * mm, "end": v(7.48, -19.97) * mm});
            skArc(sketch, "E2159", {"start": v(7.48, -19.97) * mm, "mid": v(6.76, -19.89) * mm, "end": v(6.06, -19.74) * mm});
            skArc(sketch, "E2160", {"start": v(6.06, -19.74) * mm, "mid": v(5.31, -19.51) * mm, "end": v(4.59, -19.22) * mm});
            skArc(sketch, "E2161", {"start": v(4.59, -19.22) * mm, "mid": v(3.88, -18.85) * mm, "end": v(3.2, -18.43) * mm});
            skLineSegment(sketch, "E2162", {"start": v(3.2, -18.43) * mm, "end": v(2.8, -18.14) * mm});
            skLineSegment(sketch, "E2163", {"start": v(2.8, -18.14) * mm, "end": v(3.02, -17.92) * mm});
            skArc(sketch, "E2164", {"start": v(3.02, -17.92) * mm, "mid": v(3.13, -17.82) * mm, "end": v(3.25, -17.72) * mm});
            skArc(sketch, "E2165", {"start": v(3.25, -17.72) * mm, "mid": v(3.57, -17.5) * mm, "end": v(3.9, -17.27) * mm});
            skArc(sketch, "E2166", {"start": v(3.9, -17.27) * mm, "mid": v(4.23, -17.03) * mm, "end": v(4.58, -16.8) * mm});
            skArc(sketch, "E2167", {"start": v(4.58, -16.8) * mm, "mid": v(4.64, -16.76) * mm, "end": v(4.7, -16.74) * mm});
            skArc(sketch, "E2168", {"start": v(4.7, -16.74) * mm, "mid": v(4.71, -16.74) * mm, "end": v(4.72, -16.74) * mm});
            skArc(sketch, "E2169", {"start": v(4.72, -16.74) * mm, "mid": v(4.84, -16.78) * mm, "end": v(4.96, -16.82) * mm});
            skArc(sketch, "E2170", {"start": v(4.96, -16.82) * mm, "mid": v(5.1, -16.87) * mm, "end": v(5.22, -16.91) * mm});
            skArc(sketch, "E2171", {"start": v(5.22, -16.91) * mm, "mid": v(5.38, -16.97) * mm, "end": v(5.53, -17.02) * mm});
            skArc(sketch, "E2172", {"start": v(-0.43, -18.03) * mm, "mid": v(-0.2, -18.17) * mm, "end": v(0.01, -18.31) * mm});
            skArc(sketch, "E2173", {"start": v(0.01, -18.31) * mm, "mid": v(0.2, -18.43) * mm, "end": v(0.38, -18.56) * mm});
            skArc(sketch, "E2174", {"start": v(0.38, -18.56) * mm, "mid": v(0.54, -18.67) * mm, "end": v(0.7, -18.78) * mm});
            skArc(sketch, "E2175", {"start": v(0.7, -18.78) * mm, "mid": v(0.71, -18.8) * mm, "end": v(0.72, -18.83) * mm});
            skArc(sketch, "E2176", {"start": v(0.72, -18.83) * mm, "mid": v(0.7, -18.87) * mm, "end": v(0.68, -18.91) * mm});
            skArc(sketch, "E2177", {"start": v(0.68, -18.91) * mm, "mid": v(0.38, -19.18) * mm, "end": v(0.07, -19.44) * mm});
            skArc(sketch, "E2178", {"start": v(0.07, -19.44) * mm, "mid": v(-0.22, -19.7) * mm, "end": v(-0.52, -19.94) * mm});
            skArc(sketch, "E2179", {"start": v(-0.52, -19.94) * mm, "mid": v(-0.58, -19.99) * mm, "end": v(-0.65, -20.01) * mm});
            skArc(sketch, "E2180", {"start": v(-0.65, -20.01) * mm, "mid": v(-0.7, -20.01) * mm, "end": v(-0.75, -19.99) * mm});
            skArc(sketch, "E2181", {"start": v(-0.75, -19.99) * mm, "mid": v(-1.33, -19.54) * mm, "end": v(-1.9, -19.08) * mm});
            skArc(sketch, "E2182", {"start": v(-1.9, -19.08) * mm, "mid": v(-2.48, -18.63) * mm, "end": v(-3.05, -18.18) * mm});
            skArc(sketch, "E2183", {"start": v(-3.05, -18.18) * mm, "mid": v(-3.08, -18.14) * mm, "end": v(-3.1, -18.08) * mm});
            skArc(sketch, "E2184", {"start": v(-3.1, -18.08) * mm, "mid": v(-3.08, -18.02) * mm, "end": v(-3.03, -17.97) * mm});
            skArc(sketch, "E2185", {"start": v(-3.03, -17.97) * mm, "mid": v(-2.73, -17.79) * mm, "end": v(-2.44, -17.61) * mm});
            skArc(sketch, "E2186", {"start": v(-2.44, -17.61) * mm, "mid": v(-2.14, -17.44) * mm, "end": v(-1.84, -17.27) * mm});
            skArc(sketch, "E2187", {"start": v(-1.84, -17.27) * mm, "mid": v(-1.77, -17.25) * mm, "end": v(-1.69, -17.26) * mm});
            skArc(sketch, "E2188", {"start": v(-1.69, -17.26) * mm, "mid": v(-1.65, -17.28) * mm, "end": v(-1.6, -17.3) * mm});
            skArc(sketch, "E2189", {"start": v(-1.6, -17.3) * mm, "mid": v(-1.44, -17.4) * mm, "end": v(-1.27, -17.5) * mm});
            skArc(sketch, "E2190", {"start": v(-1.27, -17.5) * mm, "mid": v(-1.07, -17.62) * mm, "end": v(-0.87, -17.75) * mm});
            skArc(sketch, "E2191", {"start": v(-0.87, -17.75) * mm, "mid": v(-0.65, -17.89) * mm, "end": v(-0.43, -18.03) * mm});
            skArc(sketch, "E2192", {"start": v(-6.18, -17.9) * mm, "mid": v(-6.02, -18) * mm, "end": v(-5.87, -18.1) * mm});
            skArc(sketch, "E2193", {"start": v(-5.87, -18.1) * mm, "mid": v(-5.74, -18.19) * mm, "end": v(-5.61, -18.27) * mm});
            skArc(sketch, "E2194", {"start": v(-5.61, -18.27) * mm, "mid": v(-5.5, -18.35) * mm, "end": v(-5.4, -18.43) * mm});
            skArc(sketch, "E2195", {"start": v(-5.4, -18.43) * mm, "mid": v(-5.38, -18.44) * mm, "end": v(-5.38, -18.46) * mm});
            skArc(sketch, "E2196", {"start": v(-5.38, -18.46) * mm, "mid": v(-5.4, -18.54) * mm, "end": v(-5.46, -18.59) * mm});
            skArc(sketch, "E2197", {"start": v(-5.46, -18.59) * mm, "mid": v(-6.09, -18.87) * mm, "end": v(-6.72, -19.15) * mm});
            skArc(sketch, "E2198", {"start": v(-6.72, -19.15) * mm, "mid": v(-7.3, -19.4) * mm, "end": v(-7.88, -19.65) * mm});
            skArc(sketch, "E2199", {"start": v(-7.88, -19.65) * mm, "mid": v(-8.23, -19.78) * mm, "end": v(-8.57, -19.88) * mm});
            skArc(sketch, "E2200", {"start": v(-8.57, -19.88) * mm, "mid": v(-9.11, -20) * mm, "end": v(-9.65, -20.1) * mm});
            skArc(sketch, "E2201", {"start": v(-9.65, -20.1) * mm, "mid": v(-10.15, -20.14) * mm, "end": v(-10.64, -20.14) * mm});
            skArc(sketch, "E2202", {"start": v(-10.64, -20.14) * mm, "mid": v(-11.07, -20.1) * mm, "end": v(-11.5, -20.03) * mm});
            skArc(sketch, "E2203", {"start": v(-11.5, -20.03) * mm, "mid": v(-11.83, -19.93) * mm, "end": v(-12.14, -19.77) * mm});
            skLineSegment(sketch, "E2204", {"start": v(-12.14, -19.77) * mm, "end": v(-12.48, -19.56) * mm});
            skLineSegment(sketch, "E2205", {"start": v(-12.48, -19.56) * mm, "end": v(-11.67, -19.4) * mm});
            skArc(sketch, "E2206", {"start": v(-11.67, -19.4) * mm, "mid": v(-11.5, -19.36) * mm, "end": v(-11.32, -19.32) * mm});
            skArc(sketch, "E2207", {"start": v(-11.32, -19.32) * mm, "mid": v(-11.14, -19.28) * mm, "end": v(-10.95, -19.23) * mm});
            skArc(sketch, "E2208", {"start": v(-10.95, -19.23) * mm, "mid": v(-10.79, -19.19) * mm, "end": v(-10.62, -19.14) * mm});
            skArc(sketch, "E2209", {"start": v(-10.62, -19.14) * mm, "mid": v(-10.5, -19.1) * mm, "end": v(-10.38, -19.07) * mm});
            skArc(sketch, "E2210", {"start": v(-10.38, -19.07) * mm, "mid": v(-10.1, -18.97) * mm, "end": v(-9.84, -18.86) * mm});
            skArc(sketch, "E2211", {"start": v(-9.84, -18.86) * mm, "mid": v(-9.43, -18.66) * mm, "end": v(-9.03, -18.47) * mm});
            skArc(sketch, "E2212", {"start": v(-9.03, -18.47) * mm, "mid": v(-8.61, -18.26) * mm, "end": v(-8.2, -18.05) * mm});
            skArc(sketch, "E2213", {"start": v(-8.2, -18.05) * mm, "mid": v(-7.9, -17.88) * mm, "end": v(-7.61, -17.7) * mm});
            skArc(sketch, "E2214", {"start": v(-7.61, -17.7) * mm, "mid": v(-7.52, -17.65) * mm, "end": v(-7.43, -17.6) * mm});
            skArc(sketch, "E2215", {"start": v(-7.43, -17.6) * mm, "mid": v(-7.34, -17.54) * mm, "end": v(-7.26, -17.5) * mm});
            skArc(sketch, "E2216", {"start": v(-7.26, -17.5) * mm, "mid": v(-7.18, -17.46) * mm, "end": v(-7.11, -17.42) * mm});
            skArc(sketch, "E2217", {"start": v(-7.11, -17.42) * mm, "mid": v(-7.09, -17.41) * mm, "end": v(-7.06, -17.4) * mm});
            skArc(sketch, "E2218", {"start": v(-7.06, -17.4) * mm, "mid": v(-7.03, -17.4) * mm, "end": v(-7, -17.42) * mm});
            skArc(sketch, "E2219", {"start": v(-7, -17.42) * mm, "mid": v(-6.88, -17.49) * mm, "end": v(-6.76, -17.55) * mm});
            skArc(sketch, "E2220", {"start": v(-6.76, -17.55) * mm, "mid": v(-6.63, -17.63) * mm, "end": v(-6.49, -17.71) * mm});
            skArc(sketch, "E2221", {"start": v(-6.49, -17.71) * mm, "mid": v(-6.33, -17.8) * mm, "end": v(-6.18, -17.9) * mm});
            skSolve(sketch);
        }
        {
            var Q0;
            Q0 = qSketchRegion(id + "F12", true);
            extrude(context, id + "F13", {"entities" : qUnion([Q0]), "operationType" : NewBodyOperationType.ADD, "depth" : 1.59 * mm, "offsetDistance" : 25.4 * mm});
        }
        {
            var Q0;
            {var subQ481=makeQuery(id+"F3.opExtrude","SWEPT_FACE",FACE,{"disambiguationData":[OSD([sQuery(id+"F2.wireOp",EDGE,"E5.bottom")])]});Q0=makeQuery(id+"F13.boolean.opBoolean","SPLIT",FACE,{"disambiguationData":[TD([subQ481])],"derivedFrom":makeQuery(id+"F11.boolean.opBoolean","SPLIT",FACE,{"disambiguationData":[TD([subQ481])],"derivedFrom":makeQuery(id+"F9.boolean.opBoolean","SPLIT",FACE,{"disambiguationData":[TD([subQ481])],"derivedFrom":makeQuery(id+"F7.boolean.opBoolean","SPLIT",FACE,{"disambiguationData":[TD([subQ481])],"derivedFrom":makeQuery(id+"F5.boolean.opBoolean","SPLIT",FACE,{"disambiguationData":[TD([subQ481])],"derivedFrom":makeQuery(id+"F1.opExtrude","CAP_FACE",FACE,{"disambiguationData":[OSD([sQuery(id+"F0.wireOp",EDGE,"E0.bottom"),sQuery(id+"F0.wireOp",EDGE,"E0.top"),sQuery(id+"F0.wireOp",EDGE,"E0.left"),sQuery(id+"F0.wireOp",EDGE,"E0.right"),sQuery(id+"F0.wireOp",EDGE,"E1.filletArc"),sQuery(id+"F0.wireOp",EDGE,"E2.filletArc"),sQuery(id+"F0.wireOp",EDGE,"E3.filletArc"),sQuery(id+"F0.wireOp",EDGE,"E4.filletArc")])],"isStart":false})})})})})});}
            var sketch = newSketch(context, id + "F14", { "sketchPlane" : qUnion([Q0])});
            skText(sketch, "E2222", { "text": "take a book", "fontName": "RobotoSlab-Regular.ttf"});
            skText(sketch, "E2223", { "text": "leave a book", "fontName": "RobotoSlab-Regular.ttf"});
            const initialGuessF14  = {"E2222": [-0.0635, -0.03175, 1, 0, 0.00838], "E2223": [-0.00506, -0.04128, 1, 0, 0.00838]};
            skSetInitialGuess(sketch, initialGuessF14);
            skSolve(sketch);
        }
        {
            var Q0;
            Q0 = qSketchRegion(id + "F14", true);
            extrude(context, id + "F15", {"entities" : qUnion([Q0]), "operationType" : NewBodyOperationType.ADD, "depth" : 1.59 * mm, "offsetDistance" : 25.4 * mm});
        }
        {
            var Q0;
            {var subQ538=makeQuery(id+"F3.opExtrude","SWEPT_FACE",FACE,{"disambiguationData":[OSD([sQuery(id+"F2.wireOp",EDGE,"E5.bottom")])]});Q0=makeQuery(id+"F15.boolean.opBoolean","SPLIT",FACE,{"disambiguationData":[TD([subQ538])],"derivedFrom":makeQuery(id+"F13.boolean.opBoolean","SPLIT",FACE,{"disambiguationData":[TD([subQ538])],"derivedFrom":makeQuery(id+"F11.boolean.opBoolean","SPLIT",FACE,{"disambiguationData":[TD([subQ538])],"derivedFrom":makeQuery(id+"F9.boolean.opBoolean","SPLIT",FACE,{"disambiguationData":[TD([subQ538])],"derivedFrom":makeQuery(id+"F7.boolean.opBoolean","SPLIT",FACE,{"disambiguationData":[TD([subQ538])],"derivedFrom":makeQuery(id+"F5.boolean.opBoolean","SPLIT",FACE,{"disambiguationData":[TD([subQ538])],"derivedFrom":makeQuery(id+"F1.opExtrude","CAP_FACE",FACE,{"disambiguationData":[OSD([sQuery(id+"F0.wireOp",EDGE,"E0.bottom"),sQuery(id+"F0.wireOp",EDGE,"E0.top"),sQuery(id+"F0.wireOp",EDGE,"E0.left"),sQuery(id+"F0.wireOp",EDGE,"E0.right"),sQuery(id+"F0.wireOp",EDGE,"E1.filletArc"),sQuery(id+"F0.wireOp",EDGE,"E2.filletArc"),sQuery(id+"F0.wireOp",EDGE,"E3.filletArc"),sQuery(id+"F0.wireOp",EDGE,"E4.filletArc")])],"isStart":false})})})})})})});}
            var sketch = newSketch(context, id + "F16", { "sketchPlane" : qUnion([Q0])});
            skCircle(sketch, "E2224", {"center": v(-65.88, 40.48) * mm, "radius": 1.98 * mm});
            skLineSegment(sketch, "E2225.bottom", {"start": v(-65.88, 40.48) * mm, "end": v(65.88, 40.48) * mm, "construction": true});
            skLineSegment(sketch, "E2225.top", {"start": v(-65.88, -40.48) * mm, "end": v(65.88, -40.48) * mm, "construction": true});
            skLineSegment(sketch, "E2225.left", {"start": v(-65.88, 40.48) * mm, "end": v(-65.88, -40.48) * mm, "construction": true});
            skLineSegment(sketch, "E2225.right", {"start": v(65.88, 40.48) * mm, "end": v(65.88, -40.48) * mm, "construction": true});
            skPoint(sketch, "E2225.middle", {"position": v(0, 0) * mm});
            skCircle(sketch, "E2226", {"center": v(65.88, 40.48) * mm, "radius": 1.98 * mm});
            skCircle(sketch, "E2227", {"center": v(65.88, -40.48) * mm, "radius": 1.98 * mm});
            skCircle(sketch, "E2228", {"center": v(-65.88, -40.48) * mm, "radius": 1.98 * mm});
            skSolve(sketch);
        }
        {
            var Q0;
            Q0 = qSketchRegion(id + "F16", true);
            extrude(context, id + "F17", {"entities" : qUnion([Q0]), "operationType" : NewBodyOperationType.REMOVE, "endBound" : BoundingType.THROUGH_ALL, "oppositeDirection" : true, "depth" : 25.4 * mm, "offsetDistance" : 25.4 * mm});
        }
        {
            var Q0;
            Q0=makeQuery(id+"F1.opExtrude","CAP_FACE",FACE,{"disambiguationData":[OSD([sQuery(id+"F0.wireOp",EDGE,"E0.bottom"),sQuery(id+"F0.wireOp",EDGE,"E0.top"),sQuery(id+"F0.wireOp",EDGE,"E0.left"),sQuery(id+"F0.wireOp",EDGE,"E0.right"),sQuery(id+"F0.wireOp",EDGE,"E1.filletArc"),sQuery(id+"F0.wireOp",EDGE,"E2.filletArc"),sQuery(id+"F0.wireOp",EDGE,"E3.filletArc"),sQuery(id+"F0.wireOp",EDGE,"E4.filletArc")])],"isStart":true});
            var sketch = newSketch(context, id + "F18", { "sketchPlane" : qUnion([Q0])});
            skArc(sketch, "E2229", {"start": v(-51.76, 55.67) * mm, "mid": v(-57.88, 60.64) * mm, "end": v(-61.79, 53.8) * mm});
            skArc(sketch, "E2230", {"start": v(-55.13, 53.9) * mm, "mid": v(-56.44, 57.97) * mm, "end": v(-59.24, 54.72) * mm});
            skArc(sketch, "E2231", {"start": v(-61.79, 53.8) * mm, "mid": v(-60.05, 52.98) * mm, "end": v(-59.24, 54.72) * mm});
            skLineSegment(sketch, "E2232", {"start": v(-56.93, 55.56) * mm, "end": v(-61.79, 53.8) * mm, "construction": true});
            skLineSegment(sketch, "E2233", {"start": v(-56.93, 55.56) * mm, "end": v(-67.77, 55.56) * mm, "construction": true});
            skArc(sketch, "E2234", {"start": v(-51.76, 55.67) * mm, "mid": v(-50.64, 52.58) * mm, "end": v(-47.87, 50.8) * mm});
            skArc(sketch, "E2235", {"start": v(-58.52, 50.8) * mm, "mid": v(-56.76, 52.28) * mm, "end": v(-55.13, 53.9) * mm});
            skLineSegment(sketch, "E2236", {"start": v(-58.52, 50.8) * mm, "end": v(-47.87, 50.8) * mm});
            skLineSegment(sketch, "E2237", {"start": v(0, 50.8) * mm, "end": v(0, 58.15) * mm, "construction": true});
            skLineSegment(sketch, "E2238.MirrorCS", {"start": v(56.93, 55.56) * mm, "end": v(61.79, 53.8) * mm, "construction": true});
            skLineSegment(sketch, "E2239.MirrorCS", {"start": v(56.93, 55.56) * mm, "end": v(67.77, 55.56) * mm, "construction": true});
            skArc(sketch, "E2240.MirrorCS", {"start": v(61.79, 53.8) * mm, "mid": v(60.05, 52.98) * mm, "end": v(59.24, 54.72) * mm});
            skArc(sketch, "E2241.MirrorCS", {"start": v(58.52, 50.8) * mm, "mid": v(56.76, 52.28) * mm, "end": v(55.13, 53.9) * mm});
            skArc(sketch, "E2242.MirrorCS", {"start": v(55.13, 53.9) * mm, "mid": v(56.44, 57.97) * mm, "end": v(59.24, 54.72) * mm});
            skArc(sketch, "E2243.MirrorCS", {"start": v(51.76, 55.67) * mm, "mid": v(57.88, 60.64) * mm, "end": v(61.79, 53.8) * mm});
            skArc(sketch, "E2244.MirrorCS", {"start": v(51.76, 55.67) * mm, "mid": v(50.64, 52.58) * mm, "end": v(47.87, 50.8) * mm});
            skLineSegment(sketch, "E2245.MirrorCS", {"start": v(58.52, 50.8) * mm, "end": v(47.87, 50.8) * mm});
            skSolve(sketch);
        }
        {
            var Q0;
            Q0=makeQuery(id+"F18.imprint","IMPRINT",FACE,{"disambiguationData":[TD([[makeQuery(id+"F18.imprint","IMPRINT",EDGE,{"derivedFrom":sQuery(id+"F18.wireOp",EDGE,"E2229")}),1.0]])]});
            var Q1;
            Q1=makeQuery(id+"F18.imprint","IMPRINT",FACE,{"disambiguationData":[TD([[makeQuery(id+"F18.imprint","IMPRINT",EDGE,{"derivedFrom":sQuery(id+"F18.wireOp",EDGE,"E2240.MirrorCS")}),-1.0]])]});
            extrude(context, id + "F19", {"entities" : qUnion([Q0, Q1]), "operationType" : NewBodyOperationType.ADD, "oppositeDirection" : true, "depth" : 3.17 * mm, "offsetDistance" : 25.4 * mm});
        }
        {
            var Q0;
            Q0=qCreatedBy(makeId("Front.planeOp"),FACE);
            var sketch = newSketch(context, id + "F20", { "sketchPlane" : qUnion([Q0])});
            skLineSegment(sketch, "E2246", {"start": v(-76.2, 69.85) * mm, "end": v(-70.97, 69.85) * mm});
            skLineSegment(sketch, "E2247", {"start": v(-76.2, 69.85) * mm, "end": v(-76.2, 76.2) * mm});
            skLineSegment(sketch, "E2248", {"start": v(-76.2, 76.2) * mm, "end": v(80.07, 76.2) * mm});
            skLineSegment(sketch, "E2249", {"start": v(-56.93, 55.56) * mm, "end": v(-56.93, 69.85) * mm, "construction": true});
            skLineSegment(sketch, "E2250", {"start": v(0, 50.8) * mm, "end": v(0, 61.94) * mm, "construction": true});
            skLineSegment(sketch, "E2251.bottom", {"start": v(80.07, 139.7) * mm, "end": v(86.42, 139.7) * mm});
            skLineSegment(sketch, "E2251.top", {"start": v(80.07, 44.45) * mm, "end": v(86.42, 44.45) * mm});
            skLineSegment(sketch, "E2251.left", {"start": v(80.07, 139.7) * mm, "end": v(80.07, 76.2) * mm});
            skLineSegment(sketch, "E2251.right", {"start": v(86.42, 139.7) * mm, "end": v(86.42, 44.45) * mm});
            skLineSegment(sketch, "E2252.trimOffspring", {"start": v(80.07, 69.85) * mm, "end": v(80.07, 44.45) * mm});
            skLineSegment(sketch, "E2253.0.0", {"start": v(-58.52, 50.8) * mm, "end": v(-47.87, 50.8) * mm, "construction": true});
            skArc(sketch, "E2253.0.1", {"start": v(-47.87, 50.8) * mm, "mid": v(-50.64, 52.58) * mm, "end": v(-51.76, 55.67) * mm, "construction": true});
            skArc(sketch, "E2253.0.2", {"start": v(-51.76, 55.67) * mm, "mid": v(-57.88, 60.64) * mm, "end": v(-61.79, 53.8) * mm, "construction": true});
            skArc(sketch, "E2253.0.3", {"start": v(-61.79, 53.8) * mm, "mid": v(-60.05, 52.98) * mm, "end": v(-59.24, 54.72) * mm, "construction": true});
            skArc(sketch, "E2253.0.4", {"start": v(-59.24, 54.72) * mm, "mid": v(-56.44, 57.97) * mm, "end": v(-55.13, 53.9) * mm, "construction": true});
            skArc(sketch, "E2253.0.5", {"start": v(-55.13, 53.9) * mm, "mid": v(-56.76, 52.28) * mm, "end": v(-58.52, 50.8) * mm, "construction": true});
            skArc(sketch, "E2253.1.0", {"start": v(58.52, 50.8) * mm, "mid": v(56.76, 52.28) * mm, "end": v(55.13, 53.9) * mm, "construction": true});
            skArc(sketch, "E2253.1.1", {"start": v(55.13, 53.9) * mm, "mid": v(56.44, 57.97) * mm, "end": v(59.24, 54.72) * mm, "construction": true});
            skArc(sketch, "E2253.1.2", {"start": v(59.24, 54.72) * mm, "mid": v(60.05, 52.98) * mm, "end": v(61.79, 53.8) * mm, "construction": true});
            skArc(sketch, "E2253.1.3", {"start": v(61.79, 53.8) * mm, "mid": v(57.88, 60.64) * mm, "end": v(51.76, 55.67) * mm, "construction": true});
            skArc(sketch, "E2253.1.4", {"start": v(51.76, 55.67) * mm, "mid": v(50.64, 52.58) * mm, "end": v(47.87, 50.8) * mm, "construction": true});
            skLineSegment(sketch, "E2253.1.5", {"start": v(47.87, 50.8) * mm, "end": v(58.52, 50.8) * mm, "construction": true});
            skArc(sketch, "E2254", {"start": v(48.67, 66.12) * mm, "mid": v(56.93, 60.79) * mm, "end": v(65.19, 66.12) * mm});
            skArc(sketch, "E2255.0", {"start": v(51.84, 69.85) * mm, "mid": v(56.93, 64.76) * mm, "end": v(62.02, 69.85) * mm});
            skArc(sketch, "E2256.MirrorCS", {"start": v(-51.84, 69.85) * mm, "mid": v(-56.93, 64.76) * mm, "end": v(-62.02, 69.85) * mm});
            skArc(sketch, "E2257.MirrorCS", {"start": v(-48.67, 66.12) * mm, "mid": v(-56.93, 60.79) * mm, "end": v(-65.19, 66.12) * mm});
            skLineSegment(sketch, "E2258.trimOffspring", {"start": v(-42.89, 69.85) * mm, "end": v(42.89, 69.85) * mm});
            skLineSegment(sketch, "E2259.trimOffspring", {"start": v(-62.02, 69.85) * mm, "end": v(-51.84, 69.85) * mm});
            skLineSegment(sketch, "E2260.trimOffspring", {"start": v(70.97, 69.85) * mm, "end": v(80.07, 69.85) * mm});
            skLineSegment(sketch, "E2261.trimOffspring", {"start": v(51.84, 69.85) * mm, "end": v(62.02, 69.85) * mm});
            skPoint(sketch, "E2262.visualSharp", {"position": v(47.87, 69.85) * mm});
            skArc(sketch, "E2262.filletArc", {"start": v(48.67, 66.12) * mm, "mid": v(46.33, 68.84) * mm, "end": v(42.89, 69.85) * mm});
            skPoint(sketch, "E2263.visualSharp", {"position": v(66, 69.85) * mm});
            skArc(sketch, "E2263.filletArc", {"start": v(70.97, 69.85) * mm, "mid": v(67.53, 68.84) * mm, "end": v(65.19, 66.12) * mm});
            skPoint(sketch, "E2264.visualSharp", {"position": v(-66, 69.85) * mm});
            skArc(sketch, "E2264.filletArc", {"start": v(-65.19, 66.12) * mm, "mid": v(-67.53, 68.84) * mm, "end": v(-70.97, 69.85) * mm});
            skPoint(sketch, "E2265.visualSharp", {"position": v(-47.87, 69.85) * mm});
            skArc(sketch, "E2265.filletArc", {"start": v(-42.89, 69.85) * mm, "mid": v(-46.33, 68.84) * mm, "end": v(-48.67, 66.12) * mm});
            skPoint(sketch, "E2266.orphan", {"position": v(88, 76.2) * mm});
            skPoint(sketch, "E2267.orphan", {"position": v(88, 69.85) * mm});
            skSolve(sketch);
        }
        {
            var Q0;
            Q0 = qSketchRegion(id + "F20", true);
            extrude(context, id + "F21", {"entities" : qUnion([Q0]), "endBound" : BoundingType.SYMMETRIC, "depth" : 12.7 * mm, "offsetDistance" : 25.4 * mm});
        }
        {
            var Q0;
            Q0=makeQuery(id+"F21.opExtrude","CAP_FACE",FACE,{"disambiguationData":[OSD([sQuery(id+"F20.wireOp",EDGE,"E2246"),sQuery(id+"F20.wireOp",EDGE,"E2247"),sQuery(id+"F20.wireOp",EDGE,"E2248"),sQuery(id+"F20.wireOp",EDGE,"E2251.bottom"),sQuery(id+"F20.wireOp",EDGE,"E2251.top"),sQuery(id+"F20.wireOp",EDGE,"E2251.left"),sQuery(id+"F20.wireOp",EDGE,"E2251.right"),sQuery(id+"F20.wireOp",EDGE,"E2252.trimOffspring"),sQuery(id+"F20.wireOp",EDGE,"E2254"),sQuery(id+"F20.wireOp",EDGE,"E2255.0"),sQuery(id+"F20.wireOp",EDGE,"E2256.MirrorCS"),sQuery(id+"F20.wireOp",EDGE,"E2257.MirrorCS"),sQuery(id+"F20.wireOp",EDGE,"E2258.trimOffspring"),sQuery(id+"F20.wireOp",EDGE,"E2259.trimOffspring"),sQuery(id+"F20.wireOp",EDGE,"E2260.trimOffspring"),sQuery(id+"F20.wireOp",EDGE,"E2261.trimOffspring"),sQuery(id+"F20.wireOp",EDGE,"E2262.filletArc"),sQuery(id+"F20.wireOp",EDGE,"E2263.filletArc"),sQuery(id+"F20.wireOp",EDGE,"E2264.filletArc"),sQuery(id+"F20.wireOp",EDGE,"E2265.filletArc")])],"isStart":false});
            var sketch = newSketch(context, id + "F22", { "sketchPlane" : qUnion([Q0])});
            skLineSegment(sketch, "E2268", {"start": v(67.64, 129.12) * mm, "end": v(69.78, 127.33) * mm});
            skArc(sketch, "E2269", {"start": v(69.78, 127.33) * mm, "mid": v(70.95, 126.27) * mm, "end": v(72.03, 125.12) * mm});
            skArc(sketch, "E2270", {"start": v(72.03, 125.12) * mm, "mid": v(73.24, 123.66) * mm, "end": v(74.38, 122.15) * mm});
            skArc(sketch, "E2271", {"start": v(74.38, 122.15) * mm, "mid": v(75.47, 120.56) * mm, "end": v(76.48, 118.93) * mm});
            skArc(sketch, "E2272", {"start": v(76.48, 118.93) * mm, "mid": v(77.28, 117.46) * mm, "end": v(77.97, 115.94) * mm});
            skArc(sketch, "E2273", {"start": v(77.97, 115.94) * mm, "mid": v(78.58, 114.33) * mm, "end": v(79.13, 112.7) * mm});
            skArc(sketch, "E2274", {"start": v(79.13, 112.7) * mm, "mid": v(79.56, 111.14) * mm, "end": v(79.9, 109.57) * mm});
            skArc(sketch, "E2275", {"start": v(79.9, 109.57) * mm, "mid": v(80.16, 107.94) * mm, "end": v(80.33, 106.3) * mm});
            skArc(sketch, "E2276", {"start": v(80.33, 106.3) * mm, "mid": v(80.43, 104.47) * mm, "end": v(80.46, 102.63) * mm});
            skArc(sketch, "E2277", {"start": v(80.46, 102.63) * mm, "mid": v(80.42, 100.83) * mm, "end": v(80.31, 99.02) * mm});
            skArc(sketch, "E2278", {"start": v(80.31, 99.02) * mm, "mid": v(80.16, 97.58) * mm, "end": v(79.9, 96.14) * mm});
            skArc(sketch, "E2279", {"start": v(79.9, 96.14) * mm, "mid": v(79.56, 94.74) * mm, "end": v(79.13, 93.36) * mm});
            skArc(sketch, "E2280", {"start": v(79.13, 93.36) * mm, "mid": v(78.51, 91.7) * mm, "end": v(77.84, 90.08) * mm});
            skArc(sketch, "E2281", {"start": v(77.84, 90.08) * mm, "mid": v(76.67, 87.74) * mm, "end": v(75.26, 85.53) * mm});
            skArc(sketch, "E2282", {"start": v(75.26, 85.53) * mm, "mid": v(73.67, 83.54) * mm, "end": v(71.87, 81.74) * mm});
            skArc(sketch, "E2283", {"start": v(71.87, 81.74) * mm, "mid": v(69.9, 80.17) * mm, "end": v(67.77, 78.84) * mm});
            skArc(sketch, "E2284", {"start": v(67.77, 78.84) * mm, "mid": v(65.5, 77.76) * mm, "end": v(63.11, 76.94) * mm});
            skArc(sketch, "E2285", {"start": v(63.11, 76.94) * mm, "mid": v(60.88, 76.44) * mm, "end": v(58.6, 76.2) * mm});
            skArc(sketch, "E2286", {"start": v(58.6, 76.2) * mm, "mid": v(55.94, 76.17) * mm, "end": v(53.3, 76.33) * mm});
            skArc(sketch, "E2287", {"start": v(53.3, 76.33) * mm, "mid": v(50.66, 76.68) * mm, "end": v(48.05, 77.23) * mm});
            skArc(sketch, "E2288", {"start": v(48.05, 77.23) * mm, "mid": v(45.85, 77.9) * mm, "end": v(43.73, 78.82) * mm});
            skArc(sketch, "E2289", {"start": v(43.73, 78.82) * mm, "mid": v(42.16, 79.71) * mm, "end": v(40.7, 80.76) * mm});
            skArc(sketch, "E2290", {"start": v(40.7, 80.76) * mm, "mid": v(39.22, 82.02) * mm, "end": v(37.85, 83.4) * mm});
            skArc(sketch, "E2291", {"start": v(37.85, 83.4) * mm, "mid": v(36.61, 84.87) * mm, "end": v(35.5, 86.43) * mm});
            skArc(sketch, "E2292", {"start": v(35.5, 86.43) * mm, "mid": v(34.65, 87.92) * mm, "end": v(33.97, 89.5) * mm});
            skArc(sketch, "E2293", {"start": v(33.97, 89.5) * mm, "mid": v(33.35, 90.88) * mm, "end": v(32.51, 92.14) * mm});
            skArc(sketch, "E2294", {"start": v(32.51, 92.14) * mm, "mid": v(31.5, 93.26) * mm, "end": v(30.32, 94.22) * mm});
            skArc(sketch, "E2295", {"start": v(30.32, 94.22) * mm, "mid": v(28.9, 95.05) * mm, "end": v(27.36, 95.68) * mm});
            skArc(sketch, "E2296", {"start": v(27.36, 95.68) * mm, "mid": v(25.54, 96.2) * mm, "end": v(23.68, 96.55) * mm});
            skLineSegment(sketch, "E2297", {"start": v(23.68, 96.55) * mm, "end": v(21.13, 96.9) * mm});
            skLineSegment(sketch, "E2298", {"start": v(21.13, 96.9) * mm, "end": v(22.66, 98.02) * mm});
            skArc(sketch, "E2299", {"start": v(22.66, 98.02) * mm, "mid": v(23.49, 98.55) * mm, "end": v(24.37, 98.96) * mm});
            skArc(sketch, "E2300", {"start": v(24.37, 98.96) * mm, "mid": v(25.3, 99.27) * mm, "end": v(26.28, 99.46) * mm});
            skArc(sketch, "E2301", {"start": v(26.28, 99.46) * mm, "mid": v(27.29, 99.53) * mm, "end": v(28.3, 99.48) * mm});
            skArc(sketch, "E2302", {"start": v(28.3, 99.48) * mm, "mid": v(29.34, 99.31) * mm, "end": v(30.36, 99.03) * mm});
            skArc(sketch, "E2303", {"start": v(30.36, 99.03) * mm, "mid": v(30.76, 98.9) * mm, "end": v(31.17, 98.77) * mm});
            skArc(sketch, "E2304", {"start": v(31.17, 98.77) * mm, "mid": v(31.52, 98.67) * mm, "end": v(31.86, 98.56) * mm});
            skArc(sketch, "E2305", {"start": v(31.86, 98.57) * mm, "mid": v(32.16, 98.48) * mm, "end": v(32.46, 98.4) * mm});
            skArc(sketch, "E2306", {"start": v(32.46, 98.4) * mm, "mid": v(32.5, 98.4) * mm, "end": v(32.52, 98.42) * mm});
            skArc(sketch, "E2307", {"start": v(32.52, 98.42) * mm, "mid": v(32.54, 98.46) * mm, "end": v(32.55, 98.5) * mm});
            skArc(sketch, "E2308", {"start": v(32.55, 98.5) * mm, "mid": v(32.61, 98.77) * mm, "end": v(32.68, 99.05) * mm});
            skArc(sketch, "E2309", {"start": v(32.68, 99.05) * mm, "mid": v(32.75, 99.37) * mm, "end": v(32.82, 99.7) * mm});
            skArc(sketch, "E2310", {"start": v(32.82, 99.7) * mm, "mid": v(32.9, 100.06) * mm, "end": v(32.98, 100.44) * mm});
            skArc(sketch, "E2311", {"start": v(32.98, 100.44) * mm, "mid": v(33.47, 102.24) * mm, "end": v(34.15, 103.97) * mm});
            skArc(sketch, "E2312", {"start": v(34.15, 103.97) * mm, "mid": v(35.03, 105.69) * mm, "end": v(36.08, 107.3) * mm});
            skArc(sketch, "E2313", {"start": v(36.08, 107.3) * mm, "mid": v(37.26, 108.8) * mm, "end": v(38.59, 110.15) * mm});
            skArc(sketch, "E2314", {"start": v(38.59, 110.15) * mm, "mid": v(39.97, 111.3) * mm, "end": v(41.48, 112.27) * mm});
            skArc(sketch, "E2315", {"start": v(41.48, 112.27) * mm, "mid": v(42.16, 112.63) * mm, "end": v(42.85, 112.96) * mm});
            skArc(sketch, "E2316", {"start": v(42.85, 112.96) * mm, "mid": v(43.39, 113.17) * mm, "end": v(43.94, 113.33) * mm});
            skArc(sketch, "E2317", {"start": v(43.94, 113.33) * mm, "mid": v(44.6, 113.45) * mm, "end": v(45.27, 113.53) * mm});
            skArc(sketch, "E2318", {"start": v(45.27, 113.53) * mm, "mid": v(46.46, 113.6) * mm, "end": v(47.66, 113.67) * mm});
            skArc(sketch, "E2319", {"start": v(47.66, 113.67) * mm, "mid": v(48.81, 113.71) * mm, "end": v(49.97, 113.74) * mm});
            skArc(sketch, "E2320", {"start": v(49.97, 113.74) * mm, "mid": v(50.66, 113.73) * mm, "end": v(51.35, 113.67) * mm});
            skArc(sketch, "E2321", {"start": v(51.35, 113.67) * mm, "mid": v(51.93, 113.57) * mm, "end": v(52.5, 113.42) * mm});
            skArc(sketch, "E2322", {"start": v(52.5, 113.42) * mm, "mid": v(53.18, 113.2) * mm, "end": v(53.86, 112.93) * mm});
            skArc(sketch, "E2323", {"start": v(53.86, 112.93) * mm, "mid": v(54.97, 112.42) * mm, "end": v(56.03, 111.81) * mm});
            skArc(sketch, "E2324", {"start": v(56.03, 111.81) * mm, "mid": v(57.04, 111.12) * mm, "end": v(57.99, 110.35) * mm});
            skArc(sketch, "E2325", {"start": v(57.99, 110.35) * mm, "mid": v(58.86, 109.5) * mm, "end": v(59.66, 108.59) * mm});
            skArc(sketch, "E2326", {"start": v(59.66, 108.59) * mm, "mid": v(60.37, 107.62) * mm, "end": v(60.99, 106.6) * mm});
            skArc(sketch, "E2327", {"start": v(60.99, 106.6) * mm, "mid": v(61.37, 105.87) * mm, "end": v(61.73, 105.14) * mm});
            skArc(sketch, "E2328", {"start": v(61.73, 105.14) * mm, "mid": v(61.93, 104.65) * mm, "end": v(62.08, 104.14) * mm});
            skArc(sketch, "E2329", {"start": v(62.08, 104.14) * mm, "mid": v(62.18, 103.6) * mm, "end": v(62.22, 103.05) * mm});
            skArc(sketch, "E2330", {"start": v(62.22, 103.05) * mm, "mid": v(62.24, 102.16) * mm, "end": v(62.24, 101.26) * mm});
            skArc(sketch, "E2331", {"start": v(62.24, 101.26) * mm, "mid": v(62.13, 99.66) * mm, "end": v(61.83, 98.08) * mm});
            skArc(sketch, "E2332", {"start": v(61.83, 98.08) * mm, "mid": v(61.38, 96.68) * mm, "end": v(60.73, 95.37) * mm});
            skArc(sketch, "E2333", {"start": v(60.73, 95.37) * mm, "mid": v(59.9, 94.18) * mm, "end": v(58.92, 93.13) * mm});
            skArc(sketch, "E2334", {"start": v(58.92, 93.13) * mm, "mid": v(57.72, 92.16) * mm, "end": v(56.4, 91.34) * mm});
            skArc(sketch, "E2335", {"start": v(56.4, 91.34) * mm, "mid": v(55.43, 90.9) * mm, "end": v(54.4, 90.62) * mm});
            skArc(sketch, "E2336", {"start": v(54.4, 90.62) * mm, "mid": v(53.2, 90.46) * mm, "end": v(51.98, 90.41) * mm});
            skArc(sketch, "E2337", {"start": v(51.98, 90.41) * mm, "mid": v(50.77, 90.5) * mm, "end": v(49.58, 90.7) * mm});
            skArc(sketch, "E2338", {"start": v(49.58, 90.7) * mm, "mid": v(48.59, 91.01) * mm, "end": v(47.66, 91.48) * mm});
            skArc(sketch, "E2339", {"start": v(47.66, 91.48) * mm, "mid": v(46.9, 91.98) * mm, "end": v(46.2, 92.53) * mm});
            skArc(sketch, "E2340", {"start": v(46.2, 92.53) * mm, "mid": v(45.61, 93.08) * mm, "end": v(45.1, 93.68) * mm});
            skArc(sketch, "E2341", {"start": v(45.1, 93.68) * mm, "mid": v(44.7, 94.28) * mm, "end": v(44.4, 94.91) * mm});
            skArc(sketch, "E2342", {"start": v(44.4, 94.91) * mm, "mid": v(44.2, 95.54) * mm, "end": v(44.1, 96.2) * mm});
            skArc(sketch, "E2343", {"start": v(44.1, 96.2) * mm, "mid": v(44.15, 97.1) * mm, "end": v(44.43, 97.97) * mm});
            skArc(sketch, "E2344", {"start": v(44.43, 97.97) * mm, "mid": v(44.91, 98.73) * mm, "end": v(45.57, 99.34) * mm});
            skArc(sketch, "E2345", {"start": v(45.57, 99.34) * mm, "mid": v(46.37, 99.76) * mm, "end": v(47.24, 99.95) * mm});
            skArc(sketch, "E2346", {"start": v(47.24, 99.95) * mm, "mid": v(48.14, 99.91) * mm, "end": v(49, 99.64) * mm});
            skArc(sketch, "E2347", {"start": v(49, 99.64) * mm, "mid": v(49.5, 99.37) * mm, "end": v(49.97, 99.04) * mm});
            skArc(sketch, "E2348", {"start": v(49.97, 99.04) * mm, "mid": v(50.33, 98.7) * mm, "end": v(50.62, 98.3) * mm});
            skArc(sketch, "E2349", {"start": v(50.62, 98.3) * mm, "mid": v(50.83, 97.84) * mm, "end": v(50.96, 97.36) * mm});
            skArc(sketch, "E2350", {"start": v(50.96, 97.36) * mm, "mid": v(51.03, 96.76) * mm, "end": v(51.04, 96.16) * mm});
            skArc(sketch, "E2351", {"start": v(51.04, 96.16) * mm, "mid": v(51.03, 95.71) * mm, "end": v(51.03, 95.26) * mm});
            skArc(sketch, "E2352", {"start": v(51.03, 95.26) * mm, "mid": v(51.07, 95.08) * mm, "end": v(51.18, 94.93) * mm});
            skArc(sketch, "E2353", {"start": v(51.18, 94.93) * mm, "mid": v(51.34, 94.82) * mm, "end": v(51.53, 94.77) * mm});
            skArc(sketch, "E2354", {"start": v(51.53, 94.77) * mm, "mid": v(52.02, 94.73) * mm, "end": v(52.52, 94.7) * mm});
            skArc(sketch, "E2355", {"start": v(52.52, 94.7) * mm, "mid": v(53.16, 94.74) * mm, "end": v(53.8, 94.87) * mm});
            skArc(sketch, "E2356", {"start": v(53.8, 94.87) * mm, "mid": v(54.45, 95.11) * mm, "end": v(55.07, 95.44) * mm});
            skArc(sketch, "E2357", {"start": v(55.07, 95.44) * mm, "mid": v(55.69, 95.87) * mm, "end": v(56.25, 96.36) * mm});
            skArc(sketch, "E2358", {"start": v(56.25, 96.36) * mm, "mid": v(56.8, 96.96) * mm, "end": v(57.27, 97.6) * mm});
            skArc(sketch, "E2359", {"start": v(57.27, 97.6) * mm, "mid": v(57.66, 98.32) * mm, "end": v(57.9, 99.1) * mm});
            skArc(sketch, "E2360", {"start": v(57.9, 99.1) * mm, "mid": v(58.05, 100.08) * mm, "end": v(58.1, 101.08) * mm});
            skArc(sketch, "E2361", {"start": v(58.1, 101.08) * mm, "mid": v(58.03, 102.13) * mm, "end": v(57.86, 103.16) * mm});
            skArc(sketch, "E2362", {"start": v(57.86, 103.16) * mm, "mid": v(57.6, 104.06) * mm, "end": v(57.2, 104.92) * mm});
            skArc(sketch, "E2363", {"start": v(57.2, 104.92) * mm, "mid": v(56.48, 106.05) * mm, "end": v(55.6, 107.06) * mm});
            skArc(sketch, "E2364", {"start": v(55.6, 107.06) * mm, "mid": v(54.52, 107.97) * mm, "end": v(53.33, 108.74) * mm});
            skArc(sketch, "E2365", {"start": v(53.33, 108.74) * mm, "mid": v(52.05, 109.35) * mm, "end": v(50.7, 109.79) * mm});
            skArc(sketch, "E2366", {"start": v(50.7, 109.79) * mm, "mid": v(49.35, 110.02) * mm, "end": v(47.98, 110.06) * mm});
            skArc(sketch, "E2367", {"start": v(47.98, 110.06) * mm, "mid": v(46.88, 109.96) * mm, "end": v(45.8, 109.75) * mm});
            skArc(sketch, "E2368", {"start": v(45.8, 109.75) * mm, "mid": v(44.79, 109.44) * mm, "end": v(43.82, 109.01) * mm});
            skArc(sketch, "E2369", {"start": v(43.82, 109.01) * mm, "mid": v(42.86, 108.46) * mm, "end": v(41.95, 107.8) * mm});
            skArc(sketch, "E2370", {"start": v(41.95, 107.8) * mm, "mid": v(41, 106.98) * mm, "end": v(40.12, 106.09) * mm});
            skArc(sketch, "E2371", {"start": v(40.12, 106.09) * mm, "mid": v(39.5, 105.4) * mm, "end": v(38.9, 104.69) * mm});
            skArc(sketch, "E2372", {"start": v(38.9, 104.69) * mm, "mid": v(38.51, 104.17) * mm, "end": v(38.16, 103.62) * mm});
            skArc(sketch, "E2373", {"start": v(38.16, 103.62) * mm, "mid": v(37.88, 103.09) * mm, "end": v(37.65, 102.52) * mm});
            skArc(sketch, "E2374", {"start": v(37.65, 102.52) * mm, "mid": v(37.4, 101.79) * mm, "end": v(37.2, 101.04) * mm});
            skArc(sketch, "E2375", {"start": v(37.2, 101.04) * mm, "mid": v(36.92, 99.79) * mm, "end": v(36.73, 98.52) * mm});
            skArc(sketch, "E2376", {"start": v(36.73, 98.52) * mm, "mid": v(36.64, 97.26) * mm, "end": v(36.64, 96) * mm});
            skArc(sketch, "E2377", {"start": v(36.64, 96) * mm, "mid": v(36.74, 94.78) * mm, "end": v(36.93, 93.56) * mm});
            skArc(sketch, "E2378", {"start": v(36.93, 93.56) * mm, "mid": v(37.21, 92.41) * mm, "end": v(37.6, 91.3) * mm});
            skArc(sketch, "E2379", {"start": v(37.6, 91.3) * mm, "mid": v(38, 90.3) * mm, "end": v(38.46, 89.3) * mm});
            skArc(sketch, "E2380", {"start": v(38.46, 89.3) * mm, "mid": v(38.88, 88.53) * mm, "end": v(39.36, 87.78) * mm});
            skArc(sketch, "E2381", {"start": v(39.36, 87.78) * mm, "mid": v(39.9, 87.05) * mm, "end": v(40.5, 86.36) * mm});
            skArc(sketch, "E2382", {"start": v(40.5, 86.36) * mm, "mid": v(41.31, 85.52) * mm, "end": v(42.15, 84.72) * mm});
            skArc(sketch, "E2383", {"start": v(42.15, 84.72) * mm, "mid": v(43.48, 83.62) * mm, "end": v(44.93, 82.67) * mm});
            skArc(sketch, "E2384", {"start": v(44.93, 82.67) * mm, "mid": v(46.5, 81.86) * mm, "end": v(48.15, 81.23) * mm});
            skArc(sketch, "E2385", {"start": v(48.15, 81.23) * mm, "mid": v(49.93, 80.74) * mm, "end": v(51.75, 80.43) * mm});
            skArc(sketch, "E2386", {"start": v(51.75, 80.43) * mm, "mid": v(53.72, 80.27) * mm, "end": v(55.68, 80.28) * mm});
            skArc(sketch, "E2387", {"start": v(55.68, 80.28) * mm, "mid": v(57.07, 80.37) * mm, "end": v(58.46, 80.52) * mm});
            skArc(sketch, "E2388", {"start": v(58.46, 80.52) * mm, "mid": v(59.64, 80.72) * mm, "end": v(60.8, 81) * mm});
            skArc(sketch, "E2389", {"start": v(60.8, 81) * mm, "mid": v(61.95, 81.36) * mm, "end": v(63.08, 81.8) * mm});
            skArc(sketch, "E2390", {"start": v(63.08, 81.8) * mm, "mid": v(64.36, 82.37) * mm, "end": v(65.6, 83) * mm});
            skArc(sketch, "E2391", {"start": v(65.6, 83) * mm, "mid": v(69.17, 85.44) * mm, "end": v(72.1, 88.6) * mm});
            skArc(sketch, "E2392", {"start": v(72.1, 88.6) * mm, "mid": v(74.4, 92.44) * mm, "end": v(75.9, 96.65) * mm});
            skArc(sketch, "E2393", {"start": v(75.9, 96.65) * mm, "mid": v(76.59, 101.3) * mm, "end": v(76.4, 105.99) * mm});
            skArc(sketch, "E2394", {"start": v(76.4, 105.99) * mm, "mid": v(75.36, 110.73) * mm, "end": v(73.54, 115.23) * mm});
            skArc(sketch, "E2395", {"start": v(73.54, 115.23) * mm, "mid": v(72.06, 117.8) * mm, "end": v(70.34, 120.22) * mm});
            skArc(sketch, "E2396", {"start": v(70.34, 120.22) * mm, "mid": v(68.33, 122.54) * mm, "end": v(66.13, 124.67) * mm});
            skArc(sketch, "E2397", {"start": v(66.13, 124.67) * mm, "mid": v(63.75, 126.58) * mm, "end": v(61.21, 128.27) * mm});
            skArc(sketch, "E2398", {"start": v(61.21, 128.27) * mm, "mid": v(58.63, 129.65) * mm, "end": v(55.92, 130.75) * mm});
            skArc(sketch, "E2399", {"start": v(55.92, 130.75) * mm, "mid": v(52.91, 131.64) * mm, "end": v(49.83, 132.23) * mm});
            skArc(sketch, "E2400", {"start": v(49.83, 132.23) * mm, "mid": v(46.37, 132.59) * mm, "end": v(42.9, 132.7) * mm});
            skArc(sketch, "E2401", {"start": v(42.9, 132.7) * mm, "mid": v(39.4, 132.54) * mm, "end": v(35.92, 132.14) * mm});
            skArc(sketch, "E2402", {"start": v(35.92, 132.14) * mm, "mid": v(32.73, 131.5) * mm, "end": v(29.6, 130.57) * mm});
            skArc(sketch, "E2403", {"start": v(29.6, 130.57) * mm, "mid": v(28.92, 130.32) * mm, "end": v(28.23, 130.04) * mm});
            skArc(sketch, "E2404", {"start": v(28.23, 130.04) * mm, "mid": v(27.7, 129.78) * mm, "end": v(27.2, 129.48) * mm});
            skArc(sketch, "E2405", {"start": v(27.2, 129.48) * mm, "mid": v(26.74, 129.16) * mm, "end": v(26.3, 128.8) * mm});
            skArc(sketch, "E2406", {"start": v(26.3, 128.8) * mm, "mid": v(25.8, 128.32) * mm, "end": v(25.33, 127.82) * mm});
            skArc(sketch, "E2407", {"start": v(25.33, 127.82) * mm, "mid": v(24.21, 126.4) * mm, "end": v(23.29, 124.86) * mm});
            skArc(sketch, "E2408", {"start": v(23.29, 124.86) * mm, "mid": v(22.51, 123.1) * mm, "end": v(21.93, 121.27) * mm});
            skArc(sketch, "E2409", {"start": v(21.93, 121.27) * mm, "mid": v(21.54, 119.3) * mm, "end": v(21.36, 117.32) * mm});
            skArc(sketch, "E2410", {"start": v(21.36, 117.32) * mm, "mid": v(21.39, 115.3) * mm, "end": v(21.62, 113.28) * mm});
            skArc(sketch, "E2411", {"start": v(21.62, 113.28) * mm, "mid": v(21.72, 112.7) * mm, "end": v(21.8, 112.1) * mm});
            skArc(sketch, "E2412", {"start": v(21.8, 112.1) * mm, "mid": v(21.88, 111.6) * mm, "end": v(21.95, 111.1) * mm});
            skArc(sketch, "E2413", {"start": v(21.95, 111.1) * mm, "mid": v(22, 110.66) * mm, "end": v(22.05, 110.22) * mm});
            skArc(sketch, "E2414", {"start": v(22.05, 110.22) * mm, "mid": v(22.04, 110.15) * mm, "end": v(22, 110.08) * mm});
            skArc(sketch, "E2415", {"start": v(22, 110.08) * mm, "mid": v(21.85, 110) * mm, "end": v(21.67, 110.05) * mm});
            skArc(sketch, "E2416", {"start": v(21.67, 110.05) * mm, "mid": v(21.08, 110.59) * mm, "end": v(20.5, 111.15) * mm});
            skArc(sketch, "E2417", {"start": v(20.5, 111.15) * mm, "mid": v(19.89, 111.77) * mm, "end": v(19.3, 112.42) * mm});
            skArc(sketch, "E2418", {"start": v(19.3, 112.42) * mm, "mid": v(18.83, 113.02) * mm, "end": v(18.4, 113.64) * mm});
            skArc(sketch, "E2419", {"start": v(18.4, 113.64) * mm, "mid": v(17.9, 114.53) * mm, "end": v(17.53, 115.49) * mm});
            skArc(sketch, "E2420", {"start": v(17.53, 115.49) * mm, "mid": v(17.23, 116.63) * mm, "end": v(17.03, 117.8) * mm});
            skArc(sketch, "E2421", {"start": v(17.03, 117.8) * mm, "mid": v(16.93, 119.02) * mm, "end": v(16.94, 120.24) * mm});
            skArc(sketch, "E2422", {"start": v(16.94, 120.24) * mm, "mid": v(17.06, 121.36) * mm, "end": v(17.3, 122.46) * mm});
            skArc(sketch, "E2423", {"start": v(17.3, 122.46) * mm, "mid": v(17.4, 122.84) * mm, "end": v(17.5, 123.23) * mm});
            skArc(sketch, "E2424", {"start": v(17.5, 123.23) * mm, "mid": v(17.57, 123.57) * mm, "end": v(17.63, 123.91) * mm});
            skArc(sketch, "E2425", {"start": v(17.63, 123.91) * mm, "mid": v(17.68, 124.2) * mm, "end": v(17.71, 124.48) * mm});
            skArc(sketch, "E2426", {"start": v(17.71, 124.48) * mm, "mid": v(17.7, 124.56) * mm, "end": v(17.66, 124.63) * mm});
            skArc(sketch, "E2427", {"start": v(17.66, 124.63) * mm, "mid": v(16.92, 124.89) * mm, "end": v(16.22, 124.55) * mm});
            skArc(sketch, "E2428", {"start": v(16.22, 124.55) * mm, "mid": v(12.2, 119.91) * mm, "end": v(8.22, 115.25) * mm});
            skArc(sketch, "E2429", {"start": v(8.22, 115.25) * mm, "mid": v(4.54, 110.82) * mm, "end": v(0.94, 106.33) * mm});
            skArc(sketch, "E2430", {"start": v(0.94, 106.33) * mm, "mid": v(-0.69, 103.98) * mm, "end": v(-2, 101.44) * mm});
            skArc(sketch, "E2431", {"start": v(-2, 101.44) * mm, "mid": v(-2.4, 100.38) * mm, "end": v(-2.66, 99.27) * mm});
            skArc(sketch, "E2432", {"start": v(-2.66, 99.27) * mm, "mid": v(-2.8, 98.07) * mm, "end": v(-2.83, 96.85) * mm});
            skArc(sketch, "E2433", {"start": v(-2.83, 96.85) * mm, "mid": v(-2.74, 95.65) * mm, "end": v(-2.52, 94.47) * mm});
            skArc(sketch, "E2434", {"start": v(-2.52, 94.47) * mm, "mid": v(-2.2, 93.42) * mm, "end": v(-1.74, 92.42) * mm});
            skArc(sketch, "E2435", {"start": v(-1.74, 92.42) * mm, "mid": v(-1.24, 91.6) * mm, "end": v(-0.64, 90.84) * mm});
            skArc(sketch, "E2436", {"start": v(-0.64, 90.84) * mm, "mid": v(0.08, 90.1) * mm, "end": v(0.87, 89.44) * mm});
            skArc(sketch, "E2437", {"start": v(0.87, 89.44) * mm, "mid": v(1.73, 88.86) * mm, "end": v(2.64, 88.36) * mm});
            skArc(sketch, "E2438", {"start": v(2.64, 88.36) * mm, "mid": v(3.55, 87.97) * mm, "end": v(4.5, 87.68) * mm});
            skArc(sketch, "E2439", {"start": v(4.5, 87.68) * mm, "mid": v(6.56, 87.44) * mm, "end": v(8.62, 87.71) * mm});
            skArc(sketch, "E2440", {"start": v(8.62, 87.71) * mm, "mid": v(10.45, 88.48) * mm, "end": v(12, 89.73) * mm});
            skArc(sketch, "E2441", {"start": v(12, 89.73) * mm, "mid": v(13.02, 91.26) * mm, "end": v(13.53, 93.03) * mm});
            skArc(sketch, "E2442", {"start": v(13.53, 93.03) * mm, "mid": v(13.46, 94.87) * mm, "end": v(12.8, 96.58) * mm});
            skArc(sketch, "E2443", {"start": v(12.8, 96.58) * mm, "mid": v(12.54, 97.02) * mm, "end": v(12.24, 97.43) * mm});
            skArc(sketch, "E2444", {"start": v(12.24, 97.43) * mm, "mid": v(12.04, 97.61) * mm, "end": v(11.78, 97.7) * mm});
            skArc(sketch, "E2445", {"start": v(11.78, 97.7) * mm, "mid": v(11.52, 97.7) * mm, "end": v(11.28, 97.59) * mm});
            skArc(sketch, "E2446", {"start": v(11.28, 97.59) * mm, "mid": v(10.9, 97.29) * mm, "end": v(10.56, 96.96) * mm});
            skArc(sketch, "E2447", {"start": v(10.56, 96.96) * mm, "mid": v(10.11, 96.6) * mm, "end": v(9.6, 96.33) * mm});
            skArc(sketch, "E2448", {"start": v(9.6, 96.33) * mm, "mid": v(9.03, 96.17) * mm, "end": v(8.44, 96.1) * mm});
            skArc(sketch, "E2449", {"start": v(8.44, 96.1) * mm, "mid": v(7.84, 96.16) * mm, "end": v(7.25, 96.32) * mm});
            skArc(sketch, "E2450", {"start": v(7.25, 96.32) * mm, "mid": v(6.72, 96.58) * mm, "end": v(6.24, 96.94) * mm});
            skArc(sketch, "E2451", {"start": v(6.24, 96.94) * mm, "mid": v(5.64, 97.7) * mm, "end": v(5.3, 98.6) * mm});
            skArc(sketch, "E2452", {"start": v(5.3, 98.6) * mm, "mid": v(5.27, 99.56) * mm, "end": v(5.54, 100.49) * mm});
            skArc(sketch, "E2453", {"start": v(5.54, 100.49) * mm, "mid": v(6.1, 101.34) * mm, "end": v(6.9, 101.99) * mm});
            skArc(sketch, "E2454", {"start": v(6.9, 101.99) * mm, "mid": v(7.87, 102.42) * mm, "end": v(8.93, 102.6) * mm});
            skArc(sketch, "E2455", {"start": v(8.93, 102.6) * mm, "mid": v(10.08, 102.56) * mm, "end": v(11.2, 102.34) * mm});
            skArc(sketch, "E2456", {"start": v(11.2, 102.34) * mm, "mid": v(12.32, 101.94) * mm, "end": v(13.36, 101.39) * mm});
            skArc(sketch, "E2457", {"start": v(13.36, 101.39) * mm, "mid": v(14.33, 100.69) * mm, "end": v(15.2, 99.86) * mm});
            skArc(sketch, "E2458", {"start": v(15.2, 99.86) * mm, "mid": v(15.91, 98.93) * mm, "end": v(16.5, 97.9) * mm});
            skArc(sketch, "E2459", {"start": v(16.5, 97.9) * mm, "mid": v(16.85, 97) * mm, "end": v(17.08, 96.06) * mm});
            skArc(sketch, "E2460", {"start": v(17.08, 96.06) * mm, "mid": v(17.22, 94.96) * mm, "end": v(17.27, 93.85) * mm});
            skArc(sketch, "E2461", {"start": v(17.27, 93.85) * mm, "mid": v(17.21, 92.73) * mm, "end": v(17.06, 91.62) * mm});
            skArc(sketch, "E2462", {"start": v(17.06, 91.62) * mm, "mid": v(16.82, 90.63) * mm, "end": v(16.47, 89.68) * mm});
            skArc(sketch, "E2463", {"start": v(16.47, 89.68) * mm, "mid": v(15.46, 87.93) * mm, "end": v(14.12, 86.43) * mm});
            skArc(sketch, "E2464", {"start": v(14.12, 86.43) * mm, "mid": v(12.46, 85.2) * mm, "end": v(10.6, 84.31) * mm});
            skArc(sketch, "E2465", {"start": v(10.6, 84.31) * mm, "mid": v(8.55, 83.78) * mm, "end": v(6.43, 83.65) * mm});
            skArc(sketch, "E2466", {"start": v(6.43, 83.65) * mm, "mid": v(4.28, 83.9) * mm, "end": v(2.21, 84.54) * mm});
            skArc(sketch, "E2467", {"start": v(2.21, 84.54) * mm, "mid": v(1.74, 84.74) * mm, "end": v(1.27, 84.95) * mm});
            skArc(sketch, "E2468", {"start": v(1.27, 84.95) * mm, "mid": v(0.8, 85.17) * mm, "end": v(0.33, 85.41) * mm});
            skArc(sketch, "E2469", {"start": v(0.33, 85.41) * mm, "mid": v(-0.07, 85.63) * mm, "end": v(-0.47, 85.86) * mm});
            skArc(sketch, "E2470", {"start": v(-0.47, 85.86) * mm, "mid": v(-0.71, 86.02) * mm, "end": v(-0.94, 86.2) * mm});
            skLineSegment(sketch, "E2471", {"start": v(-0.94, 86.2) * mm, "end": v(-1.79, 86.93) * mm});
            skLineSegment(sketch, "E2472", {"start": v(-1.79, 86.93) * mm, "end": v(-2.51, 85.63) * mm});
            skArc(sketch, "E2473", {"start": v(-2.51, 85.63) * mm, "mid": v(-3.23, 84.5) * mm, "end": v(-4.06, 83.45) * mm});
            skArc(sketch, "E2474", {"start": v(-4.06, 83.45) * mm, "mid": v(-4.93, 82.58) * mm, "end": v(-5.91, 81.83) * mm});
            skArc(sketch, "E2475", {"start": v(-5.91, 81.83) * mm, "mid": v(-6.95, 81.25) * mm, "end": v(-8.06, 80.81) * mm});
            skArc(sketch, "E2476", {"start": v(-8.06, 80.81) * mm, "mid": v(-9.24, 80.53) * mm, "end": v(-10.44, 80.4) * mm});
            skArc(sketch, "E2477", {"start": v(-10.44, 80.4) * mm, "mid": v(-11.46, 80.37) * mm, "end": v(-12.48, 80.37) * mm});
            skArc(sketch, "E2478", {"start": v(-12.48, 80.37) * mm, "mid": v(-12.77, 80.47) * mm, "end": v(-12.95, 80.7) * mm});
            skArc(sketch, "E2479", {"start": v(-12.95, 80.7) * mm, "mid": v(-12.96, 81) * mm, "end": v(-12.8, 81.26) * mm});
            skArc(sketch, "E2480", {"start": v(-12.8, 81.26) * mm, "mid": v(-12, 81.88) * mm, "end": v(-11.19, 82.48) * mm});
            skArc(sketch, "E2481", {"start": v(-11.19, 82.48) * mm, "mid": v(-9.99, 83.41) * mm, "end": v(-8.87, 84.45) * mm});
            skArc(sketch, "E2482", {"start": v(-8.87, 84.45) * mm, "mid": v(-7.9, 85.54) * mm, "end": v(-7.02, 86.73) * mm});
            skArc(sketch, "E2483", {"start": v(-7.02, 86.73) * mm, "mid": v(-6.36, 87.85) * mm, "end": v(-5.83, 89.03) * mm});
            skArc(sketch, "E2484", {"start": v(-5.83, 89.03) * mm, "mid": v(-5.56, 90.03) * mm, "end": v(-5.5, 91.07) * mm});
            skArc(sketch, "E2485", {"start": v(-5.5, 91.07) * mm, "mid": v(-5.51, 91.31) * mm, "end": v(-5.54, 91.56) * mm});
            skArc(sketch, "E2486", {"start": v(-5.54, 91.56) * mm, "mid": v(-5.6, 91.93) * mm, "end": v(-5.67, 92.3) * mm});
            skArc(sketch, "E2487", {"start": v(-5.67, 92.3) * mm, "mid": v(-5.75, 92.71) * mm, "end": v(-5.84, 93.12) * mm});
            skArc(sketch, "E2488", {"start": v(-5.84, 93.12) * mm, "mid": v(-5.93, 93.52) * mm, "end": v(-6.04, 93.92) * mm});
            skLineSegment(sketch, "E2489", {"start": v(-6.04, 93.92) * mm, "end": v(-6.53, 95.83) * mm});
            skLineSegment(sketch, "E2490", {"start": v(-6.53, 95.83) * mm, "end": v(-10.76, 91.42) * mm});
            skArc(sketch, "E2491", {"start": v(-10.76, 91.42) * mm, "mid": v(-13.7, 88.52) * mm, "end": v(-16.81, 85.8) * mm});
            skArc(sketch, "E2492", {"start": v(-16.81, 85.8) * mm, "mid": v(-19.78, 83.52) * mm, "end": v(-22.92, 81.49) * mm});
            skArc(sketch, "E2493", {"start": v(-22.92, 81.49) * mm, "mid": v(-25.98, 79.83) * mm, "end": v(-29.18, 78.44) * mm});
            skArc(sketch, "E2494", {"start": v(-29.18, 78.44) * mm, "mid": v(-32.4, 77.36) * mm, "end": v(-35.7, 76.58) * mm});
            skArc(sketch, "E2495", {"start": v(-35.7, 76.58) * mm, "mid": v(-37.89, 76.24) * mm, "end": v(-40.09, 76.07) * mm});
            skArc(sketch, "E2496", {"start": v(-40.09, 76.07) * mm, "mid": v(-42.2, 76.07) * mm, "end": v(-44.3, 76.25) * mm});
            skArc(sketch, "E2497", {"start": v(-44.3, 76.25) * mm, "mid": v(-46.44, 76.6) * mm, "end": v(-48.54, 77.13) * mm});
            skArc(sketch, "E2498", {"start": v(-48.54, 77.13) * mm, "mid": v(-50.78, 77.87) * mm, "end": v(-52.96, 78.74) * mm});
            skArc(sketch, "E2499", {"start": v(-52.96, 78.74) * mm, "mid": v(-54.7, 79.58) * mm, "end": v(-56.37, 80.53) * mm});
            skArc(sketch, "E2500", {"start": v(-56.37, 80.53) * mm, "mid": v(-57.85, 81.55) * mm, "end": v(-59.24, 82.7) * mm});
            skArc(sketch, "E2501", {"start": v(-59.24, 82.7) * mm, "mid": v(-60.51, 83.94) * mm, "end": v(-61.66, 85.29) * mm});
            skArc(sketch, "E2502", {"start": v(-61.66, 85.29) * mm, "mid": v(-62.75, 86.8) * mm, "end": v(-63.7, 88.38) * mm});
            skArc(sketch, "E2503", {"start": v(-63.7, 88.38) * mm, "mid": v(-64.21, 89.33) * mm, "end": v(-64.7, 90.29) * mm});
            skArc(sketch, "E2504", {"start": v(-64.7, 90.29) * mm, "mid": v(-65, 90.99) * mm, "end": v(-65.26, 91.7) * mm});
            skArc(sketch, "E2505", {"start": v(-65.26, 91.7) * mm, "mid": v(-65.47, 92.48) * mm, "end": v(-65.64, 93.26) * mm});
            skArc(sketch, "E2506", {"start": v(-65.64, 93.26) * mm, "mid": v(-65.84, 94.47) * mm, "end": v(-66.02, 95.69) * mm});
            skArc(sketch, "E2507", {"start": v(-66.02, 95.69) * mm, "mid": v(-66.43, 98.33) * mm, "end": v(-66.9, 100.96) * mm});
            skArc(sketch, "E2508", {"start": v(-66.9, 100.96) * mm, "mid": v(-67.31, 102.6) * mm, "end": v(-67.89, 104.2) * mm});
            skArc(sketch, "E2509", {"start": v(-67.89, 104.2) * mm, "mid": v(-68.5, 105.37) * mm, "end": v(-69.28, 106.45) * mm});
            skArc(sketch, "E2510", {"start": v(-69.28, 106.45) * mm, "mid": v(-70.27, 107.49) * mm, "end": v(-71.38, 108.39) * mm});
            skArc(sketch, "E2511", {"start": v(-71.38, 108.39) * mm, "mid": v(-71.77, 108.67) * mm, "end": v(-72.16, 108.96) * mm});
            skArc(sketch, "E2512", {"start": v(-72.16, 108.96) * mm, "mid": v(-72.49, 109.22) * mm, "end": v(-72.81, 109.49) * mm});
            skArc(sketch, "E2513", {"start": v(-72.81, 109.49) * mm, "mid": v(-73.08, 109.71) * mm, "end": v(-73.34, 109.94) * mm});
            skArc(sketch, "E2514", {"start": v(-73.34, 109.94) * mm, "mid": v(-73.4, 110.02) * mm, "end": v(-73.43, 110.1) * mm});
            skArc(sketch, "E2515", {"start": v(-73.43, 110.1) * mm, "mid": v(-73.42, 110.18) * mm, "end": v(-73.36, 110.22) * mm});
            skArc(sketch, "E2516", {"start": v(-73.36, 110.22) * mm, "mid": v(-73.13, 110.28) * mm, "end": v(-72.9, 110.33) * mm});
            skArc(sketch, "E2517", {"start": v(-72.9, 110.33) * mm, "mid": v(-72.6, 110.39) * mm, "end": v(-72.29, 110.42) * mm});
            skArc(sketch, "E2518", {"start": v(-72.29, 110.42) * mm, "mid": v(-71.92, 110.46) * mm, "end": v(-71.56, 110.48) * mm});
            skArc(sketch, "E2519", {"start": v(-71.56, 110.48) * mm, "mid": v(-70.7, 110.47) * mm, "end": v(-69.85, 110.36) * mm});
            skArc(sketch, "E2520", {"start": v(-69.85, 110.36) * mm, "mid": v(-68.99, 110.15) * mm, "end": v(-68.15, 109.86) * mm});
            skArc(sketch, "E2521", {"start": v(-68.15, 109.86) * mm, "mid": v(-67.32, 109.47) * mm, "end": v(-66.53, 109) * mm});
            skArc(sketch, "E2522", {"start": v(-66.53, 109) * mm, "mid": v(-65.77, 108.45) * mm, "end": v(-65.07, 107.83) * mm});
            skLineSegment(sketch, "E2523", {"start": v(-65.07, 107.83) * mm, "end": v(-63.77, 106.58) * mm});
            skLineSegment(sketch, "E2524", {"start": v(-63.77, 106.58) * mm, "end": v(-61.96, 108.6) * mm});
            skArc(sketch, "E2525", {"start": v(-61.96, 108.6) * mm, "mid": v(-61.52, 109.08) * mm, "end": v(-61.05, 109.53) * mm});
            skArc(sketch, "E2526", {"start": v(-61.05, 109.53) * mm, "mid": v(-60.51, 110) * mm, "end": v(-59.96, 110.45) * mm});
            skArc(sketch, "E2527", {"start": v(-59.96, 110.45) * mm, "mid": v(-59.39, 110.87) * mm, "end": v(-58.8, 111.28) * mm});
            skArc(sketch, "E2528", {"start": v(-58.8, 111.28) * mm, "mid": v(-58.22, 111.64) * mm, "end": v(-57.63, 111.97) * mm});
            skArc(sketch, "E2529", {"start": v(-57.63, 111.97) * mm, "mid": v(-56.86, 112.36) * mm, "end": v(-56.08, 112.72) * mm});
            skArc(sketch, "E2530", {"start": v(-56.08, 112.72) * mm, "mid": v(-55.52, 112.95) * mm, "end": v(-54.93, 113.12) * mm});
            skArc(sketch, "E2531", {"start": v(-54.93, 113.12) * mm, "mid": v(-54.3, 113.25) * mm, "end": v(-53.64, 113.33) * mm});
            skArc(sketch, "E2532", {"start": v(-53.64, 113.33) * mm, "mid": v(-52.57, 113.4) * mm, "end": v(-51.5, 113.46) * mm});
            skArc(sketch, "E2533", {"start": v(-51.5, 113.46) * mm, "mid": v(-50.47, 113.5) * mm, "end": v(-49.46, 113.5) * mm});
            skArc(sketch, "E2534", {"start": v(-49.46, 113.5) * mm, "mid": v(-48.8, 113.49) * mm, "end": v(-48.13, 113.42) * mm});
            skArc(sketch, "E2535", {"start": v(-48.13, 113.42) * mm, "mid": v(-47.56, 113.33) * mm, "end": v(-47, 113.18) * mm});
            skArc(sketch, "E2536", {"start": v(-47, 113.18) * mm, "mid": v(-46.34, 112.96) * mm, "end": v(-45.7, 112.71) * mm});
            skArc(sketch, "E2537", {"start": v(-45.7, 112.71) * mm, "mid": v(-43.17, 111.36) * mm, "end": v(-40.98, 109.52) * mm});
            skArc(sketch, "E2538", {"start": v(-40.98, 109.52) * mm, "mid": v(-39.31, 107.35) * mm, "end": v(-38.2, 104.85) * mm});
            skArc(sketch, "E2539", {"start": v(-38.2, 104.85) * mm, "mid": v(-37.72, 102.26) * mm, "end": v(-37.9, 99.63) * mm});
            skArc(sketch, "E2540", {"start": v(-37.9, 99.63) * mm, "mid": v(-38.7, 97.12) * mm, "end": v(-40.09, 94.88) * mm});
            skArc(sketch, "E2541", {"start": v(-40.09, 94.88) * mm, "mid": v(-40.83, 94.02) * mm, "end": v(-41.64, 93.23) * mm});
            skArc(sketch, "E2542", {"start": v(-41.64, 93.23) * mm, "mid": v(-42.4, 92.63) * mm, "end": v(-43.21, 92.13) * mm});
            skArc(sketch, "E2543", {"start": v(-43.21, 92.13) * mm, "mid": v(-44.07, 91.74) * mm, "end": v(-44.97, 91.47) * mm});
            skArc(sketch, "E2544", {"start": v(-44.97, 91.47) * mm, "mid": v(-46.01, 91.28) * mm, "end": v(-47.07, 91.19) * mm});
            skArc(sketch, "E2545", {"start": v(-47.07, 91.19) * mm, "mid": v(-48.12, 91.2) * mm, "end": v(-49.17, 91.3) * mm});
            skArc(sketch, "E2546", {"start": v(-49.17, 91.3) * mm, "mid": v(-50.12, 91.48) * mm, "end": v(-51.03, 91.79) * mm});
            skArc(sketch, "E2547", {"start": v(-51.03, 91.79) * mm, "mid": v(-51.83, 92.17) * mm, "end": v(-52.56, 92.65) * mm});
            skArc(sketch, "E2548", {"start": v(-52.56, 92.65) * mm, "mid": v(-53.17, 93.2) * mm, "end": v(-53.68, 93.84) * mm});
            skArc(sketch, "E2549", {"start": v(-53.68, 93.84) * mm, "mid": v(-54, 94.35) * mm, "end": v(-54.26, 94.89) * mm});
            skArc(sketch, "E2550", {"start": v(-54.26, 94.89) * mm, "mid": v(-54.41, 95.33) * mm, "end": v(-54.48, 95.79) * mm});
            skArc(sketch, "E2551", {"start": v(-54.48, 95.79) * mm, "mid": v(-54.45, 96.25) * mm, "end": v(-54.35, 96.7) * mm});
            skArc(sketch, "E2552", {"start": v(-54.35, 96.7) * mm, "mid": v(-54.13, 97.26) * mm, "end": v(-53.86, 97.8) * mm});
            skArc(sketch, "E2553", {"start": v(-53.86, 97.8) * mm, "mid": v(-53.28, 98.57) * mm, "end": v(-52.49, 99.14) * mm});
            skArc(sketch, "E2554", {"start": v(-52.49, 99.14) * mm, "mid": v(-51.57, 99.45) * mm, "end": v(-50.6, 99.48) * mm});
            skArc(sketch, "E2555", {"start": v(-50.6, 99.48) * mm, "mid": v(-49.65, 99.22) * mm, "end": v(-48.8, 98.7) * mm});
            skArc(sketch, "E2556", {"start": v(-48.8, 98.7) * mm, "mid": v(-48.12, 97.95) * mm, "end": v(-47.67, 97.04) * mm});
            skArc(sketch, "E2557", {"start": v(-47.67, 97.04) * mm, "mid": v(-47.44, 96.51) * mm, "end": v(-47.14, 96.02) * mm});
            skArc(sketch, "E2558", {"start": v(-47.14, 96.02) * mm, "mid": v(-46.86, 95.75) * mm, "end": v(-46.49, 95.6) * mm});
            skArc(sketch, "E2559", {"start": v(-46.49, 95.6) * mm, "mid": v(-46.04, 95.59) * mm, "end": v(-45.6, 95.72) * mm});
            skArc(sketch, "E2560", {"start": v(-45.6, 95.72) * mm, "mid": v(-44.95, 96.05) * mm, "end": v(-44.33, 96.44) * mm});
            skArc(sketch, "E2561", {"start": v(-44.33, 96.44) * mm, "mid": v(-43.8, 96.87) * mm, "end": v(-43.34, 97.38) * mm});
            skArc(sketch, "E2562", {"start": v(-43.34, 97.38) * mm, "mid": v(-42.9, 98.06) * mm, "end": v(-42.52, 98.78) * mm});
            skArc(sketch, "E2563", {"start": v(-42.52, 98.78) * mm, "mid": v(-42.2, 99.56) * mm, "end": v(-41.98, 100.37) * mm});
            skArc(sketch, "E2564", {"start": v(-41.98, 100.37) * mm, "mid": v(-41.86, 101.12) * mm, "end": v(-41.84, 101.88) * mm});
            skArc(sketch, "E2565", {"start": v(-41.84, 101.88) * mm, "mid": v(-42, 102.97) * mm, "end": v(-42.34, 104) * mm});
            skArc(sketch, "E2566", {"start": v(-42.34, 104) * mm, "mid": v(-42.92, 105.1) * mm, "end": v(-43.64, 106.11) * mm});
            skArc(sketch, "E2567", {"start": v(-43.64, 106.11) * mm, "mid": v(-44.51, 107.07) * mm, "end": v(-45.5, 107.9) * mm});
            skArc(sketch, "E2568", {"start": v(-45.5, 107.9) * mm, "mid": v(-46.54, 108.58) * mm, "end": v(-47.67, 109.1) * mm});
            skArc(sketch, "E2569", {"start": v(-47.67, 109.1) * mm, "mid": v(-48.64, 109.4) * mm, "end": v(-49.63, 109.56) * mm});
            skArc(sketch, "E2570", {"start": v(-49.63, 109.56) * mm, "mid": v(-50.76, 109.62) * mm, "end": v(-51.9, 109.58) * mm});
            skArc(sketch, "E2571", {"start": v(-51.9, 109.58) * mm, "mid": v(-53.03, 109.43) * mm, "end": v(-54.15, 109.18) * mm});
            skArc(sketch, "E2572", {"start": v(-54.15, 109.18) * mm, "mid": v(-55.13, 108.84) * mm, "end": v(-56.06, 108.4) * mm});
            skArc(sketch, "E2573", {"start": v(-56.06, 108.4) * mm, "mid": v(-57.38, 107.52) * mm, "end": v(-58.58, 106.49) * mm});
            skArc(sketch, "E2574", {"start": v(-58.58, 106.49) * mm, "mid": v(-59.62, 105.3) * mm, "end": v(-60.49, 104) * mm});
            skArc(sketch, "E2575", {"start": v(-60.49, 104) * mm, "mid": v(-61.19, 102.55) * mm, "end": v(-61.7, 101.03) * mm});
            skArc(sketch, "E2576", {"start": v(-61.7, 101.03) * mm, "mid": v(-62.02, 99.38) * mm, "end": v(-62.15, 97.7) * mm});
            skArc(sketch, "E2577", {"start": v(-62.15, 97.7) * mm, "mid": v(-61.86, 94.45) * mm, "end": v(-60.86, 91.34) * mm});
            skArc(sketch, "E2578", {"start": v(-60.86, 91.34) * mm, "mid": v(-59.2, 88.41) * mm, "end": v(-56.98, 85.88) * mm});
            skArc(sketch, "E2579", {"start": v(-56.98, 85.88) * mm, "mid": v(-54.1, 83.65) * mm, "end": v(-50.87, 81.97) * mm});
            skArc(sketch, "E2580", {"start": v(-50.87, 81.97) * mm, "mid": v(-47.13, 80.75) * mm, "end": v(-43.25, 80.07) * mm});
            skArc(sketch, "E2581", {"start": v(-43.25, 80.07) * mm, "mid": v(-40.35, 79.97) * mm, "end": v(-37.46, 80.24) * mm});
            skArc(sketch, "E2582", {"start": v(-37.46, 80.24) * mm, "mid": v(-34.31, 80.9) * mm, "end": v(-31.23, 81.85) * mm});
            skArc(sketch, "E2583", {"start": v(-31.23, 81.85) * mm, "mid": v(-28.05, 83.17) * mm, "end": v(-24.98, 84.76) * mm});
            skArc(sketch, "E2584", {"start": v(-24.98, 84.76) * mm, "mid": v(-21.98, 86.67) * mm, "end": v(-19.14, 88.8) * mm});
            skArc(sketch, "E2585", {"start": v(-19.14, 88.8) * mm, "mid": v(-17.21, 90.47) * mm, "end": v(-15.38, 92.23) * mm});
            skArc(sketch, "E2586", {"start": v(-15.38, 92.23) * mm, "mid": v(-13.44, 94.28) * mm, "end": v(-11.58, 96.4) * mm});
            skArc(sketch, "E2587", {"start": v(-11.58, 96.4) * mm, "mid": v(-9.41, 99.05) * mm, "end": v(-7.32, 101.77) * mm});
            skArc(sketch, "E2588", {"start": v(-7.32, 101.77) * mm, "mid": v(-4.7, 105.36) * mm, "end": v(-2.11, 108.98) * mm});
            skArc(sketch, "E2589", {"start": v(-2.11, 108.98) * mm, "mid": v(-1.34, 110.08) * mm, "end": v(-0.57, 111.17) * mm});
            skArc(sketch, "E2590", {"start": v(-0.57, 111.17) * mm, "mid": v(0.2, 112.26) * mm, "end": v(0.99, 113.35) * mm});
            skArc(sketch, "E2591", {"start": v(0.99, 113.35) * mm, "mid": v(1.67, 114.3) * mm, "end": v(2.36, 115.25) * mm});
            skArc(sketch, "E2592", {"start": v(2.36, 115.25) * mm, "mid": v(2.78, 115.82) * mm, "end": v(3.22, 116.39) * mm});
            skArc(sketch, "E2593", {"start": v(3.22, 116.39) * mm, "mid": v(3.52, 116.8) * mm, "end": v(3.82, 117.2) * mm});
            skArc(sketch, "E2594", {"start": v(3.82, 117.2) * mm, "mid": v(4.06, 117.56) * mm, "end": v(4.3, 117.92) * mm});
            skArc(sketch, "E2595", {"start": v(4.3, 117.92) * mm, "mid": v(4.47, 118.22) * mm, "end": v(4.65, 118.52) * mm});
            skArc(sketch, "E2596", {"start": v(4.65, 118.52) * mm, "mid": v(4.66, 118.6) * mm, "end": v(4.63, 118.66) * mm});
            skArc(sketch, "E2597", {"start": v(4.63, 118.66) * mm, "mid": v(4.55, 118.7) * mm, "end": v(4.46, 118.7) * mm});
            skArc(sketch, "E2598", {"start": v(4.46, 118.7) * mm, "mid": v(4.01, 118.59) * mm, "end": v(3.57, 118.47) * mm});
            skArc(sketch, "E2599", {"start": v(3.57, 118.47) * mm, "mid": v(3.03, 118.32) * mm, "end": v(2.5, 118.17) * mm});
            skArc(sketch, "E2600", {"start": v(2.5, 118.17) * mm, "mid": v(1.9, 117.97) * mm, "end": v(1.28, 117.77) * mm});
            skArc(sketch, "E2601", {"start": v(1.28, 117.77) * mm, "mid": v(0.58, 117.54) * mm, "end": v(-0.12, 117.32) * mm});
            skArc(sketch, "E2602", {"start": v(-0.12, 117.32) * mm, "mid": v(-0.93, 117.09) * mm, "end": v(-1.75, 116.86) * mm});
            skArc(sketch, "E2603", {"start": v(-1.75, 116.86) * mm, "mid": v(-2.54, 116.65) * mm, "end": v(-3.34, 116.44) * mm});
            skArc(sketch, "E2604", {"start": v(-3.34, 116.44) * mm, "mid": v(-3.97, 116.3) * mm, "end": v(-4.61, 116.16) * mm});
            skArc(sketch, "E2605", {"start": v(-4.61, 116.16) * mm, "mid": v(-6.78, 115.62) * mm, "end": v(-8.88, 114.9) * mm});
            skArc(sketch, "E2606", {"start": v(-8.88, 114.9) * mm, "mid": v(-10.77, 114.02) * mm, "end": v(-12.56, 112.94) * mm});
            skArc(sketch, "E2607", {"start": v(-12.56, 112.94) * mm, "mid": v(-14.17, 111.7) * mm, "end": v(-15.63, 110.29) * mm});
            skArc(sketch, "E2608", {"start": v(-15.63, 110.29) * mm, "mid": v(-16.95, 108.7) * mm, "end": v(-18.09, 106.98) * mm});
            skLineSegment(sketch, "E2609", {"start": v(-18.09, 106.98) * mm, "end": v(-19.44, 104.67) * mm});
            skLineSegment(sketch, "E2610", {"start": v(-19.44, 104.67) * mm, "end": v(-20.08, 106.02) * mm});
            skArc(sketch, "E2611", {"start": v(-20.08, 106.02) * mm, "mid": v(-20.48, 107.1) * mm, "end": v(-20.7, 108.23) * mm});
            skArc(sketch, "E2612", {"start": v(-20.7, 108.23) * mm, "mid": v(-20.73, 109.38) * mm, "end": v(-20.57, 110.51) * mm});
            skArc(sketch, "E2613", {"start": v(-20.57, 110.51) * mm, "mid": v(-20.21, 111.7) * mm, "end": v(-19.68, 112.84) * mm});
            skArc(sketch, "E2614", {"start": v(-19.68, 112.84) * mm, "mid": v(-18.91, 114.04) * mm, "end": v(-18.03, 115.16) * mm});
            skLineSegment(sketch, "E2615", {"start": v(-18.03, 115.16) * mm, "end": v(-16.5, 116.91) * mm});
            skLineSegment(sketch, "E2616", {"start": v(-16.5, 116.91) * mm, "end": v(-17.42, 117.57) * mm});
            skArc(sketch, "E2617", {"start": v(-17.42, 117.57) * mm, "mid": v(-17.65, 117.74) * mm, "end": v(-17.87, 117.9) * mm});
            skArc(sketch, "E2618", {"start": v(-17.87, 117.9) * mm, "mid": v(-18.2, 118.16) * mm, "end": v(-18.51, 118.42) * mm});
            skArc(sketch, "E2619", {"start": v(-18.51, 118.42) * mm, "mid": v(-18.86, 118.7) * mm, "end": v(-19.2, 119) * mm});
            skArc(sketch, "E2620", {"start": v(-19.2, 119) * mm, "mid": v(-19.53, 119.27) * mm, "end": v(-19.85, 119.55) * mm});
            skArc(sketch, "E2621", {"start": v(-19.85, 119.55) * mm, "mid": v(-22.22, 122.3) * mm, "end": v(-23.72, 125.6) * mm});
            skArc(sketch, "E2622", {"start": v(-23.72, 125.6) * mm, "mid": v(-24.26, 129.24) * mm, "end": v(-23.8, 132.89) * mm});
            skArc(sketch, "E2623", {"start": v(-23.8, 132.89) * mm, "mid": v(-22.4, 136.1) * mm, "end": v(-20.13, 138.79) * mm});
            skArc(sketch, "E2624", {"start": v(-20.13, 138.79) * mm, "mid": v(-17.28, 140.54) * mm, "end": v(-14.02, 141.25) * mm});
            skArc(sketch, "E2625", {"start": v(-14.02, 141.25) * mm, "mid": v(-12.17, 141.15) * mm, "end": v(-10.37, 140.72) * mm});
            skArc(sketch, "E2626", {"start": v(-10.37, 140.72) * mm, "mid": v(-8.66, 139.95) * mm, "end": v(-7.12, 138.89) * mm});
            skArc(sketch, "E2627", {"start": v(-7.12, 138.89) * mm, "mid": v(-5.84, 137.6) * mm, "end": v(-4.83, 136.1) * mm});
            skArc(sketch, "E2628", {"start": v(-4.83, 136.1) * mm, "mid": v(-4.19, 134.53) * mm, "end": v(-3.92, 132.86) * mm});
            skArc(sketch, "E2629", {"start": v(-3.92, 132.86) * mm, "mid": v(-3.93, 132.2) * mm, "end": v(-4.03, 131.56) * mm});
            skArc(sketch, "E2630", {"start": v(-4.03, 131.56) * mm, "mid": v(-4.23, 130.75) * mm, "end": v(-4.48, 129.96) * mm});
            skArc(sketch, "E2631", {"start": v(-4.48, 129.96) * mm, "mid": v(-4.77, 129.2) * mm, "end": v(-5.11, 128.46) * mm});
            skArc(sketch, "E2632", {"start": v(-5.11, 128.46) * mm, "mid": v(-5.42, 127.94) * mm, "end": v(-5.8, 127.48) * mm});
            skArc(sketch, "E2633", {"start": v(-5.8, 127.48) * mm, "mid": v(-6.55, 126.91) * mm, "end": v(-7.42, 126.58) * mm});
            skArc(sketch, "E2634", {"start": v(-7.42, 126.58) * mm, "mid": v(-8.36, 126.5) * mm, "end": v(-9.29, 126.69) * mm});
            skArc(sketch, "E2635", {"start": v(-9.29, 126.69) * mm, "mid": v(-10.1, 127.12) * mm, "end": v(-10.78, 127.76) * mm});
            skArc(sketch, "E2636", {"start": v(-10.78, 127.76) * mm, "mid": v(-11.22, 128.55) * mm, "end": v(-11.4, 129.44) * mm});
            skArc(sketch, "E2637", {"start": v(-11.4, 129.44) * mm, "mid": v(-11.36, 130) * mm, "end": v(-11.22, 130.54) * mm});
            skArc(sketch, "E2638", {"start": v(-11.22, 130.54) * mm, "mid": v(-10.97, 131.1) * mm, "end": v(-10.63, 131.6) * mm});
            skArc(sketch, "E2639", {"start": v(-10.63, 131.6) * mm, "mid": v(-10.24, 132.04) * mm, "end": v(-9.79, 132.4) * mm});
            skArc(sketch, "E2640", {"start": v(-9.79, 132.4) * mm, "mid": v(-9.36, 132.62) * mm, "end": v(-8.89, 132.7) * mm});
            skArc(sketch, "E2641", {"start": v(-8.89, 132.7) * mm, "mid": v(-8.58, 132.8) * mm, "end": v(-8.34, 133) * mm});
            skArc(sketch, "E2642", {"start": v(-8.34, 133) * mm, "mid": v(-8.19, 133.3) * mm, "end": v(-8.15, 133.65) * mm});
            skArc(sketch, "E2643", {"start": v(-8.15, 133.65) * mm, "mid": v(-8.22, 134.12) * mm, "end": v(-8.4, 134.57) * mm});
            skArc(sketch, "E2644", {"start": v(-8.4, 134.57) * mm, "mid": v(-8.68, 135.06) * mm, "end": v(-9.03, 135.52) * mm});
            skArc(sketch, "E2645", {"start": v(-9.03, 135.52) * mm, "mid": v(-9.94, 136.37) * mm, "end": v(-11.02, 136.99) * mm});
            skArc(sketch, "E2646", {"start": v(-11.02, 136.99) * mm, "mid": v(-12.24, 137.37) * mm, "end": v(-13.52, 137.49) * mm});
            skArc(sketch, "E2647", {"start": v(-13.52, 137.49) * mm, "mid": v(-14.83, 137.34) * mm, "end": v(-16.09, 136.93) * mm});
            skArc(sketch, "E2648", {"start": v(-16.09, 136.93) * mm, "mid": v(-17.26, 136.28) * mm, "end": v(-18.29, 135.41) * mm});
            skArc(sketch, "E2649", {"start": v(-18.29, 135.41) * mm, "mid": v(-18.84, 134.78) * mm, "end": v(-19.32, 134.08) * mm});
            skArc(sketch, "E2650", {"start": v(-19.32, 134.08) * mm, "mid": v(-19.73, 133.33) * mm, "end": v(-20.04, 132.54) * mm});
            skArc(sketch, "E2651", {"start": v(-20.04, 132.54) * mm, "mid": v(-20.28, 131.67) * mm, "end": v(-20.44, 130.78) * mm});
            skArc(sketch, "E2652", {"start": v(-20.44, 130.78) * mm, "mid": v(-20.51, 129.78) * mm, "end": v(-20.5, 128.79) * mm});
            skArc(sketch, "E2653", {"start": v(-20.5, 128.79) * mm, "mid": v(-20.42, 127.7) * mm, "end": v(-20.23, 126.65) * mm});
            skArc(sketch, "E2654", {"start": v(-20.23, 126.65) * mm, "mid": v(-19.96, 125.72) * mm, "end": v(-19.57, 124.83) * mm});
            skArc(sketch, "E2655", {"start": v(-19.57, 124.83) * mm, "mid": v(-19.08, 123.99) * mm, "end": v(-18.48, 123.22) * mm});
            skArc(sketch, "E2656", {"start": v(-18.48, 123.22) * mm, "mid": v(-17.72, 122.42) * mm, "end": v(-16.9, 121.7) * mm});
            skArc(sketch, "E2657", {"start": v(-16.9, 121.7) * mm, "mid": v(-14.35, 120.19) * mm, "end": v(-11.47, 119.46) * mm});
            skArc(sketch, "E2658", {"start": v(-11.47, 119.46) * mm, "mid": v(-7.9, 119.37) * mm, "end": v(-4.36, 119.88) * mm});
            skArc(sketch, "E2659", {"start": v(-4.36, 119.88) * mm, "mid": v(0.44, 121.25) * mm, "end": v(5.08, 123.12) * mm});
            skArc(sketch, "E2660", {"start": v(5.08, 123.12) * mm, "mid": v(11.58, 126.3) * mm, "end": v(17.95, 129.7) * mm});
            skArc(sketch, "E2661", {"start": v(17.95, 129.7) * mm, "mid": v(20.71, 131.17) * mm, "end": v(23.53, 132.52) * mm});
            skArc(sketch, "E2662", {"start": v(23.53, 132.52) * mm, "mid": v(25.97, 133.53) * mm, "end": v(28.46, 134.37) * mm});
            skArc(sketch, "E2663", {"start": v(28.46, 134.37) * mm, "mid": v(31, 135.05) * mm, "end": v(33.6, 135.55) * mm});
            skArc(sketch, "E2664", {"start": v(33.6, 135.55) * mm, "mid": v(36.68, 135.97) * mm, "end": v(39.79, 136.27) * mm});
            skArc(sketch, "E2665", {"start": v(39.79, 136.27) * mm, "mid": v(42.37, 136.42) * mm, "end": v(44.96, 136.48) * mm});
            skArc(sketch, "E2666", {"start": v(44.96, 136.48) * mm, "mid": v(47.1, 136.43) * mm, "end": v(49.24, 136.24) * mm});
            skArc(sketch, "E2667", {"start": v(49.24, 136.24) * mm, "mid": v(51.3, 135.93) * mm, "end": v(53.32, 135.49) * mm});
            skArc(sketch, "E2668", {"start": v(53.32, 135.49) * mm, "mid": v(55.6, 134.86) * mm, "end": v(57.84, 134.14) * mm});
            skArc(sketch, "E2669", {"start": v(57.84, 134.14) * mm, "mid": v(58.86, 133.79) * mm, "end": v(59.9, 133.46) * mm});
            skArc(sketch, "E2670", {"start": v(67.64, 129.12) * mm, "mid": v(63.97, 131.65) * mm, "end": v(59.9, 133.46) * mm});
            skSolve(sketch);
        }
        {
            var Q0;
            Q0 = qSketchRegion(id + "F22", true);
            var Q1;
            Q1=makeQuery(id+"F21.opExtrude","CAP_FACE",FACE,{"disambiguationData":[OSD([sQuery(id+"F20.wireOp",EDGE,"E2246"),sQuery(id+"F20.wireOp",EDGE,"E2247"),sQuery(id+"F20.wireOp",EDGE,"E2248"),sQuery(id+"F20.wireOp",EDGE,"E2251.bottom"),sQuery(id+"F20.wireOp",EDGE,"E2251.top"),sQuery(id+"F20.wireOp",EDGE,"E2251.left"),sQuery(id+"F20.wireOp",EDGE,"E2251.right"),sQuery(id+"F20.wireOp",EDGE,"E2252.trimOffspring"),sQuery(id+"F20.wireOp",EDGE,"E2254"),sQuery(id+"F20.wireOp",EDGE,"E2255.0"),sQuery(id+"F20.wireOp",EDGE,"E2256.MirrorCS"),sQuery(id+"F20.wireOp",EDGE,"E2257.MirrorCS"),sQuery(id+"F20.wireOp",EDGE,"E2258.trimOffspring"),sQuery(id+"F20.wireOp",EDGE,"E2259.trimOffspring"),sQuery(id+"F20.wireOp",EDGE,"E2260.trimOffspring"),sQuery(id+"F20.wireOp",EDGE,"E2261.trimOffspring"),sQuery(id+"F20.wireOp",EDGE,"E2262.filletArc"),sQuery(id+"F20.wireOp",EDGE,"E2263.filletArc"),sQuery(id+"F20.wireOp",EDGE,"E2264.filletArc"),sQuery(id+"F20.wireOp",EDGE,"E2265.filletArc")])],"isStart":true});
            extrude(context, id + "F23", {"entities" : qUnion([Q0]), "operationType" : NewBodyOperationType.ADD, "endBound" : BoundingType.UP_TO_SURFACE, "oppositeDirection" : true, "depth" : 25.4 * mm, "endBoundEntityFace" : qUnion([Q1]), "offsetDistance" : 25.4 * mm});
        }
        {
            var Q0;
            {var subQ14=sQuery(id+"F20.wireOp",EDGE,"E2251.left");var subQ16=sQuery(id+"F20.wireOp",EDGE,"E2251.bottom");Q0=makeQuery(id+"F23.boolean.opBoolean","SPLIT",FACE,{"disambiguationData":[TD([makeQuery(id+"F21.opExtrude","SWEPT_FACE",FACE,{"disambiguationData":[OSD([subQ16])]})])],"derivedFrom":makeQuery(id+"F21.opExtrude","SWEPT_FACE",FACE,{"disambiguationData":[OSD([subQ14])]})});}
            var sketch = newSketch(context, id + "F24", { "sketchPlane" : qUnion([Q0])});
            skPoint(sketch, "E2671", {"position": v(0, 133.35) * mm});
            skPoint(sketch, "E2672", {"position": v(0, 50.8) * mm});
            skLineSegment(sketch, "E2673", {"start": v(0, 139.7) * mm, "end": v(0, 133.35) * mm, "construction": true});
            skLineSegment(sketch, "E2674", {"start": v(0, 44.45) * mm, "end": v(0, 50.8) * mm, "construction": true});
            skSolve(sketch);
        }
        {
            var Q0;
            Q0=sQuery(id+"F24.wireOp",VERTEX,"E2671");
            var Q1;
            Q1=sQuery(id+"F24.wireOp",VERTEX,"E2672");
            var Q2;
            Q2=makeQuery(id+"F21.opExtrude","SWEPT_BODY",BODY,{"disambiguationData":[OSD([sQuery(id+"F20.wireOp",EDGE,"E2246"),sQuery(id+"F20.wireOp",EDGE,"E2247"),sQuery(id+"F20.wireOp",EDGE,"E2248"),sQuery(id+"F20.wireOp",EDGE,"E2251.bottom"),sQuery(id+"F20.wireOp",EDGE,"E2251.top"),sQuery(id+"F20.wireOp",EDGE,"E2251.left"),sQuery(id+"F20.wireOp",EDGE,"E2251.right"),sQuery(id+"F20.wireOp",EDGE,"E2252.trimOffspring"),sQuery(id+"F20.wireOp",EDGE,"E2254"),sQuery(id+"F20.wireOp",EDGE,"E2255.0"),sQuery(id+"F20.wireOp",EDGE,"E2256.MirrorCS"),sQuery(id+"F20.wireOp",EDGE,"E2257.MirrorCS"),sQuery(id+"F20.wireOp",EDGE,"E2258.trimOffspring"),sQuery(id+"F20.wireOp",EDGE,"E2259.trimOffspring"),sQuery(id+"F20.wireOp",EDGE,"E2260.trimOffspring"),sQuery(id+"F20.wireOp",EDGE,"E2261.trimOffspring"),sQuery(id+"F20.wireOp",EDGE,"E2262.filletArc"),sQuery(id+"F20.wireOp",EDGE,"E2263.filletArc"),sQuery(id+"F20.wireOp",EDGE,"E2264.filletArc"),sQuery(id+"F20.wireOp",EDGE,"E2265.filletArc")])]});
            hole(context, id + "F25", {"style" : HoleStyle.C_SINK, "endStyle" : HoleEndStyle.THROUGH, "standardTappedOrClearance" : lookupTablePath({ "standard" : "ANSI", "fit" : "Normal (ASME)", "size" : "#8", "type" : "Clearance" }), "standardBlindInLast" : lookupTablePath({ "fit" : "Free", "standard" : "ANSI", "size" : "#8", "type" : "Clearance" }), "holeDiameter" : 4.5 * mm, "cSinkDiameter" : 9.12 * mm, "cSinkAngle" : 82 * degree, "majorDiameter" : 6.35 * mm, "isTappedThrough" : true, "tappedDepth" : 12.7 * mm, "tapClearance" : 3, "locations" : qUnion([Q0, Q1]), "scope" : qUnion([Q2])});
        }
        {
            var Q0;
            Q0=makeQuery(id+"F23.boolean.opBoolean","MERGE",FACE,{"derivedFrom":[makeQuery(id+"F21.opExtrude","CAP_FACE",FACE,{"disambiguationData":[OSD([sQuery(id+"F20.wireOp",EDGE,"E2246"),sQuery(id+"F20.wireOp",EDGE,"E2247"),sQuery(id+"F20.wireOp",EDGE,"E2248"),sQuery(id+"F20.wireOp",EDGE,"E2251.bottom"),sQuery(id+"F20.wireOp",EDGE,"E2251.top"),sQuery(id+"F20.wireOp",EDGE,"E2251.left"),sQuery(id+"F20.wireOp",EDGE,"E2251.right"),sQuery(id+"F20.wireOp",EDGE,"E2252.trimOffspring"),sQuery(id+"F20.wireOp",EDGE,"E2254"),sQuery(id+"F20.wireOp",EDGE,"E2255.0"),sQuery(id+"F20.wireOp",EDGE,"E2256.MirrorCS"),sQuery(id+"F20.wireOp",EDGE,"E2257.MirrorCS"),sQuery(id+"F20.wireOp",EDGE,"E2258.trimOffspring"),sQuery(id+"F20.wireOp",EDGE,"E2259.trimOffspring"),sQuery(id+"F20.wireOp",EDGE,"E2260.trimOffspring"),sQuery(id+"F20.wireOp",EDGE,"E2261.trimOffspring"),sQuery(id+"F20.wireOp",EDGE,"E2262.filletArc"),sQuery(id+"F20.wireOp",EDGE,"E2263.filletArc"),sQuery(id+"F20.wireOp",EDGE,"E2264.filletArc"),sQuery(id+"F20.wireOp",EDGE,"E2265.filletArc")])],"isStart":false}),makeQuery(id+"F23.opExtrude","CAP_FACE",FACE,{"disambiguationData":[OSD([sQuery(id+"F22.wireOp",EDGE,"E2268"),sQuery(id+"F22.wireOp",EDGE,"E2269"),sQuery(id+"F22.wireOp",EDGE,"E2270"),sQuery(id+"F22.wireOp",EDGE,"E2271"),sQuery(id+"F22.wireOp",EDGE,"E2272"),sQuery(id+"F22.wireOp",EDGE,"E2273"),sQuery(id+"F22.wireOp",EDGE,"E2274"),sQuery(id+"F22.wireOp",EDGE,"E2275"),sQuery(id+"F22.wireOp",EDGE,"E2276"),sQuery(id+"F22.wireOp",EDGE,"E2277"),sQuery(id+"F22.wireOp",EDGE,"E2278"),sQuery(id+"F22.wireOp",EDGE,"E2279"),sQuery(id+"F22.wireOp",EDGE,"E2280"),sQuery(id+"F22.wireOp",EDGE,"E2281"),sQuery(id+"F22.wireOp",EDGE,"E2282"),sQuery(id+"F22.wireOp",EDGE,"E2283"),sQuery(id+"F22.wireOp",EDGE,"E2284"),sQuery(id+"F22.wireOp",EDGE,"E2285"),sQuery(id+"F22.wireOp",EDGE,"E2286"),sQuery(id+"F22.wireOp",EDGE,"E2287"),sQuery(id+"F22.wireOp",EDGE,"E2288"),sQuery(id+"F22.wireOp",EDGE,"E2289"),sQuery(id+"F22.wireOp",EDGE,"E2290"),sQuery(id+"F22.wireOp",EDGE,"E2291"),sQuery(id+"F22.wireOp",EDGE,"E2292"),sQuery(id+"F22.wireOp",EDGE,"E2293"),sQuery(id+"F22.wireOp",EDGE,"E2294"),sQuery(id+"F22.wireOp",EDGE,"E2295"),sQuery(id+"F22.wireOp",EDGE,"E2296"),sQuery(id+"F22.wireOp",EDGE,"E2297"),sQuery(id+"F22.wireOp",EDGE,"E2298"),sQuery(id+"F22.wireOp",EDGE,"E2299"),sQuery(id+"F22.wireOp",EDGE,"E2300"),sQuery(id+"F22.wireOp",EDGE,"E2301"),sQuery(id+"F22.wireOp",EDGE,"E2302"),sQuery(id+"F22.wireOp",EDGE,"E2303"),sQuery(id+"F22.wireOp",EDGE,"E2304"),sQuery(id+"F22.wireOp",EDGE,"E2305"),sQuery(id+"F22.wireOp",EDGE,"E2306"),sQuery(id+"F22.wireOp",EDGE,"E2307"),sQuery(id+"F22.wireOp",EDGE,"E2308"),sQuery(id+"F22.wireOp",EDGE,"E2309"),sQuery(id+"F22.wireOp",EDGE,"E2310"),sQuery(id+"F22.wireOp",EDGE,"E2311"),sQuery(id+"F22.wireOp",EDGE,"E2312"),sQuery(id+"F22.wireOp",EDGE,"E2313"),sQuery(id+"F22.wireOp",EDGE,"E2314"),sQuery(id+"F22.wireOp",EDGE,"E2315"),sQuery(id+"F22.wireOp",EDGE,"E2316"),sQuery(id+"F22.wireOp",EDGE,"E2317"),sQuery(id+"F22.wireOp",EDGE,"E2318"),sQuery(id+"F22.wireOp",EDGE,"E2319"),sQuery(id+"F22.wireOp",EDGE,"E2320"),sQuery(id+"F22.wireOp",EDGE,"E2321"),sQuery(id+"F22.wireOp",EDGE,"E2322"),sQuery(id+"F22.wireOp",EDGE,"E2323"),sQuery(id+"F22.wireOp",EDGE,"E2324"),sQuery(id+"F22.wireOp",EDGE,"E2325"),sQuery(id+"F22.wireOp",EDGE,"E2326"),sQuery(id+"F22.wireOp",EDGE,"E2327"),sQuery(id+"F22.wireOp",EDGE,"E2328"),sQuery(id+"F22.wireOp",EDGE,"E2329"),sQuery(id+"F22.wireOp",EDGE,"E2330"),sQuery(id+"F22.wireOp",EDGE,"E2331"),sQuery(id+"F22.wireOp",EDGE,"E2332"),sQuery(id+"F22.wireOp",EDGE,"E2333"),sQuery(id+"F22.wireOp",EDGE,"E2334"),sQuery(id+"F22.wireOp",EDGE,"E2335"),sQuery(id+"F22.wireOp",EDGE,"E2336"),sQuery(id+"F22.wireOp",EDGE,"E2337"),sQuery(id+"F22.wireOp",EDGE,"E2338"),sQuery(id+"F22.wireOp",EDGE,"E2339"),sQuery(id+"F22.wireOp",EDGE,"E2340"),sQuery(id+"F22.wireOp",EDGE,"E2341"),sQuery(id+"F22.wireOp",EDGE,"E2342"),sQuery(id+"F22.wireOp",EDGE,"E2343"),sQuery(id+"F22.wireOp",EDGE,"E2344"),sQuery(id+"F22.wireOp",EDGE,"E2345"),sQuery(id+"F22.wireOp",EDGE,"E2346"),sQuery(id+"F22.wireOp",EDGE,"E2347"),sQuery(id+"F22.wireOp",EDGE,"E2348"),sQuery(id+"F22.wireOp",EDGE,"E2349"),sQuery(id+"F22.wireOp",EDGE,"E2350"),sQuery(id+"F22.wireOp",EDGE,"E2351"),sQuery(id+"F22.wireOp",EDGE,"E2352"),sQuery(id+"F22.wireOp",EDGE,"E2353"),sQuery(id+"F22.wireOp",EDGE,"E2354"),sQuery(id+"F22.wireOp",EDGE,"E2355"),sQuery(id+"F22.wireOp",EDGE,"E2356"),sQuery(id+"F22.wireOp",EDGE,"E2357"),sQuery(id+"F22.wireOp",EDGE,"E2358"),sQuery(id+"F22.wireOp",EDGE,"E2359"),sQuery(id+"F22.wireOp",EDGE,"E2360"),sQuery(id+"F22.wireOp",EDGE,"E2361"),sQuery(id+"F22.wireOp",EDGE,"E2362"),sQuery(id+"F22.wireOp",EDGE,"E2363"),sQuery(id+"F22.wireOp",EDGE,"E2364"),sQuery(id+"F22.wireOp",EDGE,"E2365"),sQuery(id+"F22.wireOp",EDGE,"E2366"),sQuery(id+"F22.wireOp",EDGE,"E2367"),sQuery(id+"F22.wireOp",EDGE,"E2368"),sQuery(id+"F22.wireOp",EDGE,"E2369"),sQuery(id+"F22.wireOp",EDGE,"E2370"),sQuery(id+"F22.wireOp",EDGE,"E2371"),sQuery(id+"F22.wireOp",EDGE,"E2372"),sQuery(id+"F22.wireOp",EDGE,"E2373"),sQuery(id+"F22.wireOp",EDGE,"E2374"),sQuery(id+"F22.wireOp",EDGE,"E2375"),sQuery(id+"F22.wireOp",EDGE,"E2376"),sQuery(id+"F22.wireOp",EDGE,"E2377"),sQuery(id+"F22.wireOp",EDGE,"E2378"),sQuery(id+"F22.wireOp",EDGE,"E2379"),sQuery(id+"F22.wireOp",EDGE,"E2380"),sQuery(id+"F22.wireOp",EDGE,"E2381"),sQuery(id+"F22.wireOp",EDGE,"E2382"),sQuery(id+"F22.wireOp",EDGE,"E2383"),sQuery(id+"F22.wireOp",EDGE,"E2384"),sQuery(id+"F22.wireOp",EDGE,"E2385"),sQuery(id+"F22.wireOp",EDGE,"E2386"),sQuery(id+"F22.wireOp",EDGE,"E2387"),sQuery(id+"F22.wireOp",EDGE,"E2388"),sQuery(id+"F22.wireOp",EDGE,"E2389"),sQuery(id+"F22.wireOp",EDGE,"E2390"),sQuery(id+"F22.wireOp",EDGE,"E2391"),sQuery(id+"F22.wireOp",EDGE,"E2392"),sQuery(id+"F22.wireOp",EDGE,"E2393"),sQuery(id+"F22.wireOp",EDGE,"E2394"),sQuery(id+"F22.wireOp",EDGE,"E2395"),sQuery(id+"F22.wireOp",EDGE,"E2396"),sQuery(id+"F22.wireOp",EDGE,"E2397"),sQuery(id+"F22.wireOp",EDGE,"E2398"),sQuery(id+"F22.wireOp",EDGE,"E2399"),sQuery(id+"F22.wireOp",EDGE,"E2400"),sQuery(id+"F22.wireOp",EDGE,"E2401"),sQuery(id+"F22.wireOp",EDGE,"E2402"),sQuery(id+"F22.wireOp",EDGE,"E2403"),sQuery(id+"F22.wireOp",EDGE,"E2404"),sQuery(id+"F22.wireOp",EDGE,"E2405"),sQuery(id+"F22.wireOp",EDGE,"E2406"),sQuery(id+"F22.wireOp",EDGE,"E2407"),sQuery(id+"F22.wireOp",EDGE,"E2408"),sQuery(id+"F22.wireOp",EDGE,"E2409"),sQuery(id+"F22.wireOp",EDGE,"E2410"),sQuery(id+"F22.wireOp",EDGE,"E2411"),sQuery(id+"F22.wireOp",EDGE,"E2412"),sQuery(id+"F22.wireOp",EDGE,"E2413"),sQuery(id+"F22.wireOp",EDGE,"E2414"),sQuery(id+"F22.wireOp",EDGE,"E2415"),sQuery(id+"F22.wireOp",EDGE,"E2416"),sQuery(id+"F22.wireOp",EDGE,"E2417"),sQuery(id+"F22.wireOp",EDGE,"E2418"),sQuery(id+"F22.wireOp",EDGE,"E2419"),sQuery(id+"F22.wireOp",EDGE,"E2420"),sQuery(id+"F22.wireOp",EDGE,"E2421"),sQuery(id+"F22.wireOp",EDGE,"E2422"),sQuery(id+"F22.wireOp",EDGE,"E2423"),sQuery(id+"F22.wireOp",EDGE,"E2424"),sQuery(id+"F22.wireOp",EDGE,"E2425"),sQuery(id+"F22.wireOp",EDGE,"E2426"),sQuery(id+"F22.wireOp",EDGE,"E2427"),sQuery(id+"F22.wireOp",EDGE,"E2428"),sQuery(id+"F22.wireOp",EDGE,"E2429"),sQuery(id+"F22.wireOp",EDGE,"E2430"),sQuery(id+"F22.wireOp",EDGE,"E2431"),sQuery(id+"F22.wireOp",EDGE,"E2432"),sQuery(id+"F22.wireOp",EDGE,"E2433"),sQuery(id+"F22.wireOp",EDGE,"E2434"),sQuery(id+"F22.wireOp",EDGE,"E2435"),sQuery(id+"F22.wireOp",EDGE,"E2436"),sQuery(id+"F22.wireOp",EDGE,"E2437"),sQuery(id+"F22.wireOp",EDGE,"E2438"),sQuery(id+"F22.wireOp",EDGE,"E2439"),sQuery(id+"F22.wireOp",EDGE,"E2440"),sQuery(id+"F22.wireOp",EDGE,"E2441"),sQuery(id+"F22.wireOp",EDGE,"E2442"),sQuery(id+"F22.wireOp",EDGE,"E2443"),sQuery(id+"F22.wireOp",EDGE,"E2444"),sQuery(id+"F22.wireOp",EDGE,"E2445"),sQuery(id+"F22.wireOp",EDGE,"E2446"),sQuery(id+"F22.wireOp",EDGE,"E2447"),sQuery(id+"F22.wireOp",EDGE,"E2448"),sQuery(id+"F22.wireOp",EDGE,"E2449"),sQuery(id+"F22.wireOp",EDGE,"E2450"),sQuery(id+"F22.wireOp",EDGE,"E2451"),sQuery(id+"F22.wireOp",EDGE,"E2452"),sQuery(id+"F22.wireOp",EDGE,"E2453"),sQuery(id+"F22.wireOp",EDGE,"E2454"),sQuery(id+"F22.wireOp",EDGE,"E2455"),sQuery(id+"F22.wireOp",EDGE,"E2456"),sQuery(id+"F22.wireOp",EDGE,"E2457"),sQuery(id+"F22.wireOp",EDGE,"E2458"),sQuery(id+"F22.wireOp",EDGE,"E2459"),sQuery(id+"F22.wireOp",EDGE,"E2460"),sQuery(id+"F22.wireOp",EDGE,"E2461"),sQuery(id+"F22.wireOp",EDGE,"E2462"),sQuery(id+"F22.wireOp",EDGE,"E2463"),sQuery(id+"F22.wireOp",EDGE,"E2464"),sQuery(id+"F22.wireOp",EDGE,"E2465"),sQuery(id+"F22.wireOp",EDGE,"E2466"),sQuery(id+"F22.wireOp",EDGE,"E2467"),sQuery(id+"F22.wireOp",EDGE,"E2468"),sQuery(id+"F22.wireOp",EDGE,"E2469"),sQuery(id+"F22.wireOp",EDGE,"E2470"),sQuery(id+"F22.wireOp",EDGE,"E2471"),sQuery(id+"F22.wireOp",EDGE,"E2472"),sQuery(id+"F22.wireOp",EDGE,"E2473"),sQuery(id+"F22.wireOp",EDGE,"E2474"),sQuery(id+"F22.wireOp",EDGE,"E2475"),sQuery(id+"F22.wireOp",EDGE,"E2476"),sQuery(id+"F22.wireOp",EDGE,"E2477"),sQuery(id+"F22.wireOp",EDGE,"E2478"),sQuery(id+"F22.wireOp",EDGE,"E2479"),sQuery(id+"F22.wireOp",EDGE,"E2480"),sQuery(id+"F22.wireOp",EDGE,"E2481"),sQuery(id+"F22.wireOp",EDGE,"E2482"),sQuery(id+"F22.wireOp",EDGE,"E2483"),sQuery(id+"F22.wireOp",EDGE,"E2484"),sQuery(id+"F22.wireOp",EDGE,"E2485"),sQuery(id+"F22.wireOp",EDGE,"E2486"),sQuery(id+"F22.wireOp",EDGE,"E2487"),sQuery(id+"F22.wireOp",EDGE,"E2488"),sQuery(id+"F22.wireOp",EDGE,"E2489"),sQuery(id+"F22.wireOp",EDGE,"E2490"),sQuery(id+"F22.wireOp",EDGE,"E2491"),sQuery(id+"F22.wireOp",EDGE,"E2492"),sQuery(id+"F22.wireOp",EDGE,"E2493"),sQuery(id+"F22.wireOp",EDGE,"E2494"),sQuery(id+"F22.wireOp",EDGE,"E2495"),sQuery(id+"F22.wireOp",EDGE,"E2496"),sQuery(id+"F22.wireOp",EDGE,"E2497"),sQuery(id+"F22.wireOp",EDGE,"E2498"),sQuery(id+"F22.wireOp",EDGE,"E2499"),sQuery(id+"F22.wireOp",EDGE,"E2500"),sQuery(id+"F22.wireOp",EDGE,"E2501"),sQuery(id+"F22.wireOp",EDGE,"E2502"),sQuery(id+"F22.wireOp",EDGE,"E2503"),sQuery(id+"F22.wireOp",EDGE,"E2504"),sQuery(id+"F22.wireOp",EDGE,"E2505"),sQuery(id+"F22.wireOp",EDGE,"E2506"),sQuery(id+"F22.wireOp",EDGE,"E2507"),sQuery(id+"F22.wireOp",EDGE,"E2508"),sQuery(id+"F22.wireOp",EDGE,"E2509"),sQuery(id+"F22.wireOp",EDGE,"E2510"),sQuery(id+"F22.wireOp",EDGE,"E2511"),sQuery(id+"F22.wireOp",EDGE,"E2512"),sQuery(id+"F22.wireOp",EDGE,"E2513"),sQuery(id+"F22.wireOp",EDGE,"E2514"),sQuery(id+"F22.wireOp",EDGE,"E2515"),sQuery(id+"F22.wireOp",EDGE,"E2516"),sQuery(id+"F22.wireOp",EDGE,"E2517"),sQuery(id+"F22.wireOp",EDGE,"E2518"),sQuery(id+"F22.wireOp",EDGE,"E2519"),sQuery(id+"F22.wireOp",EDGE,"E2520"),sQuery(id+"F22.wireOp",EDGE,"E2521"),sQuery(id+"F22.wireOp",EDGE,"E2522"),sQuery(id+"F22.wireOp",EDGE,"E2523"),sQuery(id+"F22.wireOp",EDGE,"E2524"),sQuery(id+"F22.wireOp",EDGE,"E2525"),sQuery(id+"F22.wireOp",EDGE,"E2526"),sQuery(id+"F22.wireOp",EDGE,"E2527"),sQuery(id+"F22.wireOp",EDGE,"E2528"),sQuery(id+"F22.wireOp",EDGE,"E2529"),sQuery(id+"F22.wireOp",EDGE,"E2530"),sQuery(id+"F22.wireOp",EDGE,"E2531"),sQuery(id+"F22.wireOp",EDGE,"E2532"),sQuery(id+"F22.wireOp",EDGE,"E2533"),sQuery(id+"F22.wireOp",EDGE,"E2534"),sQuery(id+"F22.wireOp",EDGE,"E2535"),sQuery(id+"F22.wireOp",EDGE,"E2536"),sQuery(id+"F22.wireOp",EDGE,"E2537"),sQuery(id+"F22.wireOp",EDGE,"E2538"),sQuery(id+"F22.wireOp",EDGE,"E2539"),sQuery(id+"F22.wireOp",EDGE,"E2540"),sQuery(id+"F22.wireOp",EDGE,"E2541"),sQuery(id+"F22.wireOp",EDGE,"E2542"),sQuery(id+"F22.wireOp",EDGE,"E2543"),sQuery(id+"F22.wireOp",EDGE,"E2544"),sQuery(id+"F22.wireOp",EDGE,"E2545"),sQuery(id+"F22.wireOp",EDGE,"E2546"),sQuery(id+"F22.wireOp",EDGE,"E2547"),sQuery(id+"F22.wireOp",EDGE,"E2548"),sQuery(id+"F22.wireOp",EDGE,"E2549"),sQuery(id+"F22.wireOp",EDGE,"E2550"),sQuery(id+"F22.wireOp",EDGE,"E2551"),sQuery(id+"F22.wireOp",EDGE,"E2552"),sQuery(id+"F22.wireOp",EDGE,"E2553"),sQuery(id+"F22.wireOp",EDGE,"E2554"),sQuery(id+"F22.wireOp",EDGE,"E2555"),sQuery(id+"F22.wireOp",EDGE,"E2556"),sQuery(id+"F22.wireOp",EDGE,"E2557"),sQuery(id+"F22.wireOp",EDGE,"E2558"),sQuery(id+"F22.wireOp",EDGE,"E2559"),sQuery(id+"F22.wireOp",EDGE,"E2560"),sQuery(id+"F22.wireOp",EDGE,"E2561"),sQuery(id+"F22.wireOp",EDGE,"E2562"),sQuery(id+"F22.wireOp",EDGE,"E2563"),sQuery(id+"F22.wireOp",EDGE,"E2564"),sQuery(id+"F22.wireOp",EDGE,"E2565"),sQuery(id+"F22.wireOp",EDGE,"E2566"),sQuery(id+"F22.wireOp",EDGE,"E2567"),sQuery(id+"F22.wireOp",EDGE,"E2568"),sQuery(id+"F22.wireOp",EDGE,"E2569"),sQuery(id+"F22.wireOp",EDGE,"E2570"),sQuery(id+"F22.wireOp",EDGE,"E2571"),sQuery(id+"F22.wireOp",EDGE,"E2572"),sQuery(id+"F22.wireOp",EDGE,"E2573"),sQuery(id+"F22.wireOp",EDGE,"E2574"),sQuery(id+"F22.wireOp",EDGE,"E2575"),sQuery(id+"F22.wireOp",EDGE,"E2576"),sQuery(id+"F22.wireOp",EDGE,"E2577"),sQuery(id+"F22.wireOp",EDGE,"E2578"),sQuery(id+"F22.wireOp",EDGE,"E2579"),sQuery(id+"F22.wireOp",EDGE,"E2580"),sQuery(id+"F22.wireOp",EDGE,"E2581"),sQuery(id+"F22.wireOp",EDGE,"E2582"),sQuery(id+"F22.wireOp",EDGE,"E2583"),sQuery(id+"F22.wireOp",EDGE,"E2584"),sQuery(id+"F22.wireOp",EDGE,"E2585"),sQuery(id+"F22.wireOp",EDGE,"E2586"),sQuery(id+"F22.wireOp",EDGE,"E2587"),sQuery(id+"F22.wireOp",EDGE,"E2588"),sQuery(id+"F22.wireOp",EDGE,"E2589"),sQuery(id+"F22.wireOp",EDGE,"E2590"),sQuery(id+"F22.wireOp",EDGE,"E2591"),sQuery(id+"F22.wireOp",EDGE,"E2592"),sQuery(id+"F22.wireOp",EDGE,"E2593"),sQuery(id+"F22.wireOp",EDGE,"E2594"),sQuery(id+"F22.wireOp",EDGE,"E2595"),sQuery(id+"F22.wireOp",EDGE,"E2596"),sQuery(id+"F22.wireOp",EDGE,"E2597"),sQuery(id+"F22.wireOp",EDGE,"E2598"),sQuery(id+"F22.wireOp",EDGE,"E2599"),sQuery(id+"F22.wireOp",EDGE,"E2600"),sQuery(id+"F22.wireOp",EDGE,"E2601"),sQuery(id+"F22.wireOp",EDGE,"E2602"),sQuery(id+"F22.wireOp",EDGE,"E2603"),sQuery(id+"F22.wireOp",EDGE,"E2604"),sQuery(id+"F22.wireOp",EDGE,"E2605"),sQuery(id+"F22.wireOp",EDGE,"E2606"),sQuery(id+"F22.wireOp",EDGE,"E2607"),sQuery(id+"F22.wireOp",EDGE,"E2608"),sQuery(id+"F22.wireOp",EDGE,"E2609"),sQuery(id+"F22.wireOp",EDGE,"E2610"),sQuery(id+"F22.wireOp",EDGE,"E2611"),sQuery(id+"F22.wireOp",EDGE,"E2612"),sQuery(id+"F22.wireOp",EDGE,"E2613"),sQuery(id+"F22.wireOp",EDGE,"E2614"),sQuery(id+"F22.wireOp",EDGE,"E2615"),sQuery(id+"F22.wireOp",EDGE,"E2616"),sQuery(id+"F22.wireOp",EDGE,"E2617"),sQuery(id+"F22.wireOp",EDGE,"E2618"),sQuery(id+"F22.wireOp",EDGE,"E2619"),sQuery(id+"F22.wireOp",EDGE,"E2620"),sQuery(id+"F22.wireOp",EDGE,"E2621"),sQuery(id+"F22.wireOp",EDGE,"E2622"),sQuery(id+"F22.wireOp",EDGE,"E2623"),sQuery(id+"F22.wireOp",EDGE,"E2624"),sQuery(id+"F22.wireOp",EDGE,"E2625"),sQuery(id+"F22.wireOp",EDGE,"E2626"),sQuery(id+"F22.wireOp",EDGE,"E2627"),sQuery(id+"F22.wireOp",EDGE,"E2628"),sQuery(id+"F22.wireOp",EDGE,"E2629"),sQuery(id+"F22.wireOp",EDGE,"E2630"),sQuery(id+"F22.wireOp",EDGE,"E2631"),sQuery(id+"F22.wireOp",EDGE,"E2632"),sQuery(id+"F22.wireOp",EDGE,"E2633"),sQuery(id+"F22.wireOp",EDGE,"E2634"),sQuery(id+"F22.wireOp",EDGE,"E2635"),sQuery(id+"F22.wireOp",EDGE,"E2636"),sQuery(id+"F22.wireOp",EDGE,"E2637"),sQuery(id+"F22.wireOp",EDGE,"E2638"),sQuery(id+"F22.wireOp",EDGE,"E2639"),sQuery(id+"F22.wireOp",EDGE,"E2640"),sQuery(id+"F22.wireOp",EDGE,"E2641"),sQuery(id+"F22.wireOp",EDGE,"E2642"),sQuery(id+"F22.wireOp",EDGE,"E2643"),sQuery(id+"F22.wireOp",EDGE,"E2644"),sQuery(id+"F22.wireOp",EDGE,"E2645"),sQuery(id+"F22.wireOp",EDGE,"E2646"),sQuery(id+"F22.wireOp",EDGE,"E2647"),sQuery(id+"F22.wireOp",EDGE,"E2648"),sQuery(id+"F22.wireOp",EDGE,"E2649"),sQuery(id+"F22.wireOp",EDGE,"E2650"),sQuery(id+"F22.wireOp",EDGE,"E2651"),sQuery(id+"F22.wireOp",EDGE,"E2652"),sQuery(id+"F22.wireOp",EDGE,"E2653"),sQuery(id+"F22.wireOp",EDGE,"E2654"),sQuery(id+"F22.wireOp",EDGE,"E2655"),sQuery(id+"F22.wireOp",EDGE,"E2656"),sQuery(id+"F22.wireOp",EDGE,"E2657"),sQuery(id+"F22.wireOp",EDGE,"E2658"),sQuery(id+"F22.wireOp",EDGE,"E2659"),sQuery(id+"F22.wireOp",EDGE,"E2660"),sQuery(id+"F22.wireOp",EDGE,"E2661"),sQuery(id+"F22.wireOp",EDGE,"E2662"),sQuery(id+"F22.wireOp",EDGE,"E2663"),sQuery(id+"F22.wireOp",EDGE,"E2664"),sQuery(id+"F22.wireOp",EDGE,"E2665"),sQuery(id+"F22.wireOp",EDGE,"E2666"),sQuery(id+"F22.wireOp",EDGE,"E2667"),sQuery(id+"F22.wireOp",EDGE,"E2668"),sQuery(id+"F22.wireOp",EDGE,"E2669"),sQuery(id+"F22.wireOp",EDGE,"E2670")])],"isStart":true})]});
            var sketch = newSketch(context, id + "F26", { "sketchPlane" : qUnion([Q0])});
            skLineSegment(sketch, "E2675", {"start": v(-76.2, 69.85) * mm, "end": v(75.52, 69.85) * mm});
            skLineSegment(sketch, "E2676", {"start": v(75.52, 69.85) * mm, "end": v(75.52, 59.7) * mm});
            skLineSegment(sketch, "E2677", {"start": v(75.52, 59.7) * mm, "end": v(-76.2, 59.7) * mm});
            skLineSegment(sketch, "E2678", {"start": v(-76.2, 59.7) * mm, "end": v(-76.2, 69.85) * mm});
            skSolve(sketch);
        }
        {
            var Q0;
            Q0 = qSketchRegion(id + "F26", true);
            extrude(context, id + "F27", {"entities" : qUnion([Q0]), "operationType" : NewBodyOperationType.REMOVE, "oppositeDirection" : true, "depth" : 6.35 * mm, "offsetDistance" : 25.4 * mm});
        }
    });
